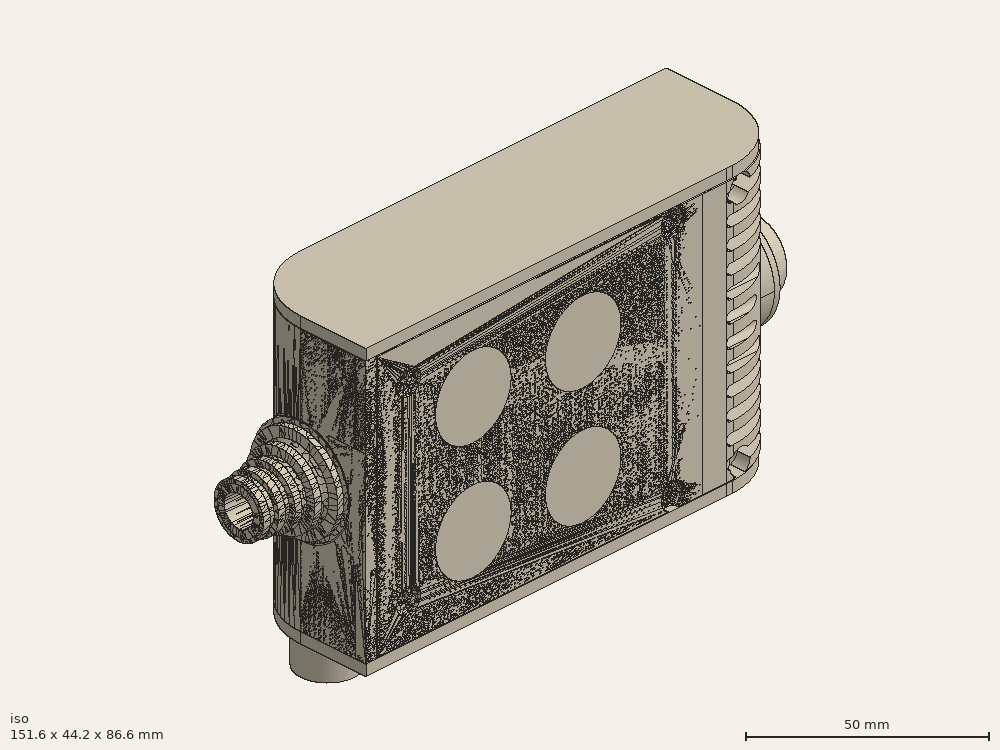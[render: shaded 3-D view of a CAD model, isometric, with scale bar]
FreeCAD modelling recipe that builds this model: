
FCSTD DOCUMENT  (FreeCAD 0.19R0.19.2)
Label: enclosure_208FCStd
License: All rights reserved
LicenseURL: http://en.wikipedia.org/wiki/All_rights_reserved
objects: Part::Revolution×152, Part::MultiFuse×146, Part::Feature×146, Sketcher::SketchObject×84, Part::Cut×71, Part::Cylinder×70, Part::Extrusion×69, Part::Fillet×58, Part::Box×36, App::MeasureDistance×4, Part::FeaturePython×2, Image::ImagePlane×1, PartDesign::Body×1, Part::Mirroring×1
note: 836 computed .brp shape members not serialized (recipe doc carries the construction recipe); baked Part::Feature solids carry a one-line shape summary decoded from their .brp

FEATURE [Sketcher::SketchObject] Sketch  label="topSketch"
  FullyConstrained = true
  sketch-geometry (20):
    g0: LineSegment StartX=5.21097e-06 StartY=3 StartZ=0 EndX=5.21097e-06 EndY=19 EndZ=0
    g1: ArcOfCircle CenterX=19 CenterY=19 CenterZ=0 NormalX=0 NormalY=0 NormalZ=1 AngleXU=0 Radius=19 StartAngle=1.5708 EndAngle=3.14159
    g2: ArcOfCircle CenterX=19 CenterY=19 CenterZ=0 NormalX=0 NormalY=0 NormalZ=1 AngleXU=0 Radius=16 StartAngle=1.5708 EndAngle=3.14159
    g3: LineSegment StartX=114 StartY=35 StartZ=0 EndX=19 EndY=35 EndZ=0
    g4: LineSegment StartX=5.21097e-06 StartY=3 StartZ=0 EndX=5.21097e-06 EndY=0 EndZ=0
    g5: LineSegment StartX=3 StartY=0 StartZ=0 EndX=5.21097e-06 EndY=0 EndZ=0
    g6: LineSegment StartX=3 StartY=19 StartZ=0 EndX=3 EndY=0 EndZ=0
    g7: LineSegment StartX=19 StartY=38 StartZ=0 EndX=124 EndY=38 EndZ=0
    g8: Circle CenterX=119 CenterY=35 CenterZ=0 NormalX=0 NormalY=0 NormalZ=1 AngleXU=0 Radius=1
    g9: Circle CenterX=121 CenterY=35 CenterZ=0 NormalX=0 NormalY=0 NormalZ=1 AngleXU=0 Radius=1
    g10: Circle CenterX=121 CenterY=33 CenterZ=0 NormalX=0 NormalY=0 NormalZ=1 AngleXU=0 Radius=1
    g11: BSplineCurve PolesCount=3 KnotsCount=2 Degree=2 IsPeriodic=0
    g12: GeomPoint X=119 Y=35 Z=0
    g13: GeomPoint X=121 Y=33 Z=0
    g14: LineSegment StartX=119 StartY=35 StartZ=0 EndX=114 EndY=35 EndZ=0
    g15: ArcOfCircle CenterX=105 CenterY=19 CenterZ=0 NormalX=0 NormalY=0 NormalZ=1 AngleXU=0 Radius=19 StartAngle=5.7297 EndAngle=6.28319
    g16: ArcOfCircle CenterX=105 CenterY=19 CenterZ=0 NormalX=0 NormalY=0 NormalZ=1 AngleXU=0 Radius=16 StartAngle=5.60905 EndAngle=6.28319
    g17: LineSegment StartX=121 StartY=33 StartZ=0 EndX=121 EndY=19 EndZ=0
    g18: LineSegment StartX=124 StartY=38 StartZ=0 EndX=124 EndY=19 EndZ=0
    g19: LineSegment StartX=117.5 StartY=9.01251 StartZ=0 EndX=121.163 EndY=9.0125 EndZ=0
  constraints (46):
    c: Vertical(g0)
    c: Block(g0)
    c: Coincident(g1,g0)
    c: Block(g1)
    c: Coincident(g2,g1)
    c: Block(g2)
    c: Coincident(g3,g2)
    c: Horizontal(g3)
    c: Tangent(g3,g2)
    c: Coincident(g4,g0)
    c: Distance(g4) = 3
    c: Vertical(g4)
    c: Coincident(g5,g4)
    c: Horizontal(g5)
    c: Coincident(g6,g2)
    c: Coincident(g6,g5)
    c: Vertical(g6)
    c: Horizontal(g7)
    c: Distance(g7) = 105
    c: Coincident(g7,g1)
    c: Block(g3)
    c: Weight(g8) = 1
    c: Equal(g8,g9)
    c: Equal(g8,g10)
    c: InternalAlignment(g8,g11)
    c: InternalAlignment(g9,g11)
    c: InternalAlignment(g10,g11)
    c: InternalAlignment(g12,g11)
    c: InternalAlignment(g13,g11)
    c: Block(g11)
    c: Coincident(g14,g11)
    c: Coincident(g14,g3)
    c: Horizontal(g14)
    c: Block(g15)
    c: Coincident(g16,g15)
    c: Block(g16)
    c: Coincident(g17,g11)
    c: Coincident(g17,g16)
    c: Vertical(g17)
    c: Distance(g17) = 14
    c: Coincident(g18,g7)
    c: Coincident(g18,g15)
    c: Vertical(g18)
    c: Distance(g18) = 19
    c: Coincident(g19,g16)
    c: Coincident(g19,g15)
FEATURE [Sketcher::SketchObject] Sketch001  label="bottomSketch"
  FullyConstrained = true
  sketch-geometry (32):
    g0: LineSegment StartX=3.3 StartY=-6.03275e-07 StartZ=0 EndX=98 EndY=-6.03275e-07 EndZ=0
    g1: ArcOfCircle CenterX=98 CenterY=19 CenterZ=0 NormalX=0 NormalY=0 NormalZ=1 AngleXU=0 Radius=19 StartAngle=4.71239 EndAngle=5.71103
    g2: LineSegment StartX=6.3 StartY=8 StartZ=0 EndX=3.3 EndY=8 EndZ=0
    g3: LineSegment StartX=3.3 StartY=8 StartZ=0 EndX=3.3 EndY=-6.03275e-07 EndZ=0
    g4: ArcOfCircle CenterX=8.3 CenterY=5 CenterZ=0 NormalX=0 NormalY=0 NormalZ=1 AngleXU=0 Radius=2 StartAngle=3.14159 EndAngle=4.71239
    g5: LineSegment StartX=6.3 StartY=8 StartZ=0 EndX=6.3 EndY=5 EndZ=0
    g6: ArcOfCircle CenterX=98 CenterY=19 CenterZ=0 NormalX=0 NormalY=0 NormalZ=1 AngleXU=0 Radius=12.7 StartAngle=4.71239 EndAngle=6.28319
    g7: LineSegment StartX=94.7 StartY=3 StartZ=0 EndX=8.3 EndY=3 EndZ=0
    g8-g12: Circle x5 (B-spline internal-alignment scaffolding for g13; pole/knot coordinates omitted)
    g13: BSplineCurve PolesCount=5 KnotsCount=3 Degree=3 IsPeriodic=0
    g14: GeomPoint X=98 Y=6.3 Z=0
    g15: GeomPoint X=96.3938 Y=4.71946 Z=0
    g16: GeomPoint X=94.7 Y=3 Z=0
    g17-g23: Circle x7 (B-spline internal-alignment scaffolding for g24; pole/knot coordinates omitted)
    g24: BSplineCurve PolesCount=7 KnotsCount=5 Degree=3 IsPeriodic=0
    g25-g29: GeomPoint x5 (B-spline internal-alignment scaffolding for g24; pole/knot coordinates omitted)
    g30: ArcOfCircle CenterX=98 CenterY=19 CenterZ=0 NormalX=0 NormalY=0 NormalZ=1 AngleXU=0 Radius=15.7 StartAngle=5.81226 EndAngle=6.28319
    g31: LineSegment StartX=110.7 StartY=19 StartZ=0 EndX=113.7 EndY=19 EndZ=0
  constraints (41):
    c: Horizontal(g0)
    c: Coincident(g1,g0)
    c: Block(g1)
    c: Horizontal(g2)
    c: Distance(g2) = 3
    c: Coincident(g3,g2)
    c: Vertical(g3)
    c: Coincident(g3,g0)
    c: Block(g4)
    c: Block(g2)
    c: Coincident(g5,g2)
    c: Coincident(g5,g4)
    c: Vertical(g5)
    c: Coincident(g6,g1)
    c: Block(g6)
    c: Coincident(g7,g4)
    c: Horizontal(g7)
    c: Block(g0)
    c: Block(g7)
    c: Block(g3)
    c: Coincident(g13,g6)
    c: Weight(g8) = 1
    c: Equal(g8, g9-g12) x4
    c: Coincident(g13,g7)
    c: InternalAlignment(g8-g12 -> g13) x5
    c: InternalAlignment(g14,g13)
    c: InternalAlignment(g15,g13)
    c: InternalAlignment(g16,g13)
    c: Block(g13)
    c: Weight(g17) = 1
    c: Equal(g17, g18-g23) x6
    c: Coincident(g24,g1)
    c: InternalAlignment(g17-g23 -> g24) x7
    c: InternalAlignment(g25-g29 -> g24) x5
    c: Block(g24)
    c: Coincident(g30,g24)
    c: Coincident(g31,g6)
    c: Coincident(g31,g30)
    c: Horizontal(g31)
    c: Block(g31)
    c: Block(g30)
FEATURE [Part::Extrusion] Extrude  label="top"
  Base = -> Sketch
  Dir = (0,0,1)
  DirMode = 2
  FaceMakerClass = Part::FaceMakerBullseye
  LengthFwd = 72
  LengthRev = 0
  Solid = true
  Symmetric = false
FEATURE [Part::Extrusion] Extrude001  label="bottom"
  Base = -> Sketch001
  Dir = (0,0,1)
  DirMode = 2
  FaceMakerClass = Part::FaceMakerBullseye
  LengthFwd = 71.4
  LengthRev = 0
  Placement = pos=(0,0,0.3) rot=(0,0,1;0rad)
  Solid = true
  Symmetric = false
FEATURE [Sketcher::SketchObject] Sketch002  label="topSketch001"
  FullyConstrained = true
  sketch-geometry (8):
    g0: ArcOfCircle CenterX=19 CenterY=19.0975 CenterZ=0 NormalX=0 NormalY=0 NormalZ=1 AngleXU=0 Radius=18.9025 StartAngle=1.5708 EndAngle=3.14674
    g1: LineSegment StartX=0.0977805 StartY=19.0003 StartZ=0 EndX=0.0977805 EndY=0.000251602 EndZ=0
    g2: LineSegment StartX=19 StartY=38 StartZ=0 EndX=124 EndY=38 EndZ=0
    g3: LineSegment StartX=0.0977805 StartY=0.000251602 StartZ=0 EndX=105.098 EndY=0.000251602 EndZ=0
    g4: LineSegment StartX=124 StartY=38 StartZ=0 EndX=125.616 EndY=38 EndZ=0
    g5: LineSegment StartX=105.098 StartY=0.000251602 StartZ=0 EndX=106.713 EndY=0.000251602 EndZ=0
    g6: ArcOfCircle CenterX=106.616 CenterY=19 CenterZ=0 NormalX=0 NormalY=0 NormalZ=1 AngleXU=0 Radius=19 StartAngle=4.71754 EndAngle=6.28319
    g7: LineSegment StartX=125.616 StartY=38 StartZ=0 EndX=125.616 EndY=19 EndZ=0
  constraints (21):
    c: Block(g0)
    c: Coincident(g1,g0)
    c: Vertical(g1)
    c: Horizontal(g2)
    c: Distance(g2) = 105
    c: Coincident(g2,g0)
    c: Distance(g1) = 19
    c: Coincident(g3,g1)
    c: Horizontal(g3)
    c: Distance(g3) = 105
    c: Coincident(g4,g2)
    c: Horizontal(g4)
    c: Distance(g4) = 1.61553
    c: Horizontal(g5)
    c: Equal(g4,g5) = 1.61553
    c: Coincident(g5,g3)
    c: Block(g6)
    c: Coincident(g6,g5)
    c: Coincident(g7,g4)
    c: Coincident(g7,g6)
    c: Vertical(g7)
FEATURE [Part::Extrusion] Extrude002  label="sideA"
  Base = -> Sketch002
  Dir = (0,0,1)
  DirMode = 2
  FaceMakerClass = Part::FaceMakerBullseye
  LengthFwd = 3
  LengthRev = 0
  Placement = pos=(0,0,-3) rot=(0,0,1;0rad)
  Solid = true
  Symmetric = false
FEATURE [Sketcher::SketchObject] Sketch003  label="topSketch002"
  FullyConstrained = true
  sketch-geometry (6):
    g0: LineSegment StartX=19 StartY=38 StartZ=0 EndX=117 EndY=38 EndZ=0
    g1: ArcOfCircle CenterX=19 CenterY=19 CenterZ=0 NormalX=0 NormalY=0 NormalZ=1 AngleXU=0 Radius=19 StartAngle=1.5708 EndAngle=3.14159
    g2: LineSegment StartX=117 StartY=38 StartZ=0 EndX=117 EndY=19 EndZ=0
    g3: LineSegment StartX=98 StartY=1.0161e-12 StartZ=0 EndX=5.22862e-06 EndY=1.0161e-12 EndZ=0
    g4: LineSegment StartX=5.22862e-06 StartY=19 StartZ=0 EndX=5.22862e-06 EndY=1.0161e-12 EndZ=0
    g5: ArcOfCircle CenterX=98 CenterY=19 CenterZ=0 NormalX=0 NormalY=0 NormalZ=1 AngleXU=0 Radius=19 StartAngle=4.71239 EndAngle=6.28319
  constraints (16):
    c: Horizontal(g0)
    c: Distance(g0) = 98
    c: Coincident(g1,g0)
    c: Block(g1)
    c: Coincident(g2,g0)
    c: Vertical(g2)
    c: Distance(g2) = 19
    c: Horizontal(g3)
    c: Coincident(g4,g1)
    c: Vertical(g4)
    c: Coincident(g3,g4)
    c: Block(g3)
    c: Coincident(g5,g2)
    c: Coincident(g5,g3)
    c: Block(g0)
    c: Block(g5)
FEATURE [Sketcher::SketchObject] Sketch004
  FullyConstrained = true
  MapMode = 3
  Placement = pos=(0,0,0) rot=(1,0,0;1.5708rad)
  Support = -> [Extrude]
  sketch-geometry (8):
    g0: Circle CenterX=80.351 CenterY=-67.6202 CenterZ=0 NormalX=0 NormalY=0 NormalZ=1 AngleXU=0 Radius=2
    g1: Circle CenterX=80.351 CenterY=-67.6202 CenterZ=0 NormalX=0 NormalY=0 NormalZ=1 AngleXU=0 Radius=3
    g2: Circle CenterX=80.351 CenterY=-4.92017 CenterZ=0 NormalX=0 NormalY=0 NormalZ=1 AngleXU=0 Radius=2
    g3: Circle CenterX=80.351 CenterY=-4.92017 CenterZ=0 NormalX=0 NormalY=0 NormalZ=1 AngleXU=0 Radius=3
    g4: Circle CenterX=23.851 CenterY=-4.92017 CenterZ=0 NormalX=0 NormalY=0 NormalZ=1 AngleXU=0 Radius=2
    g5: Circle CenterX=23.851 CenterY=-4.92017 CenterZ=0 NormalX=0 NormalY=0 NormalZ=1 AngleXU=0 Radius=3
    g6: Circle CenterX=23.851 CenterY=-67.6202 CenterZ=0 NormalX=0 NormalY=0 NormalZ=1 AngleXU=0 Radius=2
    g7: Circle CenterX=23.851 CenterY=-67.6202 CenterZ=0 NormalX=0 NormalY=0 NormalZ=1 AngleXU=0 Radius=3
  constraints (8):
    c: Block(g3)
    c: Block(g2)
    c: Block(g1)
    c: Block(g0)
    c: Block(g6)
    c: Block(g7)
    c: Block(g4)
    c: Block(g5)
FEATURE [Part::Extrusion] Extrude004
  Base = -> Sketch004
  Dir = (0,-1,2e-16)
  DirMode = 2
  FaceMakerClass = Part::FaceMakerBullseye
  LengthFwd = 6
  LengthRev = 0
  Placement = pos=(0,9,0) rot=(0,0,1;0rad)
  Solid = true
  Symmetric = false
FEATURE [Sketcher::SketchObject] Sketch005
  FullyConstrained = true
  MapMode = 3
  Placement = pos=(0,0,0) rot=(1,0,0;1.5708rad)
  Support = -> [Extrude]
  sketch-geometry (8):
    g0: Circle CenterX=80.351 CenterY=-67.6202 CenterZ=0 NormalX=0 NormalY=0 NormalZ=1 AngleXU=0 Radius=3
    g1: Circle CenterX=80.351 CenterY=-4.92017 CenterZ=0 NormalX=0 NormalY=0 NormalZ=1 AngleXU=0 Radius=3
    g2: Circle CenterX=23.851 CenterY=-4.92017 CenterZ=0 NormalX=0 NormalY=0 NormalZ=1 AngleXU=0 Radius=3
    g3: Circle CenterX=23.851 CenterY=-67.6202 CenterZ=0 NormalX=0 NormalY=0 NormalZ=1 AngleXU=0 Radius=3
    g4: Circle CenterX=23.851 CenterY=-67.6202 CenterZ=0 NormalX=0 NormalY=0 NormalZ=1 AngleXU=0 Radius=5
    g5: Circle CenterX=80.351 CenterY=-67.6202 CenterZ=0 NormalX=0 NormalY=0 NormalZ=1 AngleXU=0 Radius=5
    g6: Circle CenterX=23.851 CenterY=-4.92017 CenterZ=0 NormalX=0 NormalY=0 NormalZ=1 AngleXU=0 Radius=5
    g7: Circle CenterX=80.351 CenterY=-4.92017 CenterZ=0 NormalX=0 NormalY=0 NormalZ=1 AngleXU=0 Radius=5
  constraints (8):
    c: Block(g1)
    c: Block(g0)
    c: Block(g3)
    c: Block(g2)
    c: Block(g5)
    c: Block(g4)
    c: Block(g6)
    c: Block(g7)
FEATURE [Part::Extrusion] Extrude005
  Base = -> Sketch005
  Dir = (0,-1,2e-16)
  DirMode = 2
  FaceMakerClass = Part::FaceMakerBullseye
  LengthFwd = 2
  LengthRev = 0
  Solid = true
  Symmetric = false
FEATURE [Sketcher::SketchObject] Sketch006
  FullyConstrained = true
  MapMode = 3
  Placement = pos=(0,0,0) rot=(1,0,0;1.5708rad)
  sketch-geometry (8):
    g0: Circle CenterX=80.351 CenterY=-67.6202 CenterZ=0 NormalX=0 NormalY=0 NormalZ=1 AngleXU=0 Radius=3
    g1: Circle CenterX=80.351 CenterY=-4.92017 CenterZ=0 NormalX=0 NormalY=0 NormalZ=1 AngleXU=0 Radius=3
    g2: Circle CenterX=23.851 CenterY=-4.92017 CenterZ=0 NormalX=0 NormalY=0 NormalZ=1 AngleXU=0 Radius=3
    g3: Circle CenterX=23.851 CenterY=-67.6202 CenterZ=0 NormalX=0 NormalY=0 NormalZ=1 AngleXU=0 Radius=3
    g4: Circle CenterX=23.851 CenterY=-67.6202 CenterZ=0 NormalX=0 NormalY=0 NormalZ=1 AngleXU=0 Radius=5
    g5: Circle CenterX=80.351 CenterY=-67.6202 CenterZ=0 NormalX=0 NormalY=0 NormalZ=1 AngleXU=0 Radius=5
    g6: Circle CenterX=23.851 CenterY=-4.92017 CenterZ=0 NormalX=0 NormalY=0 NormalZ=1 AngleXU=0 Radius=5
    g7: Circle CenterX=80.351 CenterY=-4.92017 CenterZ=0 NormalX=0 NormalY=0 NormalZ=1 AngleXU=0 Radius=5
  constraints (8):
    c: Block(g1)
    c: Block(g0)
    c: Block(g3)
    c: Block(g2)
    c: Block(g5)
    c: Block(g4)
    c: Block(g6)
    c: Block(g7)
FEATURE [Part::Extrusion] Extrude007
  Base = -> Sketch006
  Dir = (0,-1,2e-16)
  DirMode = 2
  FaceMakerClass = Part::FaceMakerBullseye
  LengthFwd = 2
  LengthRev = 0
  Solid = true
  Symmetric = false
FEATURE [Part::Fillet] Fillet
  Base = -> Extrude007
  Edges = 4 edges r=1.99: [Edge6,Edge12,Edge18,Edge24]
FEATURE [Part::Cut] Cut
  Base = -> Extrude005
  Placement = pos=(0,5,0) rot=(0,0,1;0rad)
  Tool = -> Fillet
FEATURE [Part::MultiFuse] Fusion  label="pCBScrews"
  Placement = pos=(-2.5,0,72.3) rot=(0,0,1;0rad)
  Shapes = -> [Extrude004,Cut]
FEATURE [App::MeasureDistance] Distance  label="Distance: 0.69 mm"
  Distance = 0.685967
  P1 = (24.0138,2.9647,0.3)
  P2 = (23.8901,3,-0.373787)
FEATURE [App::MeasureDistance] Distance001  label="Distance: 0.53 mm"
  Distance = 0.533607
  P1 = (80.2939,3,72.2334)
  P2 = (80.281,2.99661,71.7)
FEATURE [Part::Fillet] Fillet001
  Base = -> Extrude001
  Edges = 1 edges r=2.4: [Edge17]
FEATURE [Part::Fillet] Fillet002  label="bottom001"
  Base = -> Fillet001
  Edges = 1 edges r=2.4: [Edge36]
FEATURE [Part::Fillet] Fillet003  label="top001"
  Base = -> Extrude
  Edges = 1 edges r=2: [Edge1]
FEATURE [Sketcher::SketchObject] Sketch007
  FullyConstrained = true
  sketch-geometry (16):
    g0: LineSegment StartX=4 StartY=0 StartZ=0 EndX=4 EndY=2.4 EndZ=0
    g1: LineSegment StartX=4 StartY=2.4 StartZ=0 EndX=7 EndY=2.4 EndZ=0
    g2: LineSegment StartX=4 StartY=0 StartZ=0 EndX=5.7 EndY=0 EndZ=0
    g3: LineSegment StartX=5.7 StartY=0 StartZ=0 EndX=5.7 EndY=-5.6 EndZ=0
    g4-g8: Circle x5 (B-spline internal-alignment scaffolding for g9; pole/knot coordinates omitted)
    g9: BSplineCurve PolesCount=5 KnotsCount=3 Degree=3 IsPeriodic=0
    g10: GeomPoint X=7 Y=2.4 Z=0
    g11: GeomPoint X=10.4582 Y=-1.55472 Z=0
    g12: GeomPoint X=14 Y=-5.6 Z=0
    g13: LineSegment StartX=14 StartY=-5.6 StartZ=0 EndX=14 EndY=-14.1 EndZ=0
    g14: LineSegment StartX=14 StartY=-14.1 StartZ=0 EndX=6.5 EndY=-14.1 EndZ=0
    g15: LineSegment StartX=5.7 StartY=-5.6 StartZ=0 EndX=6.5 EndY=-14.1 EndZ=0
  constraints (28):
    c: Distance(g0) = 2.4
    c: Vertical(g0)
    c: Block(g0)
    c: Coincident(g1,g0)
    c: Horizontal(g1)
    c: Distance(g1) = 3
    c: Coincident(g2,g0)
    c: Horizontal(g2)
    c: Distance(g2) = 1.7
    c: Coincident(g3,g2)
    c: Vertical(g3)
    c: Distance(g3) = 5.6
    c: Coincident(g9,g1)
    c: Weight(g4) = 1
    c: Equal(g4, g5-g8) x4
    c: InternalAlignment(g4-g8 -> g9) x5
    c: InternalAlignment(g10,g9)
    c: InternalAlignment(g11,g9)
    c: InternalAlignment(g12,g9)
    c: Block(g9)
    c: Coincident(g13,g9)
    c: Vertical(g13)
    c: Distance(g13) = 8.5
    c: Coincident(g14,g13)
    c: Horizontal(g14)
    c: Distance(g14) = 7.5
    c: Coincident(g15,g3)
    c: Coincident(g15,g14)
FEATURE [Part::Feature] Face
  shape: bbox 10 x 16.5 x 2e-07 mm, 1 faces, 0 solids (baked)
FEATURE [Part::Revolution] Revolve  label="plugHousing"
  Angle = 360
  Axis = (0,1,0)
  Base = (0,0,0)
  FaceMakerClass = Part::FaceMakerBullseye
  Placement = pos=(0,0,36.15) rot=(0,0,1;0rad)
  Solid = false
  Source = -> Face
  Symmetric = false
FEATURE [Part::Feature] Face001
  shape: bbox 10 x 16.5 x 2e-07 mm, 1 faces, 0 solids (baked)
FEATURE [Part::Revolution] Revolve001  label="plugHousing001"
  Angle = 360
  Axis = (0,1,0)
  Base = (0,0,0)
  FaceMakerClass = Part::FaceMakerBullseye
  Placement = pos=(0,0,36.15) rot=(0,0,1;0rad)
  Solid = false
  Source = -> Face001
  Symmetric = false
FEATURE [Part::MultiFuse] Fusion001  label="plugHousing002"
  Placement = pos=(0,0,0) rot=(0,0,1;1.5708rad)
  Shapes = -> [Revolve001,Revolve]
FEATURE [Part::Feature] Face002
  shape: bbox 10 x 16.5 x 2e-07 mm, 1 faces, 0 solids (baked)
FEATURE [Part::Revolution] Revolve003  label="plugHousing005"
  Angle = 360
  Axis = (0,1,0)
  Base = (0,0,0)
  FaceMakerClass = Part::FaceMakerBullseye
  Placement = pos=(0,0,36.15) rot=(0,0,1;0rad)
  Solid = false
  Source = -> Face002
  Symmetric = false
FEATURE [Part::Feature] Face003
  shape: bbox 10 x 16.5 x 2e-07 mm, 1 faces, 0 solids (baked)
FEATURE [Part::Revolution] Revolve002  label="plugHousing003"
  Angle = 360
  Axis = (0,1,0)
  Base = (0,0,0)
  FaceMakerClass = Part::FaceMakerBullseye
  Placement = pos=(0,0,36.15) rot=(0,0,1;0rad)
  Solid = false
  Source = -> Face003
  Symmetric = false
FEATURE [Part::MultiFuse] Fusion002  label="plugHousing004"
  Placement = pos=(0,0,0) rot=(0,0,1;1.5708rad)
  Shapes = -> [Revolve002,Revolve003]
FEATURE [Part::MultiFuse] Fusion003  label="plugHousing006"
  Placement = pos=(0,19,0) rot=(0,0,1;3.14159rad)
  Shapes = -> [Fusion002,Fusion001]
FEATURE [Part::Feature] Face004
  shape: bbox 10 x 16.5 x 2e-07 mm, 1 faces, 0 solids (baked)
FEATURE [Part::Revolution] Revolve006  label="plugHousing010"
  Angle = 360
  Axis = (0,1,0)
  Base = (0,0,0)
  FaceMakerClass = Part::FaceMakerBullseye
  Placement = pos=(0,0,36.15) rot=(0,0,1;0rad)
  Solid = false
  Source = -> Face004
  Symmetric = false
FEATURE [Part::Feature] Face005
  shape: bbox 10 x 16.5 x 2e-07 mm, 1 faces, 0 solids (baked)
FEATURE [Part::Revolution] Revolve007  label="plugHousing011"
  Angle = 360
  Axis = (0,1,0)
  Base = (0,0,0)
  FaceMakerClass = Part::FaceMakerBullseye
  Placement = pos=(0,0,36.15) rot=(0,0,1;0rad)
  Solid = false
  Source = -> Face005
  Symmetric = false
FEATURE [Part::Feature] Face006
  shape: bbox 10 x 16.5 x 2e-07 mm, 1 faces, 0 solids (baked)
FEATURE [Part::Revolution] Revolve004  label="plugHousing007"
  Angle = 360
  Axis = (0,1,0)
  Base = (0,0,0)
  FaceMakerClass = Part::FaceMakerBullseye
  Placement = pos=(0,0,36.15) rot=(0,0,1;0rad)
  Solid = false
  Source = -> Face006
  Symmetric = false
FEATURE [Part::MultiFuse] Fusion004  label="plugHousing009"
  Placement = pos=(0,0,0) rot=(0,0,1;1.5708rad)
  Shapes = -> [Revolve004,Revolve007]
FEATURE [Part::Feature] Face007
  shape: bbox 10 x 16.5 x 2e-07 mm, 1 faces, 0 solids (baked)
FEATURE [Part::Revolution] Revolve005  label="plugHousing008"
  Angle = 360
  Axis = (0,1,0)
  Base = (0,0,0)
  FaceMakerClass = Part::FaceMakerBullseye
  Placement = pos=(0,0,36.15) rot=(0,0,1;0rad)
  Solid = false
  Source = -> Face007
  Symmetric = false
FEATURE [Part::MultiFuse] Fusion005  label="plugHousing012"
  Placement = pos=(0,0,0) rot=(0,0,1;1.5708rad)
  Shapes = -> [Revolve006,Revolve005]
FEATURE [Part::MultiFuse] Fusion006  label="plugHousing013"
  Placement = pos=(0,19,0) rot=(0,0,1;3.14159rad)
  Shapes = -> [Fusion005,Fusion004]
FEATURE [Part::MultiFuse] Fusion007  label="plugHousing014"
  Placement = pos=(122.621,0,-0.15) rot=(0,0,1;0rad)
  Shapes = -> [Fusion003,Fusion006]
FEATURE [Part::Cylinder] Cylinder002
  Angle = 360
  AttacherType = Attacher::AttachEngine3D
  Height = 20
  Placement = pos=(0,0,36.15) rot=(0,0,1;0rad)
  Radius = 4
FEATURE [Part::Cylinder] Cylinder003
  Angle = 360
  AttacherType = Attacher::AttachEngine3D
  Height = 10
  Placement = pos=(0,0,36.15) rot=(0,0,1;0rad)
  Radius = 4
FEATURE [Part::MultiFuse] Fusion009  label="removeToCreateHoleForPlugHousing"
  Placement = pos=(70,19,36.15) rot=(0,1,0;1.5708rad)
  Shapes = -> [Cylinder002,Cylinder003]
FEATURE [Part::Cylinder] Cylinder004
  Angle = 360
  AttacherType = Attacher::AttachEngine3D
  Height = 20
  Placement = pos=(0,0,36.15) rot=(0,0,1;0rad)
  Radius = 4
FEATURE [Part::Cylinder] Cylinder005
  Angle = 360
  AttacherType = Attacher::AttachEngine3D
  Height = 10
  Placement = pos=(0,0,36.15) rot=(0,0,1;0rad)
  Radius = 4
FEATURE [Part::MultiFuse] Fusion010  label="removeToCreateHoleForPlugHousing001"
  Placement = pos=(70,19,36.15) rot=(0,1,0;1.5708rad)
  Shapes = -> [Cylinder004,Cylinder005]
FEATURE [Part::Cut] Cut001
  Base = -> Fillet003
  Tool = -> Fusion010
FEATURE [Part::Cut] Cut002  label="Bottom"
  Base = -> Fillet002
  Tool = -> Fusion009
FEATURE [Part::Feature] Face008
  shape: bbox 10 x 16.5 x 2e-07 mm, 1 faces, 0 solids (baked)
FEATURE [Part::Revolution] Revolve011  label="plugHousing021"
  Angle = 360
  Axis = (0,1,0)
  Base = (0,0,0)
  FaceMakerClass = Part::FaceMakerBullseye
  Placement = pos=(0,0,36.15) rot=(0,0,1;0rad)
  Solid = false
  Source = -> Face008
  Symmetric = false
FEATURE [Part::Feature] Face009
  shape: bbox 10 x 16.5 x 2e-07 mm, 1 faces, 0 solids (baked)
FEATURE [Part::Revolution] Revolve012  label="plugHousing022"
  Angle = 360
  Axis = (0,1,0)
  Base = (0,0,0)
  FaceMakerClass = Part::FaceMakerBullseye
  Placement = pos=(0,0,36.15) rot=(0,0,1;0rad)
  Solid = false
  Source = -> Face009
  Symmetric = false
FEATURE [Part::Feature] Face010 .. Face013  x4 (patterned run collapsed; names and placements below)
  shape: bbox 10 x 16.5 x 2e-07 mm, 1 faces, 0 solids (baked)
FEATURE [Part::Revolution] Revolve015  label="plugHousing027"
  Angle = 360
  Axis = (0,1,0)
  Base = (0,0,0)
  FaceMakerClass = Part::FaceMakerBullseye
  Placement = pos=(0,0,36.15) rot=(0,0,1;0rad)
  Solid = false
  Source = -> Face013
  Symmetric = false
FEATURE [Part::Feature] Face014
  shape: bbox 10 x 16.5 x 2e-07 mm, 1 faces, 0 solids (baked)
FEATURE [Part::Feature] Face015
  shape: bbox 10 x 16.5 x 2e-07 mm, 1 faces, 0 solids (baked)
FEATURE [Part::Feature] Face016
  shape: bbox 10 x 16.5 x 2e-07 mm, 1 faces, 0 solids (baked)
FEATURE [Part::Revolution] Revolve019  label="plugHousing033"
  Angle = 360
  Axis = (0,1,0)
  Base = (0,0,0)
  FaceMakerClass = Part::FaceMakerBullseye
  Placement = pos=(0,0,36.15) rot=(0,0,1;0rad)
  Solid = false
  Source = -> Face016
  Symmetric = false
FEATURE [Part::Feature] Face017
  shape: bbox 10 x 16.5 x 2e-07 mm, 1 faces, 0 solids (baked)
FEATURE [Part::Revolution] Revolve020  label="plugHousing034"
  Angle = 360
  Axis = (0,1,0)
  Base = (0,0,0)
  FaceMakerClass = Part::FaceMakerBullseye
  Placement = pos=(0,0,36.15) rot=(0,0,1;0rad)
  Solid = false
  Source = -> Face017
  Symmetric = false
FEATURE [Part::Feature] Face018
  shape: bbox 10 x 16.5 x 2e-07 mm, 1 faces, 0 solids (baked)
FEATURE [Part::Revolution] Revolve016  label="plugHousing030"
  Angle = 360
  Axis = (0,1,0)
  Base = (0,0,0)
  FaceMakerClass = Part::FaceMakerBullseye
  Placement = pos=(0,0,36.15) rot=(0,0,1;0rad)
  Solid = false
  Source = -> Face018
  Symmetric = false
FEATURE [Part::MultiFuse] Fusion020  label="plugHousing038"
  Placement = pos=(0,0,0) rot=(0,0,1;1.5708rad)
  Shapes = -> [Revolve016,Revolve020]
FEATURE [Part::Feature] Face019
  shape: bbox 10 x 16.5 x 2e-07 mm, 1 faces, 0 solids (baked)
FEATURE [Part::Feature] Face020
  shape: bbox 10 x 16.5 x 2e-07 mm, 1 faces, 0 solids (baked)
FEATURE [Part::Revolution] Revolve017  label="plugHousing031"
  Angle = 360
  Axis = (0,1,0)
  Base = (0,0,0)
  FaceMakerClass = Part::FaceMakerBullseye
  Placement = pos=(0,0,36.15) rot=(0,0,1;0rad)
  Solid = false
  Source = -> Face020
  Symmetric = false
FEATURE [Part::MultiFuse] Fusion021  label="plugHousing039"
  Placement = pos=(0,0,0) rot=(0,0,1;1.5708rad)
  Shapes = -> [Revolve019,Revolve017]
FEATURE [Part::MultiFuse] Fusion023  label="plugHousing041"
  Placement = pos=(0,19,0) rot=(0,0,1;3.14159rad)
  Shapes = -> [Fusion021,Fusion020]
FEATURE [Part::Revolution] Revolve022  label="plugHousing043"
  Angle = 360
  Axis = (0,1,0)
  Base = (0,0,0)
  FaceMakerClass = Part::FaceMakerBullseye
  Placement = pos=(0,0,36.15) rot=(0,0,1;0rad)
  Solid = false
  Source = -> Face019
  Symmetric = false
FEATURE [Part::Feature] Face021
  shape: bbox 10 x 16.5 x 2e-07 mm, 1 faces, 0 solids (baked)
FEATURE [Part::Revolution] Revolve023  label="plugHousing044"
  Angle = 360
  Axis = (0,1,0)
  Base = (0,0,0)
  FaceMakerClass = Part::FaceMakerBullseye
  Placement = pos=(0,0,36.15) rot=(0,0,1;0rad)
  Solid = false
  Source = -> Face021
  Symmetric = false
FEATURE [Part::Feature] Face022
  shape: bbox 10 x 16.5 x 2e-07 mm, 1 faces, 0 solids (baked)
FEATURE [Part::Revolution] Revolve018  label="plugHousing032"
  Angle = 360
  Axis = (0,1,0)
  Base = (0,0,0)
  FaceMakerClass = Part::FaceMakerBullseye
  Placement = pos=(0,0,36.15) rot=(0,0,1;0rad)
  Solid = false
  Source = -> Face022
  Symmetric = false
FEATURE [Part::MultiFuse] Fusion022  label="plugHousing040"
  Placement = pos=(0,0,0) rot=(0,0,1;1.5708rad)
  Shapes = -> [Revolve018,Revolve023]
FEATURE [Part::Feature] Face023
  shape: bbox 10 x 16.5 x 2e-07 mm, 1 faces, 0 solids (baked)
FEATURE [Part::Revolution] Revolve021  label="plugHousing035"
  Angle = 360
  Axis = (0,1,0)
  Base = (0,0,0)
  FaceMakerClass = Part::FaceMakerBullseye
  Placement = pos=(0,0,36.15) rot=(0,0,1;0rad)
  Solid = false
  Source = -> Face023
  Symmetric = false
FEATURE [Part::MultiFuse] Fusion018  label="plugHousing036"
  Placement = pos=(0,0,0) rot=(0,0,1;1.5708rad)
  Shapes = -> [Revolve022,Revolve021]
FEATURE [Part::MultiFuse] Fusion019  label="plugHousing037"
  Placement = pos=(0,19,0) rot=(0,0,1;3.14159rad)
  Shapes = -> [Fusion018,Fusion022]
FEATURE [Part::MultiFuse] Fusion024  label="plugHousing042"
  Placement = pos=(122.621,0,-0.15) rot=(0,0,1;0rad)
  Shapes = -> [Fusion023,Fusion019]
FEATURE [Part::Cylinder] Cylinder006
  Angle = 360
  AttacherType = Attacher::AttachEngine3D
  Height = 20
  Placement = pos=(0,0,36.15) rot=(0,0,1;0rad)
  Radius = 14.3
FEATURE [Part::Cylinder] Cylinder007
  Angle = 360
  AttacherType = Attacher::AttachEngine3D
  Height = 10
  Placement = pos=(0,0,36.15) rot=(0,0,1;0rad)
  Radius = 4
FEATURE [Part::MultiFuse] Fusion026  label="removeToCreteHoleForPlugHousing"
  Placement = pos=(70,19,36) rot=(0,1,0;1.5708rad)
  Shapes = -> [Cylinder006,Cylinder007]
FEATURE [Part::Box] Box001  label="Cube001"
  AttacherType = Attacher::AttachEngine3D
  Height = 28
  Length = 3
  Placement = pos=(110.7,19,22) rot=(0,0,1;0rad)
  Width = 15.7
FEATURE [Part::Cut] Cut003  label="top002"
  Base = -> Cut001
  Tool = -> Fusion007
FEATURE [Part::Revolution] Revolve008  label="plugHousing015"
  Angle = 360
  Axis = (0,1,0)
  Base = (0,0,0)
  FaceMakerClass = Part::FaceMakerBullseye
  Placement = pos=(0,0,36.15) rot=(0,0,1;0rad)
  Solid = false
  Source = -> Face010
  Symmetric = false
FEATURE [Part::MultiFuse] Fusion013  label="plugHousing020"
  Placement = pos=(0,0,0) rot=(0,0,1;1.5708rad)
  Shapes = -> [Revolve008,Revolve012]
FEATURE [Part::Cut] Cut004  label="top003"
  Base = -> Cut003
  Placement = pos=(1,0,0) rot=(0,0,1;0rad)
  Tool = -> Fusion026
FEATURE [Part::Cylinder] Cylinder008
  Angle = 360
  AttacherType = Attacher::AttachEngine3D
  Height = 20
  Placement = pos=(0,0,36.15) rot=(0,0,1;0rad)
  Radius = 10.3
FEATURE [Part::Cylinder] Cylinder009
  Angle = 360
  AttacherType = Attacher::AttachEngine3D
  Height = 10
  Placement = pos=(0,0,36.15) rot=(0,0,1;0rad)
  Radius = 4
FEATURE [Part::MultiFuse] Fusion027  label="removeToCreteHoleForPlugHousing001"
  Placement = pos=(70,19,36) rot=(0,1,0;1.5708rad)
  Shapes = -> [Cylinder008,Cylinder009]
FEATURE [Part::Cut] Cut005  label="plugHousingTab"
  Base = -> Box001
  Tool = -> Fusion027
FEATURE [Part::MultiFuse] Fusion028  label="plugHousing045"
  Shapes = -> [Fusion024,Cut005]
FEATURE [Part::Box] Box002  label="Cube002"
  AttacherType = Attacher::AttachEngine3D
  Height = 28.8
  Length = 3
  Placement = pos=(107.3,28,21.6) rot=(0,0,1;0rad)
  Width = 7
FEATURE [Part::Box] Box003  label="Cube003"
  AttacherType = Attacher::AttachEngine3D
  Height = 3
  Length = 6.4
  Placement = pos=(107.3,28,18.6) rot=(0,0,1;0rad)
  Width = 7
FEATURE [Part::Box] Box004  label="Cube004"
  AttacherType = Attacher::AttachEngine3D
  Height = 3
  Length = 6.4
  Placement = pos=(107.3,28,50.4) rot=(0,0,1;0rad)
  Width = 7
FEATURE [Part::MultiFuse] Fusion029  label="plugHousingBracketHolder"
  Shapes = -> [Box004,Box002,Box003]
FEATURE [Part::Cylinder] Cylinder010
  Angle = 360
  AttacherType = Attacher::AttachEngine3D
  Height = 20
  Placement = pos=(0,0,36.15) rot=(0,0,1;0rad)
  Radius = 14.3
FEATURE [Part::Cylinder] Cylinder011
  Angle = 360
  AttacherType = Attacher::AttachEngine3D
  Height = 10
  Placement = pos=(0,0,36.15) rot=(0,0,1;0rad)
  Radius = 4
FEATURE [Part::MultiFuse] Fusion030  label="removeToCreteHoleForPlugHousing002"
  Placement = pos=(70,19,36) rot=(0,1,0;1.5708rad)
  Shapes = -> [Cylinder010,Cylinder011]
FEATURE [Part::Cut] Cut006  label="plugHousingBracketHolder001"
  Base = -> Fusion029
  Tool = -> Fusion030
FEATURE [Part::Cylinder] Cylinder012
  Angle = 360
  AttacherType = Attacher::AttachEngine3D
  Height = 20
  Placement = pos=(0,0,36.15) rot=(0,0,1;0rad)
  Radius = 7
FEATURE [Part::Cylinder] Cylinder013
  Angle = 360
  AttacherType = Attacher::AttachEngine3D
  Height = 10
  Placement = pos=(0,0,36.15) rot=(0,0,1;0rad)
  Radius = 4
FEATURE [Part::MultiFuse] Fusion032  label="removeToCreteHoleForPlugHousing003"
  Placement = pos=(70,19,36) rot=(0,1,0;1.5708rad)
  Shapes = -> [Cylinder012,Cylinder013]
FEATURE [Part::Cut] Cut007  label="bottom002"
  Base = -> Cut002
  Tool = -> Fusion032
FEATURE [Sketcher::SketchObject] Sketch008
  FullyConstrained = true
  sketch-geometry (54):
    g0: LineSegment StartX=-4.2 StartY=0 StartZ=0 EndX=-6.2 EndY=0 EndZ=0
    g1: LineSegment StartX=-14 StartY=-18 StartZ=0 EndX=-14 EndY=-26.5 EndZ=0
    g2: LineSegment StartX=-4.2 StartY=0 StartZ=0 EndX=-4.2 EndY=-13.4877 EndZ=0
    g3: Circle CenterX=-4.2 CenterY=-13.4877 CenterZ=0 NormalX=0 NormalY=0 NormalZ=1 AngleXU=0 Radius=1
    g4: Circle CenterX=-4.2 CenterY=-26.5 CenterZ=0 NormalX=0 NormalY=0 NormalZ=1 AngleXU=0 Radius=1
    g5: Circle CenterX=-8.2 CenterY=-26.5 CenterZ=0 NormalX=0 NormalY=0 NormalZ=1 AngleXU=0 Radius=1
    g6: BSplineCurve PolesCount=3 KnotsCount=2 Degree=2 IsPeriodic=0
    g7: GeomPoint X=-4.2 Y=-13.4877 Z=0
    g8: GeomPoint X=-8.2 Y=-26.5 Z=0
    g9: LineSegment StartX=-14 StartY=-26.5 StartZ=0 EndX=-8.2 EndY=-26.5 EndZ=0
    g10: LineSegment StartX=-10.15 StartY=-12 StartZ=0 EndX=-10.15 EndY=-14 EndZ=0
    g11: LineSegment StartX=-12.8401 StartY=-16 StartZ=0 EndX=-10.1571 EndY=-16 EndZ=0
    g12: LineSegment StartX=-10.15 StartY=-14 StartZ=0 EndX=-8.70761 EndY=-14 EndZ=0
    g13: LineSegment StartX=-12.8401 StartY=-16 StartZ=0 EndX=-12.8401 EndY=-17.6958 EndZ=0
    g14: LineSegment StartX=-10.15 StartY=-12 StartZ=0 EndX=-7.79258 EndY=-12 EndZ=0
    g15: Circle CenterX=-6.2215 CenterY=-2 CenterZ=0 NormalX=0 NormalY=0 NormalZ=1 AngleXU=0 Radius=1
    g16: Circle CenterX=-6.22762 CenterY=-2.58724 CenterZ=0 NormalX=0 NormalY=0 NormalZ=1 AngleXU=0 Radius=1
    g17: Circle CenterX=-6.32538 CenterY=-4 CenterZ=0 NormalX=0 NormalY=0 NormalZ=1 AngleXU=0 Radius=1
    g18: BSplineCurve PolesCount=3 KnotsCount=2 Degree=2 IsPeriodic=0
    g19: GeomPoint X=-6.2215 Y=-2 Z=0
    g20: GeomPoint X=-6.32538 Y=-4 Z=0
    g21: Circle CenterX=-6.48644 CenterY=-5.99526 CenterZ=0 NormalX=0 NormalY=0 NormalZ=1 AngleXU=0 Radius=1
    g22: Circle CenterX=-6.58486 CenterY=-6.99526 CenterZ=0 NormalX=0 NormalY=0 NormalZ=1 AngleXU=0 Radius=1
    g23: Circle CenterX=-6.77343 CenterY=-8 CenterZ=0 NormalX=0 NormalY=0 NormalZ=1 AngleXU=0 Radius=1
    g24: BSplineCurve PolesCount=3 KnotsCount=2 Degree=2 IsPeriodic=0
    g25: GeomPoint X=-6.48644 Y=-5.99526 Z=0
    g26: GeomPoint X=-6.77343 Y=-8 Z=0
    g27: Circle CenterX=-7.19003 CenterY=-10 CenterZ=0 NormalX=0 NormalY=0 NormalZ=1 AngleXU=0 Radius=1
    g28: Circle CenterX=-7.44407 CenterY=-11.0915 CenterZ=0 NormalX=0 NormalY=0 NormalZ=1 AngleXU=0 Radius=1
    g29: Circle CenterX=-7.79258 CenterY=-12 CenterZ=0 NormalX=0 NormalY=0 NormalZ=1 AngleXU=0 Radius=1
    g30: BSplineCurve PolesCount=3 KnotsCount=2 Degree=2 IsPeriodic=0
    g31: GeomPoint X=-7.19003 Y=-10 Z=0
    g32: GeomPoint X=-7.79258 Y=-12 Z=0
    g33: Circle CenterX=-8.70761 CenterY=-14 CenterZ=0 NormalX=0 NormalY=0 NormalZ=1 AngleXU=0 Radius=1
    g34: Circle CenterX=-9.33087 CenterY=-15.1837 CenterZ=0 NormalX=0 NormalY=0 NormalZ=1 AngleXU=0 Radius=1
    g35: Circle CenterX=-10.1571 CenterY=-16 CenterZ=0 NormalX=0 NormalY=0 NormalZ=1 AngleXU=0 Radius=1
    g36: BSplineCurve PolesCount=3 KnotsCount=2 Degree=2 IsPeriodic=0
    g37: GeomPoint X=-8.70761 Y=-14 Z=0
    g38: GeomPoint X=-10.1571 Y=-16 Z=0
    g39: Circle CenterX=-12.8401 CenterY=-17.6958 CenterZ=0 NormalX=0 NormalY=0 NormalZ=1 AngleXU=0 Radius=1
    g40: Circle CenterX=-13.3521 CenterY=-17.9027 CenterZ=0 NormalX=0 NormalY=0 NormalZ=1 AngleXU=0 Radius=1
    g41: Circle CenterX=-14 CenterY=-18 CenterZ=0 NormalX=0 NormalY=0 NormalZ=1 AngleXU=0 Radius=1
    g42: BSplineCurve PolesCount=3 KnotsCount=2 Degree=2 IsPeriodic=0
    g43: GeomPoint X=-12.8401 Y=-17.6958 Z=0
    g44: GeomPoint X=-14 Y=-18 Z=0
    g45: LineSegment StartX=-6.2 StartY=0 StartZ=0 EndX=-7.2 EndY=0 EndZ=0
    g46: LineSegment StartX=-7.2 StartY=0 StartZ=0 EndX=-7.2 EndY=-2 EndZ=0
    g47: LineSegment StartX=-7.2 StartY=-2 StartZ=0 EndX=-6.2215 EndY=-2 EndZ=0
    g48: LineSegment StartX=-6.32538 StartY=-4 StartZ=0 EndX=-7.65538 EndY=-4 EndZ=0
    g49: LineSegment StartX=-7.65538 StartY=-4 StartZ=0 EndX=-7.65538 EndY=-5.99526 EndZ=0
    g50: LineSegment StartX=-7.65538 StartY=-5.99526 StartZ=0 EndX=-6.48644 EndY=-5.99526 EndZ=0
    g51: LineSegment StartX=-6.77343 StartY=-8 StartZ=0 EndX=-8.43343 EndY=-8 EndZ=0
    g52: LineSegment StartX=-8.43343 StartY=-8 StartZ=0 EndX=-8.43343 EndY=-10 EndZ=0
    g53: LineSegment StartX=-8.43343 StartY=-10 StartZ=0 EndX=-7.19003 EndY=-10 EndZ=0
  constraints (112):
    c: Horizontal(g0)
    c: Distance(g0) = 2
    c: Block(g0)
    c: Vertical(g1)
    c: Coincident(g2,g0)
    c: Vertical(g2)
    c: Block(g2)
    c: Coincident(g6,g2)
    c: Weight(g3) = 1
    c: Equal(g3,g4)
    c: Equal(g3,g5)
    c: InternalAlignment(g3,g6)
    c: InternalAlignment(g4,g6)
    c: InternalAlignment(g5,g6)
    c: InternalAlignment(g7,g6)
    c: InternalAlignment(g8,g6)
    c: Block(g6)
    c: Coincident(g9,g1)
    c: Coincident(g9,g6)
    c: Horizontal(g9)
    c: Vertical(g10)
    c: Block(g10)
    c: Horizontal(g11)
    c: Block(g11)
    c: Coincident(g12,g10)
    c: Horizontal(g12)
    c: Block(g12)
    c: Coincident(g13,g11)
    c: Vertical(g13)
    c: Block(g13)
    c: Coincident(g14,g10)
    c: Horizontal(g14)
    c: Block(g14)
    c: Block(g9)
    c: Block(g1)
    c: Weight(g15) = 1
    c: Equal(g15,g16)
    c: Equal(g15,g17)
    c: InternalAlignment(g15,g18)
    c: InternalAlignment(g16,g18)
    c: InternalAlignment(g17,g18)
    c: InternalAlignment(g19,g18)
    c: InternalAlignment(g20,g18)
    c: Weight(g21) = 1
    c: Equal(g21,g22)
    c: Equal(g21,g23)
    c: InternalAlignment(g21,g24)
    c: InternalAlignment(g22,g24)
    c: InternalAlignment(g23,g24)
    c: InternalAlignment(g25,g24)
    c: InternalAlignment(g26,g24)
    c: Weight(g27) = 1
    c: Equal(g27,g28)
    c: Equal(g27,g29)
    c: Coincident(g30,g14)
    c: InternalAlignment(g27,g30)
    c: InternalAlignment(g28,g30)
    c: InternalAlignment(g29,g30)
    c: InternalAlignment(g31,g30)
    c: InternalAlignment(g32,g30)
    c: Coincident(g36,g12)
    c: Weight(g33) = 1
    c: Equal(g33,g34)
    c: Equal(g33,g35)
    c: Coincident(g36,g11)
    c: InternalAlignment(g33,g36)
    c: InternalAlignment(g34,g36)
    c: InternalAlignment(g35,g36)
    c: InternalAlignment(g37,g36)
    c: InternalAlignment(g38,g36)
    c: Coincident(g42,g13)
    c: Weight(g39) = 1
    c: Equal(g39,g40)
    c: Equal(g39,g41)
    c: Coincident(g42,g1)
    c: InternalAlignment(g39,g42)
    c: InternalAlignment(g40,g42)
    c: InternalAlignment(g41,g42)
    c: InternalAlignment(g43,g42)
    c: InternalAlignment(g44,g42)
    c: Block(g18)
    c: Block(g24)
    c: Block(g30)
    c: Block(g36)
    c: Block(g42)
    c: Horizontal(g45)
    c: Coincident(g45,g0)
    c: Vertical(g46)
    c: Coincident(g46,g45)
    c: Coincident(g47,g46)
    c: Coincident(g47,g18)
    c: Horizontal(g47)
    c: Block(g46)
    c: Coincident(g48,g18)
    c: Horizontal(g48)
    c: Distance(g48) = 1.33
    c: Vertical(g49)
    c: Coincident(g49,g48)
    c: Coincident(g50,g49)
    c: Coincident(g50,g24)
    c: Horizontal(g50)
    c: Tangent(g50,g22)
    c: Horizontal(g51)
    c: Coincident(g51,g24)
    c: Block(g51)
    c: Vertical(g52)
    c: Block(g52)
    c: Coincident(g52,g51)
    c: Coincident(g53,g52)
    c: Coincident(g53,g30)
    c: Horizontal(g53)
    c: Distance(g1) = 8.5
FEATURE [Part::Feature] Face024
  shape: bbox 9.8 x 26.5 x 2e-07 mm, 1 faces, 0 solids (baked)
FEATURE [Part::Revolution] Revolve024
  Angle = 360
  Axis = (0,1,0)
  Base = (0,0,0)
  FaceMakerClass = Part::FaceMakerBullseye
  Placement = pos=(0,0,0) rot=(0,0,1;1.5708rad)
  Solid = false
  Source = -> Face024
  Symmetric = false
FEATURE [Part::Feature] Face025
  shape: bbox 9.8 x 26.5 x 2e-07 mm, 1 faces, 0 solids (baked)
FEATURE [Part::Revolution] Revolve025
  Angle = 360
  Axis = (0,1,0)
  Base = (0,0,0)
  FaceMakerClass = Part::FaceMakerBullseye
  Placement = pos=(0,0,0) rot=(0,0,1;1.5708rad)
  Solid = false
  Source = -> Face025
  Symmetric = false
FEATURE [Part::MultiFuse] Fusion033
  Placement = pos=(-18,19,36) rot=(0,0,1;0rad)
  Shapes = -> [Revolve025,Revolve024]
FEATURE [Part::Cylinder] Cylinder014
  Angle = 360
  AttacherType = Attacher::AttachEngine3D
  Height = 20
  Placement = pos=(0,0,36.15) rot=(0,0,1;0rad)
  Radius = 14.3
FEATURE [Part::Cylinder] Cylinder015
  Angle = 360
  AttacherType = Attacher::AttachEngine3D
  Height = 10
  Placement = pos=(0,0,36.15) rot=(0,0,1;0rad)
  Radius = 4
FEATURE [Part::MultiFuse] Fusion034  label="removeToCreteHoleForPlugHousing004"
  Placement = pos=(-42,19,36) rot=(0,1,0;1.5708rad)
  Shapes = -> [Cylinder014,Cylinder015]
FEATURE [Part::Cut] Cut008  label="top004"
  Base = -> Cut004
  Placement = pos=(-1,0,0) rot=(0,0,1;0rad)
  Tool = -> Fusion034
FEATURE [Part::Box] Box005  label="Cube005"
  AttacherType = Attacher::AttachEngine3D
  Height = 28
  Length = 3
  Placement = pos=(110.7,19,22) rot=(0,0,1;0rad)
  Width = 15.7
FEATURE [Part::Cylinder] Cylinder016
  Angle = 360
  AttacherType = Attacher::AttachEngine3D
  Height = 10
  Placement = pos=(0,0,36.15) rot=(0,0,1;0rad)
  Radius = 4
FEATURE [Part::Cylinder] Cylinder017
  Angle = 360
  AttacherType = Attacher::AttachEngine3D
  Height = 20
  Placement = pos=(0,0,36.15) rot=(0,0,1;0rad)
  Radius = 10.3
FEATURE [Part::MultiFuse] Fusion035  label="removeToCreteHoleForPlugHousing005"
  Placement = pos=(70,19,36) rot=(0,1,0;1.5708rad)
  Shapes = -> [Cylinder017,Cylinder016]
FEATURE [Part::Cut] Cut009  label="plugHousingTab001"
  Base = -> Box005
  Placement = pos=(-107.4,-14,0) rot=(0,0,1;0rad)
  Tool = -> Fusion035
FEATURE [Part::Box] Box006  label="Cube006"
  AttacherType = Attacher::AttachEngine3D
  Height = 28
  Length = 3
  Placement = pos=(110.7,19,22) rot=(0,0,1;0rad)
  Width = 15.7
FEATURE [Part::Cylinder] Cylinder018
  Angle = 360
  AttacherType = Attacher::AttachEngine3D
  Height = 10
  Placement = pos=(0,0,36.15) rot=(0,0,1;0rad)
  Radius = 4
FEATURE [Part::Cylinder] Cylinder019
  Angle = 360
  AttacherType = Attacher::AttachEngine3D
  Height = 20
  Placement = pos=(0,0,36.15) rot=(0,0,1;0rad)
  Radius = 10.3
FEATURE [Part::MultiFuse] Fusion036  label="removeToCreteHoleForPlugHousing006"
  Placement = pos=(70,19,36) rot=(0,1,0;1.5708rad)
  Shapes = -> [Cylinder019,Cylinder018]
FEATURE [Part::Cut] Cut010  label="plugHousingTab002"
  Base = -> Box006
  Placement = pos=(-107.4,-14,0) rot=(0,0,1;0rad)
  Tool = -> Fusion036
FEATURE [Part::MultiFuse] Fusion037
  Placement = pos=(9.6,23,0) rot=(0,0,1;3.14159rad)
  Shapes = -> [Cut009,Cut010]
FEATURE [Part::Box] Box  label="Cube"
  AttacherType = Attacher::AttachEngine3D
  Height = 10
  Length = 3
  Placement = pos=(3.3,4,12) rot=(0,0,1;0rad)
  Width = 10
FEATURE [Part::Fillet] Fillet004
  Base = -> Fusion028
  Edges = 1 edges r=2: [Edge25]
FEATURE [Part::Fillet] Fillet005  label="plugHousing046"
  Base = -> Fillet004
  Edges = 1 edges r=2: [Edge8]
FEATURE [Part::Fillet] Fillet006
  Base = -> Box
  Edges = 1 edges r=2: [Edge11]
FEATURE [Part::Box] Box007  label="Cube007"
  AttacherType = Attacher::AttachEngine3D
  Height = 10
  Length = 3
  Placement = pos=(3.3,4,50) rot=(0,0,1;0rad)
  Width = 10
FEATURE [Part::Fillet] Fillet007
  Base = -> Box007
  Edges = 1 edges r=2: [Edge12]
FEATURE [Part::Box] Box008  label="Cube008"
  AttacherType = Attacher::AttachEngine3D
  Height = 28
  Length = 4
  Placement = pos=(5,0,22) rot=(0,0,1;0rad)
  Width = 10
FEATURE [Part::Fillet] Fillet008
  Base = -> Box008
  Edges = 1 edges r=1: [Edge7]
FEATURE [Part::Fillet] Fillet009
  Base = -> Fillet008
  Edges = 1 edges r=2: [Edge5]
FEATURE [Part::Fillet] Fillet010
  Base = -> Fillet009
  Edges = 1 edges r=2: [Edge2]
FEATURE [Sketcher::SketchObject] Sketch009  label="topSketch003"
  FullyConstrained = true
  sketch-geometry (4):
    g0: LineSegment StartX=16.8446 StartY=31.512 StartZ=0 EndX=16.3251 EndY=34.4666 EndZ=0
    g1: ArcOfCircle CenterX=19 CenterY=19.2524 CenterZ=0 NormalX=0 NormalY=0 NormalZ=1 AngleXU=0 Radius=15.4476 StartAngle=1.74483 EndAngle=2.72717
    g2: ArcOfCircle CenterX=19 CenterY=19.2524 CenterZ=0 NormalX=0 NormalY=0 NormalZ=1 AngleXU=0 Radius=12.4476 StartAngle=1.74483 EndAngle=2.73189
    g3: LineSegment StartX=4.86004 StartY=25.4725 StartZ=0 EndX=7.58253 EndY=24.2107 EndZ=0
  constraints (7):
    c: Block(g0)
    c: Coincident(g1,g0)
    c: Coincident(g2,g0)
    c: Coincident(g3,g1)
    c: Coincident(g3,g2)
    c: Block(g1)
    c: Block(g2)
FEATURE [Part::Extrusion] Extrude008
  Base = -> Sketch009
  Dir = (0,0,1)
  DirMode = 2
  FaceMakerClass = Part::FaceMakerBullseye
  LengthFwd = 10
  LengthRev = 0
  Placement = pos=(0,0,31) rot=(0,0,1;0rad)
  Solid = true
  Symmetric = false
FEATURE [Part::Cylinder] Cylinder020
  Angle = 360
  AttacherType = Attacher::AttachEngine3D
  Height = 20
  Placement = pos=(0,0,36.15) rot=(0,0,1;0rad)
  Radius = 8.2
FEATURE [Part::Cylinder] Cylinder021
  Angle = 360
  AttacherType = Attacher::AttachEngine3D
  Height = 10
  Placement = pos=(0,0,36.15) rot=(0,0,1;0rad)
  Radius = 4
FEATURE [Part::MultiFuse] Fusion038  label="removeToCreteHoleForPlugHousing007"
  Placement = pos=(-42,19,36) rot=(0,1,0;1.5708rad)
  Shapes = -> [Cylinder020,Cylinder021]
FEATURE [Part::Cut] Cut011
  Base = -> Extrude008
  Tool = -> Fusion038
FEATURE [Part::Fillet] Fillet011
  Base = -> Cut011
  Edges = 1 edges r=2: [Edge1]
FEATURE [Part::Fillet] Fillet012
  Base = -> Fillet011
  Edges = 1 edges r=2.5: [Edge1]
FEATURE [Part::Fillet] Fillet013
  Base = -> Fillet012
  Edges = 1 edges r=2.5: [Edge2]
FEATURE [Part::Box] Box010  label="Cube010"
  AttacherType = Attacher::AttachEngine3D
  Height = 16
  Length = 8
  Placement = pos=(12.7,31.52,28) rot=(0,0,1;0rad)
  Width = 4
FEATURE [Sketcher::SketchObject] Sketch010  label="topSketch004"
  FullyConstrained = true
  sketch-geometry (4):
    g0: LineSegment StartX=16.8446 StartY=31.512 StartZ=0 EndX=16.3251 EndY=34.4666 EndZ=0
    g1: ArcOfCircle CenterX=19 CenterY=19.2524 CenterZ=0 NormalX=0 NormalY=0 NormalZ=1 AngleXU=0 Radius=15.4476 StartAngle=1.74483 EndAngle=2.72717
    g2: ArcOfCircle CenterX=19 CenterY=19.2524 CenterZ=0 NormalX=0 NormalY=0 NormalZ=1 AngleXU=0 Radius=12.4476 StartAngle=1.74483 EndAngle=2.73189
    g3: LineSegment StartX=4.86004 StartY=25.4725 StartZ=0 EndX=7.58253 EndY=24.2107 EndZ=0
  constraints (7):
    c: Block(g0)
    c: Coincident(g1,g0)
    c: Coincident(g2,g0)
    c: Coincident(g3,g1)
    c: Coincident(g3,g2)
    c: Block(g1)
    c: Block(g2)
FEATURE [Part::Cylinder] Cylinder022
  Angle = 360
  AttacherType = Attacher::AttachEngine3D
  Height = 10
  Placement = pos=(0,0,36.15) rot=(0,0,1;0rad)
  Radius = 4
FEATURE [Sketcher::SketchObject] Sketch011  label="topSketch005"
  FullyConstrained = true
  sketch-geometry (4):
    g0: LineSegment StartX=16.8446 StartY=31.512 StartZ=0 EndX=16.3251 EndY=34.4666 EndZ=0
    g1: ArcOfCircle CenterX=19 CenterY=19.2524 CenterZ=0 NormalX=0 NormalY=0 NormalZ=1 AngleXU=0 Radius=15.4476 StartAngle=1.74483 EndAngle=2.72717
    g2: ArcOfCircle CenterX=19 CenterY=19.2524 CenterZ=0 NormalX=0 NormalY=0 NormalZ=1 AngleXU=0 Radius=12.4476 StartAngle=1.74483 EndAngle=2.73189
    g3: LineSegment StartX=4.86004 StartY=25.4725 StartZ=0 EndX=7.58253 EndY=24.2107 EndZ=0
  constraints (7):
    c: Block(g0)
    c: Coincident(g1,g0)
    c: Coincident(g2,g0)
    c: Coincident(g3,g1)
    c: Coincident(g3,g2)
    c: Block(g1)
    c: Block(g2)
FEATURE [Part::Extrusion] Extrude010
  Base = -> Sketch011
  Dir = (0,0,1)
  DirMode = 2
  FaceMakerClass = Part::FaceMakerBullseye
  LengthFwd = 10.6
  LengthRev = 0
  Placement = pos=(0,0,31) rot=(0,0,1;0rad)
  Solid = true
  Symmetric = false
FEATURE [Part::Cylinder] Cylinder023
  Angle = 360
  AttacherType = Attacher::AttachEngine3D
  Height = 20
  Placement = pos=(0,0,36.15) rot=(0,0,1;0rad)
  Radius = 8.2
FEATURE [Part::MultiFuse] Fusion039  label="removeToCreteHoleForPlugHousing008"
  Placement = pos=(-42,19,36) rot=(0,1,0;1.5708rad)
  Shapes = -> [Cylinder023,Cylinder022]
FEATURE [Part::Cut] Cut012
  Base = -> Extrude010
  Placement = pos=(0,0,-0.3) rot=(0,0,1;0rad)
  Tool = -> Fusion039
FEATURE [Part::Cut] Cut013
  Base = -> Box010
  Tool = -> Cut012
FEATURE [Part::Fillet] Fillet014
  Base = -> Cut013
  Edges = 1 edges r=0.7: [Edge13]
FEATURE [Part::Fillet] Fillet015
  Base = -> Fillet014
  Edges = 1 edges r=0.7: [Edge13]
FEATURE [Part::Fillet] Fillet016
  Base = -> Fillet015
  Edges = 1 edges r=0.7: [Edge16]
FEATURE [Part::Fillet] Fillet017
  Base = -> Fillet016
  Edges = 1 edges r=0.7: [Edge11]
FEATURE [Part::Fillet] Fillet018
  Base = -> Fillet017
  Edges = 1 edges r=0.7: [Edge10]
FEATURE [Part::Fillet] Fillet019
  Base = -> Fillet018
  Edges = 1 edges r=1.2: [Edge5]
FEATURE [Part::Fillet] Fillet020
  Base = -> Fillet019
  Edges = 1 edges r=1.2: [Edge12]
FEATURE [Part::Fillet] Fillet021
  Base = -> Fillet020
  Edges = 1 edges r=2: [Edge1]
  Placement = pos=(0.3,0,0) rot=(0,0,1;0rad)
FEATURE [Part::MultiFuse] Fusion040  label="top005"
  Shapes = -> [Cut008,Fillet021]
FEATURE [Part::MultiFuse] Fusion041  label="wireHolder"
  Shapes = -> [Fusion033,Fillet013]
FEATURE [Part::MultiFuse] Fusion042
  Shapes = -> [Fillet007,Fusion041]
FEATURE [Part::MultiFuse] Fusion043  label="wireHolder001"
  Shapes = -> [Fusion042,Fillet010]
FEATURE [Part::MultiFuse] Fusion044  label="wireHolder002"
  Shapes = -> [Fillet006,Fusion037,Fusion043]
FEATURE [Part::Feature] Face026
  shape: bbox 11 x 6 x 2e-07 mm, 1 faces, 0 solids (baked)
FEATURE [Part::Revolution] Revolve026
  Angle = 360
  Axis = (0,1,0)
  Base = (0,0,0)
  FaceMakerClass = Part::FaceMakerBullseye
  Placement = pos=(30.3,-1,19.7) rot=(0,0,1;0rad)
  Solid = false
  Source = -> Face026
  Symmetric = false
FEATURE [Sketcher::SketchObject] Sketch013  label="topSketch006"
  FullyConstrained = true
  sketch-geometry (13):
    g0: LineSegment StartX=117 StartY=19 StartZ=0 EndX=117 EndY=38 EndZ=0
    g1: ArcOfCircle CenterX=98 CenterY=19 CenterZ=0 NormalX=0 NormalY=0 NormalZ=1 AngleXU=0 Radius=19 StartAngle=5.7297 EndAngle=6.28319
    g2: LineSegment StartX=0 StartY=3 StartZ=0 EndX=0 EndY=19 EndZ=0
    g3: LineSegment StartX=19 StartY=38 StartZ=0 EndX=117 EndY=38 EndZ=0
    g4: ArcOfCircle CenterX=19 CenterY=19 CenterZ=0 NormalX=0 NormalY=0 NormalZ=1 AngleXU=0 Radius=19 StartAngle=1.5708 EndAngle=3.14159
    g5: ArcOfCircle CenterX=19 CenterY=19 CenterZ=0 NormalX=0 NormalY=0 NormalZ=1 AngleXU=0 Radius=16 StartAngle=1.5708 EndAngle=3.14159
    g6: ArcOfCircle CenterX=98 CenterY=19 CenterZ=0 NormalX=0 NormalY=0 NormalZ=1 AngleXU=0 Radius=16 StartAngle=5.60905 EndAngle=6.28319
    g7: LineSegment StartX=114 StartY=19 StartZ=0 EndX=114 EndY=35 EndZ=0
    g8: LineSegment StartX=110.5 StartY=9.01251 StartZ=0 EndX=114.163 EndY=9.01251 EndZ=0
    g9: LineSegment StartX=114 StartY=35 StartZ=0 EndX=19 EndY=35 EndZ=0
    g10: LineSegment StartX=0 StartY=3 StartZ=0 EndX=0 EndY=0 EndZ=0
    g11: LineSegment StartX=3 StartY=0 StartZ=0 EndX=0 EndY=0 EndZ=0
    g12: LineSegment StartX=3 StartY=19 StartZ=0 EndX=3 EndY=0 EndZ=0
  constraints (33):
    c: Vertical(g0)
    c: Distance(g0) = 19
    c: Block(g0)
    c: Coincident(g1,g0)
    c: Block(g1)
    c: Vertical(g2)
    c: Block(g2)
    c: Coincident(g3,g0)
    c: Horizontal(g3)
    c: Distance(g3) = 98
    c: Coincident(g4,g3)
    c: Coincident(g4,g2)
    c: Block(g4)
    c: Coincident(g5,g4)
    c: Coincident(g6,g1)
    c: Block(g6)
    c: Block(g5)
    c: Coincident(g7,g6)
    c: Vertical(g7)
    c: Coincident(g8,g6)
    c: Coincident(g8,g1)
    c: Coincident(g9,g7)
    c: Coincident(g9,g5)
    c: Horizontal(g9)
    c: Tangent(g9,g5)
    c: Coincident(g10,g2)
    c: Distance(g10) = 3
    c: Vertical(g10)
    c: Coincident(g11,g10)
    c: Horizontal(g11)
    c: Coincident(g12,g5)
    c: Coincident(g12,g11)
    c: Vertical(g12)
FEATURE [Part::Extrusion] Extrude011  label="top006"
  Base = -> Sketch013
  Dir = (0,0,1)
  DirMode = 2
  FaceMakerClass = Part::FaceMakerBullseye
  LengthFwd = 72
  LengthRev = 0
  Solid = true
  Symmetric = false
FEATURE [Sketcher::SketchObject] Sketch014
  FullyConstrained = true
  MapMode = 3
  Placement = pos=(0,0,0) rot=(1,0,0;1.5708rad)
  Support = -> [Extrude011]
  sketch-geometry (8):
    g0: Circle CenterX=80.351 CenterY=-67.6202 CenterZ=0 NormalX=0 NormalY=0 NormalZ=1 AngleXU=0 Radius=2
    g1: Circle CenterX=80.351 CenterY=-67.6202 CenterZ=0 NormalX=0 NormalY=0 NormalZ=1 AngleXU=0 Radius=3
    g2: Circle CenterX=80.351 CenterY=-4.92017 CenterZ=0 NormalX=0 NormalY=0 NormalZ=1 AngleXU=0 Radius=2
    g3: Circle CenterX=80.351 CenterY=-4.92017 CenterZ=0 NormalX=0 NormalY=0 NormalZ=1 AngleXU=0 Radius=3
    g4: Circle CenterX=23.851 CenterY=-4.92017 CenterZ=0 NormalX=0 NormalY=0 NormalZ=1 AngleXU=0 Radius=2
    g5: Circle CenterX=23.851 CenterY=-4.92017 CenterZ=0 NormalX=0 NormalY=0 NormalZ=1 AngleXU=0 Radius=3
    g6: Circle CenterX=23.851 CenterY=-67.6202 CenterZ=0 NormalX=0 NormalY=0 NormalZ=1 AngleXU=0 Radius=2
    g7: Circle CenterX=23.851 CenterY=-67.6202 CenterZ=0 NormalX=0 NormalY=0 NormalZ=1 AngleXU=0 Radius=3
  constraints (8):
    c: Block(g3)
    c: Block(g2)
    c: Block(g1)
    c: Block(g0)
    c: Block(g6)
    c: Block(g7)
    c: Block(g4)
    c: Block(g5)
FEATURE [Part::Feature] Face027
  shape: bbox 11 x 6 x 2e-07 mm, 1 faces, 0 solids (baked)
FEATURE [Part::Revolution] Revolve027
  Angle = 360
  Axis = (0,1,0)
  Base = (0,0,0)
  FaceMakerClass = Part::FaceMakerBullseye
  Placement = pos=(30.3,-1,51.7) rot=(0,0,1;0rad)
  Solid = false
  Source = -> Face027
  Symmetric = false
FEATURE [Part::Feature] Face028
  shape: bbox 11 x 6 x 2e-07 mm, 1 faces, 0 solids (baked)
FEATURE [Part::Revolution] Revolve028
  Angle = 360
  Axis = (0,1,0)
  Base = (0,0,0)
  FaceMakerClass = Part::FaceMakerBullseye
  Placement = pos=(62.3,-1,19.7) rot=(0,0,1;0rad)
  Solid = false
  Source = -> Face028
  Symmetric = false
FEATURE [Part::Feature] Face029
  shape: bbox 11 x 6 x 2e-07 mm, 1 faces, 0 solids (baked)
FEATURE [Part::Revolution] Revolve029
  Angle = 360
  Axis = (0,1,0)
  Base = (0,0,0)
  FaceMakerClass = Part::FaceMakerBullseye
  Placement = pos=(62.3,-1,51.7) rot=(0,0,1;0rad)
  Solid = false
  Source = -> Face029
  Symmetric = false
FEATURE [Part::Feature] Wire
  shape: bbox 11 x 5.2 x 2e-07 mm, 0 faces, 0 solids (baked)
FEATURE [Part::Revolution] Revolve030
  Angle = 360
  Axis = (0,1,0)
  Base = (0,0,0)
  FaceMakerClass = Part::FaceMakerBullseye
  Placement = pos=(30.3,38,19.7) rot=(0,0,1;0rad)
  Solid = true
  Source = -> Wire
  Symmetric = false
FEATURE [Part::Feature] Wire001
  shape: bbox 11 x 5.2 x 2e-07 mm, 0 faces, 0 solids (baked)
FEATURE [Part::Revolution] Revolve031
  Angle = 360
  Axis = (0,1,0)
  Base = (0,0,0)
  FaceMakerClass = Part::FaceMakerBullseye
  Placement = pos=(30.3,38,51.7) rot=(0,0,1;0rad)
  Solid = true
  Source = -> Wire001
  Symmetric = false
FEATURE [Part::Feature] Wire002
  shape: bbox 11 x 5.2 x 2e-07 mm, 0 faces, 0 solids (baked)
FEATURE [Part::Revolution] Revolve032
  Angle = 360
  Axis = (0,1,0)
  Base = (0,0,0)
  FaceMakerClass = Part::FaceMakerBullseye
  Placement = pos=(62.3,38,51.7) rot=(0,0,1;0rad)
  Solid = true
  Source = -> Wire002
  Symmetric = false
FEATURE [Part::Feature] Wire003
  shape: bbox 11 x 5.2 x 2e-07 mm, 0 faces, 0 solids (baked)
FEATURE [Part::Revolution] Revolve033
  Angle = 360
  Axis = (0,1,0)
  Base = (0,0,0)
  FaceMakerClass = Part::FaceMakerBullseye
  Placement = pos=(62.3,38,19.7) rot=(0,0,1;0rad)
  Solid = true
  Source = -> Wire003
  Symmetric = false
FEATURE [Part::MultiFuse] Fusion045  label="altRandScrewHousing"
  Shapes = -> [Revolve029,Revolve027,Revolve028,Revolve026]
FEATURE [Part::MultiFuse] Fusion046  label="fanScrewHousing"
  Shapes = -> [Revolve033,Revolve032,Revolve031,Revolve030]
FEATURE [Sketcher::SketchObject] Sketch015
  FullyConstrained = true
  sketch-geometry (17):
    g0: Circle CenterX=-3.5 CenterY=23.5 CenterZ=0 NormalX=0 NormalY=0 NormalZ=1 AngleXU=0 Radius=1
    g1: Circle CenterX=-1 CenterY=15.25 CenterZ=0 NormalX=0 NormalY=0 NormalZ=1 AngleXU=0 Radius=1
    g2: Circle CenterX=-3.5 CenterY=7 CenterZ=0 NormalX=0 NormalY=0 NormalZ=1 AngleXU=0 Radius=1
    g3: BSplineCurve PolesCount=3 KnotsCount=2 Degree=2 IsPeriodic=0
    g4: GeomPoint X=-3.5 Y=23.5 Z=0
    g5: GeomPoint X=-3.5 Y=7 Z=0
    g6: Circle CenterX=-4.8 CenterY=30.5 CenterZ=0 NormalX=0 NormalY=0 NormalZ=1 AngleXU=0 Radius=1
    g7: Circle CenterX=-3.5 CenterY=30.5 CenterZ=0 NormalX=0 NormalY=0 NormalZ=1 AngleXU=0 Radius=1
    g8: Circle CenterX=-3.5 CenterY=29.2 CenterZ=0 NormalX=0 NormalY=0 NormalZ=1 AngleXU=0 Radius=1
    g9: BSplineCurve PolesCount=3 KnotsCount=2 Degree=2 IsPeriodic=0
    g10: GeomPoint X=-4.8 Y=30.5 Z=0
    g11: GeomPoint X=-3.5 Y=29.2 Z=0
    g12: LineSegment StartX=-3.5 StartY=29.2 StartZ=0 EndX=-3.5 EndY=23.5 EndZ=0
    g13: LineSegment StartX=-4.8 StartY=30.5 StartZ=0 EndX=0 EndY=30.5 EndZ=0
    g14: LineSegment StartX=-3.5 StartY=0.3 StartZ=0 EndX=0 EndY=0.3 EndZ=0
    g15: LineSegment StartX=-3.5 StartY=0.3 StartZ=0 EndX=-3.5 EndY=7 EndZ=0
    g16: LineSegment StartX=0 StartY=0.3 StartZ=0 EndX=0 EndY=30.5 EndZ=0
  constraints (33):
    c: Weight(g0) = 1
    c: Equal(g0,g1)
    c: Equal(g0,g2)
    c: InternalAlignment(g0,g3)
    c: InternalAlignment(g1,g3)
    c: InternalAlignment(g2,g3)
    c: InternalAlignment(g4,g3)
    c: InternalAlignment(g5,g3)
    c: Block(g3)
    c: Weight(g6) = 1
    c: Equal(g6,g7)
    c: Equal(g6,g8)
    c: InternalAlignment(g6,g9)
    c: InternalAlignment(g7,g9)
    c: InternalAlignment(g8,g9)
    c: InternalAlignment(g10,g9)
    c: InternalAlignment(g11,g9)
    c: Block(g9)
    c: Coincident(g12,g9)
    c: Coincident(g12,g3)
    c: Vertical(g12)
    c: Coincident(g13,g9)
    c: Horizontal(g13)
    c: Distance(g13) = 4.8
    c: Horizontal(g14)
    c: Block(g14)
    c: Coincident(g15,g14)
    c: Coincident(g15,g3)
    c: Vertical(g15)
    c: Coincident(g16,g14)
    c: Coincident(g16,g13)
    c: Vertical(g16)
    c: Tangent(g16,g1)
FEATURE [Sketcher::SketchObject] Sketch016
  FullyConstrained = true
  sketch-geometry (16):
    g0: Circle CenterX=-3.5 CenterY=23.5 CenterZ=0 NormalX=0 NormalY=0 NormalZ=1 AngleXU=0 Radius=1
    g1: Circle CenterX=-1 CenterY=15.25 CenterZ=0 NormalX=0 NormalY=0 NormalZ=1 AngleXU=0 Radius=1
    g2: Circle CenterX=-3.5 CenterY=7 CenterZ=0 NormalX=0 NormalY=0 NormalZ=1 AngleXU=0 Radius=1
    g3: BSplineCurve PolesCount=3 KnotsCount=2 Degree=2 IsPeriodic=0
    g4: GeomPoint X=-3.5 Y=23.5 Z=0
    g5: GeomPoint X=-3.5 Y=7 Z=0
    g6: LineSegment StartX=-3.5 StartY=28.2 StartZ=0 EndX=-3.5 EndY=23.5 EndZ=0
    g7: LineSegment StartX=0 StartY=29.5 StartZ=0 EndX=0 EndY=30 EndZ=0
    g8: LineSegment StartX=-3.5 StartY=28.2 StartZ=0 EndX=-3.5 EndY=30 EndZ=0
    g9: LineSegment StartX=0 StartY=30 StartZ=0 EndX=0 EndY=30.5 EndZ=0
    g10: LineSegment StartX=0 StartY=30.5 StartZ=0 EndX=-3.5 EndY=30.5 EndZ=0
    g11: LineSegment StartX=-3.5 StartY=30.5 StartZ=0 EndX=-3.5 EndY=30 EndZ=0
    g12: LineSegment StartX=0 StartY=29.5 StartZ=0 EndX=0 EndY=5 EndZ=0
    g13: LineSegment StartX=-3.5 StartY=0.3 StartZ=0 EndX=-3.5 EndY=7 EndZ=0
    g14: LineSegment StartX=-3.5 StartY=0.3 StartZ=0 EndX=0 EndY=0.3 EndZ=0
    g15: LineSegment StartX=0 StartY=5 StartZ=0 EndX=0 EndY=0.3 EndZ=0
  constraints (39):
    c: Weight(g0) = 1
    c: Equal(g0,g1)
    c: Equal(g0,g2)
    c: InternalAlignment(g0,g3)
    c: InternalAlignment(g1,g3)
    c: InternalAlignment(g2,g3)
    c: InternalAlignment(g4,g3)
    c: InternalAlignment(g5,g3)
    c: Block(g3)
    c: Coincident(g6,g3)
    c: Vertical(g6)
    c: Vertical(g7)
    c: Distance(g7) = 0.5
    c: Coincident(g8,g6)
    c: Vertical(g8)
    c: Block(g6)
    c: Block(g7)
    c: Vertical(g9)
    c: Equal(g7,g9) = 0.5
    c: Block(g9)
    c: Coincident(g9,g7)
    c: Horizontal(g10)
    c: Coincident(g10,g9)
    c: Coincident(g11,g10)
    c: Coincident(g11,g8)
    c: Vertical(g11)
    c: Block(g11)
    c: Coincident(g12,g7)
    c: Vertical(g12)
    c: Coincident(g13,g3)
    c: Vertical(g13)
    c: Distance(g13) = 6.7
    c: Coincident(g14,g13)
    c: Horizontal(g14)
    c: Block(g14)
    c: Coincident(g15,g12)
    c: Coincident(g15,g14)
    c: Vertical(g15)
    c: Block(g15)
FEATURE [Sketcher::SketchObject] Sketch017
  FullyConstrained = true
  sketch-geometry (11):
    g0: LineSegment StartX=-3.5 StartY=1e-16 StartZ=0 EndX=-1.6 EndY=1e-16 EndZ=0
    g1: LineSegment StartX=-1.6 StartY=1e-16 StartZ=0 EndX=-1.6 EndY=1.5 EndZ=0
    g2: LineSegment StartX=-3.5 StartY=1.5 StartZ=0 EndX=-1.6 EndY=1.5 EndZ=0
    g3: LineSegment StartX=-3.5 StartY=1e-16 StartZ=0 EndX=-4.8 EndY=1e-16 EndZ=0
    g4: Circle CenterX=-3.5 CenterY=1.3 CenterZ=0 NormalX=0 NormalY=0 NormalZ=1 AngleXU=0 Radius=1
    g5: Circle CenterX=-3.5 CenterY=1e-16 CenterZ=0 NormalX=0 NormalY=0 NormalZ=1 AngleXU=0 Radius=1
    g6: Circle CenterX=-4.8 CenterY=1e-16 CenterZ=0 NormalX=0 NormalY=0 NormalZ=1 AngleXU=0 Radius=1
    g7: BSplineCurve PolesCount=3 KnotsCount=2 Degree=2 IsPeriodic=0
    g8: GeomPoint X=-3.5 Y=1.3 Z=0
    g9: GeomPoint X=-4.8 Y=1e-16 Z=0
    g10: LineSegment StartX=-3.5 StartY=1.3 StartZ=0 EndX=-3.5 EndY=1.5 EndZ=0
  constraints (24):
    c: Horizontal(g0)
    c: Distance(g0) = 1.9
    c: Block(g0)
    c: Coincident(g1,g0)
    c: Vertical(g1)
    c: Coincident(g2,g1)
    c: Horizontal(g2)
    c: Coincident(g3,g0)
    c: Horizontal(g3)
    c: Distance(g3) = 1.3
    c: Weight(g4) = 1
    c: Equal(g4,g5)
    c: Coincident(g5,g0)
    c: Equal(g4,g6)
    c: Coincident(g7,g3)
    c: InternalAlignment(g4,g7)
    c: InternalAlignment(g5,g7)
    c: InternalAlignment(g6,g7)
    c: InternalAlignment(g8,g7)
    c: InternalAlignment(g9,g7)
    c: Coincident(g10,g7)
    c: Coincident(g10,g2)
    c: Vertical(g10)
    c: Block(g10)
FEATURE [Part::Feature] Face035
  shape: bbox 3.2 x 1.5 x 2e-07 mm, 1 faces, 0 solids (baked)
FEATURE [Part::Revolution] Revolve039  label="backCaseScrewRetainer"
  Angle = 360
  Axis = (0,1,0)
  Base = (0,0,0)
  FaceMakerClass = Part::FaceMakerBullseye
  Placement = pos=(12.5,3,62) rot=(0,0,1;0rad)
  Solid = false
  Source = -> Face035
  Symmetric = false
FEATURE [Part::Feature] Face036
  shape: bbox 3.2 x 1.5 x 2e-07 mm, 1 faces, 0 solids (baked)
FEATURE [Part::Feature] Face039
  shape: bbox 4.8 x 30.2 x 2e-07 mm, 1 faces, 0 solids (baked)
FEATURE [Part::Revolution] Revolve043  label="frontCaseScrewPost002"
  Angle = 360
  Axis = (0,1,0)
  Base = (0,0,0)
  FaceMakerClass = Part::FaceMakerBullseye
  Placement = pos=(89.5,4.5,3.5) rot=(0,0,1;0rad)
  Solid = false
  Source = -> Face039
  Symmetric = false
FEATURE [Part::Feature] Face042
  shape: bbox 4.8 x 30.2 x 2e-07 mm, 1 faces, 0 solids (baked)
FEATURE [Part::Revolution] Revolve046  label="frontCaseScrewPost003"
  Angle = 360
  Axis = (0,1,0)
  Base = (0,0,0)
  FaceMakerClass = Part::FaceMakerBullseye
  Placement = pos=(89.5,4.5,68.5) rot=(0,0,1;0rad)
  Solid = false
  Source = -> Face042
  Symmetric = false
FEATURE [Part::Feature] Face043
  shape: bbox 3.2 x 1.5 x 2e-07 mm, 1 faces, 0 solids (baked)
FEATURE [Part::Revolution] Revolve047  label="frontCaseScrewRetainer002"
  Angle = 360
  Axis = (0,1,0)
  Base = (0,0,0)
  FaceMakerClass = Part::FaceMakerBullseye
  Placement = pos=(89.5,3,68.5) rot=(0,0,1;0rad)
  Solid = false
  Source = -> Face043
  Symmetric = false
FEATURE [Part::Feature] Face044
  shape: bbox 3.2 x 1.5 x 2e-07 mm, 1 faces, 0 solids (baked)
FEATURE [Part::Revolution] Revolve048  label="frontCaseScrewRetainer003"
  Angle = 360
  Axis = (0,1,0)
  Base = (0,0,0)
  FaceMakerClass = Part::FaceMakerBullseye
  Placement = pos=(89.5,3,3.5) rot=(0,0,1;0rad)
  Solid = false
  Source = -> Face044
  Symmetric = false
FEATURE [App::MeasureDistance] Distance002  label="Distance: 1.67 mm"
  Distance = 1.66921
  P1 = (99.2361,4.7524,71.7)
  P2 = (99.2347,6.42161,71.7)
FEATURE [Sketcher::SketchObject] Sketch018
  FullyConstrained = true
  sketch-geometry (7):
    g0: LineSegment StartX=0 StartY=0 StartZ=0 EndX=0 EndY=6 EndZ=0
    g1: Circle CenterX=0 CenterY=0 CenterZ=0 NormalX=0 NormalY=0 NormalZ=1 AngleXU=0 Radius=1
    g2: Circle CenterX=8 CenterY=6 CenterZ=0 NormalX=0 NormalY=0 NormalZ=1 AngleXU=0 Radius=1
    g3: BSplineCurve PolesCount=3 KnotsCount=2 Degree=2 IsPeriodic=0
    g4: GeomPoint X=0 Y=0 Z=0
    g5: GeomPoint X=8 Y=6 Z=0
    g6: LineSegment StartX=0 StartY=6 StartZ=0 EndX=8 EndY=6 EndZ=0
  constraints (14):
    c: Coincident(g0,g-1)
    c: Distance(g0) = 6
    c: Vertical(g0)
    c: Coincident(g3,g0)
    c: Weight(g1) = 1
    c: Equal(g1,g2)
    c: InternalAlignment(g1,g3)
    c: InternalAlignment(g2,g3)
    c: InternalAlignment(g4,g3)
    c: InternalAlignment(g5,g3)
    c: Block(g3)
    c: Coincident(g6,g0)
    c: Coincident(g6,g3)
    c: Horizontal(g6)
FEATURE [Part::Extrusion] Extrude012  label="caseScrewPillarBracket"
  Base = -> Sketch018
  Dir = (0,0,1)
  DirMode = 2
  FaceMakerClass = Part::FaceMakerBullseye
  LengthFwd = 2.4
  LengthRev = 0
  Placement = pos=(15.76,29,8.8) rot=(0,1,0;0rad)
  Solid = true
  Symmetric = false
FEATURE [Sketcher::SketchObject] Sketch019
  FullyConstrained = true
  sketch-geometry (7):
    g0: LineSegment StartX=0 StartY=0 StartZ=0 EndX=0 EndY=6 EndZ=0
    g1: Circle CenterX=0 CenterY=0 CenterZ=0 NormalX=0 NormalY=0 NormalZ=1 AngleXU=0 Radius=1
    g2: Circle CenterX=8 CenterY=6 CenterZ=0 NormalX=0 NormalY=0 NormalZ=1 AngleXU=0 Radius=1
    g3: BSplineCurve PolesCount=3 KnotsCount=2 Degree=2 IsPeriodic=0
    g4: GeomPoint X=0 Y=0 Z=0
    g5: GeomPoint X=8 Y=6 Z=0
    g6: LineSegment StartX=0 StartY=6 StartZ=0 EndX=8 EndY=6 EndZ=0
  constraints (14):
    c: Coincident(g0,g-1)
    c: Distance(g0) = 6
    c: Vertical(g0)
    c: Coincident(g3,g0)
    c: Weight(g1) = 1
    c: Equal(g1,g2)
    c: InternalAlignment(g1,g3)
    c: InternalAlignment(g2,g3)
    c: InternalAlignment(g4,g3)
    c: InternalAlignment(g5,g3)
    c: Block(g3)
    c: Coincident(g6,g0)
    c: Coincident(g6,g3)
    c: Horizontal(g6)
FEATURE [Part::Extrusion] Extrude013  label="caseScrewPillarBracket001"
  Base = -> Sketch019
  Dir = (0,0,1)
  DirMode = 2
  FaceMakerClass = Part::FaceMakerBullseye
  LengthFwd = 2.4
  LengthRev = 0
  Placement = pos=(15.76,29,60.8) rot=(0,0,1;0rad)
  Solid = true
  Symmetric = false
FEATURE [Sketcher::SketchObject] Sketch020
  FullyConstrained = true
  sketch-geometry (7):
    g0: LineSegment StartX=0 StartY=0 StartZ=0 EndX=0 EndY=6 EndZ=0
    g1: Circle CenterX=0 CenterY=0 CenterZ=0 NormalX=0 NormalY=0 NormalZ=1 AngleXU=0 Radius=1
    g2: Circle CenterX=8 CenterY=6 CenterZ=0 NormalX=0 NormalY=0 NormalZ=1 AngleXU=0 Radius=1
    g3: BSplineCurve PolesCount=3 KnotsCount=2 Degree=2 IsPeriodic=0
    g4: GeomPoint X=0 Y=0 Z=0
    g5: GeomPoint X=8 Y=6 Z=0
    g6: LineSegment StartX=0 StartY=6 StartZ=0 EndX=8 EndY=6 EndZ=0
  constraints (14):
    c: Coincident(g0,g-1)
    c: Distance(g0) = 6
    c: Vertical(g0)
    c: Coincident(g3,g0)
    c: Weight(g1) = 1
    c: Equal(g1,g2)
    c: InternalAlignment(g1,g3)
    c: InternalAlignment(g2,g3)
    c: InternalAlignment(g4,g3)
    c: InternalAlignment(g5,g3)
    c: Block(g3)
    c: Coincident(g6,g0)
    c: Coincident(g6,g3)
    c: Horizontal(g6)
FEATURE [Part::Extrusion] Extrude014  label="caseScrewPillarBracket002"
  Base = -> Sketch020
  Dir = (0,0,1)
  DirMode = 2
  FaceMakerClass = Part::FaceMakerBullseye
  LengthFwd = 2.4
  LengthRev = 0
  Placement = pos=(13.7,29,13.26) rot=(0,-1,0;1.5708rad)
  Solid = true
  Symmetric = false
FEATURE [Sketcher::SketchObject] Sketch021
  FullyConstrained = true
  sketch-geometry (7):
    g0: LineSegment StartX=0 StartY=0 StartZ=0 EndX=0 EndY=6 EndZ=0
    g1: Circle CenterX=0 CenterY=0 CenterZ=0 NormalX=0 NormalY=0 NormalZ=1 AngleXU=0 Radius=1
    g2: Circle CenterX=8 CenterY=6 CenterZ=0 NormalX=0 NormalY=0 NormalZ=1 AngleXU=0 Radius=1
    g3: BSplineCurve PolesCount=3 KnotsCount=2 Degree=2 IsPeriodic=0
    g4: GeomPoint X=0 Y=0 Z=0
    g5: GeomPoint X=8 Y=6 Z=0
    g6: LineSegment StartX=0 StartY=6 StartZ=0 EndX=8 EndY=6 EndZ=0
  constraints (14):
    c: Coincident(g0,g-1)
    c: Distance(g0) = 6
    c: Vertical(g0)
    c: Coincident(g3,g0)
    c: Weight(g1) = 1
    c: Equal(g1,g2)
    c: InternalAlignment(g1,g3)
    c: InternalAlignment(g2,g3)
    c: InternalAlignment(g4,g3)
    c: InternalAlignment(g5,g3)
    c: Block(g3)
    c: Coincident(g6,g0)
    c: Coincident(g6,g3)
    c: Horizontal(g6)
FEATURE [Part::Extrusion] Extrude015  label="caseScrewPillarBracket003"
  Base = -> Sketch021
  Dir = (0,0,1)
  DirMode = 2
  FaceMakerClass = Part::FaceMakerBullseye
  LengthFwd = 2.4
  LengthRev = 0
  Placement = pos=(11.3,29,58.74) rot=(0,1,0;1.5708rad)
  Solid = true
  Symmetric = false
FEATURE [Sketcher::SketchObject] Sketch022
  FullyConstrained = true
  sketch-geometry (7):
    g0: LineSegment StartX=0 StartY=0 StartZ=0 EndX=0 EndY=6 EndZ=0
    g1: Circle CenterX=0 CenterY=0 CenterZ=0 NormalX=0 NormalY=0 NormalZ=1 AngleXU=0 Radius=1
    g2: Circle CenterX=8 CenterY=6 CenterZ=0 NormalX=0 NormalY=0 NormalZ=1 AngleXU=0 Radius=1
    g3: BSplineCurve PolesCount=3 KnotsCount=2 Degree=2 IsPeriodic=0
    g4: GeomPoint X=0 Y=0 Z=0
    g5: GeomPoint X=8 Y=6 Z=0
    g6: LineSegment StartX=0 StartY=6 StartZ=0 EndX=8 EndY=6 EndZ=0
  constraints (14):
    c: Coincident(g0,g-1)
    c: Distance(g0) = 6
    c: Vertical(g0)
    c: Coincident(g3,g0)
    c: Weight(g1) = 1
    c: Equal(g1,g2)
    c: InternalAlignment(g1,g3)
    c: InternalAlignment(g2,g3)
    c: InternalAlignment(g4,g3)
    c: InternalAlignment(g5,g3)
    c: Block(g3)
    c: Coincident(g6,g0)
    c: Coincident(g6,g3)
    c: Horizontal(g6)
FEATURE [Part::Extrusion] Extrude016  label="caseScrewPillarBracket004"
  Base = -> Sketch022
  Dir = (0,0,1)
  DirMode = 2
  FaceMakerClass = Part::FaceMakerBullseye
  LengthFwd = 2.4
  LengthRev = 0
  Placement = pos=(88.3,29,65.23) rot=(0,1,0;1.5708rad)
  Solid = true
  Symmetric = false
FEATURE [Sketcher::SketchObject] Sketch023
  FullyConstrained = true
  sketch-geometry (7):
    g0: LineSegment StartX=0 StartY=0 StartZ=0 EndX=0 EndY=6 EndZ=0
    g1: Circle CenterX=0 CenterY=0 CenterZ=0 NormalX=0 NormalY=0 NormalZ=1 AngleXU=0 Radius=1
    g2: Circle CenterX=8 CenterY=6 CenterZ=0 NormalX=0 NormalY=0 NormalZ=1 AngleXU=0 Radius=1
    g3: BSplineCurve PolesCount=3 KnotsCount=2 Degree=2 IsPeriodic=0
    g4: GeomPoint X=0 Y=0 Z=0
    g5: GeomPoint X=8 Y=6 Z=0
    g6: LineSegment StartX=0 StartY=6 StartZ=0 EndX=8 EndY=6 EndZ=0
  constraints (14):
    c: Coincident(g0,g-1)
    c: Distance(g0) = 6
    c: Vertical(g0)
    c: Coincident(g3,g0)
    c: Weight(g1) = 1
    c: Equal(g1,g2)
    c: InternalAlignment(g1,g3)
    c: InternalAlignment(g2,g3)
    c: InternalAlignment(g4,g3)
    c: InternalAlignment(g5,g3)
    c: Block(g3)
    c: Coincident(g6,g0)
    c: Coincident(g6,g3)
    c: Horizontal(g6)
FEATURE [Part::Extrusion] Extrude017  label="caseScrewPillarBracket005"
  Base = -> Sketch023
  Dir = (0,0,1)
  DirMode = 2
  FaceMakerClass = Part::FaceMakerBullseye
  LengthFwd = 2.4
  LengthRev = 0
  Placement = pos=(90.7,29,6.77) rot=(0,-1,0;1.5708rad)
  Solid = true
  Symmetric = false
FEATURE [Sketcher::SketchObject] Sketch024
  FullyConstrained = true
  sketch-geometry (7):
    g0: LineSegment StartX=0 StartY=0 StartZ=0 EndX=0 EndY=6 EndZ=0
    g1: Circle CenterX=0 CenterY=0 CenterZ=0 NormalX=0 NormalY=0 NormalZ=1 AngleXU=0 Radius=1
    g2: Circle CenterX=8 CenterY=6 CenterZ=0 NormalX=0 NormalY=0 NormalZ=1 AngleXU=0 Radius=1
    g3: BSplineCurve PolesCount=3 KnotsCount=2 Degree=2 IsPeriodic=0
    g4: GeomPoint X=0 Y=0 Z=0
    g5: GeomPoint X=8 Y=6 Z=0
    g6: LineSegment StartX=0 StartY=6 StartZ=0 EndX=8 EndY=6 EndZ=0
  constraints (14):
    c: Coincident(g0,g-1)
    c: Distance(g0) = 6
    c: Vertical(g0)
    c: Coincident(g3,g0)
    c: Weight(g1) = 1
    c: Equal(g1,g2)
    c: InternalAlignment(g1,g3)
    c: InternalAlignment(g2,g3)
    c: InternalAlignment(g4,g3)
    c: InternalAlignment(g5,g3)
    c: Block(g3)
    c: Coincident(g6,g0)
    c: Coincident(g6,g3)
    c: Horizontal(g6)
FEATURE [Part::Extrusion] Extrude018  label="caseScrewPillarBracket006"
  Base = -> Sketch024
  Dir = (0,0,1)
  DirMode = 2
  FaceMakerClass = Part::FaceMakerBullseye
  LengthFwd = 2.4
  LengthRev = 0
  Placement = pos=(103.7,29,6.77) rot=(0,-1,0;1.5708rad)
  Solid = true
  Symmetric = false
FEATURE [Sketcher::SketchObject] Sketch025
  FullyConstrained = true
  sketch-geometry (7):
    g0: LineSegment StartX=0 StartY=0 StartZ=0 EndX=0 EndY=6 EndZ=0
    g1: Circle CenterX=0 CenterY=0 CenterZ=0 NormalX=0 NormalY=0 NormalZ=1 AngleXU=0 Radius=1
    g2: Circle CenterX=8 CenterY=6 CenterZ=0 NormalX=0 NormalY=0 NormalZ=1 AngleXU=0 Radius=1
    g3: BSplineCurve PolesCount=3 KnotsCount=2 Degree=2 IsPeriodic=0
    g4: GeomPoint X=0 Y=0 Z=0
    g5: GeomPoint X=8 Y=6 Z=0
    g6: LineSegment StartX=0 StartY=6 StartZ=0 EndX=8 EndY=6 EndZ=0
  constraints (14):
    c: Coincident(g0,g-1)
    c: Distance(g0) = 6
    c: Vertical(g0)
    c: Coincident(g3,g0)
    c: Weight(g1) = 1
    c: Equal(g1,g2)
    c: InternalAlignment(g1,g3)
    c: InternalAlignment(g2,g3)
    c: InternalAlignment(g4,g3)
    c: InternalAlignment(g5,g3)
    c: Block(g3)
    c: Coincident(g6,g0)
    c: Coincident(g6,g3)
    c: Horizontal(g6)
FEATURE [Part::Extrusion] Extrude019  label="caseScrewPillarBracket007"
  Base = -> Sketch025
  Dir = (0,0,1)
  DirMode = 2
  FaceMakerClass = Part::FaceMakerBullseye
  LengthFwd = 2.4
  LengthRev = 0
  Placement = pos=(101.3,29,65.23) rot=(0,1,0;1.5708rad)
  Solid = true
  Symmetric = false
FEATURE [Part::Box] Box011  label="frontCaseScrewPillarBracket"
  AttacherType = Attacher::AttachEngine3D
  Height = 2.4
  Length = 16
  Placement = pos=(87,28,2.3) rot=(0,0,1;0rad)
  Width = 7
FEATURE [Part::Box] Box012  label="frontCaseScrewPillarBracket001"
  AttacherType = Attacher::AttachEngine3D
  Height = 2.4
  Length = 16
  Placement = pos=(87,28,67.3) rot=(0,0,1;0rad)
  Width = 7
FEATURE [Sketcher::SketchObject] Sketch026
  FullyConstrained = true
  sketch-geometry (17):
    g0: Circle CenterX=-3.5 CenterY=23.5 CenterZ=0 NormalX=0 NormalY=0 NormalZ=1 AngleXU=0 Radius=1
    g1: Circle CenterX=-1 CenterY=15.25 CenterZ=0 NormalX=0 NormalY=0 NormalZ=1 AngleXU=0 Radius=1
    g2: Circle CenterX=-3.5 CenterY=7 CenterZ=0 NormalX=0 NormalY=0 NormalZ=1 AngleXU=0 Radius=1
    g3: BSplineCurve PolesCount=3 KnotsCount=2 Degree=2 IsPeriodic=0
    g4: GeomPoint X=-3.5 Y=23.5 Z=0
    g5: GeomPoint X=-3.5 Y=7 Z=0
    g6: Circle CenterX=-4.8 CenterY=30.5 CenterZ=0 NormalX=0 NormalY=0 NormalZ=1 AngleXU=0 Radius=1
    g7: Circle CenterX=-3.5 CenterY=30.5 CenterZ=0 NormalX=0 NormalY=0 NormalZ=1 AngleXU=0 Radius=1
    g8: Circle CenterX=-3.5 CenterY=29.2 CenterZ=0 NormalX=0 NormalY=0 NormalZ=1 AngleXU=0 Radius=1
    g9: BSplineCurve PolesCount=3 KnotsCount=2 Degree=2 IsPeriodic=0
    g10: GeomPoint X=-4.8 Y=30.5 Z=0
    g11: GeomPoint X=-3.5 Y=29.2 Z=0
    g12: LineSegment StartX=-3.5 StartY=29.2 StartZ=0 EndX=-3.5 EndY=23.5 EndZ=0
    g13: LineSegment StartX=-4.8 StartY=30.5 StartZ=0 EndX=0 EndY=30.5 EndZ=0
    g14: LineSegment StartX=-3.5 StartY=5 StartZ=0 EndX=-3.5 EndY=7 EndZ=0
    g15: LineSegment StartX=0 StartY=5 StartZ=0 EndX=0 EndY=30.5 EndZ=0
    g16: LineSegment StartX=-3.5 StartY=5 StartZ=0 EndX=0 EndY=5 EndZ=0
  constraints (33):
    c: Weight(g0) = 1
    c: Equal(g0,g1)
    c: Equal(g0,g2)
    c: InternalAlignment(g0,g3)
    c: InternalAlignment(g1,g3)
    c: InternalAlignment(g2,g3)
    c: InternalAlignment(g4,g3)
    c: InternalAlignment(g5,g3)
    c: Block(g3)
    c: Weight(g6) = 1
    c: Equal(g6,g7)
    c: Equal(g6,g8)
    c: InternalAlignment(g6,g9)
    c: InternalAlignment(g7,g9)
    c: InternalAlignment(g8,g9)
    c: InternalAlignment(g10,g9)
    c: InternalAlignment(g11,g9)
    c: Block(g9)
    c: Coincident(g12,g9)
    c: Coincident(g12,g3)
    c: Vertical(g12)
    c: Coincident(g13,g9)
    c: Horizontal(g13)
    c: Distance(g13) = 4.8
    c: Coincident(g14,g3)
    c: Vertical(g14)
    c: Coincident(g15,g13)
    c: Vertical(g15)
    c: Tangent(g15,g1)
    c: Distance(g14) = 2
    c: Coincident(g16,g14)
    c: Horizontal(g16)
    c: Coincident(g15,g16)
FEATURE [Part::Feature] Face050
  shape: bbox 4.8 x 25.5 x 2e-07 mm, 1 faces, 0 solids (baked)
FEATURE [Part::Revolution] Revolve054  label="moreFrontCaseScrewPost001"
  Angle = 360
  Axis = (0,1,0)
  Base = (0,0,0)
  FaceMakerClass = Part::FaceMakerBullseye
  Placement = pos=(102.5,4.5,3.5) rot=(0,0,1;0rad)
  Solid = false
  Source = -> Face050
  Symmetric = false
FEATURE [Part::Feature] Face051
  shape: bbox 4.8 x 25.5 x 2e-07 mm, 1 faces, 0 solids (baked)
FEATURE [Part::Revolution] Revolve055  label="moreFrontCaseScrewPost002"
  Angle = 360
  Axis = (0,1,0)
  Base = (0,0,0)
  FaceMakerClass = Part::FaceMakerBullseye
  Placement = pos=(102.5,4.5,68.5) rot=(0,0,1;0rad)
  Solid = false
  Source = -> Face051
  Symmetric = false
FEATURE [Sketcher::SketchObject] Sketch027
  FullyConstrained = true
  sketch-geometry (10):
    g0: LineSegment StartX=-1.6 StartY=4.7 StartZ=0 EndX=-1.6 EndY=1.7 EndZ=0
    g1: LineSegment StartX=-3.5 StartY=4.7 StartZ=0 EndX=-1.6 EndY=4.7 EndZ=0
    g2: LineSegment StartX=-1.6 StartY=1.7 StartZ=0 EndX=-1.6 EndY=1.5 EndZ=0
    g3: LineSegment StartX=-1.6 StartY=1.5 StartZ=0 EndX=-5.2 EndY=1.5 EndZ=0
    g4: Circle CenterX=-3.5 CenterY=4.7 CenterZ=0 NormalX=0 NormalY=0 NormalZ=1 AngleXU=0 Radius=1
    g5: Circle CenterX=-3.59627 CenterY=2.99743 CenterZ=0 NormalX=0 NormalY=0 NormalZ=1 AngleXU=0 Radius=1
    g6: Circle CenterX=-5.2 CenterY=1.5 CenterZ=0 NormalX=0 NormalY=0 NormalZ=1 AngleXU=0 Radius=1
    g7: BSplineCurve PolesCount=3 KnotsCount=2 Degree=2 IsPeriodic=0
    g8: GeomPoint X=-3.5 Y=4.7 Z=0
    g9: GeomPoint X=-5.2 Y=1.5 Z=0
  constraints (23):
    c: Vertical(g0)
    c: Distance(g0) = 3
    c: Coincident(g1,g0)
    c: Horizontal(g1)
    c: Block(g0)
    c: Block(g1)
    c: Coincident(g2,g0)
    c: Vertical(g2)
    c: Distance(g2) = 0.2
    c: Coincident(g3,g2)
    c: Horizontal(g3)
    c: Block(g3)
    c: Coincident(g7,g1)
    c: Weight(g4) = 1
    c: Equal(g4,g5)
    c: Equal(g4,g6)
    c: Coincident(g7,g3)
    c: InternalAlignment(g4,g7)
    c: InternalAlignment(g5,g7)
    c: InternalAlignment(g6,g7)
    c: InternalAlignment(g8,g7)
    c: InternalAlignment(g9,g7)
    c: Block(g7)
FEATURE [Sketcher::SketchObject] Sketch028
  FullyConstrained = true
  sketch-geometry (18):
    g0: LineSegment StartX=0 StartY=3e-16 StartZ=0 EndX=0 EndY=1.7 EndZ=0
    g1: LineSegment StartX=-3.5 StartY=0 StartZ=0 EndX=-3.5 EndY=0.9 EndZ=0
    g2: Circle CenterX=-2.7 CenterY=1.7 CenterZ=0 NormalX=0 NormalY=0 NormalZ=1 AngleXU=0 Radius=1
    g3: Circle CenterX=-3.5 CenterY=1.7 CenterZ=0 NormalX=0 NormalY=0 NormalZ=1 AngleXU=0 Radius=1
    g4: Circle CenterX=-3.5 CenterY=0.9 CenterZ=0 NormalX=0 NormalY=0 NormalZ=1 AngleXU=0 Radius=1
    g5: BSplineCurve PolesCount=3 KnotsCount=2 Degree=2 IsPeriodic=0
    g6: GeomPoint X=-2.7 Y=1.7 Z=0
    g7: GeomPoint X=-3.5 Y=0.9 Z=0
    g8: LineSegment StartX=-3.5 StartY=0 StartZ=0 EndX=-3.5 EndY=-7 EndZ=0
    g9: LineSegment StartX=0 StartY=3e-16 StartZ=0 EndX=0 EndY=-7 EndZ=0
    g10: LineSegment StartX=-3.5 StartY=-7 StartZ=0 EndX=0 EndY=-7 EndZ=0
    g11: LineSegment StartX=-2.7 StartY=1.7 StartZ=0 EndX=-1.6 EndY=1.7 EndZ=0
    g12: LineSegment StartX=0 StartY=1.7 StartZ=0 EndX=0 EndY=4.5 EndZ=0
    g13: LineSegment StartX=0 StartY=4.5 StartZ=0 EndX=0 EndY=10.8 EndZ=0
    g14: LineSegment StartX=0 StartY=10.8 StartZ=0 EndX=-2 EndY=10.8 EndZ=0
    g15: LineSegment StartX=-1.6 StartY=4.7 StartZ=0 EndX=-1.6 EndY=1.7 EndZ=0
    g16: LineSegment StartX=-1.6 StartY=4.7 StartZ=0 EndX=-2 EndY=4.7 EndZ=0
    g17: LineSegment StartX=-2 StartY=4.7 StartZ=0 EndX=-2 EndY=10.8 EndZ=0
  constraints (44):
    c: Vertical(g0)
    c: Vertical(g1)
    c: Distance(g1) = 0.9
    c: Block(g0)
    c: Distance(g0) = 1.7
    c: Weight(g2) = 1
    c: Equal(g2,g3)
    c: Equal(g2,g4)
    c: Coincident(g5,g1)
    c: InternalAlignment(g2,g5)
    c: InternalAlignment(g3,g5)
    c: InternalAlignment(g4,g5)
    c: InternalAlignment(g6,g5)
    c: InternalAlignment(g7,g5)
    c: Block(g5)
    c: Coincident(g8,g1)
    c: Vertical(g8)
    c: Distance(g8) = 7
    c: Vertical(g9)
    c: Equal(g8,g9) = 7
    c: Coincident(g9,g0)
    c: Coincident(g10,g8)
    c: Coincident(g10,g9)
    c: Horizontal(g10)
    c: Coincident(g11,g5)
    c: Horizontal(g11)
    c: Coincident(g12,g0)
    c: Vertical(g12)
    c: Distance(g12) = 2.8
    c: Coincident(g13,g12)
    c: Vertical(g13)
    c: Distance(g13) = 6.3
    c: Coincident(g14,g13)
    c: Horizontal(g14)
    c: Distance(g14) = 2
    c: Vertical(g15)
    c: Distance(g15) = 3
    c: Block(g11)
    c: Coincident(g15,g11)
    c: Coincident(g16,g15)
    c: Horizontal(g16)
    c: Coincident(g17,g16)
    c: Coincident(g17,g14)
    c: Vertical(g17)
FEATURE [Part::Revolution] Revolve040  label="backCaseScrewRetainer001"
  Angle = 360
  Axis = (0,1,0)
  Base = (0,0,0)
  FaceMakerClass = Part::FaceMakerBullseye
  Placement = pos=(12.5,3,10) rot=(0,0,1;0rad)
  Solid = false
  Source = -> Face036
  Symmetric = false
FEATURE [Part::Feature] Face055
  shape: bbox 3.5 x 30.2 x 2e-07 mm, 1 faces, 0 solids (baked)
FEATURE [Part::Revolution] Revolve059  label="backCaseScrewPost"
  Angle = 360
  Axis = (0,1,0)
  Base = (0,0,0)
  FaceMakerClass = Part::FaceMakerBullseye
  Placement = pos=(12.5,4.5,10) rot=(0,0,1;0rad)
  Solid = false
  Source = -> Face055
  Symmetric = false
FEATURE [Part::Feature] Face056
  shape: bbox 3.5 x 30.2 x 2e-07 mm, 1 faces, 0 solids (baked)
FEATURE [Part::Revolution] Revolve060  label="backCaseScrewPost001"
  Angle = 360
  Axis = (0,1,0)
  Base = (0,0,0)
  FaceMakerClass = Part::FaceMakerBullseye
  Placement = pos=(12.5,4.5,62) rot=(0,0,1;0rad)
  Solid = false
  Source = -> Face056
  Symmetric = false
FEATURE [Part::Feature] Face057
  shape: bbox 3.5 x 17.8 x 2e-07 mm, 1 faces, 0 solids (baked)
FEATURE [Part::Revolution] Revolve061  label="removeToCreateScrewAndThreadedInsertHole"
  Angle = 360
  Axis = (0,1,0)
  Base = (0,0,0)
  FaceMakerClass = Part::FaceMakerBullseye
  Placement = pos=(12.5,0,10) rot=(0,0,1;0rad)
  Solid = false
  Source = -> Face057
  Symmetric = false
FEATURE [Part::Feature] Face058
  shape: bbox 3.5 x 17.8 x 2e-07 mm, 1 faces, 0 solids (baked)
FEATURE [Part::Revolution] Revolve062  label="removeToCreateScrewAndThreadedInsertHole001"
  Angle = 360
  Axis = (0,1,0)
  Base = (0,0,0)
  FaceMakerClass = Part::FaceMakerBullseye
  Placement = pos=(12.5,0,62) rot=(0,0,1;0rad)
  Solid = false
  Source = -> Face058
  Symmetric = false
FEATURE [Part::Feature] Face059
  shape: bbox 3.5 x 17.8 x 2e-07 mm, 1 faces, 0 solids (baked)
FEATURE [Part::Revolution] Revolve063  label="removeToCreateScrewAndThreadedInsertHole002"
  Angle = 360
  Axis = (0,1,0)
  Base = (0,0,0)
  FaceMakerClass = Part::FaceMakerBullseye
  Placement = pos=(89.5,0,68.5) rot=(0,0,1;0rad)
  Solid = false
  Source = -> Face059
  Symmetric = false
FEATURE [Part::Feature] Face060
  shape: bbox 3.5 x 17.8 x 2e-07 mm, 1 faces, 0 solids (baked)
FEATURE [Part::Revolution] Revolve064  label="removeToCreateScrewAndThreadedInsertHole003"
  Angle = 360
  Axis = (0,1,0)
  Base = (0,0,0)
  FaceMakerClass = Part::FaceMakerBullseye
  Placement = pos=(89.5,0,3.5) rot=(0,0,1;0rad)
  Solid = false
  Source = -> Face060
  Symmetric = false
FEATURE [Part::Feature] Face061
  shape: bbox 3.5 x 17.8 x 2e-07 mm, 1 faces, 0 solids (baked)
FEATURE [Part::Revolution] Revolve065  label="removeToCreateScrewAndThreadedInsertHole004"
  Angle = 360
  Axis = (0,1,0)
  Base = (0,0,0)
  FaceMakerClass = Part::FaceMakerBullseye
  Placement = pos=(102.5,4.7,3.5) rot=(0,0,1;0rad)
  Solid = false
  Source = -> Face061
  Symmetric = false
FEATURE [Part::Feature] Face062
  shape: bbox 3.5 x 17.8 x 2e-07 mm, 1 faces, 0 solids (baked)
FEATURE [Part::Revolution] Revolve066  label="removeToCreateScrewAndThreadedInsertHole005"
  Angle = 360
  Axis = (0,1,0)
  Base = (0,0,0)
  FaceMakerClass = Part::FaceMakerBullseye
  Placement = pos=(102.5,4.7,68.5) rot=(0,0,1;0rad)
  Solid = false
  Source = -> Face062
  Symmetric = false
FEATURE [Part::MultiFuse] Fusion047  label="makeHoles"
  Shapes = -> [Revolve066,Revolve065,Revolve064,Revolve063,Revolve062,Revolve061]
FEATURE [Part::Feature] Face063
  shape: bbox 3.6 x 3.2 x 2e-07 mm, 1 faces, 0 solids (baked)
FEATURE [Part::Revolution] Revolve067  label="moreFrontCaseScrewRetainer002"
  Angle = 360
  Axis = (0,1,0)
  Base = (0,0,0)
  FaceMakerClass = Part::FaceMakerBullseye
  Placement = pos=(102.5,4.5,68.5) rot=(0,0,1;0rad)
  Solid = false
  Source = -> Face063
  Symmetric = false
FEATURE [Part::Feature] Face064
  shape: bbox 3.6 x 3.2 x 2e-07 mm, 1 faces, 0 solids (baked)
FEATURE [Part::Revolution] Revolve068  label="moreFrontCaseScrewRetainer003"
  Angle = 360
  Axis = (0,1,0)
  Base = (0,0,0)
  FaceMakerClass = Part::FaceMakerBullseye
  Placement = pos=(102.5,4.5,3.5) rot=(0,0,1;0rad)
  Solid = false
  Source = -> Face064
  Symmetric = false
FEATURE [Part::Feature] Face065
  shape: bbox 3.5 x 17.8 x 2e-07 mm, 1 faces, 0 solids (baked)
FEATURE [Part::Revolution] Revolve069  label="removeToCreateScrewAndThreadedInsertHole006"
  Angle = 360
  Axis = (0,1,0)
  Base = (0,0,0)
  FaceMakerClass = Part::FaceMakerBullseye
  Placement = pos=(12.5,0,10) rot=(0,0,1;0rad)
  Solid = false
  Source = -> Face065
  Symmetric = false
FEATURE [Part::Feature] Face066
  shape: bbox 3.5 x 17.8 x 2e-07 mm, 1 faces, 0 solids (baked)
FEATURE [Part::Revolution] Revolve070  label="removeToCreateScrewAndThreadedInsertHole007"
  Angle = 360
  Axis = (0,1,0)
  Base = (0,0,0)
  FaceMakerClass = Part::FaceMakerBullseye
  Placement = pos=(12.5,0,62) rot=(0,0,1;0rad)
  Solid = false
  Source = -> Face066
  Symmetric = false
FEATURE [Part::Feature] Face067
  shape: bbox 3.5 x 17.8 x 2e-07 mm, 1 faces, 0 solids (baked)
FEATURE [Part::Revolution] Revolve071  label="removeToCreateScrewAndThreadedInsertHole008"
  Angle = 360
  Axis = (0,1,0)
  Base = (0,0,0)
  FaceMakerClass = Part::FaceMakerBullseye
  Placement = pos=(89.5,0,68.5) rot=(0,0,1;0rad)
  Solid = false
  Source = -> Face067
  Symmetric = false
FEATURE [Part::Feature] Face068
  shape: bbox 3.5 x 17.8 x 2e-07 mm, 1 faces, 0 solids (baked)
FEATURE [Part::Revolution] Revolve072  label="removeToCreateScrewAndThreadedInsertHole009"
  Angle = 360
  Axis = (0,1,0)
  Base = (0,0,0)
  FaceMakerClass = Part::FaceMakerBullseye
  Placement = pos=(89.5,0,3.5) rot=(0,0,1;0rad)
  Solid = false
  Source = -> Face068
  Symmetric = false
FEATURE [Part::Feature] Face069
  shape: bbox 3.5 x 17.8 x 2e-07 mm, 1 faces, 0 solids (baked)
FEATURE [Part::Feature] Face070
  shape: bbox 3.5 x 17.8 x 2e-07 mm, 1 faces, 0 solids (baked)
FEATURE [Part::Revolution] Revolve073  label="removeToCreateScrewAndThreadedInsertHole010"
  Angle = 360
  Axis = (0,1,0)
  Base = (0,0,0)
  FaceMakerClass = Part::FaceMakerBullseye
  Placement = pos=(102.5,4.7,3.5) rot=(0,0,1;0rad)
  Solid = false
  Source = -> Face069
  Symmetric = false
FEATURE [Part::Revolution] Revolve074  label="removeToCreateScrewAndThreadedInsertHole011"
  Angle = 360
  Axis = (0,1,0)
  Base = (0,0,0)
  FaceMakerClass = Part::FaceMakerBullseye
  Placement = pos=(102.5,4.7,68.5) rot=(0,0,1;0rad)
  Solid = false
  Source = -> Face070
  Symmetric = false
FEATURE [Part::MultiFuse] Fusion048  label="makeHoles001"
  Shapes = -> [Revolve074,Revolve073,Revolve072,Revolve071,Revolve070,Revolve069]
FEATURE [Part::MultiFuse] Fusion049  label="caseScrewRetainers"
  Shapes = -> [Revolve067,Revolve068,Revolve048,Revolve047,Revolve039,Revolve040]
FEATURE [Part::Cut] Cut015  label="caseScrewRetainers001"
  Base = -> Fusion049
  Tool = -> Fusion048
FEATURE [Part::MultiFuse] Fusion050  label="casePillars"
  Shapes = -> [Revolve055,Revolve054,Revolve043,Revolve046,Revolve059,Revolve060]
FEATURE [Part::Feature] Face071 .. Face076  x6 (patterned run collapsed; names and placements below)
  shape: bbox 3.5 x 17.8 x 2e-07 mm, 1 faces, 0 solids (baked)
FEATURE [Part::Revolution] Revolve075  label="removeToCreateScrewAndThreadedInsertHole012"
  Angle = 360
  Axis = (0,1,0)
  Base = (0,0,0)
  FaceMakerClass = Part::FaceMakerBullseye
  Placement = pos=(12.5,0,10) rot=(0,0,1;0rad)
  Solid = false
  Source = -> Face071
  Symmetric = false
FEATURE [Part::Revolution] Revolve076  label="removeToCreateScrewAndThreadedInsertHole013"
  Angle = 360
  Axis = (0,1,0)
  Base = (0,0,0)
  FaceMakerClass = Part::FaceMakerBullseye
  Placement = pos=(12.5,0,62) rot=(0,0,1;0rad)
  Solid = false
  Source = -> Face072
  Symmetric = false
FEATURE [Part::Revolution] Revolve077  label="removeToCreateScrewAndThreadedInsertHole014"
  Angle = 360
  Axis = (0,1,0)
  Base = (0,0,0)
  FaceMakerClass = Part::FaceMakerBullseye
  Placement = pos=(89.5,0,68.5) rot=(0,0,1;0rad)
  Solid = false
  Source = -> Face073
  Symmetric = false
FEATURE [Part::Revolution] Revolve078  label="removeToCreateScrewAndThreadedInsertHole015"
  Angle = 360
  Axis = (0,1,0)
  Base = (0,0,0)
  FaceMakerClass = Part::FaceMakerBullseye
  Placement = pos=(89.5,0,3.5) rot=(0,0,1;0rad)
  Solid = false
  Source = -> Face074
  Symmetric = false
FEATURE [Part::Revolution] Revolve079  label="removeToCreateScrewAndThreadedInsertHole016"
  Angle = 360
  Axis = (0,1,0)
  Base = (0,0,0)
  FaceMakerClass = Part::FaceMakerBullseye
  Placement = pos=(102.5,4.7,3.5) rot=(0,0,1;0rad)
  Solid = false
  Source = -> Face075
  Symmetric = false
FEATURE [Part::Revolution] Revolve080  label="removeToCreateScrewAndThreadedInsertHole017"
  Angle = 360
  Axis = (0,1,0)
  Base = (0,0,0)
  FaceMakerClass = Part::FaceMakerBullseye
  Placement = pos=(102.5,4.7,68.5) rot=(0,0,1;0rad)
  Solid = false
  Source = -> Face076
  Symmetric = false
FEATURE [Part::MultiFuse] Fusion051  label="makeHoles002"
  Shapes = -> [Revolve080,Revolve079,Revolve078,Revolve077,Revolve076,Revolve075]
FEATURE [Part::Cut] Cut016  label="caesPillars"
  Base = -> Fusion050
  Tool = -> Fusion051
FEATURE [Part::Revolution] Revolve009  label="plugHousing016"
  Angle = 360
  Axis = (0,1,0)
  Base = (0,0,0)
  FaceMakerClass = Part::FaceMakerBullseye
  Placement = pos=(0,0,36.15) rot=(0,0,1;0rad)
  Solid = false
  Source = -> Face012
  Symmetric = false
FEATURE [Part::MultiFuse] Fusion014  label="plugHousing023"
  Placement = pos=(0,0,0) rot=(0,0,1;1.5708rad)
  Shapes = -> [Revolve011,Revolve009]
FEATURE [Part::Revolution] Revolve010  label="plugHousing017"
  Angle = 360
  Axis = (0,1,0)
  Base = (0,0,0)
  FaceMakerClass = Part::FaceMakerBullseye
  Placement = pos=(0,0,36.15) rot=(0,0,1;0rad)
  Solid = false
  Source = -> Face014
  Symmetric = false
FEATURE [Part::MultiFuse] Fusion015  label="plugHousing024"
  Placement = pos=(0,0,0) rot=(0,0,1;1.5708rad)
  Shapes = -> [Revolve010,Revolve015]
FEATURE [Part::Revolution] Revolve014  label="plugHousing026"
  Angle = 360
  Axis = (0,1,0)
  Base = (0,0,0)
  FaceMakerClass = Part::FaceMakerBullseye
  Placement = pos=(0,0,36.15) rot=(0,0,1;0rad)
  Solid = false
  Source = -> Face011
  Symmetric = false
FEATURE [Part::Revolution] Revolve013  label="plugHousing025"
  Angle = 360
  Axis = (0,1,0)
  Base = (0,0,0)
  FaceMakerClass = Part::FaceMakerBullseye
  Placement = pos=(0,0,36.15) rot=(0,0,1;0rad)
  Solid = false
  Source = -> Face015
  Symmetric = false
FEATURE [Part::MultiFuse] Fusion016  label="plugHousing028"
  Placement = pos=(0,19,0) rot=(0,0,1;3.14159rad)
  Shapes = -> [Fusion014,Fusion013]
FEATURE [Part::MultiFuse] Fusion011  label="plugHousing018"
  Placement = pos=(0,0,0) rot=(0,0,1;1.5708rad)
  Shapes = -> [Revolve014,Revolve013]
FEATURE [Part::MultiFuse] Fusion012  label="plugHousing019"
  Placement = pos=(0,19,0) rot=(0,0,1;3.14159rad)
  Shapes = -> [Fusion011,Fusion015]
FEATURE [Part::MultiFuse] Fusion017  label="plugHousing029"
  Placement = pos=(122.621,0,-0.15) rot=(0,0,1;0rad)
  Shapes = -> [Fusion016,Fusion012]
FEATURE [Part::MultiFuse] Fusion052  label="casePillarRetainers"
  Shapes = -> [Extrude012,Extrude013,Extrude014,Extrude015,Extrude016,Extrude017,Extrude018,Extrude019,Box011,Box012]
FEATURE [Part::Feature] Face077
  shape: bbox 3.5 x 17.8 x 2e-07 mm, 1 faces, 0 solids (baked)
FEATURE [Part::Revolution] Revolve081  label="removeToCreateScrewAndThreadedInsertHole018"
  Angle = 360
  Axis = (0,1,0)
  Base = (0,0,0)
  FaceMakerClass = Part::FaceMakerBullseye
  Placement = pos=(62.3,30.3,19.7) rot=(0,0,1;0rad)
  Solid = false
  Source = -> Face077
  Symmetric = false
FEATURE [Part::Feature] Face078
  shape: bbox 3.5 x 17.8 x 2e-07 mm, 1 faces, 0 solids (baked)
FEATURE [Part::Revolution] Revolve082  label="removeToCreateScrewAndThreadedInsertHole019"
  Angle = 360
  Axis = (0,1,0)
  Base = (0,0,0)
  FaceMakerClass = Part::FaceMakerBullseye
  Placement = pos=(62.3,30.3,51.7) rot=(0,0,1;0rad)
  Solid = false
  Source = -> Face078
  Symmetric = false
FEATURE [Part::Feature] Face079
  shape: bbox 3.5 x 17.8 x 2e-07 mm, 1 faces, 0 solids (baked)
FEATURE [Part::Revolution] Revolve083  label="removeToCreateScrewAndThreadedInsertHole020"
  Angle = 360
  Axis = (0,1,0)
  Base = (0,0,0)
  FaceMakerClass = Part::FaceMakerBullseye
  Placement = pos=(30.3,30.3,19.7) rot=(0,0,1;0rad)
  Solid = false
  Source = -> Face079
  Symmetric = false
FEATURE [Part::Feature] Face080
  shape: bbox 3.5 x 17.8 x 2e-07 mm, 1 faces, 0 solids (baked)
FEATURE [Part::Revolution] Revolve084  label="removeToCreateScrewAndThreadedInsertHole021"
  Angle = 360
  Axis = (0,1,0)
  Base = (0,0,0)
  FaceMakerClass = Part::FaceMakerBullseye
  Placement = pos=(30.3,30.3,51.7) rot=(0,0,1;0rad)
  Solid = false
  Source = -> Face080
  Symmetric = false
FEATURE [Part::MultiFuse] Fusion053  label="createThreadedInsertHolesForFan"
  Shapes = -> [Revolve081,Revolve082,Revolve083,Revolve084]
FEATURE [Part::Cut] Cut017  label="fanScrewHousing001"
  Base = -> Fusion046
  Tool = -> Fusion053
FEATURE [Part::Feature] Face081
  shape: bbox 3.5 x 17.8 x 2e-07 mm, 1 faces, 0 solids (baked)
FEATURE [Part::Revolution] Revolve085  label="removeToCreateScrewAndThreadedInsertHole022"
  Angle = 360
  Axis = (0,1,0)
  Base = (0,0,0)
  FaceMakerClass = Part::FaceMakerBullseye
  Placement = pos=(62.3,30.3,19.7) rot=(0,0,1;0rad)
  Solid = false
  Source = -> Face081
  Symmetric = false
FEATURE [Part::Feature] Face082
  shape: bbox 3.5 x 17.8 x 2e-07 mm, 1 faces, 0 solids (baked)
FEATURE [Part::Revolution] Revolve086  label="removeToCreateScrewAndThreadedInsertHole023"
  Angle = 360
  Axis = (0,1,0)
  Base = (0,0,0)
  FaceMakerClass = Part::FaceMakerBullseye
  Placement = pos=(62.3,30.3,51.7) rot=(0,0,1;0rad)
  Solid = false
  Source = -> Face082
  Symmetric = false
FEATURE [Part::Feature] Face083
  shape: bbox 3.5 x 17.8 x 2e-07 mm, 1 faces, 0 solids (baked)
FEATURE [Part::Revolution] Revolve087  label="removeToCreateScrewAndThreadedInsertHole024"
  Angle = 360
  Axis = (0,1,0)
  Base = (0,0,0)
  FaceMakerClass = Part::FaceMakerBullseye
  Placement = pos=(30.3,30.3,19.7) rot=(0,0,1;0rad)
  Solid = false
  Source = -> Face083
  Symmetric = false
FEATURE [Part::Feature] Face084
  shape: bbox 3.5 x 17.8 x 2e-07 mm, 1 faces, 0 solids (baked)
FEATURE [Part::Revolution] Revolve088  label="removeToCreateScrewAndThreadedInsertHole025"
  Angle = 360
  Axis = (0,1,0)
  Base = (0,0,0)
  FaceMakerClass = Part::FaceMakerBullseye
  Placement = pos=(30.3,30.3,51.7) rot=(0,0,1;0rad)
  Solid = false
  Source = -> Face084
  Symmetric = false
FEATURE [Part::MultiFuse] Fusion054  label="createThreadedInsertHolesForFan001"
  Shapes = -> [Revolve085,Revolve086,Revolve087,Revolve088]
FEATURE [Part::Cut] Cut018  label="top007"
  Base = -> Fusion040
  Tool = -> Fusion054
FEATURE [Sketcher::SketchObject] Sketch029
  FullyConstrained = false
  Placement = pos=(0,0,0) rot=(1,0,0;1.5708rad)
  sketch-geometry (24):
    g0: ArcOfCircle CenterX=-4 CenterY=-10.5 CenterZ=0 NormalX=0 NormalY=0 NormalZ=1 AngleXU=0 Radius=1.5 StartAngle=6e-16 EndAngle=3.14159
    g1: ArcOfCircle CenterX=-34.2 CenterY=-10.5 CenterZ=0 NormalX=0 NormalY=0 NormalZ=1 AngleXU=0 Radius=1.5 StartAngle=0 EndAngle=3.14159
    g2: ArcOfCircle CenterX=-34.2 CenterY=-27.7 CenterZ=0 NormalX=0 NormalY=0 NormalZ=1 AngleXU=0 Radius=1.5 StartAngle=3.14159 EndAngle=6.28319
    g3: ArcOfCircle CenterX=-4 CenterY=-27.7 CenterZ=0 NormalX=0 NormalY=0 NormalZ=1 AngleXU=0 Radius=1.5 StartAngle=3.1416 EndAngle=6.28319
    g4: ArcOfCircle CenterX=-10 CenterY=-4.3 CenterZ=0 NormalX=0 NormalY=0 NormalZ=1 AngleXU=0 Radius=1.5 StartAngle=2e-16 EndAngle=3.14159
    g5: ArcOfCircle CenterX=-16.1 CenterY=-1.8 CenterZ=0 NormalX=0 NormalY=0 NormalZ=1 AngleXU=0 Radius=1.5 StartAngle=5e-16 EndAngle=3.14159
    g6: ArcOfCircle CenterX=-22.1 CenterY=-1.8 CenterZ=0 NormalX=0 NormalY=0 NormalZ=1 AngleXU=0 Radius=1.5 StartAngle=5e-16 EndAngle=3.14159
    g7: ArcOfCircle CenterX=-28.2 CenterY=-4.3 CenterZ=0 NormalX=0 NormalY=0 NormalZ=1 AngleXU=0 Radius=1.5 StartAngle=2e-16 EndAngle=3.14159
    g8: ArcOfCircle CenterX=-10 CenterY=-33.9 CenterZ=0 NormalX=0 NormalY=0 NormalZ=1 AngleXU=0 Radius=1.5 StartAngle=3.14159 EndAngle=6.28319
    g9: ArcOfCircle CenterX=-16.1 CenterY=-36.4 CenterZ=0 NormalX=0 NormalY=0 NormalZ=1 AngleXU=0 Radius=1.5 StartAngle=3.14159 EndAngle=6.28319
    g10: ArcOfCircle CenterX=-22.1 CenterY=-36.4 CenterZ=0 NormalX=0 NormalY=0 NormalZ=1 AngleXU=0 Radius=1.5 StartAngle=3.14159 EndAngle=6.28319
    g11: ArcOfCircle CenterX=-28.2 CenterY=-33.9 CenterZ=0 NormalX=0 NormalY=0 NormalZ=1 AngleXU=0 Radius=1.5 StartAngle=3.14159 EndAngle=6.28319
    g12: LineSegment StartX=-35.7 StartY=-10.5 StartZ=0 EndX=-35.7 EndY=-27.7 EndZ=0
    g13: LineSegment StartX=-32.7 StartY=-10.5 StartZ=0 EndX=-32.7 EndY=-27.7 EndZ=0
    g14: LineSegment StartX=-29.7 StartY=-33.9 StartZ=0 EndX=-29.7 EndY=-4.3 EndZ=0
    g15: LineSegment StartX=-26.7 StartY=-33.9 StartZ=0 EndX=-26.7 EndY=-4.3 EndZ=0
    g16: LineSegment StartX=-2.5 StartY=-10.5 StartZ=0 EndX=-2.5 EndY=-27.7 EndZ=0
    g17: LineSegment StartX=-8.5 StartY=-4.3 StartZ=0 EndX=-8.5 EndY=-33.9 EndZ=0
    g18: LineSegment StartX=-5.5 StartY=-10.5 StartZ=0 EndX=-5.5 EndY=-27.7 EndZ=0
    g19: LineSegment StartX=-11.5 StartY=-4.3 StartZ=0 EndX=-11.5 EndY=-33.9 EndZ=0
    g20: LineSegment StartX=-14.6 StartY=-1.8 StartZ=0 EndX=-14.6 EndY=-36.4 EndZ=0
    g21: LineSegment StartX=-17.6 StartY=-1.8 StartZ=0 EndX=-17.6 EndY=-36.4 EndZ=0
    g22: LineSegment StartX=-20.6 StartY=-36.4 StartZ=0 EndX=-20.6 EndY=-1.8 EndZ=0
    g23: LineSegment StartX=-23.6 StartY=-1.8 StartZ=0 EndX=-23.6 EndY=-36.4 EndZ=0
  constraints (48):
    c: Block(g0)
    c: Block(g1)
    c: Block(g2)
    c: Block(g3)
    c: Block(g4)
    c: Block(g5)
    c: Block(g6)
    c: Block(g7)
    c: Block(g8)
    c: Block(g9)
    c: Block(g10)
    c: Block(g11)
    c: Coincident(g12,g1)
    c: Coincident(g12,g2)
    c: Vertical(g12)
    c: Coincident(g13,g1)
    c: Coincident(g13,g2)
    c: Vertical(g13)
    c: Coincident(g14,g11)
    c: Coincident(g14,g7)
    c: Vertical(g14)
    c: Coincident(g15,g11)
    c: Coincident(g15,g7)
    c: Vertical(g15)
    c: Coincident(g16,g0)
    c: Coincident(g16,g3)
    c: Vertical(g16)
    c: Coincident(g17,g4)
    c: Coincident(g17,g8)
    c: Vertical(g17)
    c: Coincident(g18,g0)
    c: Coincident(g18,g3)
    c: Vertical(g18)
    c: Coincident(g19,g4)
    c: Coincident(g19,g8)
    c: Vertical(g19)
    c: Coincident(g20,g5)
    c: Coincident(g20,g9)
    c: Vertical(g20)
    c: Coincident(g21,g5)
    c: Coincident(g21,g9)
    c: Vertical(g21)
    c: Coincident(g22,g10)
    c: Coincident(g22,g6)
    c: Vertical(g22)
    c: Coincident(g23,g6)
    c: Coincident(g23,g10)
    c: Vertical(g23)
FEATURE [Part::Extrusion] Extrude020  label="removeToCreateFanGrillHoles"
  Base = -> Sketch029
  Dir = (0,-1,6e-16)
  DirMode = 2
  FaceMakerClass = Part::FaceMakerBullseye
  LengthFwd = 10
  LengthRev = 0
  Placement = pos=(65.4,44,54.82) rot=(0,0,1;0rad)
  Solid = true
  Symmetric = false
FEATURE [Part::MultiFuse] Fusion055  label="top008"
  Shapes = -> [Cut017,Cut018]
FEATURE [Part::Cut] Cut019  label="top009"
  Base = -> Fusion055
  Tool = -> Extrude020
FEATURE [App::MeasureDistance] Distance003  label="Distance: 71.95 mm"
  Distance = 71.9513
  P1 = (117,38,72)
  P2 = (117,38,0.0487319)
FEATURE [Sketcher::SketchObject] Sketch030
  FullyConstrained = true
  Placement = pos=(117,19,0) rot=(0.57735,0.57735,0.57735;2.0944rad)
  sketch-geometry (48):
    g0: LineSegment StartX=-49.19 StartY=69.25 StartZ=0 EndX=-49.19 EndY=66.25 EndZ=0
    g1: LineSegment StartX=-49.19 StartY=63.5 StartZ=0 EndX=-49.19 EndY=60.5 EndZ=0
    g2: LineSegment StartX=-49.19 StartY=57.75 StartZ=0 EndX=-49.19 EndY=54.75 EndZ=0
    g3: LineSegment StartX=-49.19 StartY=52 StartZ=0 EndX=-49.19 EndY=49 EndZ=0
    g4: LineSegment StartX=-49.19 StartY=46.25 StartZ=0 EndX=-49.19 EndY=43.25 EndZ=0
    g5: LineSegment StartX=-49.19 StartY=40.5 StartZ=0 EndX=-49.19 EndY=37.5 EndZ=0
    g6: LineSegment StartX=-49.19 StartY=34.5 StartZ=0 EndX=-49.19 EndY=31.5 EndZ=0
    g7: LineSegment StartX=-49.19 StartY=28.75 StartZ=0 EndX=-49.19 EndY=25.75 EndZ=0
    g8: LineSegment StartX=-49.19 StartY=23 StartZ=0 EndX=-49.19 EndY=20 EndZ=0
    g9: LineSegment StartX=-49.19 StartY=17.25 StartZ=0 EndX=-49.19 EndY=14.25 EndZ=0
    g10: LineSegment StartX=-49.19 StartY=11.5 StartZ=0 EndX=-49.19 EndY=8.5 EndZ=0
    g11: LineSegment StartX=-49.19 StartY=5.75 StartZ=0 EndX=-49.19 EndY=2.75 EndZ=0
    g12: ArcOfCircle CenterX=-1.5 CenterY=67.75 CenterZ=0 NormalX=0 NormalY=0 NormalZ=1 AngleXU=0 Radius=1.5 StartAngle=4.71239 EndAngle=7.85398
    g13: ArcOfCircle CenterX=-1.5 CenterY=62 CenterZ=0 NormalX=0 NormalY=0 NormalZ=1 AngleXU=0 Radius=1.5 StartAngle=4.71239 EndAngle=7.85398
    g14: ArcOfCircle CenterX=-1.5 CenterY=56.25 CenterZ=0 NormalX=0 NormalY=0 NormalZ=1 AngleXU=0 Radius=1.5 StartAngle=4.71239 EndAngle=7.85398
    g15: ArcOfCircle CenterX=-11.49 CenterY=50.5 CenterZ=0 NormalX=0 NormalY=0 NormalZ=1 AngleXU=0 Radius=1.5 StartAngle=4.71239 EndAngle=7.85398
    g16: ArcOfCircle CenterX=-16.28 CenterY=44.75 CenterZ=0 NormalX=0 NormalY=0 NormalZ=1 AngleXU=0 Radius=1.5 StartAngle=4.71239 EndAngle=7.85398
    g17: ArcOfCircle CenterX=-18.2337 CenterY=39 CenterZ=0 NormalX=0 NormalY=0 NormalZ=1 AngleXU=0 Radius=1.5 StartAngle=4.71485 EndAngle=7.85398
    g18: ArcOfCircle CenterX=-16.2837 CenterY=27.25 CenterZ=0 NormalX=0 NormalY=0 NormalZ=1 AngleXU=0 Radius=1.5 StartAngle=4.71485 EndAngle=7.85398
    g19: ArcOfCircle CenterX=-18.2337 CenterY=33 CenterZ=0 NormalX=0 NormalY=0 NormalZ=1 AngleXU=0 Radius=1.5 StartAngle=4.71485 EndAngle=7.85398
    g20: ArcOfCircle CenterX=-11.49 CenterY=21.5 CenterZ=0 NormalX=0 NormalY=0 NormalZ=1 AngleXU=0 Radius=1.5 StartAngle=4.71239 EndAngle=7.85398
    g21: ArcOfCircle CenterX=-1.5 CenterY=4.25 CenterZ=0 NormalX=0 NormalY=0 NormalZ=1 AngleXU=0 Radius=1.5 StartAngle=4.71239 EndAngle=7.85398
    g22: ArcOfCircle CenterX=-1.5 CenterY=10 CenterZ=0 NormalX=0 NormalY=0 NormalZ=1 AngleXU=0 Radius=1.5 StartAngle=4.71239 EndAngle=7.85398
    g23: ArcOfCircle CenterX=-1.5 CenterY=15.75 CenterZ=0 NormalX=0 NormalY=0 NormalZ=1 AngleXU=0 Radius=1.5 StartAngle=4.71239 EndAngle=7.85398
    g24: LineSegment StartX=-49.19 StartY=69.25 StartZ=0 EndX=-1.5 EndY=69.25 EndZ=0
    g25: LineSegment StartX=-49.19 StartY=66.25 StartZ=0 EndX=-1.5 EndY=66.25 EndZ=0
    g26: LineSegment StartX=-49.19 StartY=63.5 StartZ=0 EndX=-1.5 EndY=63.5 EndZ=0
    g27: LineSegment StartX=-49.19 StartY=60.5 StartZ=0 EndX=-1.5 EndY=60.5 EndZ=0
    g28: LineSegment StartX=-49.19 StartY=57.75 StartZ=0 EndX=-1.5 EndY=57.75 EndZ=0
    g29: LineSegment StartX=-49.19 StartY=54.75 StartZ=0 EndX=-1.5 EndY=54.75 EndZ=0
    g30: LineSegment StartX=-49.19 StartY=52 StartZ=0 EndX=-11.49 EndY=52 EndZ=0
    g31: LineSegment StartX=-49.19 StartY=49 StartZ=0 EndX=-11.49 EndY=49 EndZ=0
    g32: LineSegment StartX=-49.19 StartY=46.25 StartZ=0 EndX=-16.28 EndY=46.25 EndZ=0
    g33: LineSegment StartX=-49.19 StartY=43.25 StartZ=0 EndX=-16.28 EndY=43.25 EndZ=0
    g34: LineSegment StartX=-49.19 StartY=40.5 StartZ=0 EndX=-18.2337 EndY=40.5 EndZ=0
    g35: LineSegment StartX=-49.19 StartY=37.5 StartZ=0 EndX=-18.23 EndY=37.5 EndZ=0
    g36: LineSegment StartX=-49.19 StartY=34.5 StartZ=0 EndX=-18.2337 EndY=34.5 EndZ=0
    g37: LineSegment StartX=-49.19 StartY=31.5 StartZ=0 EndX=-18.23 EndY=31.5 EndZ=0
    g38: LineSegment StartX=-49.19 StartY=28.75 StartZ=0 EndX=-16.2837 EndY=28.75 EndZ=0
    g39: LineSegment StartX=-49.19 StartY=25.75 StartZ=0 EndX=-16.28 EndY=25.75 EndZ=0
    g40: LineSegment StartX=-49.19 StartY=23 StartZ=0 EndX=-11.49 EndY=23 EndZ=0
    g41: LineSegment StartX=-49.19 StartY=20 StartZ=0 EndX=-11.49 EndY=20 EndZ=0
    g42: LineSegment StartX=-49.19 StartY=17.25 StartZ=0 EndX=-1.5 EndY=17.25 EndZ=0
    g43: LineSegment StartX=-49.19 StartY=14.25 StartZ=0 EndX=-1.5 EndY=14.25 EndZ=0
    g44: LineSegment StartX=-49.19 StartY=11.5 StartZ=0 EndX=-1.5 EndY=11.5 EndZ=0
    g45: LineSegment StartX=-49.19 StartY=8.5 StartZ=0 EndX=-1.5 EndY=8.5 EndZ=0
    g46: LineSegment StartX=-49.19 StartY=5.75 StartZ=0 EndX=-1.5 EndY=5.75 EndZ=0
    g47: LineSegment StartX=-49.19 StartY=2.75 StartZ=0 EndX=-1.5 EndY=2.75 EndZ=0
  constraints (120):
    c: Vertical(g0)
    c: Distance(g0) = 3
    c: Block(g0)
    c: Vertical(g1)
    c: Distance(g1) = 3
    c: Vertical(g2)
    c: Equal(g0,g2) = 3
    c: Block(g2)
    c: Vertical(g3)
    c: Equal(g1,g3) = 3
    c: Vertical(g4)
    c: Equal(g0,g4) = 3
    c: Block(g4)
    c: Vertical(g5)
    c: Equal(g1,g5) = 3
    c: Vertical(g6)
    c: Equal(g0,g6) = 3
    c: Block(g6)
    c: Vertical(g7)
    c: Equal(g1,g7) = 3
    c: Vertical(g8)
    c: Equal(g0,g8) = 3
    c: Block(g8)
    c: Vertical(g9)
    c: Equal(g1,g9) = 3
    c: Vertical(g10)
    c: Equal(g0,g10) = 3
    c: Block(g10)
    c: Vertical(g11)
    c: Equal(g1,g11) = 3
    c: Block(g12)
    c: Block(g13)
    c: Block(g14)
    c: Block(g15)
    c: Block(g16)
    c: Block(g17)
    c: Block(g18)
    c: Block(g19)
    c: Block(g20)
    c: Block(g21)
    c: Block(g22)
    c: Block(g23)
    c: Block(g11)
    c: Block(g9)
    c: Block(g7)
    c: Block(g5)
    c: Block(g3)
    c: Block(g1)
    c: Coincident(g24,g0)
    c: Coincident(g24,g12)
    c: Horizontal(g24)
    c: Coincident(g25,g0)
    c: Coincident(g25,g12)
    c: Horizontal(g25)
    c: Coincident(g26,g1)
    c: Coincident(g26,g13)
    c: Horizontal(g26)
    c: Coincident(g27,g1)
    c: Coincident(g27,g13)
    c: Horizontal(g27)
    c: Coincident(g28,g2)
    c: Coincident(g28,g14)
    c: Horizontal(g28)
    c: Coincident(g29,g2)
    c: Coincident(g29,g14)
    c: Horizontal(g29)
    c: Coincident(g30,g3)
    c: Coincident(g30,g15)
    c: Horizontal(g30)
    c: Coincident(g31,g3)
    c: Coincident(g31,g15)
    c: Horizontal(g31)
    c: Coincident(g32,g4)
    c: Coincident(g32,g16)
    c: Horizontal(g32)
    c: Coincident(g33,g4)
    c: Coincident(g33,g16)
    c: Horizontal(g33)
    c: Coincident(g34,g5)
    c: Coincident(g34,g17)
    c: Horizontal(g34)
    c: Coincident(g35,g5)
    c: Coincident(g35,g17)
    c: Horizontal(g35)
    c: Coincident(g36,g6)
    c: Coincident(g36,g19)
    c: Horizontal(g36)
    c: Coincident(g37,g6)
    c: Coincident(g37,g19)
    c: Horizontal(g37)
    c: Coincident(g38,g7)
    c: Coincident(g38,g18)
    c: Horizontal(g38)
    c: Coincident(g39,g7)
    c: Coincident(g39,g18)
    c: Horizontal(g39)
    c: Coincident(g40,g8)
    c: Coincident(g40,g20)
    c: Horizontal(g40)
    c: Coincident(g41,g8)
    c: Coincident(g41,g20)
    c: Horizontal(g41)
    c: Coincident(g42,g9)
    c: Coincident(g42,g23)
    c: Horizontal(g42)
    c: Coincident(g43,g9)
    c: Coincident(g43,g23)
    c: Horizontal(g43)
    c: Coincident(g44,g10)
    c: Coincident(g44,g22)
    c: Horizontal(g44)
    c: Coincident(g45,g10)
    c: Coincident(g45,g22)
    c: Horizontal(g45)
    c: Coincident(g46,g11)
    c: Coincident(g46,g21)
    c: Horizontal(g46)
    c: Coincident(g47,g11)
    c: Coincident(g47,g21)
    c: Horizontal(g47)
FEATURE [Sketcher::SketchObject] Sketch031
  FullyConstrained = true
  Placement = pos=(117,19,0) rot=(0.57735,0.57735,0.57735;2.0944rad)
  sketch-geometry (24):
    g0: ArcOfCircle CenterX=-49.19 CenterY=67.75 CenterZ=0 NormalX=0 NormalY=0 NormalZ=1 AngleXU=0 Radius=1.5 StartAngle=1.5708 EndAngle=4.71239
    g1: ArcOfCircle CenterX=-49.19 CenterY=62 CenterZ=0 NormalX=0 NormalY=0 NormalZ=1 AngleXU=0 Radius=1.5 StartAngle=1.5708 EndAngle=4.71239
    g2: ArcOfCircle CenterX=-49.19 CenterY=56.25 CenterZ=0 NormalX=0 NormalY=0 NormalZ=1 AngleXU=0 Radius=1.5 StartAngle=1.5708 EndAngle=4.71239
    g3: ArcOfCircle CenterX=-49.19 CenterY=50.5 CenterZ=0 NormalX=0 NormalY=0 NormalZ=1 AngleXU=0 Radius=1.5 StartAngle=1.5708 EndAngle=4.71239
    g4: ArcOfCircle CenterX=-49.19 CenterY=44.75 CenterZ=0 NormalX=0 NormalY=0 NormalZ=1 AngleXU=0 Radius=1.5 StartAngle=1.5708 EndAngle=4.71239
    g5: ArcOfCircle CenterX=-49.19 CenterY=39 CenterZ=0 NormalX=0 NormalY=0 NormalZ=1 AngleXU=0 Radius=1.5 StartAngle=1.5708 EndAngle=4.71239
    g6: ArcOfCircle CenterX=-49.19 CenterY=33 CenterZ=0 NormalX=0 NormalY=0 NormalZ=1 AngleXU=0 Radius=1.5 StartAngle=1.5708 EndAngle=4.71239
    g7: ArcOfCircle CenterX=-49.19 CenterY=27.25 CenterZ=0 NormalX=0 NormalY=0 NormalZ=1 AngleXU=0 Radius=1.5 StartAngle=1.5708 EndAngle=4.71239
    g8: ArcOfCircle CenterX=-49.19 CenterY=21.5 CenterZ=0 NormalX=0 NormalY=0 NormalZ=1 AngleXU=0 Radius=1.5 StartAngle=1.5708 EndAngle=4.71239
    g9: ArcOfCircle CenterX=-49.19 CenterY=15.75 CenterZ=0 NormalX=0 NormalY=0 NormalZ=1 AngleXU=0 Radius=1.5 StartAngle=1.5708 EndAngle=4.71239
    g10: ArcOfCircle CenterX=-49.19 CenterY=10 CenterZ=0 NormalX=0 NormalY=0 NormalZ=1 AngleXU=0 Radius=1.5 StartAngle=1.5708 EndAngle=4.71239
    g11: ArcOfCircle CenterX=-49.19 CenterY=4.25 CenterZ=0 NormalX=0 NormalY=0 NormalZ=1 AngleXU=0 Radius=1.5 StartAngle=1.5708 EndAngle=4.71239
    g12: LineSegment StartX=-49.19 StartY=69.25 StartZ=0 EndX=-49.19 EndY=66.25 EndZ=0
    g13: LineSegment StartX=-49.19 StartY=63.5 StartZ=0 EndX=-49.19 EndY=60.5 EndZ=0
    g14: LineSegment StartX=-49.19 StartY=57.75 StartZ=0 EndX=-49.19 EndY=54.75 EndZ=0
    g15: LineSegment StartX=-49.19 StartY=52 StartZ=0 EndX=-49.19 EndY=49 EndZ=0
    g16: LineSegment StartX=-49.19 StartY=46.25 StartZ=0 EndX=-49.19 EndY=43.25 EndZ=0
    g17: LineSegment StartX=-49.19 StartY=40.5 StartZ=0 EndX=-49.19 EndY=37.5 EndZ=0
    g18: LineSegment StartX=-49.19 StartY=34.5 StartZ=0 EndX=-49.19 EndY=31.5 EndZ=0
    g19: LineSegment StartX=-49.19 StartY=28.75 StartZ=0 EndX=-49.19 EndY=25.75 EndZ=0
    g20: LineSegment StartX=-49.19 StartY=23 StartZ=0 EndX=-49.19 EndY=20 EndZ=0
    g21: LineSegment StartX=-49.19 StartY=17.25 StartZ=0 EndX=-49.19 EndY=14.25 EndZ=0
    g22: LineSegment StartX=-49.19 StartY=11.5 StartZ=0 EndX=-49.19 EndY=8.5 EndZ=0
    g23: LineSegment StartX=-49.19 StartY=5.75 StartZ=0 EndX=-49.19 EndY=2.75 EndZ=0
  constraints (48):
    c: Block(g0)
    c: Block(g1)
    c: Block(g2)
    c: Block(g3)
    c: Block(g4)
    c: Block(g5)
    c: Block(g6)
    c: Block(g7)
    c: Block(g8)
    c: Block(g9)
    c: Block(g10)
    c: Block(g11)
    c: Coincident(g12,g0)
    c: Coincident(g12,g0)
    c: Vertical(g12)
    c: Vertical(g13)
    c: Coincident(g13,g1)
    c: Vertical(g14)
    c: Coincident(g14,g2)
    c: Vertical(g15)
    c: Coincident(g15,g3)
    c: Vertical(g16)
    c: Coincident(g16,g4)
    c: Vertical(g17)
    c: Coincident(g17,g5)
    c: Vertical(g18)
    c: Coincident(g18,g6)
    c: Vertical(g19)
    c: Coincident(g19,g7)
    c: Vertical(g20)
    c: Coincident(g20,g8)
    c: Vertical(g21)
    c: Coincident(g21,g9)
    c: Vertical(g22)
    c: Coincident(g22,g10)
    c: Vertical(g23)
    c: Coincident(g23,g11)
    c: Block(g23)
    c: Block(g22)
    c: Block(g21)
    c: Block(g20)
    c: Block(g13)
    c: Block(g14)
    c: Block(g15)
    c: Block(g16)
    c: Block(g17)
    c: Block(g18)
    c: Block(g19)
FEATURE [Part::Extrusion] Extrude022
  Base = -> Sketch030
  Dir = (1,-2e-16,2e-16)
  DirMode = 2
  FaceMakerClass = Part::FaceMakerBullseye
  LengthFwd = 19
  LengthRev = 0
  Placement = pos=(-19,0,0) rot=(0,0,1;0rad)
  Solid = true
  Symmetric = false
FEATURE [Part::Fillet] Fillet022
  Base = -> Extrude022
  Edges = 24 edges r=1.49: [Edge6,Edge11,Edge18,Edge23,Edge30,Edge35,Edge42,Edge47,Edge54,Edge59,Edge66,Edge71,Edge78,Edge83,Edge90,Edge95,Edge102,Edge107,Edge114,Edge119,Edge126,Edge131,Edge138,Edge143]
FEATURE [Part::Cut] Cut020  label="top010"
  Base = -> Cut019
  Tool = -> Fillet022
FEATURE [Sketcher::SketchObject] Sketch032
  FullyConstrained = true
  Placement = pos=(117,19,0) rot=(0.57735,0.57735,0.57735;2.0944rad)
  sketch-geometry (48):
    g0: LineSegment StartX=-49.19 StartY=69.25 StartZ=0 EndX=-49.19 EndY=66.25 EndZ=0
    g1: LineSegment StartX=-49.19 StartY=63.5 StartZ=0 EndX=-49.19 EndY=60.5 EndZ=0
    g2: LineSegment StartX=-49.19 StartY=57.75 StartZ=0 EndX=-49.19 EndY=54.75 EndZ=0
    g3: LineSegment StartX=-49.19 StartY=52 StartZ=0 EndX=-49.19 EndY=49 EndZ=0
    g4: LineSegment StartX=-49.19 StartY=46.25 StartZ=0 EndX=-49.19 EndY=43.25 EndZ=0
    g5: LineSegment StartX=-49.19 StartY=40.5 StartZ=0 EndX=-49.19 EndY=37.5 EndZ=0
    g6: LineSegment StartX=-49.19 StartY=34.5 StartZ=0 EndX=-49.19 EndY=31.5 EndZ=0
    g7: LineSegment StartX=-49.19 StartY=28.75 StartZ=0 EndX=-49.19 EndY=25.75 EndZ=0
    g8: LineSegment StartX=-49.19 StartY=23 StartZ=0 EndX=-49.19 EndY=20 EndZ=0
    g9: LineSegment StartX=-49.19 StartY=17.25 StartZ=0 EndX=-49.19 EndY=14.25 EndZ=0
    g10: LineSegment StartX=-49.19 StartY=11.5 StartZ=0 EndX=-49.19 EndY=8.5 EndZ=0
    g11: LineSegment StartX=-49.19 StartY=5.75 StartZ=0 EndX=-49.19 EndY=2.75 EndZ=0
    g12: ArcOfCircle CenterX=-1.5 CenterY=67.75 CenterZ=0 NormalX=0 NormalY=0 NormalZ=1 AngleXU=0 Radius=1.5 StartAngle=4.71239 EndAngle=7.85398
    g13: ArcOfCircle CenterX=-1.5 CenterY=62 CenterZ=0 NormalX=0 NormalY=0 NormalZ=1 AngleXU=0 Radius=1.5 StartAngle=4.71239 EndAngle=7.85398
    g14: ArcOfCircle CenterX=-1.5 CenterY=56.25 CenterZ=0 NormalX=0 NormalY=0 NormalZ=1 AngleXU=0 Radius=1.5 StartAngle=4.71239 EndAngle=7.85398
    g15: ArcOfCircle CenterX=-11.49 CenterY=50.5 CenterZ=0 NormalX=0 NormalY=0 NormalZ=1 AngleXU=0 Radius=1.5 StartAngle=4.71239 EndAngle=7.85398
    g16: ArcOfCircle CenterX=-16.28 CenterY=44.75 CenterZ=0 NormalX=0 NormalY=0 NormalZ=1 AngleXU=0 Radius=1.5 StartAngle=4.71239 EndAngle=7.85398
    g17: ArcOfCircle CenterX=-18.2337 CenterY=39 CenterZ=0 NormalX=0 NormalY=0 NormalZ=1 AngleXU=0 Radius=1.5 StartAngle=4.71485 EndAngle=7.85398
    g18: ArcOfCircle CenterX=-16.2837 CenterY=27.25 CenterZ=0 NormalX=0 NormalY=0 NormalZ=1 AngleXU=0 Radius=1.5 StartAngle=4.71485 EndAngle=7.85398
    g19: ArcOfCircle CenterX=-18.2337 CenterY=33 CenterZ=0 NormalX=0 NormalY=0 NormalZ=1 AngleXU=0 Radius=1.5 StartAngle=4.71485 EndAngle=7.85398
    g20: ArcOfCircle CenterX=-11.49 CenterY=21.5 CenterZ=0 NormalX=0 NormalY=0 NormalZ=1 AngleXU=0 Radius=1.5 StartAngle=4.71239 EndAngle=7.85398
    g21: ArcOfCircle CenterX=-1.5 CenterY=4.25 CenterZ=0 NormalX=0 NormalY=0 NormalZ=1 AngleXU=0 Radius=1.5 StartAngle=4.71239 EndAngle=7.85398
    g22: ArcOfCircle CenterX=-1.5 CenterY=10 CenterZ=0 NormalX=0 NormalY=0 NormalZ=1 AngleXU=0 Radius=1.5 StartAngle=4.71239 EndAngle=7.85398
    g23: ArcOfCircle CenterX=-1.5 CenterY=15.75 CenterZ=0 NormalX=0 NormalY=0 NormalZ=1 AngleXU=0 Radius=1.5 StartAngle=4.71239 EndAngle=7.85398
    g24: LineSegment StartX=-49.19 StartY=69.25 StartZ=0 EndX=-1.5 EndY=69.25 EndZ=0
    g25: LineSegment StartX=-49.19 StartY=66.25 StartZ=0 EndX=-1.5 EndY=66.25 EndZ=0
    g26: LineSegment StartX=-49.19 StartY=63.5 StartZ=0 EndX=-1.5 EndY=63.5 EndZ=0
    g27: LineSegment StartX=-49.19 StartY=60.5 StartZ=0 EndX=-1.5 EndY=60.5 EndZ=0
    g28: LineSegment StartX=-49.19 StartY=57.75 StartZ=0 EndX=-1.5 EndY=57.75 EndZ=0
    g29: LineSegment StartX=-49.19 StartY=54.75 StartZ=0 EndX=-1.5 EndY=54.75 EndZ=0
    g30: LineSegment StartX=-49.19 StartY=52 StartZ=0 EndX=-11.49 EndY=52 EndZ=0
    g31: LineSegment StartX=-49.19 StartY=49 StartZ=0 EndX=-11.49 EndY=49 EndZ=0
    g32: LineSegment StartX=-49.19 StartY=46.25 StartZ=0 EndX=-16.28 EndY=46.25 EndZ=0
    g33: LineSegment StartX=-49.19 StartY=43.25 StartZ=0 EndX=-16.28 EndY=43.25 EndZ=0
    g34: LineSegment StartX=-49.19 StartY=40.5 StartZ=0 EndX=-18.2337 EndY=40.5 EndZ=0
    g35: LineSegment StartX=-49.19 StartY=37.5 StartZ=0 EndX=-18.23 EndY=37.5 EndZ=0
    g36: LineSegment StartX=-49.19 StartY=34.5 StartZ=0 EndX=-18.2337 EndY=34.5 EndZ=0
    g37: LineSegment StartX=-49.19 StartY=31.5 StartZ=0 EndX=-18.23 EndY=31.5 EndZ=0
    g38: LineSegment StartX=-49.19 StartY=28.75 StartZ=0 EndX=-16.2837 EndY=28.75 EndZ=0
    g39: LineSegment StartX=-49.19 StartY=25.75 StartZ=0 EndX=-16.28 EndY=25.75 EndZ=0
    g40: LineSegment StartX=-49.19 StartY=23 StartZ=0 EndX=-11.49 EndY=23 EndZ=0
    g41: LineSegment StartX=-49.19 StartY=20 StartZ=0 EndX=-11.49 EndY=20 EndZ=0
    g42: LineSegment StartX=-49.19 StartY=17.25 StartZ=0 EndX=-1.5 EndY=17.25 EndZ=0
    g43: LineSegment StartX=-49.19 StartY=14.25 StartZ=0 EndX=-1.5 EndY=14.25 EndZ=0
    g44: LineSegment StartX=-49.19 StartY=11.5 StartZ=0 EndX=-1.5 EndY=11.5 EndZ=0
    g45: LineSegment StartX=-49.19 StartY=8.5 StartZ=0 EndX=-1.5 EndY=8.5 EndZ=0
    g46: LineSegment StartX=-49.19 StartY=5.75 StartZ=0 EndX=-1.5 EndY=5.75 EndZ=0
    g47: LineSegment StartX=-49.19 StartY=2.75 StartZ=0 EndX=-1.5 EndY=2.75 EndZ=0
  constraints (120):
    c: Vertical(g0)
    c: Distance(g0) = 3
    c: Block(g0)
    c: Vertical(g1)
    c: Distance(g1) = 3
    c: Vertical(g2)
    c: Equal(g0,g2) = 3
    c: Block(g2)
    c: Vertical(g3)
    c: Equal(g1,g3) = 3
    c: Vertical(g4)
    c: Equal(g0,g4) = 3
    c: Block(g4)
    c: Vertical(g5)
    c: Equal(g1,g5) = 3
    c: Vertical(g6)
    c: Equal(g0,g6) = 3
    c: Block(g6)
    c: Vertical(g7)
    c: Equal(g1,g7) = 3
    c: Vertical(g8)
    c: Equal(g0,g8) = 3
    c: Block(g8)
    c: Vertical(g9)
    c: Equal(g1,g9) = 3
    c: Vertical(g10)
    c: Equal(g0,g10) = 3
    c: Block(g10)
    c: Vertical(g11)
    c: Equal(g1,g11) = 3
    c: Block(g12)
    c: Block(g13)
    c: Block(g14)
    c: Block(g15)
    c: Block(g16)
    c: Block(g17)
    c: Block(g18)
    c: Block(g19)
    c: Block(g20)
    c: Block(g21)
    c: Block(g22)
    c: Block(g23)
    c: Block(g11)
    c: Block(g9)
    c: Block(g7)
    c: Block(g5)
    c: Block(g3)
    c: Block(g1)
    c: Coincident(g24,g0)
    c: Coincident(g24,g12)
    c: Horizontal(g24)
    c: Coincident(g25,g0)
    c: Coincident(g25,g12)
    c: Horizontal(g25)
    c: Coincident(g26,g1)
    c: Coincident(g26,g13)
    c: Horizontal(g26)
    c: Coincident(g27,g1)
    c: Coincident(g27,g13)
    c: Horizontal(g27)
    c: Coincident(g28,g2)
    c: Coincident(g28,g14)
    c: Horizontal(g28)
    c: Coincident(g29,g2)
    c: Coincident(g29,g14)
    c: Horizontal(g29)
    c: Coincident(g30,g3)
    c: Coincident(g30,g15)
    c: Horizontal(g30)
    c: Coincident(g31,g3)
    c: Coincident(g31,g15)
    c: Horizontal(g31)
    c: Coincident(g32,g4)
    c: Coincident(g32,g16)
    c: Horizontal(g32)
    c: Coincident(g33,g4)
    c: Coincident(g33,g16)
    c: Horizontal(g33)
    c: Coincident(g34,g5)
    c: Coincident(g34,g17)
    c: Horizontal(g34)
    c: Coincident(g35,g5)
    c: Coincident(g35,g17)
    c: Horizontal(g35)
    c: Coincident(g36,g6)
    c: Coincident(g36,g19)
    c: Horizontal(g36)
    c: Coincident(g37,g6)
    c: Coincident(g37,g19)
    c: Horizontal(g37)
    c: Coincident(g38,g7)
    c: Coincident(g38,g18)
    c: Horizontal(g38)
    c: Coincident(g39,g7)
    c: Coincident(g39,g18)
    c: Horizontal(g39)
    c: Coincident(g40,g8)
    c: Coincident(g40,g20)
    c: Horizontal(g40)
    c: Coincident(g41,g8)
    c: Coincident(g41,g20)
    c: Horizontal(g41)
    c: Coincident(g42,g9)
    c: Coincident(g42,g23)
    c: Horizontal(g42)
    c: Coincident(g43,g9)
    c: Coincident(g43,g23)
    c: Horizontal(g43)
    c: Coincident(g44,g10)
    c: Coincident(g44,g22)
    c: Horizontal(g44)
    c: Coincident(g45,g10)
    c: Coincident(g45,g22)
    c: Horizontal(g45)
    c: Coincident(g46,g11)
    c: Coincident(g46,g21)
    c: Horizontal(g46)
    c: Coincident(g47,g11)
    c: Coincident(g47,g21)
    c: Horizontal(g47)
FEATURE [Part::Extrusion] Extrude023
  Base = -> Sketch032
  Dir = (1,-2e-16,2e-16)
  DirMode = 2
  FaceMakerClass = Part::FaceMakerBullseye
  LengthFwd = 19
  LengthRev = 0
  Placement = pos=(-19,0,0) rot=(0,0,1;0rad)
  Solid = true
  Symmetric = false
FEATURE [Part::Fillet] Fillet023
  Base = -> Extrude023
  Edges = <same value as first occurrence — deduplicated (x6 in doc)>
  Placement = pos=(0,0.05,0) rot=(0,0,1;0rad)
FEATURE [Part::Cut] Cut014  label="bottom003"
  Base = -> Cut007
  Tool = -> Fusion047
FEATURE [Part::Cut] Cut021  label="bottom004"
  Base = -> Cut014
  Tool = -> Fillet023
FEATURE [Sketcher::SketchObject] Sketch033
  FullyConstrained = true
  Placement = pos=(117,19,0) rot=(0.57735,0.57735,0.57735;2.0944rad)
  sketch-geometry (8):
    g0: LineSegment StartX=-49.19 StartY=69.25 StartZ=0 EndX=-49.19 EndY=66.25 EndZ=0
    g1: LineSegment StartX=-49.19 StartY=5.75 StartZ=0 EndX=-49.19 EndY=2.75 EndZ=0
    g2: ArcOfCircle CenterX=-1.5 CenterY=67.75 CenterZ=0 NormalX=0 NormalY=0 NormalZ=1 AngleXU=0 Radius=1.5 StartAngle=4.71239 EndAngle=7.85398
    g3: ArcOfCircle CenterX=-1.5 CenterY=4.25 CenterZ=0 NormalX=0 NormalY=0 NormalZ=1 AngleXU=0 Radius=1.5 StartAngle=4.71239 EndAngle=7.85398
    g4: LineSegment StartX=-49.19 StartY=69.25 StartZ=0 EndX=-1.5 EndY=69.25 EndZ=0
    g5: LineSegment StartX=-49.19 StartY=66.25 StartZ=0 EndX=-1.5 EndY=66.25 EndZ=0
    g6: LineSegment StartX=-49.19 StartY=5.75 StartZ=0 EndX=-1.5 EndY=5.75 EndZ=0
    g7: LineSegment StartX=-49.19 StartY=2.75 StartZ=0 EndX=-1.5 EndY=2.75 EndZ=0
  constraints (19):
    c: Vertical(g0)
    c: Distance(g0) = 3
    c: Block(g0)
    c: Vertical(g1)
    c: Block(g2)
    c: Block(g3)
    c: Block(g1)
    c: Coincident(g4,g0)
    c: Coincident(g4,g2)
    c: Horizontal(g4)
    c: Coincident(g5,g0)
    c: Coincident(g5,g2)
    c: Horizontal(g5)
    c: Coincident(g6,g1)
    c: Coincident(g6,g3)
    c: Horizontal(g6)
    c: Coincident(g7,g1)
    c: Coincident(g7,g3)
    c: Horizontal(g7)
FEATURE [Sketcher::SketchObject] Sketch034
  FullyConstrained = true
  Placement = pos=(117,19,0) rot=(0.57735,0.57735,0.57735;2.0944rad)
  sketch-geometry (8):
    g0: LineSegment StartX=-49.19 StartY=63.5 StartZ=0 EndX=-49.19 EndY=60.5 EndZ=0
    g1: LineSegment StartX=-49.19 StartY=11.5 StartZ=0 EndX=-49.19 EndY=8.5 EndZ=0
    g2: ArcOfCircle CenterX=-1.5 CenterY=62 CenterZ=0 NormalX=0 NormalY=0 NormalZ=1 AngleXU=0 Radius=1.5 StartAngle=4.71239 EndAngle=7.85398
    g3: ArcOfCircle CenterX=-1.5 CenterY=10 CenterZ=0 NormalX=0 NormalY=0 NormalZ=1 AngleXU=0 Radius=1.5 StartAngle=4.71239 EndAngle=7.85398
    g4: LineSegment StartX=-49.19 StartY=63.5 StartZ=0 EndX=-1.5 EndY=63.5 EndZ=0
    g5: LineSegment StartX=-49.19 StartY=60.5 StartZ=0 EndX=-1.5 EndY=60.5 EndZ=0
    g6: LineSegment StartX=-49.19 StartY=11.5 StartZ=0 EndX=-1.5 EndY=11.5 EndZ=0
    g7: LineSegment StartX=-49.19 StartY=8.5 StartZ=0 EndX=-1.5 EndY=8.5 EndZ=0
  constraints (19):
    c: Vertical(g0)
    c: Distance(g0) = 3
    c: Vertical(g1)
    c: Block(g1)
    c: Block(g2)
    c: Block(g3)
    c: Block(g0)
    c: Coincident(g4,g0)
    c: Coincident(g4,g2)
    c: Horizontal(g4)
    c: Coincident(g5,g0)
    c: Coincident(g5,g2)
    c: Horizontal(g5)
    c: Coincident(g6,g1)
    c: Coincident(g6,g3)
    c: Horizontal(g6)
    c: Coincident(g7,g1)
    c: Coincident(g7,g3)
    c: Horizontal(g7)
FEATURE [Part::Extrusion] Extrude024
  Base = -> Sketch033
  Dir = (1,0,0)
  DirMode = 2
  FaceMakerClass = Part::FaceMakerBullseye
  LengthFwd = 10
  LengthRev = 0
  Solid = true
  Symmetric = false
FEATURE [Part::Extrusion] Extrude025
  Base = -> Sketch034
  Dir = (1,0,0)
  DirMode = 2
  FaceMakerClass = Part::FaceMakerBullseye
  LengthFwd = 10
  LengthRev = 0
  Solid = true
  Symmetric = false
FEATURE [Part::Fillet] Fillet024  label="removeFromtMoreFrontCaseScrewRetainers"
  Base = -> Extrude024
  Edges = 4 edges r=1.49: [Edge6,Edge11,Edge18,Edge23]
  Placement = pos=(-11,0,0) rot=(0,0,1;0rad)
FEATURE [Part::Fillet] Fillet025  label="removeFromtMoreFrontCaseScrewRetainers001"
  Base = -> Extrude025
  Edges = 4 edges r=1.49: [Edge6,Edge11,Edge18,Edge23]
  Placement = pos=(-19,0,0) rot=(0,0,1;0rad)
FEATURE [Part::Cut] Cut022
  Base = -> Cut015
  Tool = -> Fillet025
FEATURE [Part::Cut] Cut023  label="screwRetainers"
  Base = -> Cut022
  Tool = -> Fillet024
FEATURE [Part::MultiFuse] Fusion056  label="bottom005"
  Shapes = -> [Fusion044,Cut021]
FEATURE [Part::MultiFuse] Fusion057  label="casePillars001"
  Shapes = -> [Cut016,Fusion052]
FEATURE [Part::MultiFuse] Fusion058  label="bottom006"
  Shapes = -> [Fusion056,Cut023]
FEATURE [Part::MultiFuse] Fusion059  label="bottom007"
  Shapes = -> [Fusion058,Fillet005]
FEATURE [Part::MultiFuse] Fusion060  label="bottom008"
  Shapes = -> [Fusion059,Fusion]
FEATURE [Part::MultiFuse] Fusion061  label="top011"
  Shapes = -> [Cut006,Cut020]
FEATURE [Part::MultiFuse] Fusion062  label="top012"
  Shapes = -> [Fusion057,Fusion061]
FEATURE [Sketcher::SketchObject] Sketch035  label="topSketch007"
  FullyConstrained = true
  sketch-geometry (6):
    g0: LineSegment StartX=19 StartY=38 StartZ=0 EndX=117 EndY=38 EndZ=0
    g1: ArcOfCircle CenterX=19 CenterY=19 CenterZ=0 NormalX=0 NormalY=0 NormalZ=1 AngleXU=0 Radius=19 StartAngle=1.5708 EndAngle=3.14159
    g2: LineSegment StartX=117 StartY=38 StartZ=0 EndX=117 EndY=19 EndZ=0
    g3: LineSegment StartX=98 StartY=1.0161e-12 StartZ=0 EndX=5.22862e-06 EndY=1.0161e-12 EndZ=0
    g4: LineSegment StartX=5.22862e-06 StartY=19 StartZ=0 EndX=5.22862e-06 EndY=1.0161e-12 EndZ=0
    g5: ArcOfCircle CenterX=98 CenterY=19 CenterZ=0 NormalX=0 NormalY=0 NormalZ=1 AngleXU=0 Radius=19 StartAngle=4.71239 EndAngle=6.28319
  constraints (16):
    c: Horizontal(g0)
    c: Distance(g0) = 98
    c: Coincident(g1,g0)
    c: Block(g1)
    c: Coincident(g2,g0)
    c: Vertical(g2)
    c: Distance(g2) = 19
    c: Horizontal(g3)
    c: Coincident(g4,g1)
    c: Vertical(g4)
    c: Coincident(g3,g4)
    c: Block(g3)
    c: Coincident(g5,g2)
    c: Coincident(g5,g3)
    c: Block(g0)
    c: Block(g5)
FEATURE [Part::Extrusion] Extrude026  label="sideA001"
  Base = -> Sketch035
  Dir = (0,0,1)
  DirMode = 2
  FaceMakerClass = Part::FaceMakerBullseye
  LengthFwd = 3
  LengthRev = 0
  Placement = pos=(0,0,-2.7) rot=(0,0,1;0rad)
  Solid = true
  Symmetric = false
FEATURE [Sketcher::SketchObject] Sketch036  label="topSketch008"
  FullyConstrained = true
  sketch-geometry (6):
    g0: LineSegment StartX=19 StartY=38 StartZ=0 EndX=117 EndY=38 EndZ=0
    g1: ArcOfCircle CenterX=19 CenterY=19 CenterZ=0 NormalX=0 NormalY=0 NormalZ=1 AngleXU=0 Radius=19 StartAngle=1.5708 EndAngle=3.14159
    g2: LineSegment StartX=117 StartY=38 StartZ=0 EndX=117 EndY=19 EndZ=0
    g3: LineSegment StartX=98 StartY=1.0161e-12 StartZ=0 EndX=5.22862e-06 EndY=1.0161e-12 EndZ=0
    g4: LineSegment StartX=5.22862e-06 StartY=19 StartZ=0 EndX=5.22862e-06 EndY=1.0161e-12 EndZ=0
    g5: ArcOfCircle CenterX=98 CenterY=19 CenterZ=0 NormalX=0 NormalY=0 NormalZ=1 AngleXU=0 Radius=19 StartAngle=4.71239 EndAngle=6.28319
  constraints (16):
    c: Horizontal(g0)
    c: Distance(g0) = 98
    c: Coincident(g1,g0)
    c: Block(g1)
    c: Coincident(g2,g0)
    c: Vertical(g2)
    c: Distance(g2) = 19
    c: Horizontal(g3)
    c: Coincident(g4,g1)
    c: Vertical(g4)
    c: Coincident(g3,g4)
    c: Block(g3)
    c: Coincident(g5,g2)
    c: Coincident(g5,g3)
    c: Block(g0)
    c: Block(g5)
FEATURE [Part::Extrusion] Extrude027  label="sideB001"
  Base = -> Sketch036
  Dir = (0,0,1)
  DirMode = 2
  FaceMakerClass = Part::FaceMakerBullseye
  LengthFwd = 3
  LengthRev = 0
  Placement = pos=(0,0,71.7) rot=(0,0,1;0rad)
  Solid = true
  Symmetric = false
FEATURE [Part::MultiFuse] Fusion064  label="removeFromBottom"
  Shapes = -> [Extrude026,Extrude027]
FEATURE [Part::Cut] Cut024  label="bottom009"
  Base = -> Fusion060
  Tool = -> Fusion064
FEATURE [Sketcher::SketchObject] Sketch037  label="topSketch009"
  FullyConstrained = true
  sketch-geometry (8):
    g0: ArcOfCircle CenterX=19 CenterY=19.1201 CenterZ=0 NormalX=0 NormalY=0 NormalZ=1 AngleXU=0 Radius=18.8799 StartAngle=1.5708 EndAngle=3.14793
    g1: LineSegment StartX=0.120501 StartY=19.0004 StartZ=0 EndX=0.120501 EndY=0.000382114 EndZ=0
    g2: LineSegment StartX=19 StartY=38 StartZ=0 EndX=124 EndY=38 EndZ=0
    g3: LineSegment StartX=0.120501 StartY=0.000382114 StartZ=0 EndX=105.121 EndY=0.000382114 EndZ=0
    g4: LineSegment StartX=124 StartY=38 StartZ=0 EndX=125.616 EndY=38 EndZ=0
    g5: LineSegment StartX=105.121 StartY=0.000382114 StartZ=0 EndX=106.736 EndY=0.000382114 EndZ=0
    g6: ArcOfCircle CenterX=106.616 CenterY=19 CenterZ=0 NormalX=0 NormalY=0 NormalZ=1 AngleXU=0 Radius=19 StartAngle=4.71873 EndAngle=6.28319
    g7: LineSegment StartX=125.616 StartY=38 StartZ=0 EndX=125.616 EndY=19 EndZ=0
  constraints (21):
    c: Block(g0)
    c: Coincident(g1,g0)
    c: Vertical(g1)
    c: Horizontal(g2)
    c: Distance(g2) = 105
    c: Coincident(g2,g0)
    c: Distance(g1) = 19
    c: Coincident(g3,g1)
    c: Horizontal(g3)
    c: Distance(g3) = 105
    c: Coincident(g4,g2)
    c: Horizontal(g4)
    c: Distance(g4) = 1.61553
    c: Horizontal(g5)
    c: Equal(g4,g5) = 1.61553
    c: Coincident(g5,g3)
    c: Block(g6)
    c: Coincident(g6,g5)
    c: Coincident(g7,g4)
    c: Coincident(g7,g6)
    c: Vertical(g7)
FEATURE [Part::Extrusion] Extrude028  label="sideB"
  Base = -> Sketch037
  Dir = (0,0,1)
  DirMode = 2
  FaceMakerClass = Part::FaceMakerBullseye
  LengthFwd = 3
  LengthRev = 0
  Placement = pos=(0,0,72) rot=(0,0,1;0rad)
  Solid = true
  Symmetric = false
FEATURE [Sketcher::SketchObject] Sketch038  label="topSketch010"
  FullyConstrained = true
  sketch-geometry (22):
    g0: LineSegment StartX=5.21097e-06 StartY=3 StartZ=0 EndX=5.21097e-06 EndY=19 EndZ=0
    g1: ArcOfCircle CenterX=19 CenterY=19 CenterZ=0 NormalX=0 NormalY=0 NormalZ=1 AngleXU=0 Radius=19 StartAngle=1.5708 EndAngle=3.14159
    g2: ArcOfCircle CenterX=19 CenterY=19 CenterZ=0 NormalX=0 NormalY=0 NormalZ=1 AngleXU=0 Radius=16 StartAngle=1.5708 EndAngle=3.14159
    g3: LineSegment StartX=114 StartY=35 StartZ=0 EndX=19 EndY=35 EndZ=0
    g4: LineSegment StartX=5.21097e-06 StartY=3 StartZ=0 EndX=5.21097e-06 EndY=0 EndZ=0
    g5: LineSegment StartX=3 StartY=0 StartZ=0 EndX=5.21097e-06 EndY=0 EndZ=0
    g6: LineSegment StartX=3 StartY=19 StartZ=0 EndX=3 EndY=0 EndZ=0
    g7: LineSegment StartX=19 StartY=38 StartZ=0 EndX=124 EndY=38 EndZ=0
    g8: Circle CenterX=119 CenterY=35 CenterZ=0 NormalX=0 NormalY=0 NormalZ=1 AngleXU=0 Radius=1
    g9: Circle CenterX=121 CenterY=35 CenterZ=0 NormalX=0 NormalY=0 NormalZ=1 AngleXU=0 Radius=1
    g10: Circle CenterX=121 CenterY=33 CenterZ=0 NormalX=0 NormalY=0 NormalZ=1 AngleXU=0 Radius=1
    g11: BSplineCurve PolesCount=3 KnotsCount=2 Degree=2 IsPeriodic=0
    g12: GeomPoint X=119 Y=35 Z=0
    g13: GeomPoint X=121 Y=33 Z=0
    g14: LineSegment StartX=119 StartY=35 StartZ=0 EndX=114 EndY=35 EndZ=0
    g15: ArcOfCircle CenterX=105 CenterY=19 CenterZ=0 NormalX=0 NormalY=0 NormalZ=1 AngleXU=0 Radius=16 StartAngle=5.60905 EndAngle=6.28319
    g16: LineSegment StartX=121 StartY=33 StartZ=0 EndX=121 EndY=19 EndZ=0
    g17: LineSegment StartX=117.5 StartY=9.01251 StartZ=0 EndX=121.163 EndY=9.0125 EndZ=0
    g18: ArcOfCircle CenterX=105 CenterY=19 CenterZ=0 NormalX=0 NormalY=0 NormalZ=1 AngleXU=0 Radius=20.6155 StartAngle=5.7297 EndAngle=6.28319
    g19: LineSegment StartX=121.163 StartY=9.0125 StartZ=0 EndX=122.538 EndY=8.16329 EndZ=0
    g20: LineSegment StartX=124 StartY=38 StartZ=0 EndX=125.616 EndY=38 EndZ=0
    g21: LineSegment StartX=125.616 StartY=19 StartZ=0 EndX=125.616 EndY=38 EndZ=0
  constraints (49):
    c: Vertical(g0)
    c: Block(g0)
    c: Coincident(g1,g0)
    c: Block(g1)
    c: Coincident(g2,g1)
    c: Block(g2)
    c: Coincident(g3,g2)
    c: Horizontal(g3)
    c: Tangent(g3,g2)
    c: Coincident(g4,g0)
    c: Distance(g4) = 3
    c: Vertical(g4)
    c: Coincident(g5,g4)
    c: Horizontal(g5)
    c: Coincident(g6,g2)
    c: Coincident(g6,g5)
    c: Vertical(g6)
    c: Horizontal(g7)
    c: Distance(g7) = 105
    c: Coincident(g7,g1)
    c: Block(g3)
    c: Weight(g8) = 1
    c: Equal(g8,g9)
    c: Equal(g8,g10)
    c: InternalAlignment(g8,g11)
    c: InternalAlignment(g9,g11)
    c: InternalAlignment(g10,g11)
    c: InternalAlignment(g12,g11)
    c: InternalAlignment(g13,g11)
    c: Block(g11)
    c: Coincident(g14,g11)
    c: Coincident(g14,g3)
    c: Horizontal(g14)
    c: Block(g15)
    c: Coincident(g16,g11)
    c: Coincident(g16,g15)
    c: Vertical(g16)
    c: Distance(g16) = 14
    c: Coincident(g17,g15)
    c: Block(g18)
    c: Coincident(g19,g18)
    c: Coincident(g20,g7)
    c: Horizontal(g20)
    c: Vertical(g21)
    c: Coincident(g20,g21)
    c: Block(g20)
    c: Block(g21)
    c: Block(g19)
    c: Block(g17)
FEATURE [Part::Extrusion] Extrude029
  Base = -> Sketch038
  Dir = (0,0,1)
  DirMode = 2
  FaceMakerClass = Part::FaceMakerBullseye
  LengthFwd = 72
  LengthRev = 0
  Solid = true
  Symmetric = false
FEATURE [Part::Feature] Face085
  shape: bbox 4.8 x 25.5 x 2e-07 mm, 1 faces, 0 solids (baked)
FEATURE [Part::Revolution] Revolve089  label="moreFrontCaseScrewPost003"
  Angle = 360
  Axis = (0,1,0)
  Base = (0,0,0)
  FaceMakerClass = Part::FaceMakerBullseye
  Placement = pos=(109.5,4.5,3.5) rot=(0,0,1;0rad)
  Solid = false
  Source = -> Face085
  Symmetric = false
FEATURE [Part::Feature] Face086
  shape: bbox 4.8 x 25.5 x 2e-07 mm, 1 faces, 0 solids (baked)
FEATURE [Part::Revolution] Revolve090  label="moreFrontCaseScrewPost004"
  Angle = 360
  Axis = (0,1,0)
  Base = (0,0,0)
  FaceMakerClass = Part::FaceMakerBullseye
  Placement = pos=(109.5,4.5,68.5) rot=(0,0,1;0rad)
  Solid = false
  Source = -> Face086
  Symmetric = false
FEATURE [Part::Fillet] Fillet026  label="top013"
  Base = -> Extrude029
  Edges = 1 edges r=2: [Edge35]
FEATURE [Sketcher::SketchObject] Sketch039
  FullyConstrained = true
  sketch-geometry (7):
    g0: LineSegment StartX=0 StartY=0 StartZ=0 EndX=0 EndY=6 EndZ=0
    g1: Circle CenterX=0 CenterY=0 CenterZ=0 NormalX=0 NormalY=0 NormalZ=1 AngleXU=0 Radius=1
    g2: Circle CenterX=8 CenterY=6 CenterZ=0 NormalX=0 NormalY=0 NormalZ=1 AngleXU=0 Radius=1
    g3: BSplineCurve PolesCount=3 KnotsCount=2 Degree=2 IsPeriodic=0
    g4: GeomPoint X=0 Y=0 Z=0
    g5: GeomPoint X=8 Y=6 Z=0
    g6: LineSegment StartX=0 StartY=6 StartZ=0 EndX=8 EndY=6 EndZ=0
  constraints (14):
    c: Coincident(g0,g-1)
    c: Distance(g0) = 6
    c: Vertical(g0)
    c: Coincident(g3,g0)
    c: Weight(g1) = 1
    c: Equal(g1,g2)
    c: InternalAlignment(g1,g3)
    c: InternalAlignment(g2,g3)
    c: InternalAlignment(g4,g3)
    c: InternalAlignment(g5,g3)
    c: Block(g3)
    c: Coincident(g6,g0)
    c: Coincident(g6,g3)
    c: Horizontal(g6)
FEATURE [Sketcher::SketchObject] Sketch040
  FullyConstrained = true
  sketch-geometry (7):
    g0: LineSegment StartX=0 StartY=0 StartZ=0 EndX=0 EndY=6 EndZ=0
    g1: Circle CenterX=0 CenterY=0 CenterZ=0 NormalX=0 NormalY=0 NormalZ=1 AngleXU=0 Radius=1
    g2: Circle CenterX=8 CenterY=6 CenterZ=0 NormalX=0 NormalY=0 NormalZ=1 AngleXU=0 Radius=1
    g3: BSplineCurve PolesCount=3 KnotsCount=2 Degree=2 IsPeriodic=0
    g4: GeomPoint X=0 Y=0 Z=0
    g5: GeomPoint X=8 Y=6 Z=0
    g6: LineSegment StartX=0 StartY=6 StartZ=0 EndX=8 EndY=6 EndZ=0
  constraints (14):
    c: Coincident(g0,g-1)
    c: Distance(g0) = 6
    c: Vertical(g0)
    c: Coincident(g3,g0)
    c: Weight(g1) = 1
    c: Equal(g1,g2)
    c: InternalAlignment(g1,g3)
    c: InternalAlignment(g2,g3)
    c: InternalAlignment(g4,g3)
    c: InternalAlignment(g5,g3)
    c: Block(g3)
    c: Coincident(g6,g0)
    c: Coincident(g6,g3)
    c: Horizontal(g6)
FEATURE [Sketcher::SketchObject] Sketch041
  FullyConstrained = true
  sketch-geometry (7):
    g0: LineSegment StartX=0 StartY=0 StartZ=0 EndX=0 EndY=6 EndZ=0
    g1: Circle CenterX=0 CenterY=0 CenterZ=0 NormalX=0 NormalY=0 NormalZ=1 AngleXU=0 Radius=1
    g2: Circle CenterX=8 CenterY=6 CenterZ=0 NormalX=0 NormalY=0 NormalZ=1 AngleXU=0 Radius=1
    g3: BSplineCurve PolesCount=3 KnotsCount=2 Degree=2 IsPeriodic=0
    g4: GeomPoint X=0 Y=0 Z=0
    g5: GeomPoint X=8 Y=6 Z=0
    g6: LineSegment StartX=0 StartY=6 StartZ=0 EndX=8 EndY=6 EndZ=0
  constraints (14):
    c: Coincident(g0,g-1)
    c: Distance(g0) = 6
    c: Vertical(g0)
    c: Coincident(g3,g0)
    c: Weight(g1) = 1
    c: Equal(g1,g2)
    c: InternalAlignment(g1,g3)
    c: InternalAlignment(g2,g3)
    c: InternalAlignment(g4,g3)
    c: InternalAlignment(g5,g3)
    c: Block(g3)
    c: Coincident(g6,g0)
    c: Coincident(g6,g3)
    c: Horizontal(g6)
FEATURE [Sketcher::SketchObject] Sketch042
  FullyConstrained = true
  sketch-geometry (7):
    g0: LineSegment StartX=0 StartY=0 StartZ=0 EndX=0 EndY=6 EndZ=0
    g1: Circle CenterX=0 CenterY=0 CenterZ=0 NormalX=0 NormalY=0 NormalZ=1 AngleXU=0 Radius=1
    g2: Circle CenterX=8 CenterY=6 CenterZ=0 NormalX=0 NormalY=0 NormalZ=1 AngleXU=0 Radius=1
    g3: BSplineCurve PolesCount=3 KnotsCount=2 Degree=2 IsPeriodic=0
    g4: GeomPoint X=0 Y=0 Z=0
    g5: GeomPoint X=8 Y=6 Z=0
    g6: LineSegment StartX=0 StartY=6 StartZ=0 EndX=8 EndY=6 EndZ=0
  constraints (14):
    c: Coincident(g0,g-1)
    c: Distance(g0) = 6
    c: Vertical(g0)
    c: Coincident(g3,g0)
    c: Weight(g1) = 1
    c: Equal(g1,g2)
    c: InternalAlignment(g1,g3)
    c: InternalAlignment(g2,g3)
    c: InternalAlignment(g4,g3)
    c: InternalAlignment(g5,g3)
    c: Block(g3)
    c: Coincident(g6,g0)
    c: Coincident(g6,g3)
    c: Horizontal(g6)
FEATURE [Part::Extrusion] Extrude030  label="caseScrewPillarBracket008"
  Base = -> Sketch039
  Dir = (0,0,1)
  DirMode = 2
  FaceMakerClass = Part::FaceMakerBullseye
  LengthFwd = 2.4
  LengthRev = 0
  Placement = pos=(15.76,29,8.8) rot=(0,1,0;0rad)
  Solid = true
  Symmetric = false
FEATURE [Part::Extrusion] Extrude031  label="caseScrewPillarBracket009"
  Base = -> Sketch040
  Dir = (0,0,1)
  DirMode = 2
  FaceMakerClass = Part::FaceMakerBullseye
  LengthFwd = 2.4
  LengthRev = 0
  Placement = pos=(15.76,29,60.8) rot=(0,0,1;0rad)
  Solid = true
  Symmetric = false
FEATURE [Part::Extrusion] Extrude032  label="caseScrewPillarBracket010"
  Base = -> Sketch041
  Dir = (0,0,1)
  DirMode = 2
  FaceMakerClass = Part::FaceMakerBullseye
  LengthFwd = 2.4
  LengthRev = 0
  Placement = pos=(13.7,29,13.26) rot=(0,-1,0;1.5708rad)
  Solid = true
  Symmetric = false
FEATURE [Part::Extrusion] Extrude033  label="caseScrewPillarBracket011"
  Base = -> Sketch042
  Dir = (0,0,1)
  DirMode = 2
  FaceMakerClass = Part::FaceMakerBullseye
  LengthFwd = 2.4
  LengthRev = 0
  Placement = pos=(11.3,29,58.74) rot=(0,1,0;1.5708rad)
  Solid = true
  Symmetric = false
FEATURE [Sketcher::SketchObject] Sketch043
  FullyConstrained = true
  sketch-geometry (7):
    g0: LineSegment StartX=0 StartY=0 StartZ=0 EndX=0 EndY=6 EndZ=0
    g1: Circle CenterX=0 CenterY=0 CenterZ=0 NormalX=0 NormalY=0 NormalZ=1 AngleXU=0 Radius=1
    g2: Circle CenterX=8 CenterY=6 CenterZ=0 NormalX=0 NormalY=0 NormalZ=1 AngleXU=0 Radius=1
    g3: BSplineCurve PolesCount=3 KnotsCount=2 Degree=2 IsPeriodic=0
    g4: GeomPoint X=0 Y=0 Z=0
    g5: GeomPoint X=8 Y=6 Z=0
    g6: LineSegment StartX=0 StartY=6 StartZ=0 EndX=8 EndY=6 EndZ=0
  constraints (14):
    c: Coincident(g0,g-1)
    c: Distance(g0) = 6
    c: Vertical(g0)
    c: Coincident(g3,g0)
    c: Weight(g1) = 1
    c: Equal(g1,g2)
    c: InternalAlignment(g1,g3)
    c: InternalAlignment(g2,g3)
    c: InternalAlignment(g4,g3)
    c: InternalAlignment(g5,g3)
    c: Block(g3)
    c: Coincident(g6,g0)
    c: Coincident(g6,g3)
    c: Horizontal(g6)
FEATURE [Part::Extrusion] Extrude034  label="caseScrewPillarBracket012"
  Base = -> Sketch043
  Dir = (0,0,1)
  DirMode = 2
  FaceMakerClass = Part::FaceMakerBullseye
  LengthFwd = 2.4
  LengthRev = 0
  Placement = pos=(88.3,29,65.23) rot=(0,1,0;1.5708rad)
  Solid = true
  Symmetric = false
FEATURE [Sketcher::SketchObject] Sketch044
  FullyConstrained = true
  sketch-geometry (7):
    g0: LineSegment StartX=0 StartY=0 StartZ=0 EndX=0 EndY=6 EndZ=0
    g1: Circle CenterX=0 CenterY=0 CenterZ=0 NormalX=0 NormalY=0 NormalZ=1 AngleXU=0 Radius=1
    g2: Circle CenterX=8 CenterY=6 CenterZ=0 NormalX=0 NormalY=0 NormalZ=1 AngleXU=0 Radius=1
    g3: BSplineCurve PolesCount=3 KnotsCount=2 Degree=2 IsPeriodic=0
    g4: GeomPoint X=0 Y=0 Z=0
    g5: GeomPoint X=8 Y=6 Z=0
    g6: LineSegment StartX=0 StartY=6 StartZ=0 EndX=8 EndY=6 EndZ=0
  constraints (14):
    c: Coincident(g0,g-1)
    c: Distance(g0) = 6
    c: Vertical(g0)
    c: Coincident(g3,g0)
    c: Weight(g1) = 1
    c: Equal(g1,g2)
    c: InternalAlignment(g1,g3)
    c: InternalAlignment(g2,g3)
    c: InternalAlignment(g4,g3)
    c: InternalAlignment(g5,g3)
    c: Block(g3)
    c: Coincident(g6,g0)
    c: Coincident(g6,g3)
    c: Horizontal(g6)
FEATURE [Part::Extrusion] Extrude035  label="caseScrewPillarBracket013"
  Base = -> Sketch044
  Dir = (0,0,1)
  DirMode = 2
  FaceMakerClass = Part::FaceMakerBullseye
  LengthFwd = 2.4
  LengthRev = 0
  Placement = pos=(90.7,29,6.77) rot=(0,-1,0;1.5708rad)
  Solid = true
  Symmetric = false
FEATURE [Sketcher::SketchObject] Sketch045
  FullyConstrained = true
  sketch-geometry (7):
    g0: LineSegment StartX=0 StartY=0 StartZ=0 EndX=0 EndY=6 EndZ=0
    g1: Circle CenterX=0 CenterY=0 CenterZ=0 NormalX=0 NormalY=0 NormalZ=1 AngleXU=0 Radius=1
    g2: Circle CenterX=8 CenterY=6 CenterZ=0 NormalX=0 NormalY=0 NormalZ=1 AngleXU=0 Radius=1
    g3: BSplineCurve PolesCount=3 KnotsCount=2 Degree=2 IsPeriodic=0
    g4: GeomPoint X=0 Y=0 Z=0
    g5: GeomPoint X=8 Y=6 Z=0
    g6: LineSegment StartX=0 StartY=6 StartZ=0 EndX=8 EndY=6 EndZ=0
  constraints (14):
    c: Coincident(g0,g-1)
    c: Distance(g0) = 6
    c: Vertical(g0)
    c: Coincident(g3,g0)
    c: Weight(g1) = 1
    c: Equal(g1,g2)
    c: InternalAlignment(g1,g3)
    c: InternalAlignment(g2,g3)
    c: InternalAlignment(g4,g3)
    c: InternalAlignment(g5,g3)
    c: Block(g3)
    c: Coincident(g6,g0)
    c: Coincident(g6,g3)
    c: Horizontal(g6)
FEATURE [Sketcher::SketchObject] Sketch046
  FullyConstrained = true
  sketch-geometry (7):
    g0: LineSegment StartX=0 StartY=0 StartZ=0 EndX=0 EndY=6 EndZ=0
    g1: Circle CenterX=0 CenterY=0 CenterZ=0 NormalX=0 NormalY=0 NormalZ=1 AngleXU=0 Radius=1
    g2: Circle CenterX=8 CenterY=6 CenterZ=0 NormalX=0 NormalY=0 NormalZ=1 AngleXU=0 Radius=1
    g3: BSplineCurve PolesCount=3 KnotsCount=2 Degree=2 IsPeriodic=0
    g4: GeomPoint X=0 Y=0 Z=0
    g5: GeomPoint X=8 Y=6 Z=0
    g6: LineSegment StartX=0 StartY=6 StartZ=0 EndX=8 EndY=6 EndZ=0
  constraints (14):
    c: Coincident(g0,g-1)
    c: Distance(g0) = 6
    c: Vertical(g0)
    c: Coincident(g3,g0)
    c: Weight(g1) = 1
    c: Equal(g1,g2)
    c: InternalAlignment(g1,g3)
    c: InternalAlignment(g2,g3)
    c: InternalAlignment(g4,g3)
    c: InternalAlignment(g5,g3)
    c: Block(g3)
    c: Coincident(g6,g0)
    c: Coincident(g6,g3)
    c: Horizontal(g6)
FEATURE [Part::Extrusion] Extrude036  label="caseScrewPillarBracket014"
  Base = -> Sketch045
  Dir = (0,0,1)
  DirMode = 2
  FaceMakerClass = Part::FaceMakerBullseye
  LengthFwd = 2.4
  LengthRev = 0
  Placement = pos=(110.7,29,6.77) rot=(0,-1,0;1.5708rad)
  Solid = true
  Symmetric = false
FEATURE [Part::Extrusion] Extrude037  label="caseScrewPillarBracket015"
  Base = -> Sketch046
  Dir = (0,0,1)
  DirMode = 2
  FaceMakerClass = Part::FaceMakerBullseye
  LengthFwd = 2.4
  LengthRev = 0
  Placement = pos=(108.3,29,65.23) rot=(0,1,0;1.5708rad)
  Solid = true
  Symmetric = false
FEATURE [Part::Box] Box013  label="frontCaseScrewPillarBracket002"
  AttacherType = Attacher::AttachEngine3D
  Height = 2.4
  Length = 22
  Placement = pos=(87,28,2.3) rot=(0,0,1;0rad)
  Width = 7
FEATURE [Part::Box] Box014  label="frontCaseScrewPillarBracket003"
  AttacherType = Attacher::AttachEngine3D
  Height = 2.4
  Length = 22
  Placement = pos=(87,28,67.3) rot=(0,0,1;0rad)
  Width = 7
FEATURE [Part::Feature] Face087
  shape: bbox 4.8 x 30.2 x 2e-07 mm, 1 faces, 0 solids (baked)
FEATURE [Part::Revolution] Revolve091  label="frontCaseScrewPost004"
  Angle = 360
  Axis = (0,1,0)
  Base = (0,0,0)
  FaceMakerClass = Part::FaceMakerBullseye
  Placement = pos=(89.5,4.5,3.5) rot=(0,0,1;0rad)
  Solid = false
  Source = -> Face087
  Symmetric = false
FEATURE [Part::Feature] Face088
  shape: bbox 4.8 x 30.2 x 2e-07 mm, 1 faces, 0 solids (baked)
FEATURE [Part::Revolution] Revolve092  label="frontCaseScrewPost005"
  Angle = 360
  Axis = (0,1,0)
  Base = (0,0,0)
  FaceMakerClass = Part::FaceMakerBullseye
  Placement = pos=(89.5,4.5,68.5) rot=(0,0,1;0rad)
  Solid = false
  Source = -> Face088
  Symmetric = false
FEATURE [Part::Feature] Face089
  shape: bbox 3.5 x 30.2 x 2e-07 mm, 1 faces, 0 solids (baked)
FEATURE [Part::Revolution] Revolve093  label="backCaseScrewPost002"
  Angle = 360
  Axis = (0,1,0)
  Base = (0,0,0)
  FaceMakerClass = Part::FaceMakerBullseye
  Placement = pos=(12.5,4.5,10) rot=(0,0,1;0rad)
  Solid = false
  Source = -> Face089
  Symmetric = false
FEATURE [Part::Feature] Face090
  shape: bbox 3.5 x 30.2 x 2e-07 mm, 1 faces, 0 solids (baked)
FEATURE [Part::Revolution] Revolve094  label="backCaseScrewPost003"
  Angle = 360
  Axis = (0,1,0)
  Base = (0,0,0)
  FaceMakerClass = Part::FaceMakerBullseye
  Placement = pos=(12.5,4.5,62) rot=(0,0,1;0rad)
  Solid = false
  Source = -> Face090
  Symmetric = false
FEATURE [Part::Box] Box015  label="Cube011"
  AttacherType = Attacher::AttachEngine3D
  Height = 28.8
  Length = 3
  Placement = pos=(107.3,28,21.6) rot=(0,0,1;0rad)
  Width = 7
FEATURE [Part::Box] Box016  label="Cube012"
  AttacherType = Attacher::AttachEngine3D
  Height = 3
  Length = 7.4
  Placement = pos=(107.3,28,18.6) rot=(0,0,1;0rad)
  Width = 7
FEATURE [Part::Box] Box017  label="Cube013"
  AttacherType = Attacher::AttachEngine3D
  Height = 3
  Length = 7.4
  Placement = pos=(107.3,28,50.4) rot=(0,0,1;0rad)
  Width = 7
FEATURE [Part::Cylinder] Cylinder024
  Angle = 360
  AttacherType = Attacher::AttachEngine3D
  Height = 20
  Placement = pos=(0,0,36.15) rot=(0,0,1;0rad)
  Radius = 14.3
FEATURE [Part::Cylinder] Cylinder025
  Angle = 360
  AttacherType = Attacher::AttachEngine3D
  Height = 10
  Placement = pos=(0,0,36.15) rot=(0,0,1;0rad)
  Radius = 4
FEATURE [Part::MultiFuse] Fusion066  label="removeToCreteHoleForPlugHousing009"
  Placement = pos=(70,19,36) rot=(0,1,0;1.5708rad)
  Shapes = -> [Cylinder024,Cylinder025]
FEATURE [Part::MultiFuse] Fusion065  label="plugHousingBracketHolder002"
  Shapes = -> [Box017,Box015,Box016]
FEATURE [Part::Cut] Cut025  label="plugHousingBracketHolder003"
  Base = -> Fusion065
  Placement = pos=(7,0,0) rot=(0,0,1;0rad)
  Tool = -> Fusion066
FEATURE [Sketcher::SketchObject] Sketch047
  FullyConstrained = false
  Placement = pos=(0,0,0) rot=(1,0,0;1.5708rad)
  sketch-geometry (24):
    g0: ArcOfCircle CenterX=-4 CenterY=-10.5 CenterZ=0 NormalX=0 NormalY=0 NormalZ=1 AngleXU=0 Radius=1.5 StartAngle=6e-16 EndAngle=3.14159
    g1: ArcOfCircle CenterX=-34.2 CenterY=-10.5 CenterZ=0 NormalX=0 NormalY=0 NormalZ=1 AngleXU=0 Radius=1.5 StartAngle=0 EndAngle=3.14159
    g2: ArcOfCircle CenterX=-34.2 CenterY=-27.7 CenterZ=0 NormalX=0 NormalY=0 NormalZ=1 AngleXU=0 Radius=1.5 StartAngle=3.14159 EndAngle=6.28319
    g3: ArcOfCircle CenterX=-4 CenterY=-27.7 CenterZ=0 NormalX=0 NormalY=0 NormalZ=1 AngleXU=0 Radius=1.5 StartAngle=3.1416 EndAngle=6.28319
    g4: ArcOfCircle CenterX=-10 CenterY=-4.3 CenterZ=0 NormalX=0 NormalY=0 NormalZ=1 AngleXU=0 Radius=1.5 StartAngle=2e-16 EndAngle=3.14159
    g5: ArcOfCircle CenterX=-16.1 CenterY=-1.8 CenterZ=0 NormalX=0 NormalY=0 NormalZ=1 AngleXU=0 Radius=1.5 StartAngle=5e-16 EndAngle=3.14159
    g6: ArcOfCircle CenterX=-22.1 CenterY=-1.8 CenterZ=0 NormalX=0 NormalY=0 NormalZ=1 AngleXU=0 Radius=1.5 StartAngle=5e-16 EndAngle=3.14159
    g7: ArcOfCircle CenterX=-28.2 CenterY=-4.3 CenterZ=0 NormalX=0 NormalY=0 NormalZ=1 AngleXU=0 Radius=1.5 StartAngle=2e-16 EndAngle=3.14159
    g8: ArcOfCircle CenterX=-10 CenterY=-33.9 CenterZ=0 NormalX=0 NormalY=0 NormalZ=1 AngleXU=0 Radius=1.5 StartAngle=3.14159 EndAngle=6.28319
    g9: ArcOfCircle CenterX=-16.1 CenterY=-36.4 CenterZ=0 NormalX=0 NormalY=0 NormalZ=1 AngleXU=0 Radius=1.5 StartAngle=3.14159 EndAngle=6.28319
    g10: ArcOfCircle CenterX=-22.1 CenterY=-36.4 CenterZ=0 NormalX=0 NormalY=0 NormalZ=1 AngleXU=0 Radius=1.5 StartAngle=3.14159 EndAngle=6.28319
    g11: ArcOfCircle CenterX=-28.2 CenterY=-33.9 CenterZ=0 NormalX=0 NormalY=0 NormalZ=1 AngleXU=0 Radius=1.5 StartAngle=3.14159 EndAngle=6.28319
    g12: LineSegment StartX=-35.7 StartY=-10.5 StartZ=0 EndX=-35.7 EndY=-27.7 EndZ=0
    g13: LineSegment StartX=-32.7 StartY=-10.5 StartZ=0 EndX=-32.7 EndY=-27.7 EndZ=0
    g14: LineSegment StartX=-29.7 StartY=-33.9 StartZ=0 EndX=-29.7 EndY=-4.3 EndZ=0
    g15: LineSegment StartX=-26.7 StartY=-33.9 StartZ=0 EndX=-26.7 EndY=-4.3 EndZ=0
    g16: LineSegment StartX=-2.5 StartY=-10.5 StartZ=0 EndX=-2.5 EndY=-27.7 EndZ=0
    g17: LineSegment StartX=-8.5 StartY=-4.3 StartZ=0 EndX=-8.5 EndY=-33.9 EndZ=0
    g18: LineSegment StartX=-5.5 StartY=-10.5 StartZ=0 EndX=-5.5 EndY=-27.7 EndZ=0
    g19: LineSegment StartX=-11.5 StartY=-4.3 StartZ=0 EndX=-11.5 EndY=-33.9 EndZ=0
    g20: LineSegment StartX=-14.6 StartY=-1.8 StartZ=0 EndX=-14.6 EndY=-36.4 EndZ=0
    g21: LineSegment StartX=-17.6 StartY=-1.8 StartZ=0 EndX=-17.6 EndY=-36.4 EndZ=0
    g22: LineSegment StartX=-20.6 StartY=-36.4 StartZ=0 EndX=-20.6 EndY=-1.8 EndZ=0
    g23: LineSegment StartX=-23.6 StartY=-1.8 StartZ=0 EndX=-23.6 EndY=-36.4 EndZ=0
  constraints (48):
    c: Block(g0)
    c: Block(g1)
    c: Block(g2)
    c: Block(g3)
    c: Block(g4)
    c: Block(g5)
    c: Block(g6)
    c: Block(g7)
    c: Block(g8)
    c: Block(g9)
    c: Block(g10)
    c: Block(g11)
    c: Coincident(g12,g1)
    c: Coincident(g12,g2)
    c: Vertical(g12)
    c: Coincident(g13,g1)
    c: Coincident(g13,g2)
    c: Vertical(g13)
    c: Coincident(g14,g11)
    c: Coincident(g14,g7)
    c: Vertical(g14)
    c: Coincident(g15,g11)
    c: Coincident(g15,g7)
    c: Vertical(g15)
    c: Coincident(g16,g0)
    c: Coincident(g16,g3)
    c: Vertical(g16)
    c: Coincident(g17,g4)
    c: Coincident(g17,g8)
    c: Vertical(g17)
    c: Coincident(g18,g0)
    c: Coincident(g18,g3)
    c: Vertical(g18)
    c: Coincident(g19,g4)
    c: Coincident(g19,g8)
    c: Vertical(g19)
    c: Coincident(g20,g5)
    c: Coincident(g20,g9)
    c: Vertical(g20)
    c: Coincident(g21,g5)
    c: Coincident(g21,g9)
    c: Vertical(g21)
    c: Coincident(g22,g10)
    c: Coincident(g22,g6)
    c: Vertical(g22)
    c: Coincident(g23,g6)
    c: Coincident(g23,g10)
    c: Vertical(g23)
FEATURE [Part::Extrusion] Extrude038  label="removeToCreateFanGrillHoles001"
  Base = -> Sketch047
  Dir = (0,-1,6e-16)
  DirMode = 2
  FaceMakerClass = Part::FaceMakerBullseye
  LengthFwd = 10
  LengthRev = 0
  Placement = pos=(65.4,44,54.82) rot=(0,0,1;0rad)
  Solid = true
  Symmetric = false
FEATURE [Part::Feature] Wire004
  shape: bbox 11 x 5.2 x 2e-07 mm, 0 faces, 0 solids (baked)
FEATURE [Part::Revolution] Revolve095
  Angle = 360
  Axis = (0,1,0)
  Base = (0,0,0)
  FaceMakerClass = Part::FaceMakerBullseye
  Placement = pos=(30.3,38,19.7) rot=(0,0,1;0rad)
  Solid = true
  Source = -> Wire004
  Symmetric = false
FEATURE [Part::Feature] Wire005
  shape: bbox 11 x 5.2 x 2e-07 mm, 0 faces, 0 solids (baked)
FEATURE [Part::Revolution] Revolve096
  Angle = 360
  Axis = (0,1,0)
  Base = (0,0,0)
  FaceMakerClass = Part::FaceMakerBullseye
  Placement = pos=(30.3,38,51.7) rot=(0,0,1;0rad)
  Solid = true
  Source = -> Wire005
  Symmetric = false
FEATURE [Part::Feature] Wire006
  shape: bbox 11 x 5.2 x 2e-07 mm, 0 faces, 0 solids (baked)
FEATURE [Part::Revolution] Revolve097
  Angle = 360
  Axis = (0,1,0)
  Base = (0,0,0)
  FaceMakerClass = Part::FaceMakerBullseye
  Placement = pos=(62.3,38,51.7) rot=(0,0,1;0rad)
  Solid = true
  Source = -> Wire006
  Symmetric = false
FEATURE [Part::Feature] Wire007
  shape: bbox 11 x 5.2 x 2e-07 mm, 0 faces, 0 solids (baked)
FEATURE [Part::Revolution] Revolve098
  Angle = 360
  Axis = (0,1,0)
  Base = (0,0,0)
  FaceMakerClass = Part::FaceMakerBullseye
  Placement = pos=(62.3,38,19.7) rot=(0,0,1;0rad)
  Solid = true
  Source = -> Wire007
  Symmetric = false
FEATURE [Part::MultiFuse] Fusion067  label="fanScrewHousing002"
  Shapes = -> [Revolve098,Revolve097,Revolve096,Revolve095]
FEATURE [Part::Feature] Face091 .. Face094  x4 (patterned run collapsed; names and placements below)
  shape: bbox 3.5 x 17.8 x 2e-07 mm, 1 faces, 0 solids (baked)
FEATURE [Part::Revolution] Revolve099  label="removeToCreateScrewAndThreadedInsertHole026"
  Angle = 360
  Axis = (0,1,0)
  Base = (0,0,0)
  FaceMakerClass = Part::FaceMakerBullseye
  Placement = pos=(62.3,30.3,19.7) rot=(0,0,1;0rad)
  Solid = false
  Source = -> Face091
  Symmetric = false
FEATURE [Part::Revolution] Revolve100  label="removeToCreateScrewAndThreadedInsertHole027"
  Angle = 360
  Axis = (0,1,0)
  Base = (0,0,0)
  FaceMakerClass = Part::FaceMakerBullseye
  Placement = pos=(62.3,30.3,51.7) rot=(0,0,1;0rad)
  Solid = false
  Source = -> Face092
  Symmetric = false
FEATURE [Part::Revolution] Revolve101  label="removeToCreateScrewAndThreadedInsertHole028"
  Angle = 360
  Axis = (0,1,0)
  Base = (0,0,0)
  FaceMakerClass = Part::FaceMakerBullseye
  Placement = pos=(30.3,30.3,19.7) rot=(0,0,1;0rad)
  Solid = false
  Source = -> Face093
  Symmetric = false
FEATURE [Part::Revolution] Revolve102  label="removeToCreateScrewAndThreadedInsertHole029"
  Angle = 360
  Axis = (0,1,0)
  Base = (0,0,0)
  FaceMakerClass = Part::FaceMakerBullseye
  Placement = pos=(30.3,30.3,51.7) rot=(0,0,1;0rad)
  Solid = false
  Source = -> Face094
  Symmetric = false
FEATURE [Part::MultiFuse] Fusion068  label="createThreadedInsertHolesForFan002"
  Shapes = -> [Revolve099,Revolve100,Revolve101,Revolve102]
FEATURE [Part::Cut] Cut026  label="fanScrewHousing003"
  Base = -> Fusion067
  Tool = -> Fusion068
FEATURE [Sketcher::SketchObject] Sketch048
  FullyConstrained = false
  Placement = pos=(0,0,0) rot=(1,0,0;1.5708rad)
  sketch-geometry (24):
    g0: ArcOfCircle CenterX=-4 CenterY=-10.5 CenterZ=0 NormalX=0 NormalY=0 NormalZ=1 AngleXU=0 Radius=1.5 StartAngle=6e-16 EndAngle=3.14159
    g1: ArcOfCircle CenterX=-34.2 CenterY=-10.5 CenterZ=0 NormalX=0 NormalY=0 NormalZ=1 AngleXU=0 Radius=1.5 StartAngle=0 EndAngle=3.14159
    g2: ArcOfCircle CenterX=-34.2 CenterY=-27.7 CenterZ=0 NormalX=0 NormalY=0 NormalZ=1 AngleXU=0 Radius=1.5 StartAngle=3.14159 EndAngle=6.28319
    g3: ArcOfCircle CenterX=-4 CenterY=-27.7 CenterZ=0 NormalX=0 NormalY=0 NormalZ=1 AngleXU=0 Radius=1.5 StartAngle=3.1416 EndAngle=6.28319
    g4: ArcOfCircle CenterX=-10 CenterY=-4.3 CenterZ=0 NormalX=0 NormalY=0 NormalZ=1 AngleXU=0 Radius=1.5 StartAngle=2e-16 EndAngle=3.14159
    g5: ArcOfCircle CenterX=-16.1 CenterY=-1.8 CenterZ=0 NormalX=0 NormalY=0 NormalZ=1 AngleXU=0 Radius=1.5 StartAngle=5e-16 EndAngle=3.14159
    g6: ArcOfCircle CenterX=-22.1 CenterY=-1.8 CenterZ=0 NormalX=0 NormalY=0 NormalZ=1 AngleXU=0 Radius=1.5 StartAngle=5e-16 EndAngle=3.14159
    g7: ArcOfCircle CenterX=-28.2 CenterY=-4.3 CenterZ=0 NormalX=0 NormalY=0 NormalZ=1 AngleXU=0 Radius=1.5 StartAngle=2e-16 EndAngle=3.14159
    g8: ArcOfCircle CenterX=-10 CenterY=-33.9 CenterZ=0 NormalX=0 NormalY=0 NormalZ=1 AngleXU=0 Radius=1.5 StartAngle=3.14159 EndAngle=6.28319
    g9: ArcOfCircle CenterX=-16.1 CenterY=-36.4 CenterZ=0 NormalX=0 NormalY=0 NormalZ=1 AngleXU=0 Radius=1.5 StartAngle=3.14159 EndAngle=6.28319
    g10: ArcOfCircle CenterX=-22.1 CenterY=-36.4 CenterZ=0 NormalX=0 NormalY=0 NormalZ=1 AngleXU=0 Radius=1.5 StartAngle=3.14159 EndAngle=6.28319
    g11: ArcOfCircle CenterX=-28.2 CenterY=-33.9 CenterZ=0 NormalX=0 NormalY=0 NormalZ=1 AngleXU=0 Radius=1.5 StartAngle=3.14159 EndAngle=6.28319
    g12: LineSegment StartX=-35.7 StartY=-10.5 StartZ=0 EndX=-35.7 EndY=-27.7 EndZ=0
    g13: LineSegment StartX=-32.7 StartY=-10.5 StartZ=0 EndX=-32.7 EndY=-27.7 EndZ=0
    g14: LineSegment StartX=-29.7 StartY=-33.9 StartZ=0 EndX=-29.7 EndY=-4.3 EndZ=0
    g15: LineSegment StartX=-26.7 StartY=-33.9 StartZ=0 EndX=-26.7 EndY=-4.3 EndZ=0
    g16: LineSegment StartX=-2.5 StartY=-10.5 StartZ=0 EndX=-2.5 EndY=-27.7 EndZ=0
    g17: LineSegment StartX=-8.5 StartY=-4.3 StartZ=0 EndX=-8.5 EndY=-33.9 EndZ=0
    g18: LineSegment StartX=-5.5 StartY=-10.5 StartZ=0 EndX=-5.5 EndY=-27.7 EndZ=0
    g19: LineSegment StartX=-11.5 StartY=-4.3 StartZ=0 EndX=-11.5 EndY=-33.9 EndZ=0
    g20: LineSegment StartX=-14.6 StartY=-1.8 StartZ=0 EndX=-14.6 EndY=-36.4 EndZ=0
    g21: LineSegment StartX=-17.6 StartY=-1.8 StartZ=0 EndX=-17.6 EndY=-36.4 EndZ=0
    g22: LineSegment StartX=-20.6 StartY=-36.4 StartZ=0 EndX=-20.6 EndY=-1.8 EndZ=0
    g23: LineSegment StartX=-23.6 StartY=-1.8 StartZ=0 EndX=-23.6 EndY=-36.4 EndZ=0
  constraints (48):
    c: Block(g0)
    c: Block(g1)
    c: Block(g2)
    c: Block(g3)
    c: Block(g4)
    c: Block(g5)
    c: Block(g6)
    c: Block(g7)
    c: Block(g8)
    c: Block(g9)
    c: Block(g10)
    c: Block(g11)
    c: Coincident(g12,g1)
    c: Coincident(g12,g2)
    c: Vertical(g12)
    c: Coincident(g13,g1)
    c: Coincident(g13,g2)
    c: Vertical(g13)
    c: Coincident(g14,g11)
    c: Coincident(g14,g7)
    c: Vertical(g14)
    c: Coincident(g15,g11)
    c: Coincident(g15,g7)
    c: Vertical(g15)
    c: Coincident(g16,g0)
    c: Coincident(g16,g3)
    c: Vertical(g16)
    c: Coincident(g17,g4)
    c: Coincident(g17,g8)
    c: Vertical(g17)
    c: Coincident(g18,g0)
    c: Coincident(g18,g3)
    c: Vertical(g18)
    c: Coincident(g19,g4)
    c: Coincident(g19,g8)
    c: Vertical(g19)
    c: Coincident(g20,g5)
    c: Coincident(g20,g9)
    c: Vertical(g20)
    c: Coincident(g21,g5)
    c: Coincident(g21,g9)
    c: Vertical(g21)
    c: Coincident(g22,g10)
    c: Coincident(g22,g6)
    c: Vertical(g22)
    c: Coincident(g23,g6)
    c: Coincident(g23,g10)
    c: Vertical(g23)
FEATURE [Part::Extrusion] Extrude039  label="removeToCreateFanGrillHoles002"
  Base = -> Sketch048
  Dir = (0,-1,6e-16)
  DirMode = 2
  FaceMakerClass = Part::FaceMakerBullseye
  LengthFwd = 10
  LengthRev = 0
  Placement = pos=(65.4,44,54.82) rot=(0,0,1;0rad)
  Solid = true
  Symmetric = false
FEATURE [Part::Cut] Cut027  label="fanScrewHousing004"
  Base = -> Cut026
  Tool = -> Extrude038
FEATURE [Part::Cut] Cut028  label="top014"
  Base = -> Fillet026
  Tool = -> Extrude039
FEATURE [Part::Feature] Face095 .. Face098  x4 (patterned run collapsed; names and placements below)
  shape: bbox 3.5 x 17.8 x 2e-07 mm, 1 faces, 0 solids (baked)
FEATURE [Part::Revolution] Revolve103  label="removeToCreateScrewAndThreadedInsertHole030"
  Angle = 360
  Axis = (0,1,0)
  Base = (0,0,0)
  FaceMakerClass = Part::FaceMakerBullseye
  Placement = pos=(62.3,30.3,19.7) rot=(0,0,1;0rad)
  Solid = false
  Source = -> Face095
  Symmetric = false
FEATURE [Part::Revolution] Revolve104  label="removeToCreateScrewAndThreadedInsertHole031"
  Angle = 360
  Axis = (0,1,0)
  Base = (0,0,0)
  FaceMakerClass = Part::FaceMakerBullseye
  Placement = pos=(62.3,30.3,51.7) rot=(0,0,1;0rad)
  Solid = false
  Source = -> Face096
  Symmetric = false
FEATURE [Part::Revolution] Revolve105  label="removeToCreateScrewAndThreadedInsertHole032"
  Angle = 360
  Axis = (0,1,0)
  Base = (0,0,0)
  FaceMakerClass = Part::FaceMakerBullseye
  Placement = pos=(30.3,30.3,19.7) rot=(0,0,1;0rad)
  Solid = false
  Source = -> Face097
  Symmetric = false
FEATURE [Part::Revolution] Revolve106  label="removeToCreateScrewAndThreadedInsertHole033"
  Angle = 360
  Axis = (0,1,0)
  Base = (0,0,0)
  FaceMakerClass = Part::FaceMakerBullseye
  Placement = pos=(30.3,30.3,51.7) rot=(0,0,1;0rad)
  Solid = false
  Source = -> Face098
  Symmetric = false
FEATURE [Part::MultiFuse] Fusion069  label="createThreadedInsertHolesForFan003"
  Shapes = -> [Revolve103,Revolve104,Revolve105,Revolve106]
FEATURE [Part::Cut] Cut029  label="top015"
  Base = -> Cut028
  Tool = -> Fusion054
FEATURE [Part::Cut] Cut030  label="fanScrewHousing005"
  Base = -> Cut027
  Tool = -> Fusion069
FEATURE [Part::Cylinder] Cylinder026  label="removeToCreteHoleForPlugHousing010"
  Angle = 360
  AttacherType = Attacher::AttachEngine3D
  Height = 20
  Placement = pos=(-2,19,36) rot=(0,1,0;1.5708rad)
  Radius = 14.3
FEATURE [Part::Box] Box018  label="removeToCreteHoleForPlugHousing011"
  AttacherType = Attacher::AttachEngine3D
  Height = 28.6
  Length = 10
  Placement = pos=(-2,0,21.7) rot=(0,0,1;0rad)
  Width = 19
FEATURE [Part::Box] Box019  label="wireHolderBottomCaseBit"
  AttacherType = Attacher::AttachEngine3D
  Height = 28
  Length = 3
  Placement = pos=(0,0,22) rot=(0,0,1;0rad)
  Width = 21
FEATURE [Part::Cylinder] Cylinder027  label="removeToCreteHoleForPlugHousing012"
  Angle = 360
  AttacherType = Attacher::AttachEngine3D
  Height = 20
  Placement = pos=(-2,19,36) rot=(0,1,0;1.5708rad)
  Radius = 14.3
FEATURE [Part::Cut] Cut031  label="wireHolderBottomCaseBit001"
  Base = -> Box019
  Tool = -> Cylinder027
FEATURE [Part::MultiFuse] Fusion070  label="removeToCreteHoleForPlugHousing013"
  Shapes = -> [Box018,Cylinder026]
FEATURE [Part::Cut] Cut032  label="top016"
  Base = -> Cut029
  Tool = -> Fusion070
FEATURE [Part::Cylinder] Cylinder028
  Angle = 360
  AttacherType = Attacher::AttachEngine3D
  Height = 20
  Placement = pos=(0,0,36.15) rot=(0,0,1;0rad)
  Radius = 14.3
FEATURE [Part::Cylinder] Cylinder029
  Angle = 360
  AttacherType = Attacher::AttachEngine3D
  Height = 10
  Placement = pos=(0,0,36.15) rot=(0,0,1;0rad)
  Radius = 4
FEATURE [Part::MultiFuse] Fusion071  label="removeToCreteHoleForPlugHousing014"
  Placement = pos=(70,19,36) rot=(0,1,0;1.5708rad)
  Shapes = -> [Cylinder028,Cylinder029]
FEATURE [Sketcher::SketchObject] Sketch049  label="topSketch011"
  FullyConstrained = true
  sketch-geometry (4):
    g0: ArcOfCircle CenterX=105 CenterY=19 CenterZ=0 NormalX=0 NormalY=0 NormalZ=1 AngleXU=0 Radius=20.6155 StartAngle=5.54125 EndAngle=6.28319
    g1: ArcOfCircle CenterX=105 CenterY=19 CenterZ=0 NormalX=0 NormalY=0 NormalZ=1 AngleXU=0 Radius=13 StartAngle=5.54125 EndAngle=6.28319
    g2: LineSegment StartX=118 StartY=19 StartZ=0 EndX=125.616 EndY=19 EndZ=0
    g3: LineSegment StartX=114.583 StartY=10.2157 StartZ=0 EndX=120.197 EndY=5.06982 EndZ=0
  constraints (7):
    c: Block(g0)
    c: Block(g1)
    c: Coincident(g2,g1)
    c: Coincident(g2,g0)
    c: Horizontal(g2)
    c: Coincident(g3,g1)
    c: Coincident(g3,g0)
FEATURE [Part::Box] Box020  label="removeToCreteHoleForPlugHousing015"
  AttacherType = Attacher::AttachEngine3D
  Height = 28.6
  Length = 20
  Placement = pos=(106.15,0,21.7) rot=(0,0,1;0rad)
  Width = 19
FEATURE [Part::MultiFuse] Fusion072  label="removeToCreteHoleForPlugHousing016"
  Shapes = -> [Box020,Fusion071]
FEATURE [Part::Cut] Cut033  label="removeToCreteHoleForPlugHousing017"
  Base = -> Cut032
  Tool = -> Fusion072
FEATURE [Part::Cylinder] Cylinder030
  Angle = 360
  AttacherType = Attacher::AttachEngine3D
  Height = 20
  Placement = pos=(0,0,36.15) rot=(0,0,1;0rad)
  Radius = 14.3
FEATURE [Part::Cylinder] Cylinder031
  Angle = 360
  AttacherType = Attacher::AttachEngine3D
  Height = 10
  Placement = pos=(0,0,36.15) rot=(0,0,1;0rad)
  Radius = 4
FEATURE [Part::Box] Box021  label="removeToCreteHoleForPlugHousing019"
  AttacherType = Attacher::AttachEngine3D
  Height = 28.6
  Length = 20
  Placement = pos=(106.15,0,21.7) rot=(0,0,1;0rad)
  Width = 19
FEATURE [Part::MultiFuse] Fusion074  label="removeToCreteHoleForPlugHousing020"
  Placement = pos=(70,19,36) rot=(0,1,0;1.5708rad)
  Shapes = -> [Cylinder030,Cylinder031]
FEATURE [Part::MultiFuse] Fusion073  label="removeToCreteHoleForPlugHousing018"
  Placement = pos=(0,0,28.3) rot=(0,0,1;0rad)
  Shapes = -> [Box021,Fusion074]
FEATURE [Part::Cylinder] Cylinder032
  Angle = 360
  AttacherType = Attacher::AttachEngine3D
  Height = 20
  Placement = pos=(0,0,36.15) rot=(0,0,1;0rad)
  Radius = 14.3
FEATURE [Part::Cylinder] Cylinder033
  Angle = 360
  AttacherType = Attacher::AttachEngine3D
  Height = 10
  Placement = pos=(0,0,36.15) rot=(0,0,1;0rad)
  Radius = 4
FEATURE [Part::Box] Box022  label="removeToCreteHoleForPlugHousing021"
  AttacherType = Attacher::AttachEngine3D
  Height = 28.6
  Length = 20
  Placement = pos=(106.15,0,21.7) rot=(0,0,1;0rad)
  Width = 19
FEATURE [Part::MultiFuse] Fusion076  label="removeToCreteHoleForPlugHousing023"
  Placement = pos=(70,19,36) rot=(0,1,0;1.5708rad)
  Shapes = -> [Cylinder032,Cylinder033]
FEATURE [Part::MultiFuse] Fusion075  label="removeToCreteHoleForPlugHousing022"
  Placement = pos=(0,0,-28.3) rot=(0,0,1;0rad)
  Shapes = -> [Box022,Fusion076]
FEATURE [Part::MultiFuse] Fusion077  label="removeToCreatePlugHousingBottomBit"
  Shapes = -> [Fusion075,Fusion073]
FEATURE [Part::Cylinder] Cylinder034
  Angle = 360
  AttacherType = Attacher::AttachEngine3D
  Height = 20
  Placement = pos=(0,0,36.15) rot=(0,0,1;0rad)
  Radius = 14
FEATURE [Part::Cylinder] Cylinder035
  Angle = 360
  AttacherType = Attacher::AttachEngine3D
  Height = 10
  Placement = pos=(0,0,36.15) rot=(0,0,1;0rad)
  Radius = 4
FEATURE [Part::MultiFuse] Fusion078  label="removeToCreteHoleForPlugHousing024"
  Placement = pos=(70,19,36) rot=(0,1,0;1.5708rad)
  Shapes = -> [Cylinder034,Cylinder035]
FEATURE [Part::MultiFuse] Fusion079  label="removeToCreatePlugHousingBottomBit001"
  Shapes = -> [Fusion078,Fusion077]
FEATURE [Part::Extrusion] Extrude040  label="bottomPlugHousingBit"
  Base = -> Sketch049
  Dir = (0,0,1)
  DirMode = 2
  FaceMakerClass = Part::FaceMakerBullseye
  LengthFwd = 72
  LengthRev = 0
  Solid = true
  Symmetric = false
FEATURE [Part::Cut] Cut034  label="bottomPlugHousingBit001"
  Base = -> Extrude040
  Placement = pos=(-0.09,0,0) rot=(0,0,1;0rad)
  Tool = -> Fusion079
FEATURE [Part::Box] Box023  label="Cube014"
  AttacherType = Attacher::AttachEngine3D
  Height = 16
  Length = 8
  Placement = pos=(12.7,31.52,28) rot=(0,0,1;0rad)
  Width = 4
FEATURE [Part::Cylinder] Cylinder036
  Angle = 360
  AttacherType = Attacher::AttachEngine3D
  Height = 10
  Placement = pos=(0,0,36.15) rot=(0,0,1;0rad)
  Radius = 4
FEATURE [Part::Cylinder] Cylinder037
  Angle = 360
  AttacherType = Attacher::AttachEngine3D
  Height = 20
  Placement = pos=(0,0,36.15) rot=(0,0,1;0rad)
  Radius = 8.2
FEATURE [Part::MultiFuse] Fusion080  label="removeToCreteHoleForPlugHousing025"
  Placement = pos=(-42,19,36) rot=(0,1,0;1.5708rad)
  Shapes = -> [Cylinder037,Cylinder036]
FEATURE [Sketcher::SketchObject] Sketch050  label="topSketch012"
  FullyConstrained = true
  sketch-geometry (4):
    g0: LineSegment StartX=16.8446 StartY=31.512 StartZ=0 EndX=16.3251 EndY=34.4666 EndZ=0
    g1: ArcOfCircle CenterX=19 CenterY=19.2524 CenterZ=0 NormalX=0 NormalY=0 NormalZ=1 AngleXU=0 Radius=15.4476 StartAngle=1.74483 EndAngle=2.72717
    g2: ArcOfCircle CenterX=19 CenterY=19.2524 CenterZ=0 NormalX=0 NormalY=0 NormalZ=1 AngleXU=0 Radius=12.4476 StartAngle=1.74483 EndAngle=2.73189
    g3: LineSegment StartX=4.86004 StartY=25.4725 StartZ=0 EndX=7.58253 EndY=24.2107 EndZ=0
  constraints (7):
    c: Block(g0)
    c: Coincident(g1,g0)
    c: Coincident(g2,g0)
    c: Coincident(g3,g1)
    c: Coincident(g3,g2)
    c: Block(g1)
    c: Block(g2)
FEATURE [Part::Extrusion] Extrude041
  Base = -> Sketch050
  Dir = (0,0,1)
  DirMode = 2
  FaceMakerClass = Part::FaceMakerBullseye
  LengthFwd = 10.6
  LengthRev = 0
  Placement = pos=(0,0,31) rot=(0,0,1;0rad)
  Solid = true
  Symmetric = false
FEATURE [Part::Cut] Cut035
  Base = -> Extrude041
  Placement = pos=(0,0,-0.3) rot=(0,0,1;0rad)
  Tool = -> Fusion080
FEATURE [Part::Cut] Cut036
  Base = -> Box023
  Tool = -> Cut035
FEATURE [Part::Fillet] Fillet027
  Base = -> Cut036
  Edges = 1 edges r=0.7: [Edge13]
FEATURE [Part::Fillet] Fillet028
  Base = -> Fillet027
  Edges = 1 edges r=0.7: [Edge13]
FEATURE [Part::Fillet] Fillet029
  Base = -> Fillet028
  Edges = 1 edges r=0.7: [Edge16]
FEATURE [Part::Fillet] Fillet030
  Base = -> Fillet029
  Edges = 1 edges r=0.7: [Edge11]
FEATURE [Part::Fillet] Fillet031
  Base = -> Fillet030
  Edges = 1 edges r=0.7: [Edge10]
FEATURE [Part::Fillet] Fillet032
  Base = -> Fillet031
  Edges = 1 edges r=1.2: [Edge5]
FEATURE [Part::Fillet] Fillet033
  Base = -> Fillet032
  Edges = 1 edges r=1.2: [Edge12]
FEATURE [Part::Fillet] Fillet034  label="wireHousingRetainer"
  Base = -> Fillet033
  Edges = 1 edges r=2: [Edge1]
  Placement = pos=(0.3,0,0) rot=(0,0,1;0rad)
FEATURE [Part::Feature] Face099
  shape: bbox 3.5 x 17.8 x 2e-07 mm, 1 faces, 0 solids (baked)
FEATURE [Part::Revolution] Revolve107  label="removeToCreateScrewAndThreadedInsertHole034"
  Angle = 360
  Axis = (0,1,0)
  Base = (0,0,0)
  FaceMakerClass = Part::FaceMakerBullseye
  Placement = pos=(12.5,0,10) rot=(0,0,1;0rad)
  Solid = false
  Source = -> Face099
  Symmetric = false
FEATURE [Part::Feature] Face100
  shape: bbox 3.5 x 17.8 x 2e-07 mm, 1 faces, 0 solids (baked)
FEATURE [Part::Revolution] Revolve108  label="removeToCreateScrewAndThreadedInsertHole035"
  Angle = 360
  Axis = (0,1,0)
  Base = (0,0,0)
  FaceMakerClass = Part::FaceMakerBullseye
  Placement = pos=(12.5,0,62) rot=(0,0,1;0rad)
  Solid = false
  Source = -> Face100
  Symmetric = false
FEATURE [Part::Feature] Face101
  shape: bbox 3.5 x 17.8 x 2e-07 mm, 1 faces, 0 solids (baked)
FEATURE [Part::Revolution] Revolve109  label="removeToCreateScrewAndThreadedInsertHole036"
  Angle = 360
  Axis = (0,1,0)
  Base = (0,0,0)
  FaceMakerClass = Part::FaceMakerBullseye
  Placement = pos=(89.5,0,68.5) rot=(0,0,1;0rad)
  Solid = false
  Source = -> Face101
  Symmetric = false
FEATURE [Part::Feature] Face102
  shape: bbox 3.5 x 17.8 x 2e-07 mm, 1 faces, 0 solids (baked)
FEATURE [Part::Revolution] Revolve110  label="removeToCreateScrewAndThreadedInsertHole037"
  Angle = 360
  Axis = (0,1,0)
  Base = (0,0,0)
  FaceMakerClass = Part::FaceMakerBullseye
  Placement = pos=(89.5,0,3.5) rot=(0,0,1;0rad)
  Solid = false
  Source = -> Face102
  Symmetric = false
FEATURE [Part::Feature] Face103
  shape: bbox 3.5 x 17.8 x 2e-07 mm, 1 faces, 0 solids (baked)
FEATURE [Part::Revolution] Revolve111  label="removeToCreateScrewAndThreadedInsertHole038"
  Angle = 360
  Axis = (0,1,0)
  Base = (0,0,0)
  FaceMakerClass = Part::FaceMakerBullseye
  Placement = pos=(109.5,4.7,3.5) rot=(0,0,1;0rad)
  Solid = false
  Source = -> Face103
  Symmetric = false
FEATURE [Part::Feature] Face104
  shape: bbox 3.5 x 17.8 x 2e-07 mm, 1 faces, 0 solids (baked)
FEATURE [Part::Revolution] Revolve112  label="removeToCreateScrewAndThreadedInsertHole039"
  Angle = 360
  Axis = (0,1,0)
  Base = (0,0,0)
  FaceMakerClass = Part::FaceMakerBullseye
  Placement = pos=(109.5,4.7,68.5) rot=(0,0,1;0rad)
  Solid = false
  Source = -> Face104
  Symmetric = false
FEATURE [Part::MultiFuse] Fusion081  label="removeToCreateScrewAndThreadedInsertHole040"
  Shapes = -> [Revolve107,Revolve108,Revolve109,Revolve110,Revolve111,Revolve112]
FEATURE [Part::MultiFuse] Fusion082  label="casePillars002"
  Shapes = -> [Revolve094,Revolve092,Revolve090,Revolve089,Revolve091,Revolve093]
FEATURE [Part::Cut] Cut037  label="casePillars003"
  Base = -> Fusion082
  Tool = -> Fusion081
FEATURE [Sketcher::SketchObject] Sketch051
  FullyConstrained = true
  Placement = pos=(117,19,0) rot=(0.57735,0.57735,0.57735;2.0944rad)
  sketch-geometry (48):
    g0: LineSegment StartX=-49.19 StartY=69.25 StartZ=0 EndX=-49.19 EndY=66.25 EndZ=0
    g1: LineSegment StartX=-49.19 StartY=63.5 StartZ=0 EndX=-49.19 EndY=60.5 EndZ=0
    g2: LineSegment StartX=-49.19 StartY=57.75 StartZ=0 EndX=-49.19 EndY=54.75 EndZ=0
    g3: LineSegment StartX=-49.19 StartY=52 StartZ=0 EndX=-49.19 EndY=49 EndZ=0
    g4: LineSegment StartX=-49.19 StartY=46.25 StartZ=0 EndX=-49.19 EndY=43.25 EndZ=0
    g5: LineSegment StartX=-49.19 StartY=40.5 StartZ=0 EndX=-49.19 EndY=37.5 EndZ=0
    g6: LineSegment StartX=-49.19 StartY=34.5 StartZ=0 EndX=-49.19 EndY=31.5 EndZ=0
    g7: LineSegment StartX=-49.19 StartY=28.75 StartZ=0 EndX=-49.19 EndY=25.75 EndZ=0
    g8: LineSegment StartX=-49.19 StartY=23 StartZ=0 EndX=-49.19 EndY=20 EndZ=0
    g9: LineSegment StartX=-49.19 StartY=17.25 StartZ=0 EndX=-49.19 EndY=14.25 EndZ=0
    g10: LineSegment StartX=-49.19 StartY=11.5 StartZ=0 EndX=-49.19 EndY=8.5 EndZ=0
    g11: LineSegment StartX=-49.19 StartY=5.75 StartZ=0 EndX=-49.19 EndY=2.75 EndZ=0
    g12: ArcOfCircle CenterX=-1.5 CenterY=67.75 CenterZ=0 NormalX=0 NormalY=0 NormalZ=1 AngleXU=0 Radius=1.5 StartAngle=4.71239 EndAngle=7.85398
    g13: ArcOfCircle CenterX=-1.5 CenterY=62 CenterZ=0 NormalX=0 NormalY=0 NormalZ=1 AngleXU=0 Radius=1.5 StartAngle=4.71239 EndAngle=7.85398
    g14: ArcOfCircle CenterX=-1.5 CenterY=56.25 CenterZ=0 NormalX=0 NormalY=0 NormalZ=1 AngleXU=0 Radius=1.5 StartAngle=4.71239 EndAngle=7.85398
    g15: ArcOfCircle CenterX=-11.49 CenterY=50.5 CenterZ=0 NormalX=0 NormalY=0 NormalZ=1 AngleXU=0 Radius=1.5 StartAngle=4.71239 EndAngle=7.85398
    g16: ArcOfCircle CenterX=-16.28 CenterY=44.75 CenterZ=0 NormalX=0 NormalY=0 NormalZ=1 AngleXU=0 Radius=1.5 StartAngle=4.71239 EndAngle=7.85398
    g17: ArcOfCircle CenterX=-18.2337 CenterY=39 CenterZ=0 NormalX=0 NormalY=0 NormalZ=1 AngleXU=0 Radius=1.5 StartAngle=4.71485 EndAngle=7.85398
    g18: ArcOfCircle CenterX=-16.2837 CenterY=27.25 CenterZ=0 NormalX=0 NormalY=0 NormalZ=1 AngleXU=0 Radius=1.5 StartAngle=4.71485 EndAngle=7.85398
    g19: ArcOfCircle CenterX=-18.2337 CenterY=33 CenterZ=0 NormalX=0 NormalY=0 NormalZ=1 AngleXU=0 Radius=1.5 StartAngle=4.71485 EndAngle=7.85398
    g20: ArcOfCircle CenterX=-11.49 CenterY=21.5 CenterZ=0 NormalX=0 NormalY=0 NormalZ=1 AngleXU=0 Radius=1.5 StartAngle=4.71239 EndAngle=7.85398
    g21: ArcOfCircle CenterX=-1.5 CenterY=4.25 CenterZ=0 NormalX=0 NormalY=0 NormalZ=1 AngleXU=0 Radius=1.5 StartAngle=4.71239 EndAngle=7.85398
    g22: ArcOfCircle CenterX=-1.5 CenterY=10 CenterZ=0 NormalX=0 NormalY=0 NormalZ=1 AngleXU=0 Radius=1.5 StartAngle=4.71239 EndAngle=7.85398
    g23: ArcOfCircle CenterX=-1.5 CenterY=15.75 CenterZ=0 NormalX=0 NormalY=0 NormalZ=1 AngleXU=0 Radius=1.5 StartAngle=4.71239 EndAngle=7.85398
    g24: LineSegment StartX=-49.19 StartY=69.25 StartZ=0 EndX=-1.5 EndY=69.25 EndZ=0
    g25: LineSegment StartX=-49.19 StartY=66.25 StartZ=0 EndX=-1.5 EndY=66.25 EndZ=0
    g26: LineSegment StartX=-49.19 StartY=63.5 StartZ=0 EndX=-1.5 EndY=63.5 EndZ=0
    g27: LineSegment StartX=-49.19 StartY=60.5 StartZ=0 EndX=-1.5 EndY=60.5 EndZ=0
    g28: LineSegment StartX=-49.19 StartY=57.75 StartZ=0 EndX=-1.5 EndY=57.75 EndZ=0
    g29: LineSegment StartX=-49.19 StartY=54.75 StartZ=0 EndX=-1.5 EndY=54.75 EndZ=0
    g30: LineSegment StartX=-49.19 StartY=52 StartZ=0 EndX=-11.49 EndY=52 EndZ=0
    g31: LineSegment StartX=-49.19 StartY=49 StartZ=0 EndX=-11.49 EndY=49 EndZ=0
    g32: LineSegment StartX=-49.19 StartY=46.25 StartZ=0 EndX=-16.28 EndY=46.25 EndZ=0
    g33: LineSegment StartX=-49.19 StartY=43.25 StartZ=0 EndX=-16.28 EndY=43.25 EndZ=0
    g34: LineSegment StartX=-49.19 StartY=40.5 StartZ=0 EndX=-18.2337 EndY=40.5 EndZ=0
    g35: LineSegment StartX=-49.19 StartY=37.5 StartZ=0 EndX=-18.23 EndY=37.5 EndZ=0
    g36: LineSegment StartX=-49.19 StartY=34.5 StartZ=0 EndX=-18.2337 EndY=34.5 EndZ=0
    g37: LineSegment StartX=-49.19 StartY=31.5 StartZ=0 EndX=-18.23 EndY=31.5 EndZ=0
    g38: LineSegment StartX=-49.19 StartY=28.75 StartZ=0 EndX=-16.2837 EndY=28.75 EndZ=0
    g39: LineSegment StartX=-49.19 StartY=25.75 StartZ=0 EndX=-16.28 EndY=25.75 EndZ=0
    g40: LineSegment StartX=-49.19 StartY=23 StartZ=0 EndX=-11.49 EndY=23 EndZ=0
    g41: LineSegment StartX=-49.19 StartY=20 StartZ=0 EndX=-11.49 EndY=20 EndZ=0
    g42: LineSegment StartX=-49.19 StartY=17.25 StartZ=0 EndX=-1.5 EndY=17.25 EndZ=0
    g43: LineSegment StartX=-49.19 StartY=14.25 StartZ=0 EndX=-1.5 EndY=14.25 EndZ=0
    g44: LineSegment StartX=-49.19 StartY=11.5 StartZ=0 EndX=-1.5 EndY=11.5 EndZ=0
    g45: LineSegment StartX=-49.19 StartY=8.5 StartZ=0 EndX=-1.5 EndY=8.5 EndZ=0
    g46: LineSegment StartX=-49.19 StartY=5.75 StartZ=0 EndX=-1.5 EndY=5.75 EndZ=0
    g47: LineSegment StartX=-49.19 StartY=2.75 StartZ=0 EndX=-1.5 EndY=2.75 EndZ=0
  constraints (120):
    c: Vertical(g0)
    c: Distance(g0) = 3
    c: Block(g0)
    c: Vertical(g1)
    c: Distance(g1) = 3
    c: Vertical(g2)
    c: Equal(g0,g2) = 3
    c: Block(g2)
    c: Vertical(g3)
    c: Equal(g1,g3) = 3
    c: Vertical(g4)
    c: Equal(g0,g4) = 3
    c: Block(g4)
    c: Vertical(g5)
    c: Equal(g1,g5) = 3
    c: Vertical(g6)
    c: Equal(g0,g6) = 3
    c: Block(g6)
    c: Vertical(g7)
    c: Equal(g1,g7) = 3
    c: Vertical(g8)
    c: Equal(g0,g8) = 3
    c: Block(g8)
    c: Vertical(g9)
    c: Equal(g1,g9) = 3
    c: Vertical(g10)
    c: Equal(g0,g10) = 3
    c: Block(g10)
    c: Vertical(g11)
    c: Equal(g1,g11) = 3
    c: Block(g12)
    c: Block(g13)
    c: Block(g14)
    c: Block(g15)
    c: Block(g16)
    c: Block(g17)
    c: Block(g18)
    c: Block(g19)
    c: Block(g20)
    c: Block(g21)
    c: Block(g22)
    c: Block(g23)
    c: Block(g11)
    c: Block(g9)
    c: Block(g7)
    c: Block(g5)
    c: Block(g3)
    c: Block(g1)
    c: Coincident(g24,g0)
    c: Coincident(g24,g12)
    c: Horizontal(g24)
    c: Coincident(g25,g0)
    c: Coincident(g25,g12)
    c: Horizontal(g25)
    c: Coincident(g26,g1)
    c: Coincident(g26,g13)
    c: Horizontal(g26)
    c: Coincident(g27,g1)
    c: Coincident(g27,g13)
    c: Horizontal(g27)
    c: Coincident(g28,g2)
    c: Coincident(g28,g14)
    c: Horizontal(g28)
    c: Coincident(g29,g2)
    c: Coincident(g29,g14)
    c: Horizontal(g29)
    c: Coincident(g30,g3)
    c: Coincident(g30,g15)
    c: Horizontal(g30)
    c: Coincident(g31,g3)
    c: Coincident(g31,g15)
    c: Horizontal(g31)
    c: Coincident(g32,g4)
    c: Coincident(g32,g16)
    c: Horizontal(g32)
    c: Coincident(g33,g4)
    c: Coincident(g33,g16)
    c: Horizontal(g33)
    c: Coincident(g34,g5)
    c: Coincident(g34,g17)
    c: Horizontal(g34)
    c: Coincident(g35,g5)
    c: Coincident(g35,g17)
    c: Horizontal(g35)
    c: Coincident(g36,g6)
    c: Coincident(g36,g19)
    c: Horizontal(g36)
    c: Coincident(g37,g6)
    c: Coincident(g37,g19)
    c: Horizontal(g37)
    c: Coincident(g38,g7)
    c: Coincident(g38,g18)
    c: Horizontal(g38)
    c: Coincident(g39,g7)
    c: Coincident(g39,g18)
    c: Horizontal(g39)
    c: Coincident(g40,g8)
    c: Coincident(g40,g20)
    c: Horizontal(g40)
    c: Coincident(g41,g8)
    c: Coincident(g41,g20)
    c: Horizontal(g41)
    c: Coincident(g42,g9)
    c: Coincident(g42,g23)
    c: Horizontal(g42)
    c: Coincident(g43,g9)
    c: Coincident(g43,g23)
    c: Horizontal(g43)
    c: Coincident(g44,g10)
    c: Coincident(g44,g22)
    c: Horizontal(g44)
    c: Coincident(g45,g10)
    c: Coincident(g45,g22)
    c: Horizontal(g45)
    c: Coincident(g46,g11)
    c: Coincident(g46,g21)
    c: Horizontal(g46)
    c: Coincident(g47,g11)
    c: Coincident(g47,g21)
    c: Horizontal(g47)
FEATURE [Part::Extrusion] Extrude042
  Base = -> Sketch051
  Dir = (1,-2e-16,2e-16)
  DirMode = 2
  FaceMakerClass = Part::FaceMakerBullseye
  LengthFwd = 19
  LengthRev = 0
  Placement = pos=(-19,0,0) rot=(0,0,1;0rad)
  Solid = true
  Symmetric = false
FEATURE [Part::Fillet] Fillet035  label="removeToCreateVentalationHoles"
  Base = -> Extrude042
  Edges = <same value as first occurrence — deduplicated (x6 in doc)>
  Placement = pos=(7,0,0) rot=(0,0,1;0rad)
FEATURE [Part::Cut] Cut038  label="top017"
  Base = -> Cut033
  Tool = -> Fillet035
FEATURE [Sketcher::SketchObject] Sketch052  label="bottomSketch001"
  FullyConstrained = true
  sketch-geometry (45):
    g0: LineSegment StartX=6.29999 StartY=8 StartZ=0 EndX=3.29999 EndY=8 EndZ=0
    g1: LineSegment StartX=3.29999 StartY=8 StartZ=0 EndX=3.29999 EndY=-6.03275e-07 EndZ=0
    g2: ArcOfCircle CenterX=8.29999 CenterY=5 CenterZ=0 NormalX=0 NormalY=0 NormalZ=1 AngleXU=0 Radius=2 StartAngle=3.14159 EndAngle=4.71239
    g3: LineSegment StartX=6.29999 StartY=8 StartZ=0 EndX=6.29999 EndY=5 EndZ=0
    g4: ArcOfCircle CenterX=105 CenterY=19 CenterZ=0 NormalX=0 NormalY=0 NormalZ=1 AngleXU=0 Radius=12.7 StartAngle=4.71239 EndAngle=5.94289
    g5-g11: Circle x7 (B-spline internal-alignment scaffolding for g12; pole/knot coordinates omitted)
    g12: BSplineCurve PolesCount=7 KnotsCount=5 Degree=3 IsPeriodic=0
    g13-g17: GeomPoint x5 (B-spline internal-alignment scaffolding for g12; pole/knot coordinates omitted)
    g18: ArcOfCircle CenterX=105 CenterY=19 CenterZ=0 NormalX=0 NormalY=0 NormalZ=1 AngleXU=0 Radius=15.7 StartAngle=5.81226 EndAngle=6.28319
    g19: BSplineCurve PolesCount=5 KnotsCount=3 Degree=3 IsPeriodic=0
    g20: LineSegment StartX=8.29999 StartY=3 StartZ=0 EndX=101.7 EndY=3 EndZ=0
    g21: LineSegment StartX=3.29999 StartY=-6.03275e-07 StartZ=0 EndX=105 EndY=-6.03275e-07 EndZ=0
    g22: LineSegment StartX=120.974 StartY=8.71251 StartZ=0 EndX=122.332 EndY=7.83778 EndZ=0
    g23: LineSegment StartX=105 StartY=-6.03274e-07 StartZ=0 EndX=113 EndY=-6.03274e-07 EndZ=0
    g24: ArcOfCircle CenterX=105 CenterY=19 CenterZ=0 NormalX=0 NormalY=0 NormalZ=1 AngleXU=0 Radius=20.6155 StartAngle=5.11091 EndAngle=5.71103
    g25: ArcOfCircle CenterX=117.7 CenterY=19 CenterZ=0 NormalX=0 NormalY=0 NormalZ=1 AngleXU=0 Radius=3 StartAngle=1.2e-15 EndAngle=2.10468
    g26: Circle CenterX=116.345 CenterY=16.3232 CenterZ=0 NormalX=0 NormalY=0 NormalZ=1 AngleXU=0 Radius=1
    g27: Circle CenterX=117.24 CenterY=15.7584 CenterZ=0 NormalX=0 NormalY=0 NormalZ=1 AngleXU=0 Radius=1
    g28: Circle CenterX=116.972 CenterY=14.7612 CenterZ=0 NormalX=0 NormalY=0 NormalZ=1 AngleXU=0 Radius=1
    g29: BSplineCurve PolesCount=3 KnotsCount=2 Degree=2 IsPeriodic=0
    g30: GeomPoint X=116.345 Y=16.3232 Z=0
    g31: GeomPoint X=116.972 Y=14.7612 Z=0
    g32: Circle CenterX=115.828 CenterY=17.157 CenterZ=0 NormalX=0 NormalY=0 NormalZ=1 AngleXU=0 Radius=1
    g33: Circle CenterX=115.841 CenterY=16.639 CenterZ=0 NormalX=0 NormalY=0 NormalZ=1 AngleXU=0 Radius=1
    g34: Circle CenterX=116.345 CenterY=16.3232 CenterZ=0 NormalX=0 NormalY=0 NormalZ=1 AngleXU=0 Radius=1
    g35: BSplineCurve PolesCount=3 KnotsCount=2 Degree=2 IsPeriodic=0
    g36: GeomPoint X=115.828 Y=17.157 Z=0
    g37: GeomPoint X=116.345 Y=16.3232 Z=0
    g38: LineSegment StartX=115.828 StartY=17.157 StartZ=0 EndX=115.828 EndY=20.8307 EndZ=0
    g39: Circle CenterX=115.828 CenterY=20.8307 CenterZ=0 NormalX=0 NormalY=0 NormalZ=1 AngleXU=0 Radius=1
    g40: Circle CenterX=115.831 CenterY=21.3396 CenterZ=0 NormalX=0 NormalY=0 NormalZ=1 AngleXU=0 Radius=1
    g41: Circle CenterX=116.173 CenterY=21.5825 CenterZ=0 NormalX=0 NormalY=0 NormalZ=1 AngleXU=0 Radius=1
    g42: BSplineCurve PolesCount=3 KnotsCount=2 Degree=2 IsPeriodic=0
    g43: GeomPoint X=115.828 Y=20.8307 Z=0
    g44: GeomPoint X=116.173 Y=21.5825 Z=0
  constraints (70):
    c: Horizontal(g0)
    c: Distance(g0) = 3
    c: Coincident(g1,g0)
    c: Vertical(g1)
    c: Block(g2)
    c: Block(g0)
    c: Coincident(g3,g0)
    c: Coincident(g3,g2)
    c: Vertical(g3)
    c: Block(g1)
    c: Block(g4)
    c: Coincident(g19,g4)
    c: Block(g19)
    c: Equal(g5, g6-g11) x6
    c: InternalAlignment(g5-g11 -> g12) x7
    c: InternalAlignment(g13-g17 -> g12) x5
    c: Block(g12)
    c: Coincident(g18,g12)
    c: Block(g18)
    c: Coincident(g20,g2)
    c: Coincident(g20,g19)
    c: Horizontal(g20)
    c: Distance(g20) = 93.4
    c: Coincident(g21,g1)
    c: Horizontal(g21)
    c: Distance(g21) = 101.7
    c: Horizontal(g23)
    c: Distance(g23) = 8
    c: Coincident(g24,g23)
    c: Block(g23)
    c: Coincident(g22,g24)
    c: Block(g24)
    c: Block(g22)
    c: Distance(g22) = 1.61553
    c: Coincident(g25,g18)
    c: Block(g25)
    c: Weight(g26) = 1
    c: Equal(g26,g27)
    c: Equal(g26,g28)
    c: Coincident(g29,g4)
    c: InternalAlignment(g26,g29)
    c: InternalAlignment(g27,g29)
    c: InternalAlignment(g28,g29)
    c: InternalAlignment(g30,g29)
    c: InternalAlignment(g31,g29)
    c: Block(g29)
    c: Weight(g32) = 1
    c: Equal(g32,g33)
    c: Equal(g32,g34)
    c: Coincident(g35,g29)
    c: InternalAlignment(g32,g35)
    c: InternalAlignment(g33,g35)
    c: InternalAlignment(g34,g35)
    c: InternalAlignment(g36,g35)
    c: InternalAlignment(g37,g35)
    c: Block(g35)
    c: Coincident(g38,g35)
    c: Vertical(g38)
    c: Block(g38)
    c: Coincident(g42,g38)
    c: Weight(g39) = 1
    c: Equal(g39,g40)
    c: Equal(g39,g41)
    c: Coincident(g42,g25)
    c: InternalAlignment(g39,g42)
    c: InternalAlignment(g40,g42)
    c: InternalAlignment(g41,g42)
    c: InternalAlignment(g43,g42)
    c: InternalAlignment(g44,g42)
    c: Block(g42)
FEATURE [Part::Extrusion] Extrude043  label="bottom010"
  Base = -> Sketch052
  Dir = (0,0,1)
  DirMode = 2
  FaceMakerClass = Part::FaceMakerBullseye
  LengthFwd = 71.4
  LengthRev = 0
  Placement = pos=(0,0,0.3) rot=(0,0,1;0rad)
  Solid = true
  Symmetric = false
FEATURE [Sketcher::SketchObject] Sketch053  label="topSketch013"
  FullyConstrained = true
  sketch-geometry (22):
    g0: LineSegment StartX=5.21097e-06 StartY=3 StartZ=0 EndX=5.21097e-06 EndY=19 EndZ=0
    g1: ArcOfCircle CenterX=19 CenterY=19 CenterZ=0 NormalX=0 NormalY=0 NormalZ=1 AngleXU=0 Radius=19 StartAngle=1.5708 EndAngle=3.14159
    g2: ArcOfCircle CenterX=19 CenterY=19 CenterZ=0 NormalX=0 NormalY=0 NormalZ=1 AngleXU=0 Radius=16 StartAngle=1.5708 EndAngle=3.14159
    g3: LineSegment StartX=114 StartY=35 StartZ=0 EndX=19 EndY=35 EndZ=0
    g4: LineSegment StartX=5.21097e-06 StartY=3 StartZ=0 EndX=5.21097e-06 EndY=0 EndZ=0
    g5: LineSegment StartX=3 StartY=0 StartZ=0 EndX=5.21097e-06 EndY=0 EndZ=0
    g6: LineSegment StartX=3 StartY=19 StartZ=0 EndX=3 EndY=0 EndZ=0
    g7: LineSegment StartX=19 StartY=38 StartZ=0 EndX=124 EndY=38 EndZ=0
    g8: Circle CenterX=119 CenterY=35 CenterZ=0 NormalX=0 NormalY=0 NormalZ=1 AngleXU=0 Radius=1
    g9: Circle CenterX=121 CenterY=35 CenterZ=0 NormalX=0 NormalY=0 NormalZ=1 AngleXU=0 Radius=1
    g10: Circle CenterX=121 CenterY=33 CenterZ=0 NormalX=0 NormalY=0 NormalZ=1 AngleXU=0 Radius=1
    g11: BSplineCurve PolesCount=3 KnotsCount=2 Degree=2 IsPeriodic=0
    g12: GeomPoint X=119 Y=35 Z=0
    g13: GeomPoint X=121 Y=33 Z=0
    g14: LineSegment StartX=119 StartY=35 StartZ=0 EndX=114 EndY=35 EndZ=0
    g15: ArcOfCircle CenterX=105 CenterY=19 CenterZ=0 NormalX=0 NormalY=0 NormalZ=1 AngleXU=0 Radius=16 StartAngle=5.60905 EndAngle=6.28319
    g16: LineSegment StartX=121 StartY=33 StartZ=0 EndX=121 EndY=19 EndZ=0
    g17: LineSegment StartX=117.5 StartY=9.01251 StartZ=0 EndX=121.163 EndY=9.0125 EndZ=0
    g18: ArcOfCircle CenterX=105 CenterY=19 CenterZ=0 NormalX=0 NormalY=0 NormalZ=1 AngleXU=0 Radius=20.6155 StartAngle=5.7297 EndAngle=6.28319
    g19: LineSegment StartX=121.163 StartY=9.0125 StartZ=0 EndX=122.538 EndY=8.16329 EndZ=0
    g20: LineSegment StartX=124 StartY=38 StartZ=0 EndX=125.616 EndY=38 EndZ=0
    g21: LineSegment StartX=125.616 StartY=19 StartZ=0 EndX=125.616 EndY=38 EndZ=0
  constraints (50):
    c: Vertical(g0)
    c: Block(g0)
    c: Coincident(g1,g0)
    c: Block(g1)
    c: Coincident(g2,g1)
    c: Block(g2)
    c: Coincident(g3,g2)
    c: Horizontal(g3)
    c: Tangent(g3,g2)
    c: Coincident(g4,g0)
    c: Distance(g4) = 3
    c: Vertical(g4)
    c: Coincident(g5,g4)
    c: Horizontal(g5)
    c: Coincident(g6,g2)
    c: Coincident(g6,g5)
    c: Vertical(g6)
    c: Horizontal(g7)
    c: Distance(g7) = 105
    c: Coincident(g7,g1)
    c: Block(g3)
    c: Weight(g8) = 1
    c: Equal(g8,g9)
    c: Equal(g8,g10)
    c: InternalAlignment(g8,g11)
    c: InternalAlignment(g9,g11)
    c: InternalAlignment(g10,g11)
    c: InternalAlignment(g12,g11)
    c: InternalAlignment(g13,g11)
    c: Block(g11)
    c: Coincident(g14,g11)
    c: Coincident(g14,g3)
    c: Horizontal(g14)
    c: Block(g15)
    c: Coincident(g16,g11)
    c: Coincident(g16,g15)
    c: Vertical(g16)
    c: Distance(g16) = 14
    c: Coincident(g17,g15)
    c: Block(g18)
    c: Coincident(g19,g18)
    c: Coincident(g20,g7)
    c: Horizontal(g20)
    c: Vertical(g21)
    c: Coincident(g20,g21)
    c: Block(g20)
    c: Block(g21)
    c: Block(g19)
    c: Block(g17)
    c: Distance(g20) = 1.61553
FEATURE [Part::Extrusion] Extrude044
  Base = -> Sketch053
  Dir = (0,0,1)
  DirMode = 2
  FaceMakerClass = Part::FaceMakerBullseye
  LengthFwd = 72
  LengthRev = 0
  Solid = true
  Symmetric = false
FEATURE [Part::Fillet] Fillet036  label="top018"
  Base = -> Extrude044
  Edges = 1 edges r=2: [Edge41]
FEATURE [Sketcher::SketchObject] Sketch054
  FullyConstrained = false
  Placement = pos=(0,0,0) rot=(1,0,0;1.5708rad)
  sketch-geometry (24):
    g0: ArcOfCircle CenterX=-4 CenterY=-10.5 CenterZ=0 NormalX=0 NormalY=0 NormalZ=1 AngleXU=0 Radius=1.5 StartAngle=6e-16 EndAngle=3.14159
    g1: ArcOfCircle CenterX=-34.2 CenterY=-10.5 CenterZ=0 NormalX=0 NormalY=0 NormalZ=1 AngleXU=0 Radius=1.5 StartAngle=0 EndAngle=3.14159
    g2: ArcOfCircle CenterX=-34.2 CenterY=-27.7 CenterZ=0 NormalX=0 NormalY=0 NormalZ=1 AngleXU=0 Radius=1.5 StartAngle=3.14159 EndAngle=6.28319
    g3: ArcOfCircle CenterX=-4 CenterY=-27.7 CenterZ=0 NormalX=0 NormalY=0 NormalZ=1 AngleXU=0 Radius=1.5 StartAngle=3.1416 EndAngle=6.28319
    g4: ArcOfCircle CenterX=-10 CenterY=-4.3 CenterZ=0 NormalX=0 NormalY=0 NormalZ=1 AngleXU=0 Radius=1.5 StartAngle=2e-16 EndAngle=3.14159
    g5: ArcOfCircle CenterX=-16.1 CenterY=-1.8 CenterZ=0 NormalX=0 NormalY=0 NormalZ=1 AngleXU=0 Radius=1.5 StartAngle=5e-16 EndAngle=3.14159
    g6: ArcOfCircle CenterX=-22.1 CenterY=-1.8 CenterZ=0 NormalX=0 NormalY=0 NormalZ=1 AngleXU=0 Radius=1.5 StartAngle=5e-16 EndAngle=3.14159
    g7: ArcOfCircle CenterX=-28.2 CenterY=-4.3 CenterZ=0 NormalX=0 NormalY=0 NormalZ=1 AngleXU=0 Radius=1.5 StartAngle=2e-16 EndAngle=3.14159
    g8: ArcOfCircle CenterX=-10 CenterY=-33.9 CenterZ=0 NormalX=0 NormalY=0 NormalZ=1 AngleXU=0 Radius=1.5 StartAngle=3.14159 EndAngle=6.28319
    g9: ArcOfCircle CenterX=-16.1 CenterY=-36.4 CenterZ=0 NormalX=0 NormalY=0 NormalZ=1 AngleXU=0 Radius=1.5 StartAngle=3.14159 EndAngle=6.28319
    g10: ArcOfCircle CenterX=-22.1 CenterY=-36.4 CenterZ=0 NormalX=0 NormalY=0 NormalZ=1 AngleXU=0 Radius=1.5 StartAngle=3.14159 EndAngle=6.28319
    g11: ArcOfCircle CenterX=-28.2 CenterY=-33.9 CenterZ=0 NormalX=0 NormalY=0 NormalZ=1 AngleXU=0 Radius=1.5 StartAngle=3.14159 EndAngle=6.28319
    g12: LineSegment StartX=-35.7 StartY=-10.5 StartZ=0 EndX=-35.7 EndY=-27.7 EndZ=0
    g13: LineSegment StartX=-32.7 StartY=-10.5 StartZ=0 EndX=-32.7 EndY=-27.7 EndZ=0
    g14: LineSegment StartX=-29.7 StartY=-33.9 StartZ=0 EndX=-29.7 EndY=-4.3 EndZ=0
    g15: LineSegment StartX=-26.7 StartY=-33.9 StartZ=0 EndX=-26.7 EndY=-4.3 EndZ=0
    g16: LineSegment StartX=-2.5 StartY=-10.5 StartZ=0 EndX=-2.5 EndY=-27.7 EndZ=0
    g17: LineSegment StartX=-8.5 StartY=-4.3 StartZ=0 EndX=-8.5 EndY=-33.9 EndZ=0
    g18: LineSegment StartX=-5.5 StartY=-10.5 StartZ=0 EndX=-5.5 EndY=-27.7 EndZ=0
    g19: LineSegment StartX=-11.5 StartY=-4.3 StartZ=0 EndX=-11.5 EndY=-33.9 EndZ=0
    g20: LineSegment StartX=-14.6 StartY=-1.8 StartZ=0 EndX=-14.6 EndY=-36.4 EndZ=0
    g21: LineSegment StartX=-17.6 StartY=-1.8 StartZ=0 EndX=-17.6 EndY=-36.4 EndZ=0
    g22: LineSegment StartX=-20.6 StartY=-36.4 StartZ=0 EndX=-20.6 EndY=-1.8 EndZ=0
    g23: LineSegment StartX=-23.6 StartY=-1.8 StartZ=0 EndX=-23.6 EndY=-36.4 EndZ=0
  constraints (48):
    c: Block(g0)
    c: Block(g1)
    c: Block(g2)
    c: Block(g3)
    c: Block(g4)
    c: Block(g5)
    c: Block(g6)
    c: Block(g7)
    c: Block(g8)
    c: Block(g9)
    c: Block(g10)
    c: Block(g11)
    c: Coincident(g12,g1)
    c: Coincident(g12,g2)
    c: Vertical(g12)
    c: Coincident(g13,g1)
    c: Coincident(g13,g2)
    c: Vertical(g13)
    c: Coincident(g14,g11)
    c: Coincident(g14,g7)
    c: Vertical(g14)
    c: Coincident(g15,g11)
    c: Coincident(g15,g7)
    c: Vertical(g15)
    c: Coincident(g16,g0)
    c: Coincident(g16,g3)
    c: Vertical(g16)
    c: Coincident(g17,g4)
    c: Coincident(g17,g8)
    c: Vertical(g17)
    c: Coincident(g18,g0)
    c: Coincident(g18,g3)
    c: Vertical(g18)
    c: Coincident(g19,g4)
    c: Coincident(g19,g8)
    c: Vertical(g19)
    c: Coincident(g20,g5)
    c: Coincident(g20,g9)
    c: Vertical(g20)
    c: Coincident(g21,g5)
    c: Coincident(g21,g9)
    c: Vertical(g21)
    c: Coincident(g22,g10)
    c: Coincident(g22,g6)
    c: Vertical(g22)
    c: Coincident(g23,g6)
    c: Coincident(g23,g10)
    c: Vertical(g23)
FEATURE [Part::Extrusion] Extrude045  label="removeToCreateFanGrillHoles003"
  Base = -> Sketch054
  Dir = (0,-1,6e-16)
  DirMode = 2
  FaceMakerClass = Part::FaceMakerBullseye
  LengthFwd = 10
  LengthRev = 0
  Placement = pos=(65.4,44,54.82) rot=(0,0,1;0rad)
  Solid = true
  Symmetric = false
FEATURE [Part::Feature] Face105 .. Face108  x4 (patterned run collapsed; names and placements below)
  shape: bbox 3.5 x 17.8 x 2e-07 mm, 1 faces, 0 solids (baked)
FEATURE [Part::Revolution] Revolve113  label="removeToCreateScrewAndThreadedInsertHole041"
  Angle = 360
  Axis = (0,1,0)
  Base = (0,0,0)
  FaceMakerClass = Part::FaceMakerBullseye
  Placement = pos=(62.3,30.3,19.7) rot=(0,0,1;0rad)
  Solid = false
  Source = -> Face105
  Symmetric = false
FEATURE [Part::Revolution] Revolve114  label="removeToCreateScrewAndThreadedInsertHole042"
  Angle = 360
  Axis = (0,1,0)
  Base = (0,0,0)
  FaceMakerClass = Part::FaceMakerBullseye
  Placement = pos=(62.3,30.3,51.7) rot=(0,0,1;0rad)
  Solid = false
  Source = -> Face106
  Symmetric = false
FEATURE [Part::Revolution] Revolve115  label="removeToCreateScrewAndThreadedInsertHole043"
  Angle = 360
  Axis = (0,1,0)
  Base = (0,0,0)
  FaceMakerClass = Part::FaceMakerBullseye
  Placement = pos=(30.3,30.3,19.7) rot=(0,0,1;0rad)
  Solid = false
  Source = -> Face107
  Symmetric = false
FEATURE [Part::Revolution] Revolve116  label="removeToCreateScrewAndThreadedInsertHole044"
  Angle = 360
  Axis = (0,1,0)
  Base = (0,0,0)
  FaceMakerClass = Part::FaceMakerBullseye
  Placement = pos=(30.3,30.3,51.7) rot=(0,0,1;0rad)
  Solid = false
  Source = -> Face108
  Symmetric = false
FEATURE [Part::MultiFuse] Fusion083  label="createThreadedInsertHolesForFan004"
  Shapes = -> [Revolve113,Revolve114,Revolve115,Revolve116]
FEATURE [Part::Box] Box024  label="removeToCreteHoleForPlugHousing026"
  AttacherType = Attacher::AttachEngine3D
  Height = 28.6
  Length = 10
  Placement = pos=(-2,0,21.7) rot=(0,0,1;0rad)
  Width = 19
FEATURE [Part::Cylinder] Cylinder038  label="removeToCreteHoleForPlugHousing027"
  Angle = 360
  AttacherType = Attacher::AttachEngine3D
  Height = 20
  Placement = pos=(-2,19,36) rot=(0,1,0;1.5708rad)
  Radius = 14.3
FEATURE [Part::MultiFuse] Fusion084  label="removeToCreteHoleForPlugHousing028"
  Shapes = -> [Box024,Cylinder038]
FEATURE [Part::Cylinder] Cylinder039
  Angle = 360
  AttacherType = Attacher::AttachEngine3D
  Height = 20
  Placement = pos=(0,0,36.15) rot=(0,0,1;0rad)
  Radius = 14.3
FEATURE [Part::Cylinder] Cylinder040
  Angle = 360
  AttacherType = Attacher::AttachEngine3D
  Height = 10
  Placement = pos=(0,0,36.15) rot=(0,0,1;0rad)
  Radius = 4
FEATURE [Part::Box] Box025  label="removeToCreteHoleForPlugHousing030"
  AttacherType = Attacher::AttachEngine3D
  Height = 28.6
  Length = 20
  Placement = pos=(106.15,0,21.7) rot=(0,0,1;0rad)
  Width = 19
FEATURE [Part::MultiFuse] Fusion086  label="removeToCreteHoleForPlugHousing031"
  Placement = pos=(70,19,36) rot=(0,1,0;1.5708rad)
  Shapes = -> [Cylinder039,Cylinder040]
FEATURE [Part::MultiFuse] Fusion085  label="removeToCreteHoleForPlugHousing029"
  Shapes = -> [Box025,Fusion086]
FEATURE [Sketcher::SketchObject] Sketch055
  FullyConstrained = true
  Placement = pos=(117,19,0) rot=(0.57735,0.57735,0.57735;2.0944rad)
  sketch-geometry (48):
    g0: LineSegment StartX=-49.19 StartY=69.25 StartZ=0 EndX=-49.19 EndY=66.25 EndZ=0
    g1: LineSegment StartX=-49.19 StartY=63.5 StartZ=0 EndX=-49.19 EndY=60.5 EndZ=0
    g2: LineSegment StartX=-49.19 StartY=57.75 StartZ=0 EndX=-49.19 EndY=54.75 EndZ=0
    g3: LineSegment StartX=-49.19 StartY=52 StartZ=0 EndX=-49.19 EndY=49 EndZ=0
    g4: LineSegment StartX=-49.19 StartY=46.25 StartZ=0 EndX=-49.19 EndY=43.25 EndZ=0
    g5: LineSegment StartX=-49.19 StartY=40.5 StartZ=0 EndX=-49.19 EndY=37.5 EndZ=0
    g6: LineSegment StartX=-49.19 StartY=34.5 StartZ=0 EndX=-49.19 EndY=31.5 EndZ=0
    g7: LineSegment StartX=-49.19 StartY=28.75 StartZ=0 EndX=-49.19 EndY=25.75 EndZ=0
    g8: LineSegment StartX=-49.19 StartY=23 StartZ=0 EndX=-49.19 EndY=20 EndZ=0
    g9: LineSegment StartX=-49.19 StartY=17.25 StartZ=0 EndX=-49.19 EndY=14.25 EndZ=0
    g10: LineSegment StartX=-49.19 StartY=11.5 StartZ=0 EndX=-49.19 EndY=8.5 EndZ=0
    g11: LineSegment StartX=-49.19 StartY=5.75 StartZ=0 EndX=-49.19 EndY=2.75 EndZ=0
    g12: ArcOfCircle CenterX=-1.5 CenterY=67.75 CenterZ=0 NormalX=0 NormalY=0 NormalZ=1 AngleXU=0 Radius=1.5 StartAngle=4.71239 EndAngle=7.85398
    g13: ArcOfCircle CenterX=-1.5 CenterY=62 CenterZ=0 NormalX=0 NormalY=0 NormalZ=1 AngleXU=0 Radius=1.5 StartAngle=4.71239 EndAngle=7.85398
    g14: ArcOfCircle CenterX=-1.5 CenterY=56.25 CenterZ=0 NormalX=0 NormalY=0 NormalZ=1 AngleXU=0 Radius=1.5 StartAngle=4.71239 EndAngle=7.85398
    g15: ArcOfCircle CenterX=-11.49 CenterY=50.5 CenterZ=0 NormalX=0 NormalY=0 NormalZ=1 AngleXU=0 Radius=1.5 StartAngle=4.71239 EndAngle=7.85398
    g16: ArcOfCircle CenterX=-16.28 CenterY=44.75 CenterZ=0 NormalX=0 NormalY=0 NormalZ=1 AngleXU=0 Radius=1.5 StartAngle=4.71239 EndAngle=7.85398
    g17: ArcOfCircle CenterX=-18.2337 CenterY=39 CenterZ=0 NormalX=0 NormalY=0 NormalZ=1 AngleXU=0 Radius=1.5 StartAngle=4.71485 EndAngle=7.85398
    g18: ArcOfCircle CenterX=-16.2837 CenterY=27.25 CenterZ=0 NormalX=0 NormalY=0 NormalZ=1 AngleXU=0 Radius=1.5 StartAngle=4.71485 EndAngle=7.85398
    g19: ArcOfCircle CenterX=-18.2337 CenterY=33 CenterZ=0 NormalX=0 NormalY=0 NormalZ=1 AngleXU=0 Radius=1.5 StartAngle=4.71485 EndAngle=7.85398
    g20: ArcOfCircle CenterX=-11.49 CenterY=21.5 CenterZ=0 NormalX=0 NormalY=0 NormalZ=1 AngleXU=0 Radius=1.5 StartAngle=4.71239 EndAngle=7.85398
    g21: ArcOfCircle CenterX=-1.5 CenterY=4.25 CenterZ=0 NormalX=0 NormalY=0 NormalZ=1 AngleXU=0 Radius=1.5 StartAngle=4.71239 EndAngle=7.85398
    g22: ArcOfCircle CenterX=-1.5 CenterY=10 CenterZ=0 NormalX=0 NormalY=0 NormalZ=1 AngleXU=0 Radius=1.5 StartAngle=4.71239 EndAngle=7.85398
    g23: ArcOfCircle CenterX=-1.5 CenterY=15.75 CenterZ=0 NormalX=0 NormalY=0 NormalZ=1 AngleXU=0 Radius=1.5 StartAngle=4.71239 EndAngle=7.85398
    g24: LineSegment StartX=-49.19 StartY=69.25 StartZ=0 EndX=-1.5 EndY=69.25 EndZ=0
    g25: LineSegment StartX=-49.19 StartY=66.25 StartZ=0 EndX=-1.5 EndY=66.25 EndZ=0
    g26: LineSegment StartX=-49.19 StartY=63.5 StartZ=0 EndX=-1.5 EndY=63.5 EndZ=0
    g27: LineSegment StartX=-49.19 StartY=60.5 StartZ=0 EndX=-1.5 EndY=60.5 EndZ=0
    g28: LineSegment StartX=-49.19 StartY=57.75 StartZ=0 EndX=-1.5 EndY=57.75 EndZ=0
    g29: LineSegment StartX=-49.19 StartY=54.75 StartZ=0 EndX=-1.5 EndY=54.75 EndZ=0
    g30: LineSegment StartX=-49.19 StartY=52 StartZ=0 EndX=-11.49 EndY=52 EndZ=0
    g31: LineSegment StartX=-49.19 StartY=49 StartZ=0 EndX=-11.49 EndY=49 EndZ=0
    g32: LineSegment StartX=-49.19 StartY=46.25 StartZ=0 EndX=-16.28 EndY=46.25 EndZ=0
    g33: LineSegment StartX=-49.19 StartY=43.25 StartZ=0 EndX=-16.28 EndY=43.25 EndZ=0
    g34: LineSegment StartX=-49.19 StartY=40.5 StartZ=0 EndX=-18.2337 EndY=40.5 EndZ=0
    g35: LineSegment StartX=-49.19 StartY=37.5 StartZ=0 EndX=-18.23 EndY=37.5 EndZ=0
    g36: LineSegment StartX=-49.19 StartY=34.5 StartZ=0 EndX=-18.2337 EndY=34.5 EndZ=0
    g37: LineSegment StartX=-49.19 StartY=31.5 StartZ=0 EndX=-18.23 EndY=31.5 EndZ=0
    g38: LineSegment StartX=-49.19 StartY=28.75 StartZ=0 EndX=-16.2837 EndY=28.75 EndZ=0
    g39: LineSegment StartX=-49.19 StartY=25.75 StartZ=0 EndX=-16.28 EndY=25.75 EndZ=0
    g40: LineSegment StartX=-49.19 StartY=23 StartZ=0 EndX=-11.49 EndY=23 EndZ=0
    g41: LineSegment StartX=-49.19 StartY=20 StartZ=0 EndX=-11.49 EndY=20 EndZ=0
    g42: LineSegment StartX=-49.19 StartY=17.25 StartZ=0 EndX=-1.5 EndY=17.25 EndZ=0
    g43: LineSegment StartX=-49.19 StartY=14.25 StartZ=0 EndX=-1.5 EndY=14.25 EndZ=0
    g44: LineSegment StartX=-49.19 StartY=11.5 StartZ=0 EndX=-1.5 EndY=11.5 EndZ=0
    g45: LineSegment StartX=-49.19 StartY=8.5 StartZ=0 EndX=-1.5 EndY=8.5 EndZ=0
    g46: LineSegment StartX=-49.19 StartY=5.75 StartZ=0 EndX=-1.5 EndY=5.75 EndZ=0
    g47: LineSegment StartX=-49.19 StartY=2.75 StartZ=0 EndX=-1.5 EndY=2.75 EndZ=0
  constraints (120):
    c: Vertical(g0)
    c: Distance(g0) = 3
    c: Block(g0)
    c: Vertical(g1)
    c: Distance(g1) = 3
    c: Vertical(g2)
    c: Equal(g0,g2) = 3
    c: Block(g2)
    c: Vertical(g3)
    c: Equal(g1,g3) = 3
    c: Vertical(g4)
    c: Equal(g0,g4) = 3
    c: Block(g4)
    c: Vertical(g5)
    c: Equal(g1,g5) = 3
    c: Vertical(g6)
    c: Equal(g0,g6) = 3
    c: Block(g6)
    c: Vertical(g7)
    c: Equal(g1,g7) = 3
    c: Vertical(g8)
    c: Equal(g0,g8) = 3
    c: Block(g8)
    c: Vertical(g9)
    c: Equal(g1,g9) = 3
    c: Vertical(g10)
    c: Equal(g0,g10) = 3
    c: Block(g10)
    c: Vertical(g11)
    c: Equal(g1,g11) = 3
    c: Block(g12)
    c: Block(g13)
    c: Block(g14)
    c: Block(g15)
    c: Block(g16)
    c: Block(g17)
    c: Block(g18)
    c: Block(g19)
    c: Block(g20)
    c: Block(g21)
    c: Block(g22)
    c: Block(g23)
    c: Block(g11)
    c: Block(g9)
    c: Block(g7)
    c: Block(g5)
    c: Block(g3)
    c: Block(g1)
    c: Coincident(g24,g0)
    c: Coincident(g24,g12)
    c: Horizontal(g24)
    c: Coincident(g25,g0)
    c: Coincident(g25,g12)
    c: Horizontal(g25)
    c: Coincident(g26,g1)
    c: Coincident(g26,g13)
    c: Horizontal(g26)
    c: Coincident(g27,g1)
    c: Coincident(g27,g13)
    c: Horizontal(g27)
    c: Coincident(g28,g2)
    c: Coincident(g28,g14)
    c: Horizontal(g28)
    c: Coincident(g29,g2)
    c: Coincident(g29,g14)
    c: Horizontal(g29)
    c: Coincident(g30,g3)
    c: Coincident(g30,g15)
    c: Horizontal(g30)
    c: Coincident(g31,g3)
    c: Coincident(g31,g15)
    c: Horizontal(g31)
    c: Coincident(g32,g4)
    c: Coincident(g32,g16)
    c: Horizontal(g32)
    c: Coincident(g33,g4)
    c: Coincident(g33,g16)
    c: Horizontal(g33)
    c: Coincident(g34,g5)
    c: Coincident(g34,g17)
    c: Horizontal(g34)
    c: Coincident(g35,g5)
    c: Coincident(g35,g17)
    c: Horizontal(g35)
    c: Coincident(g36,g6)
    c: Coincident(g36,g19)
    c: Horizontal(g36)
    c: Coincident(g37,g6)
    c: Coincident(g37,g19)
    c: Horizontal(g37)
    c: Coincident(g38,g7)
    c: Coincident(g38,g18)
    c: Horizontal(g38)
    c: Coincident(g39,g7)
    c: Coincident(g39,g18)
    c: Horizontal(g39)
    c: Coincident(g40,g8)
    c: Coincident(g40,g20)
    c: Horizontal(g40)
    c: Coincident(g41,g8)
    c: Coincident(g41,g20)
    c: Horizontal(g41)
    c: Coincident(g42,g9)
    c: Coincident(g42,g23)
    c: Horizontal(g42)
    c: Coincident(g43,g9)
    c: Coincident(g43,g23)
    c: Horizontal(g43)
    c: Coincident(g44,g10)
    c: Coincident(g44,g22)
    c: Horizontal(g44)
    c: Coincident(g45,g10)
    c: Coincident(g45,g22)
    c: Horizontal(g45)
    c: Coincident(g46,g11)
    c: Coincident(g46,g21)
    c: Horizontal(g46)
    c: Coincident(g47,g11)
    c: Coincident(g47,g21)
    c: Horizontal(g47)
FEATURE [Part::Extrusion] Extrude046
  Base = -> Sketch055
  Dir = (1,0,0)
  DirMode = 2
  FaceMakerClass = Part::FaceMakerBullseye
  LengthFwd = 23
  LengthRev = 0
  Placement = pos=(-19,0,0) rot=(0,0,1;0rad)
  Solid = true
  Symmetric = false
FEATURE [Part::Fillet] Fillet038  label="removeToCreateVentalationHoles001"
  Base = -> Extrude046
  Edges = <same value as first occurrence — deduplicated (x6 in doc)>
  Placement = pos=(7,0,0) rot=(0,0,1;0rad)
FEATURE [Sketcher::SketchObject] Sketch056  label="topSketch014"
  FullyConstrained = true
  sketch-geometry (22):
    g0: LineSegment StartX=5.21097e-06 StartY=3 StartZ=0 EndX=5.21097e-06 EndY=19 EndZ=0
    g1: ArcOfCircle CenterX=19 CenterY=19 CenterZ=0 NormalX=0 NormalY=0 NormalZ=1 AngleXU=0 Radius=19 StartAngle=1.5708 EndAngle=3.14159
    g2: ArcOfCircle CenterX=19 CenterY=19 CenterZ=0 NormalX=0 NormalY=0 NormalZ=1 AngleXU=0 Radius=16 StartAngle=1.5708 EndAngle=3.14159
    g3: LineSegment StartX=114 StartY=35 StartZ=0 EndX=19 EndY=35 EndZ=0
    g4: LineSegment StartX=5.21097e-06 StartY=3 StartZ=0 EndX=5.21097e-06 EndY=0 EndZ=0
    g5: LineSegment StartX=3 StartY=0 StartZ=0 EndX=5.21097e-06 EndY=0 EndZ=0
    g6: LineSegment StartX=3 StartY=19 StartZ=0 EndX=3 EndY=0 EndZ=0
    g7: LineSegment StartX=19 StartY=38 StartZ=0 EndX=124 EndY=38 EndZ=0
    g8: Circle CenterX=119 CenterY=35 CenterZ=0 NormalX=0 NormalY=0 NormalZ=1 AngleXU=0 Radius=1
    g9: Circle CenterX=121 CenterY=35 CenterZ=0 NormalX=0 NormalY=0 NormalZ=1 AngleXU=0 Radius=1
    g10: Circle CenterX=121 CenterY=33 CenterZ=0 NormalX=0 NormalY=0 NormalZ=1 AngleXU=0 Radius=1
    g11: BSplineCurve PolesCount=3 KnotsCount=2 Degree=2 IsPeriodic=0
    g12: GeomPoint X=119 Y=35 Z=0
    g13: GeomPoint X=121 Y=33 Z=0
    g14: LineSegment StartX=119 StartY=35 StartZ=0 EndX=114 EndY=35 EndZ=0
    g15: ArcOfCircle CenterX=105 CenterY=19 CenterZ=0 NormalX=0 NormalY=0 NormalZ=1 AngleXU=0 Radius=16 StartAngle=5.60905 EndAngle=6.28319
    g16: LineSegment StartX=121 StartY=33 StartZ=0 EndX=121 EndY=19 EndZ=0
    g17: LineSegment StartX=117.5 StartY=9.01251 StartZ=0 EndX=121.163 EndY=9.0125 EndZ=0
    g18: ArcOfCircle CenterX=105 CenterY=19 CenterZ=0 NormalX=0 NormalY=0 NormalZ=1 AngleXU=0 Radius=20.6155 StartAngle=5.7297 EndAngle=6.28319
    g19: LineSegment StartX=121.163 StartY=9.0125 StartZ=0 EndX=122.538 EndY=8.16329 EndZ=0
    g20: LineSegment StartX=124 StartY=38 StartZ=0 EndX=125.616 EndY=38 EndZ=0
    g21: LineSegment StartX=125.616 StartY=19 StartZ=0 EndX=125.616 EndY=38 EndZ=0
  constraints (49):
    c: Vertical(g0)
    c: Block(g0)
    c: Coincident(g1,g0)
    c: Block(g1)
    c: Coincident(g2,g1)
    c: Block(g2)
    c: Coincident(g3,g2)
    c: Horizontal(g3)
    c: Tangent(g3,g2)
    c: Coincident(g4,g0)
    c: Distance(g4) = 3
    c: Vertical(g4)
    c: Coincident(g5,g4)
    c: Horizontal(g5)
    c: Coincident(g6,g2)
    c: Coincident(g6,g5)
    c: Vertical(g6)
    c: Horizontal(g7)
    c: Distance(g7) = 105
    c: Coincident(g7,g1)
    c: Block(g3)
    c: Weight(g8) = 1
    c: Equal(g8,g9)
    c: Equal(g8,g10)
    c: InternalAlignment(g8,g11)
    c: InternalAlignment(g9,g11)
    c: InternalAlignment(g10,g11)
    c: InternalAlignment(g12,g11)
    c: InternalAlignment(g13,g11)
    c: Block(g11)
    c: Coincident(g14,g11)
    c: Coincident(g14,g3)
    c: Horizontal(g14)
    c: Block(g15)
    c: Coincident(g16,g11)
    c: Coincident(g16,g15)
    c: Vertical(g16)
    c: Distance(g16) = 14
    c: Coincident(g17,g15)
    c: Block(g18)
    c: Coincident(g19,g18)
    c: Coincident(g20,g7)
    c: Horizontal(g20)
    c: Vertical(g21)
    c: Coincident(g20,g21)
    c: Block(g20)
    c: Block(g21)
    c: Block(g19)
    c: Block(g17)
FEATURE [Part::Box] Box026  label="removeToCreteHoleForPlugHousing032"
  AttacherType = Attacher::AttachEngine3D
  Height = 28.6
  Length = 10
  Placement = pos=(-2,0,21.7) rot=(0,0,1;0rad)
  Width = 19
FEATURE [Part::Feature] Face109 .. Face112  x4 (patterned run collapsed; names and placements below)
  shape: bbox 3.5 x 17.8 x 2e-07 mm, 1 faces, 0 solids (baked)
FEATURE [Part::Revolution] Revolve117  label="removeToCreateScrewAndThreadedInsertHole045"
  Angle = 360
  Axis = (0,1,0)
  Base = (0,0,0)
  FaceMakerClass = Part::FaceMakerBullseye
  Placement = pos=(62.3,30.3,19.7) rot=(0,0,1;0rad)
  Solid = false
  Source = -> Face109
  Symmetric = false
FEATURE [Part::Revolution] Revolve118  label="removeToCreateScrewAndThreadedInsertHole046"
  Angle = 360
  Axis = (0,1,0)
  Base = (0,0,0)
  FaceMakerClass = Part::FaceMakerBullseye
  Placement = pos=(62.3,30.3,51.7) rot=(0,0,1;0rad)
  Solid = false
  Source = -> Face110
  Symmetric = false
FEATURE [Part::Revolution] Revolve119  label="removeToCreateScrewAndThreadedInsertHole047"
  Angle = 360
  Axis = (0,1,0)
  Base = (0,0,0)
  FaceMakerClass = Part::FaceMakerBullseye
  Placement = pos=(30.3,30.3,19.7) rot=(0,0,1;0rad)
  Solid = false
  Source = -> Face111
  Symmetric = false
FEATURE [Part::Revolution] Revolve120  label="removeToCreateScrewAndThreadedInsertHole048"
  Angle = 360
  Axis = (0,1,0)
  Base = (0,0,0)
  FaceMakerClass = Part::FaceMakerBullseye
  Placement = pos=(30.3,30.3,51.7) rot=(0,0,1;0rad)
  Solid = false
  Source = -> Face112
  Symmetric = false
FEATURE [Part::MultiFuse] Fusion087  label="createThreadedInsertHolesForFan005"
  Shapes = -> [Revolve117,Revolve118,Revolve119,Revolve120]
FEATURE [Part::Extrusion] Extrude047
  Base = -> Sketch056
  Dir = (0,0,1)
  DirMode = 2
  FaceMakerClass = Part::FaceMakerBullseye
  LengthFwd = 72
  LengthRev = 0
  Solid = true
  Symmetric = false
FEATURE [Part::Fillet] Fillet039  label="top019"
  Base = -> Extrude047
  Edges = 1 edges r=2: [Edge35]
FEATURE [Sketcher::SketchObject] Sketch057
  FullyConstrained = false
  Placement = pos=(0,0,0) rot=(1,0,0;1.5708rad)
  sketch-geometry (24):
    g0: ArcOfCircle CenterX=-4 CenterY=-10.5 CenterZ=0 NormalX=0 NormalY=0 NormalZ=1 AngleXU=0 Radius=1.5 StartAngle=6e-16 EndAngle=3.14159
    g1: ArcOfCircle CenterX=-34.2 CenterY=-10.5 CenterZ=0 NormalX=0 NormalY=0 NormalZ=1 AngleXU=0 Radius=1.5 StartAngle=0 EndAngle=3.14159
    g2: ArcOfCircle CenterX=-34.2 CenterY=-27.7 CenterZ=0 NormalX=0 NormalY=0 NormalZ=1 AngleXU=0 Radius=1.5 StartAngle=3.14159 EndAngle=6.28319
    g3: ArcOfCircle CenterX=-4 CenterY=-27.7 CenterZ=0 NormalX=0 NormalY=0 NormalZ=1 AngleXU=0 Radius=1.5 StartAngle=3.1416 EndAngle=6.28319
    g4: ArcOfCircle CenterX=-10 CenterY=-4.3 CenterZ=0 NormalX=0 NormalY=0 NormalZ=1 AngleXU=0 Radius=1.5 StartAngle=2e-16 EndAngle=3.14159
    g5: ArcOfCircle CenterX=-16.1 CenterY=-1.8 CenterZ=0 NormalX=0 NormalY=0 NormalZ=1 AngleXU=0 Radius=1.5 StartAngle=5e-16 EndAngle=3.14159
    g6: ArcOfCircle CenterX=-22.1 CenterY=-1.8 CenterZ=0 NormalX=0 NormalY=0 NormalZ=1 AngleXU=0 Radius=1.5 StartAngle=5e-16 EndAngle=3.14159
    g7: ArcOfCircle CenterX=-28.2 CenterY=-4.3 CenterZ=0 NormalX=0 NormalY=0 NormalZ=1 AngleXU=0 Radius=1.5 StartAngle=2e-16 EndAngle=3.14159
    g8: ArcOfCircle CenterX=-10 CenterY=-33.9 CenterZ=0 NormalX=0 NormalY=0 NormalZ=1 AngleXU=0 Radius=1.5 StartAngle=3.14159 EndAngle=6.28319
    g9: ArcOfCircle CenterX=-16.1 CenterY=-36.4 CenterZ=0 NormalX=0 NormalY=0 NormalZ=1 AngleXU=0 Radius=1.5 StartAngle=3.14159 EndAngle=6.28319
    g10: ArcOfCircle CenterX=-22.1 CenterY=-36.4 CenterZ=0 NormalX=0 NormalY=0 NormalZ=1 AngleXU=0 Radius=1.5 StartAngle=3.14159 EndAngle=6.28319
    g11: ArcOfCircle CenterX=-28.2 CenterY=-33.9 CenterZ=0 NormalX=0 NormalY=0 NormalZ=1 AngleXU=0 Radius=1.5 StartAngle=3.14159 EndAngle=6.28319
    g12: LineSegment StartX=-35.7 StartY=-10.5 StartZ=0 EndX=-35.7 EndY=-27.7 EndZ=0
    g13: LineSegment StartX=-32.7 StartY=-10.5 StartZ=0 EndX=-32.7 EndY=-27.7 EndZ=0
    g14: LineSegment StartX=-29.7 StartY=-33.9 StartZ=0 EndX=-29.7 EndY=-4.3 EndZ=0
    g15: LineSegment StartX=-26.7 StartY=-33.9 StartZ=0 EndX=-26.7 EndY=-4.3 EndZ=0
    g16: LineSegment StartX=-2.5 StartY=-10.5 StartZ=0 EndX=-2.5 EndY=-27.7 EndZ=0
    g17: LineSegment StartX=-8.5 StartY=-4.3 StartZ=0 EndX=-8.5 EndY=-33.9 EndZ=0
    g18: LineSegment StartX=-5.5 StartY=-10.5 StartZ=0 EndX=-5.5 EndY=-27.7 EndZ=0
    g19: LineSegment StartX=-11.5 StartY=-4.3 StartZ=0 EndX=-11.5 EndY=-33.9 EndZ=0
    g20: LineSegment StartX=-14.6 StartY=-1.8 StartZ=0 EndX=-14.6 EndY=-36.4 EndZ=0
    g21: LineSegment StartX=-17.6 StartY=-1.8 StartZ=0 EndX=-17.6 EndY=-36.4 EndZ=0
    g22: LineSegment StartX=-20.6 StartY=-36.4 StartZ=0 EndX=-20.6 EndY=-1.8 EndZ=0
    g23: LineSegment StartX=-23.6 StartY=-1.8 StartZ=0 EndX=-23.6 EndY=-36.4 EndZ=0
  constraints (48):
    c: Block(g0)
    c: Block(g1)
    c: Block(g2)
    c: Block(g3)
    c: Block(g4)
    c: Block(g5)
    c: Block(g6)
    c: Block(g7)
    c: Block(g8)
    c: Block(g9)
    c: Block(g10)
    c: Block(g11)
    c: Coincident(g12,g1)
    c: Coincident(g12,g2)
    c: Vertical(g12)
    c: Coincident(g13,g1)
    c: Coincident(g13,g2)
    c: Vertical(g13)
    c: Coincident(g14,g11)
    c: Coincident(g14,g7)
    c: Vertical(g14)
    c: Coincident(g15,g11)
    c: Coincident(g15,g7)
    c: Vertical(g15)
    c: Coincident(g16,g0)
    c: Coincident(g16,g3)
    c: Vertical(g16)
    c: Coincident(g17,g4)
    c: Coincident(g17,g8)
    c: Vertical(g17)
    c: Coincident(g18,g0)
    c: Coincident(g18,g3)
    c: Vertical(g18)
    c: Coincident(g19,g4)
    c: Coincident(g19,g8)
    c: Vertical(g19)
    c: Coincident(g20,g5)
    c: Coincident(g20,g9)
    c: Vertical(g20)
    c: Coincident(g21,g5)
    c: Coincident(g21,g9)
    c: Vertical(g21)
    c: Coincident(g22,g10)
    c: Coincident(g22,g6)
    c: Vertical(g22)
    c: Coincident(g23,g6)
    c: Coincident(g23,g10)
    c: Vertical(g23)
FEATURE [Part::Extrusion] Extrude048  label="removeToCreateFanGrillHoles004"
  Base = -> Sketch057
  Dir = (0,-1,6e-16)
  DirMode = 2
  FaceMakerClass = Part::FaceMakerBullseye
  LengthFwd = 10
  LengthRev = 0
  Placement = pos=(65.4,44,54.82) rot=(0,0,1;0rad)
  Solid = true
  Symmetric = false
FEATURE [Part::Cut] Cut040  label="top021"
  Base = -> Fillet039
  Tool = -> Extrude048
FEATURE [Part::Cylinder] Cylinder041  label="removeToCreteHoleForPlugHousing034"
  Angle = 360
  AttacherType = Attacher::AttachEngine3D
  Height = 20
  Placement = pos=(-2,19,36) rot=(0,1,0;1.5708rad)
  Radius = 14.3
FEATURE [Part::MultiFuse] Fusion089  label="removeToCreteHoleForPlugHousing035"
  Shapes = -> [Box026,Cylinder041]
FEATURE [Part::Cylinder] Cylinder042
  Angle = 360
  AttacherType = Attacher::AttachEngine3D
  Height = 20
  Placement = pos=(0,0,36.15) rot=(0,0,1;0rad)
  Radius = 14.3
FEATURE [Part::Cylinder] Cylinder043
  Angle = 360
  AttacherType = Attacher::AttachEngine3D
  Height = 10
  Placement = pos=(0,0,36.15) rot=(0,0,1;0rad)
  Radius = 4
FEATURE [Part::Box] Box027  label="removeToCreteHoleForPlugHousing036"
  AttacherType = Attacher::AttachEngine3D
  Height = 28.6
  Length = 20
  Placement = pos=(106.15,0,21.7) rot=(0,0,1;0rad)
  Width = 19
FEATURE [Part::Cut] Cut041  label="top022"
  Base = -> Cut040
  Tool = -> Fusion087
FEATURE [Part::Cut] Cut039  label="top020"
  Base = -> Cut041
  Tool = -> Fusion089
FEATURE [Part::MultiFuse] Fusion090  label="removeToCreteHoleForPlugHousing037"
  Placement = pos=(70,19,36) rot=(0,1,0;1.5708rad)
  Shapes = -> [Cylinder042,Cylinder043]
FEATURE [Part::MultiFuse] Fusion088  label="removeToCreteHoleForPlugHousing033"
  Shapes = -> [Box027,Fusion090]
FEATURE [Part::Cut] Cut042  label="removeToCreteHoleForPlugHousing038"
  Base = -> Cut039
  Tool = -> Fusion088
FEATURE [Part::MultiFuse] Fusion091  label="removeFromTop"
  Shapes = -> [Fillet038,Fusion085,Fusion084,Fusion083,Extrude045]
FEATURE [Part::Cut] Cut043  label="REAL TOP ====="
  Base = -> Fillet036
  Tool = -> Fusion091
FEATURE [Part::MultiFuse] Fusion092  label="caseScrewPillarBracket016"
  Shapes = -> [Extrude030,Extrude031,Extrude032,Extrude033,Extrude034,Extrude035,Extrude036,Extrude037,Box013,Box014]
FEATURE [Sketcher::SketchObject] Sketch058  label="topSketch015"
  FullyConstrained = true
  sketch-geometry (20):
    g0: LineSegment StartX=5.21097e-06 StartY=3 StartZ=0 EndX=5.21097e-06 EndY=19 EndZ=0
    g1: ArcOfCircle CenterX=19 CenterY=19 CenterZ=0 NormalX=0 NormalY=0 NormalZ=1 AngleXU=0 Radius=19 StartAngle=1.5708 EndAngle=3.14159
    g2: ArcOfCircle CenterX=19 CenterY=19 CenterZ=0 NormalX=0 NormalY=0 NormalZ=1 AngleXU=0 Radius=16 StartAngle=1.5708 EndAngle=3.14159
    g3: LineSegment StartX=114 StartY=35 StartZ=0 EndX=19 EndY=35 EndZ=0
    g4: LineSegment StartX=5.21097e-06 StartY=3 StartZ=0 EndX=5.21097e-06 EndY=0 EndZ=0
    g5: LineSegment StartX=3 StartY=0 StartZ=0 EndX=5.21097e-06 EndY=0 EndZ=0
    g6: LineSegment StartX=3 StartY=19 StartZ=0 EndX=3 EndY=0 EndZ=0
    g7: LineSegment StartX=19 StartY=38 StartZ=0 EndX=124 EndY=38 EndZ=0
    g8: Circle CenterX=119 CenterY=35 CenterZ=0 NormalX=0 NormalY=0 NormalZ=1 AngleXU=0 Radius=1
    g9: Circle CenterX=121 CenterY=35 CenterZ=0 NormalX=0 NormalY=0 NormalZ=1 AngleXU=0 Radius=1
    g10: Circle CenterX=121 CenterY=33 CenterZ=0 NormalX=0 NormalY=0 NormalZ=1 AngleXU=0 Radius=1
    g11: BSplineCurve PolesCount=3 KnotsCount=2 Degree=2 IsPeriodic=0
    g12: GeomPoint X=119 Y=35 Z=0
    g13: GeomPoint X=121 Y=33 Z=0
    g14: LineSegment StartX=119 StartY=35 StartZ=0 EndX=114 EndY=35 EndZ=0
    g15: ArcOfCircle CenterX=105 CenterY=19 CenterZ=0 NormalX=0 NormalY=0 NormalZ=1 AngleXU=0 Radius=19 StartAngle=5.7297 EndAngle=6.28319
    g16: ArcOfCircle CenterX=105 CenterY=19 CenterZ=0 NormalX=0 NormalY=0 NormalZ=1 AngleXU=0 Radius=16 StartAngle=5.60905 EndAngle=6.28319
    g17: LineSegment StartX=121 StartY=33 StartZ=0 EndX=121 EndY=19 EndZ=0
    g18: LineSegment StartX=124 StartY=38 StartZ=0 EndX=124 EndY=19 EndZ=0
    g19: LineSegment StartX=117.5 StartY=9.01251 StartZ=0 EndX=121.163 EndY=9.0125 EndZ=0
  constraints (46):
    c: Vertical(g0)
    c: Block(g0)
    c: Coincident(g1,g0)
    c: Block(g1)
    c: Coincident(g2,g1)
    c: Block(g2)
    c: Coincident(g3,g2)
    c: Horizontal(g3)
    c: Tangent(g3,g2)
    c: Coincident(g4,g0)
    c: Distance(g4) = 3
    c: Vertical(g4)
    c: Coincident(g5,g4)
    c: Horizontal(g5)
    c: Coincident(g6,g2)
    c: Coincident(g6,g5)
    c: Vertical(g6)
    c: Horizontal(g7)
    c: Distance(g7) = 105
    c: Coincident(g7,g1)
    c: Block(g3)
    c: Weight(g8) = 1
    c: Equal(g8,g9)
    c: Equal(g8,g10)
    c: InternalAlignment(g8,g11)
    c: InternalAlignment(g9,g11)
    c: InternalAlignment(g10,g11)
    c: InternalAlignment(g12,g11)
    c: InternalAlignment(g13,g11)
    c: Block(g11)
    c: Coincident(g14,g11)
    c: Coincident(g14,g3)
    c: Horizontal(g14)
    c: Block(g15)
    c: Coincident(g16,g15)
    c: Block(g16)
    c: Coincident(g17,g11)
    c: Coincident(g17,g16)
    c: Vertical(g17)
    c: Distance(g17) = 14
    c: Coincident(g18,g7)
    c: Coincident(g18,g15)
    c: Vertical(g18)
    c: Distance(g18) = 19
    c: Coincident(g19,g16)
    c: Coincident(g19,g15)
FEATURE [Part::Extrusion] Extrude049  label="top023"
  Base = -> Sketch058
  Dir = (0,0,1)
  DirMode = 2
  FaceMakerClass = Part::FaceMakerBullseye
  LengthFwd = 72
  LengthRev = 0
  Solid = true
  Symmetric = false
FEATURE [Sketcher::SketchObject] Sketch059
  FullyConstrained = true
  MapMode = 3
  Placement = pos=(0,0,0) rot=(1,0,0;1.5708rad)
  Support = -> [Extrude049]
  sketch-geometry (8):
    g0: Circle CenterX=80.351 CenterY=-67.6202 CenterZ=0 NormalX=0 NormalY=0 NormalZ=1 AngleXU=0 Radius=2
    g1: Circle CenterX=80.351 CenterY=-67.6202 CenterZ=0 NormalX=0 NormalY=0 NormalZ=1 AngleXU=0 Radius=3
    g2: Circle CenterX=80.351 CenterY=-4.92017 CenterZ=0 NormalX=0 NormalY=0 NormalZ=1 AngleXU=0 Radius=2
    g3: Circle CenterX=80.351 CenterY=-4.92017 CenterZ=0 NormalX=0 NormalY=0 NormalZ=1 AngleXU=0 Radius=3
    g4: Circle CenterX=23.851 CenterY=-4.92017 CenterZ=0 NormalX=0 NormalY=0 NormalZ=1 AngleXU=0 Radius=2
    g5: Circle CenterX=23.851 CenterY=-4.92017 CenterZ=0 NormalX=0 NormalY=0 NormalZ=1 AngleXU=0 Radius=3
    g6: Circle CenterX=23.851 CenterY=-67.6202 CenterZ=0 NormalX=0 NormalY=0 NormalZ=1 AngleXU=0 Radius=2
    g7: Circle CenterX=23.851 CenterY=-67.6202 CenterZ=0 NormalX=0 NormalY=0 NormalZ=1 AngleXU=0 Radius=3
  constraints (8):
    c: Block(g3)
    c: Block(g2)
    c: Block(g1)
    c: Block(g0)
    c: Block(g6)
    c: Block(g7)
    c: Block(g4)
    c: Block(g5)
FEATURE [Sketcher::SketchObject] Sketch060
  FullyConstrained = true
  MapMode = 3
  Placement = pos=(0,0,0) rot=(1,0,0;1.5708rad)
  Support = -> [Extrude049]
  sketch-geometry (8):
    g0: Circle CenterX=80.351 CenterY=-67.6202 CenterZ=0 NormalX=0 NormalY=0 NormalZ=1 AngleXU=0 Radius=3
    g1: Circle CenterX=80.351 CenterY=-4.92017 CenterZ=0 NormalX=0 NormalY=0 NormalZ=1 AngleXU=0 Radius=3
    g2: Circle CenterX=23.851 CenterY=-4.92017 CenterZ=0 NormalX=0 NormalY=0 NormalZ=1 AngleXU=0 Radius=3
    g3: Circle CenterX=23.851 CenterY=-67.6202 CenterZ=0 NormalX=0 NormalY=0 NormalZ=1 AngleXU=0 Radius=3
    g4: Circle CenterX=23.851 CenterY=-67.6202 CenterZ=0 NormalX=0 NormalY=0 NormalZ=1 AngleXU=0 Radius=5
    g5: Circle CenterX=80.351 CenterY=-67.6202 CenterZ=0 NormalX=0 NormalY=0 NormalZ=1 AngleXU=0 Radius=5
    g6: Circle CenterX=23.851 CenterY=-4.92017 CenterZ=0 NormalX=0 NormalY=0 NormalZ=1 AngleXU=0 Radius=5
    g7: Circle CenterX=80.351 CenterY=-4.92017 CenterZ=0 NormalX=0 NormalY=0 NormalZ=1 AngleXU=0 Radius=5
  constraints (8):
    c: Block(g1)
    c: Block(g0)
    c: Block(g3)
    c: Block(g2)
    c: Block(g5)
    c: Block(g4)
    c: Block(g6)
    c: Block(g7)
FEATURE [Sketcher::SketchObject] Sketch061
  FullyConstrained = true
  MapMode = 3
  Placement = pos=(0,0,0) rot=(1,0,0;1.5708rad)
  sketch-geometry (8):
    g0: Circle CenterX=80.351 CenterY=-67.6202 CenterZ=0 NormalX=0 NormalY=0 NormalZ=1 AngleXU=0 Radius=3
    g1: Circle CenterX=80.351 CenterY=-4.92017 CenterZ=0 NormalX=0 NormalY=0 NormalZ=1 AngleXU=0 Radius=3
    g2: Circle CenterX=23.851 CenterY=-4.92017 CenterZ=0 NormalX=0 NormalY=0 NormalZ=1 AngleXU=0 Radius=3
    g3: Circle CenterX=23.851 CenterY=-67.6202 CenterZ=0 NormalX=0 NormalY=0 NormalZ=1 AngleXU=0 Radius=3
    g4: Circle CenterX=23.851 CenterY=-67.6202 CenterZ=0 NormalX=0 NormalY=0 NormalZ=1 AngleXU=0 Radius=5
    g5: Circle CenterX=80.351 CenterY=-67.6202 CenterZ=0 NormalX=0 NormalY=0 NormalZ=1 AngleXU=0 Radius=5
    g6: Circle CenterX=23.851 CenterY=-4.92017 CenterZ=0 NormalX=0 NormalY=0 NormalZ=1 AngleXU=0 Radius=5
    g7: Circle CenterX=80.351 CenterY=-4.92017 CenterZ=0 NormalX=0 NormalY=0 NormalZ=1 AngleXU=0 Radius=5
  constraints (8):
    c: Block(g1)
    c: Block(g0)
    c: Block(g3)
    c: Block(g2)
    c: Block(g5)
    c: Block(g4)
    c: Block(g6)
    c: Block(g7)
FEATURE [Sketcher::SketchObject] Sketch062  label="topSketch016"
  FullyConstrained = true
  sketch-geometry (20):
    g0: LineSegment StartX=5.21097e-06 StartY=3 StartZ=0 EndX=5.21097e-06 EndY=19 EndZ=0
    g1: ArcOfCircle CenterX=19 CenterY=19 CenterZ=0 NormalX=0 NormalY=0 NormalZ=1 AngleXU=0 Radius=19 StartAngle=1.5708 EndAngle=3.14159
    g2: ArcOfCircle CenterX=19 CenterY=19 CenterZ=0 NormalX=0 NormalY=0 NormalZ=1 AngleXU=0 Radius=16 StartAngle=1.5708 EndAngle=3.14159
    g3: LineSegment StartX=114 StartY=35 StartZ=0 EndX=19 EndY=35 EndZ=0
    g4: LineSegment StartX=5.21097e-06 StartY=3 StartZ=0 EndX=5.21097e-06 EndY=0 EndZ=0
    g5: LineSegment StartX=3 StartY=0 StartZ=0 EndX=5.21097e-06 EndY=0 EndZ=0
    g6: LineSegment StartX=3 StartY=19 StartZ=0 EndX=3 EndY=0 EndZ=0
    g7: LineSegment StartX=19 StartY=38 StartZ=0 EndX=124 EndY=38 EndZ=0
    g8: Circle CenterX=119 CenterY=35 CenterZ=0 NormalX=0 NormalY=0 NormalZ=1 AngleXU=0 Radius=1
    g9: Circle CenterX=121 CenterY=35 CenterZ=0 NormalX=0 NormalY=0 NormalZ=1 AngleXU=0 Radius=1
    g10: Circle CenterX=121 CenterY=33 CenterZ=0 NormalX=0 NormalY=0 NormalZ=1 AngleXU=0 Radius=1
    g11: BSplineCurve PolesCount=3 KnotsCount=2 Degree=2 IsPeriodic=0
    g12: GeomPoint X=119 Y=35 Z=0
    g13: GeomPoint X=121 Y=33 Z=0
    g14: LineSegment StartX=119 StartY=35 StartZ=0 EndX=114 EndY=35 EndZ=0
    g15: ArcOfCircle CenterX=105 CenterY=19 CenterZ=0 NormalX=0 NormalY=0 NormalZ=1 AngleXU=0 Radius=19 StartAngle=5.7297 EndAngle=6.28319
    g16: ArcOfCircle CenterX=105 CenterY=19 CenterZ=0 NormalX=0 NormalY=0 NormalZ=1 AngleXU=0 Radius=16 StartAngle=5.60905 EndAngle=6.28319
    g17: LineSegment StartX=121 StartY=33 StartZ=0 EndX=121 EndY=19 EndZ=0
    g18: LineSegment StartX=124 StartY=38 StartZ=0 EndX=124 EndY=19 EndZ=0
    g19: LineSegment StartX=117.5 StartY=9.01251 StartZ=0 EndX=121.163 EndY=9.0125 EndZ=0
  constraints (46):
    c: Vertical(g0)
    c: Block(g0)
    c: Coincident(g1,g0)
    c: Block(g1)
    c: Coincident(g2,g1)
    c: Block(g2)
    c: Coincident(g3,g2)
    c: Horizontal(g3)
    c: Tangent(g3,g2)
    c: Coincident(g4,g0)
    c: Distance(g4) = 3
    c: Vertical(g4)
    c: Coincident(g5,g4)
    c: Horizontal(g5)
    c: Coincident(g6,g2)
    c: Coincident(g6,g5)
    c: Vertical(g6)
    c: Horizontal(g7)
    c: Distance(g7) = 105
    c: Coincident(g7,g1)
    c: Block(g3)
    c: Weight(g8) = 1
    c: Equal(g8,g9)
    c: Equal(g8,g10)
    c: InternalAlignment(g8,g11)
    c: InternalAlignment(g9,g11)
    c: InternalAlignment(g10,g11)
    c: InternalAlignment(g12,g11)
    c: InternalAlignment(g13,g11)
    c: Block(g11)
    c: Coincident(g14,g11)
    c: Coincident(g14,g3)
    c: Horizontal(g14)
    c: Block(g15)
    c: Coincident(g16,g15)
    c: Block(g16)
    c: Coincident(g17,g11)
    c: Coincident(g17,g16)
    c: Vertical(g17)
    c: Distance(g17) = 14
    c: Coincident(g18,g7)
    c: Coincident(g18,g15)
    c: Vertical(g18)
    c: Distance(g18) = 19
    c: Coincident(g19,g16)
    c: Coincident(g19,g15)
FEATURE [Part::Extrusion] Extrude053  label="top024"
  Base = -> Sketch062
  Dir = (0,0,1)
  DirMode = 2
  FaceMakerClass = Part::FaceMakerBullseye
  LengthFwd = 72
  LengthRev = 0
  Solid = true
  Symmetric = false
FEATURE [Sketcher::SketchObject] Sketch063
  FullyConstrained = true
  MapMode = 3
  Placement = pos=(0,0,0) rot=(1,0,0;1.5708rad)
  Support = -> [Extrude053]
  sketch-geometry (8):
    g0: Circle CenterX=80.351 CenterY=-67.6202 CenterZ=0 NormalX=0 NormalY=0 NormalZ=1 AngleXU=0 Radius=2
    g1: Circle CenterX=80.351 CenterY=-67.6202 CenterZ=0 NormalX=0 NormalY=0 NormalZ=1 AngleXU=0 Radius=3
    g2: Circle CenterX=80.351 CenterY=-4.92017 CenterZ=0 NormalX=0 NormalY=0 NormalZ=1 AngleXU=0 Radius=2
    g3: Circle CenterX=80.351 CenterY=-4.92017 CenterZ=0 NormalX=0 NormalY=0 NormalZ=1 AngleXU=0 Radius=3
    g4: Circle CenterX=23.851 CenterY=-4.92017 CenterZ=0 NormalX=0 NormalY=0 NormalZ=1 AngleXU=0 Radius=2
    g5: Circle CenterX=23.851 CenterY=-4.92017 CenterZ=0 NormalX=0 NormalY=0 NormalZ=1 AngleXU=0 Radius=3
    g6: Circle CenterX=23.851 CenterY=-67.6202 CenterZ=0 NormalX=0 NormalY=0 NormalZ=1 AngleXU=0 Radius=2
    g7: Circle CenterX=23.851 CenterY=-67.6202 CenterZ=0 NormalX=0 NormalY=0 NormalZ=1 AngleXU=0 Radius=3
  constraints (8):
    c: Block(g3)
    c: Block(g2)
    c: Block(g1)
    c: Block(g0)
    c: Block(g6)
    c: Block(g7)
    c: Block(g4)
    c: Block(g5)
FEATURE [Part::Extrusion] Extrude054
  Base = -> Sketch063
  Dir = (0,-1,2e-16)
  DirMode = 2
  FaceMakerClass = Part::FaceMakerBullseye
  LengthFwd = 6
  LengthRev = 0
  Placement = pos=(0,9,0) rot=(0,0,1;0rad)
  Solid = true
  Symmetric = false
FEATURE [Sketcher::SketchObject] Sketch064  label="topSketch017"
  FullyConstrained = true
  sketch-geometry (20):
    g0: LineSegment StartX=5.21097e-06 StartY=3 StartZ=0 EndX=5.21097e-06 EndY=19 EndZ=0
    g1: ArcOfCircle CenterX=19 CenterY=19 CenterZ=0 NormalX=0 NormalY=0 NormalZ=1 AngleXU=0 Radius=19 StartAngle=1.5708 EndAngle=3.14159
    g2: ArcOfCircle CenterX=19 CenterY=19 CenterZ=0 NormalX=0 NormalY=0 NormalZ=1 AngleXU=0 Radius=16 StartAngle=1.5708 EndAngle=3.14159
    g3: LineSegment StartX=114 StartY=35 StartZ=0 EndX=19 EndY=35 EndZ=0
    g4: LineSegment StartX=5.21097e-06 StartY=3 StartZ=0 EndX=5.21097e-06 EndY=0 EndZ=0
    g5: LineSegment StartX=3 StartY=0 StartZ=0 EndX=5.21097e-06 EndY=0 EndZ=0
    g6: LineSegment StartX=3 StartY=19 StartZ=0 EndX=3 EndY=0 EndZ=0
    g7: LineSegment StartX=19 StartY=38 StartZ=0 EndX=124 EndY=38 EndZ=0
    g8: Circle CenterX=119 CenterY=35 CenterZ=0 NormalX=0 NormalY=0 NormalZ=1 AngleXU=0 Radius=1
    g9: Circle CenterX=121 CenterY=35 CenterZ=0 NormalX=0 NormalY=0 NormalZ=1 AngleXU=0 Radius=1
    g10: Circle CenterX=121 CenterY=33 CenterZ=0 NormalX=0 NormalY=0 NormalZ=1 AngleXU=0 Radius=1
    g11: BSplineCurve PolesCount=3 KnotsCount=2 Degree=2 IsPeriodic=0
    g12: GeomPoint X=119 Y=35 Z=0
    g13: GeomPoint X=121 Y=33 Z=0
    g14: LineSegment StartX=119 StartY=35 StartZ=0 EndX=114 EndY=35 EndZ=0
    g15: ArcOfCircle CenterX=105 CenterY=19 CenterZ=0 NormalX=0 NormalY=0 NormalZ=1 AngleXU=0 Radius=19 StartAngle=5.7297 EndAngle=6.28319
    g16: ArcOfCircle CenterX=105 CenterY=19 CenterZ=0 NormalX=0 NormalY=0 NormalZ=1 AngleXU=0 Radius=16 StartAngle=5.60905 EndAngle=6.28319
    g17: LineSegment StartX=121 StartY=33 StartZ=0 EndX=121 EndY=19 EndZ=0
    g18: LineSegment StartX=124 StartY=38 StartZ=0 EndX=124 EndY=19 EndZ=0
    g19: LineSegment StartX=117.5 StartY=9.01251 StartZ=0 EndX=121.163 EndY=9.0125 EndZ=0
  constraints (46):
    c: Vertical(g0)
    c: Block(g0)
    c: Coincident(g1,g0)
    c: Block(g1)
    c: Coincident(g2,g1)
    c: Block(g2)
    c: Coincident(g3,g2)
    c: Horizontal(g3)
    c: Tangent(g3,g2)
    c: Coincident(g4,g0)
    c: Distance(g4) = 3
    c: Vertical(g4)
    c: Coincident(g5,g4)
    c: Horizontal(g5)
    c: Coincident(g6,g2)
    c: Coincident(g6,g5)
    c: Vertical(g6)
    c: Horizontal(g7)
    c: Distance(g7) = 105
    c: Coincident(g7,g1)
    c: Block(g3)
    c: Weight(g8) = 1
    c: Equal(g8,g9)
    c: Equal(g8,g10)
    c: InternalAlignment(g8,g11)
    c: InternalAlignment(g9,g11)
    c: InternalAlignment(g10,g11)
    c: InternalAlignment(g12,g11)
    c: InternalAlignment(g13,g11)
    c: Block(g11)
    c: Coincident(g14,g11)
    c: Coincident(g14,g3)
    c: Horizontal(g14)
    c: Block(g15)
    c: Coincident(g16,g15)
    c: Block(g16)
    c: Coincident(g17,g11)
    c: Coincident(g17,g16)
    c: Vertical(g17)
    c: Distance(g17) = 14
    c: Coincident(g18,g7)
    c: Coincident(g18,g15)
    c: Vertical(g18)
    c: Distance(g18) = 19
    c: Coincident(g19,g16)
    c: Coincident(g19,g15)
FEATURE [Sketcher::SketchObject] Sketch065
  FullyConstrained = true
  MapMode = 3
  Placement = pos=(0,0,0) rot=(1,0,0;1.5708rad)
  sketch-geometry (8):
    g0: Circle CenterX=80.351 CenterY=-67.6202 CenterZ=0 NormalX=0 NormalY=0 NormalZ=1 AngleXU=0 Radius=3
    g1: Circle CenterX=80.351 CenterY=-4.92017 CenterZ=0 NormalX=0 NormalY=0 NormalZ=1 AngleXU=0 Radius=3
    g2: Circle CenterX=23.851 CenterY=-4.92017 CenterZ=0 NormalX=0 NormalY=0 NormalZ=1 AngleXU=0 Radius=3
    g3: Circle CenterX=23.851 CenterY=-67.6202 CenterZ=0 NormalX=0 NormalY=0 NormalZ=1 AngleXU=0 Radius=3
    g4: Circle CenterX=23.851 CenterY=-67.6202 CenterZ=0 NormalX=0 NormalY=0 NormalZ=1 AngleXU=0 Radius=5
    g5: Circle CenterX=80.351 CenterY=-67.6202 CenterZ=0 NormalX=0 NormalY=0 NormalZ=1 AngleXU=0 Radius=5
    g6: Circle CenterX=23.851 CenterY=-4.92017 CenterZ=0 NormalX=0 NormalY=0 NormalZ=1 AngleXU=0 Radius=5
    g7: Circle CenterX=80.351 CenterY=-4.92017 CenterZ=0 NormalX=0 NormalY=0 NormalZ=1 AngleXU=0 Radius=5
  constraints (8):
    c: Block(g1)
    c: Block(g0)
    c: Block(g3)
    c: Block(g2)
    c: Block(g5)
    c: Block(g4)
    c: Block(g6)
    c: Block(g7)
FEATURE [Part::Extrusion] Extrude056
  Base = -> Sketch065
  Dir = (0,-1,2e-16)
  DirMode = 2
  FaceMakerClass = Part::FaceMakerBullseye
  LengthFwd = 2
  LengthRev = 0
  Solid = true
  Symmetric = false
FEATURE [Part::Extrusion] Extrude057  label="top025"
  Base = -> Sketch064
  Dir = (0,0,1)
  DirMode = 2
  FaceMakerClass = Part::FaceMakerBullseye
  LengthFwd = 72
  LengthRev = 0
  Solid = true
  Symmetric = false
FEATURE [Sketcher::SketchObject] Sketch066
  FullyConstrained = true
  MapMode = 3
  Placement = pos=(0,0,0) rot=(1,0,0;1.5708rad)
  Support = -> [Extrude057]
  sketch-geometry (8):
    g0: Circle CenterX=80.351 CenterY=-67.6202 CenterZ=0 NormalX=0 NormalY=0 NormalZ=1 AngleXU=0 Radius=3
    g1: Circle CenterX=80.351 CenterY=-4.92017 CenterZ=0 NormalX=0 NormalY=0 NormalZ=1 AngleXU=0 Radius=3
    g2: Circle CenterX=23.851 CenterY=-4.92017 CenterZ=0 NormalX=0 NormalY=0 NormalZ=1 AngleXU=0 Radius=3
    g3: Circle CenterX=23.851 CenterY=-67.6202 CenterZ=0 NormalX=0 NormalY=0 NormalZ=1 AngleXU=0 Radius=3
    g4: Circle CenterX=23.851 CenterY=-67.6202 CenterZ=0 NormalX=0 NormalY=0 NormalZ=1 AngleXU=0 Radius=5
    g5: Circle CenterX=80.351 CenterY=-67.6202 CenterZ=0 NormalX=0 NormalY=0 NormalZ=1 AngleXU=0 Radius=5
    g6: Circle CenterX=23.851 CenterY=-4.92017 CenterZ=0 NormalX=0 NormalY=0 NormalZ=1 AngleXU=0 Radius=5
    g7: Circle CenterX=80.351 CenterY=-4.92017 CenterZ=0 NormalX=0 NormalY=0 NormalZ=1 AngleXU=0 Radius=5
  constraints (8):
    c: Block(g1)
    c: Block(g0)
    c: Block(g3)
    c: Block(g2)
    c: Block(g5)
    c: Block(g4)
    c: Block(g6)
    c: Block(g7)
FEATURE [Part::Extrusion] Extrude055
  Base = -> Sketch066
  Dir = (0,-1,2e-16)
  DirMode = 2
  FaceMakerClass = Part::FaceMakerBullseye
  LengthFwd = 2
  LengthRev = 0
  Solid = true
  Symmetric = false
FEATURE [Part::Fillet] Fillet041
  Base = -> Extrude056
  Edges = 4 edges r=1.99: [Edge6,Edge12,Edge18,Edge24]
FEATURE [Part::Cut] Cut045
  Base = -> Extrude055
  Placement = pos=(0,6,0) rot=(0,0,1;0rad)
  Tool = -> Fillet041
FEATURE [Part::MultiFuse] Fusion095  label="pcbScrewPillars"
  Placement = pos=(-3.2,-1,72.3) rot=(0,0,1;0rad)
  Shapes = -> [Cut045,Extrude054]
FEATURE [Part::Feature] Face113
  shape: bbox 3.2 x 1.5 x 2e-07 mm, 1 faces, 0 solids (baked)
FEATURE [Part::Revolution] Revolve121  label="backCaseScrewRetainer002"
  Angle = 360
  Axis = (0,1,0)
  Base = (0,0,0)
  FaceMakerClass = Part::FaceMakerBullseye
  Placement = pos=(12.5,3,62) rot=(0,0,1;0rad)
  Solid = false
  Source = -> Face113
  Symmetric = false
FEATURE [Part::Feature] Face114
  shape: bbox 3.2 x 1.5 x 2e-07 mm, 1 faces, 0 solids (baked)
FEATURE [Part::Feature] Face115
  shape: bbox 3.2 x 1.5 x 2e-07 mm, 1 faces, 0 solids (baked)
FEATURE [Part::Feature] Face116
  shape: bbox 3.2 x 1.5 x 2e-07 mm, 1 faces, 0 solids (baked)
FEATURE [Part::Revolution] Revolve122  label="frontCaseScrewRetainer004"
  Angle = 360
  Axis = (0,1,0)
  Base = (0,0,0)
  FaceMakerClass = Part::FaceMakerBullseye
  Placement = pos=(89.5,3,68.5) rot=(0,0,1;0rad)
  Solid = false
  Source = -> Face115
  Symmetric = false
FEATURE [Part::Revolution] Revolve123  label="frontCaseScrewRetainer005"
  Angle = 360
  Axis = (0,1,0)
  Base = (0,0,0)
  FaceMakerClass = Part::FaceMakerBullseye
  Placement = pos=(89.5,3,3.5) rot=(0,0,1;0rad)
  Solid = false
  Source = -> Face116
  Symmetric = false
FEATURE [Part::Revolution] Revolve124  label="backCaseScrewRetainer003"
  Angle = 360
  Axis = (0,1,0)
  Base = (0,0,0)
  FaceMakerClass = Part::FaceMakerBullseye
  Placement = pos=(12.5,3,10) rot=(0,0,1;0rad)
  Solid = false
  Source = -> Face114
  Symmetric = false
FEATURE [Part::Feature] Face117
  shape: bbox 3.6 x 3.2 x 2e-07 mm, 1 faces, 0 solids (baked)
FEATURE [Part::Revolution] Revolve125  label="moreFrontCaseScrewRetainer004"
  Angle = 360
  Axis = (0,1,0)
  Base = (0,0,0)
  FaceMakerClass = Part::FaceMakerBullseye
  Placement = pos=(109.5,4.5,68.5) rot=(0,0,1;0rad)
  Solid = false
  Source = -> Face117
  Symmetric = false
FEATURE [Part::Feature] Face118
  shape: bbox 3.6 x 3.2 x 2e-07 mm, 1 faces, 0 solids (baked)
FEATURE [Part::Revolution] Revolve126  label="moreFrontCaseScrewRetainer005"
  Angle = 360
  Axis = (0,1,0)
  Base = (0,0,0)
  FaceMakerClass = Part::FaceMakerBullseye
  Placement = pos=(109.5,4.5,3.5) rot=(0,0,1;0rad)
  Solid = false
  Source = -> Face118
  Symmetric = false
FEATURE [Part::MultiFuse] Fusion096  label="screwRetainers001"
  Shapes = -> [Revolve126,Revolve125,Revolve124,Revolve123,Revolve122,Revolve121]
FEATURE [Part::Feature] Face119
  shape: bbox 10 x 16.5 x 2e-07 mm, 1 faces, 0 solids (baked)
FEATURE [Part::Revolution] Revolve130  label="plugHousing050"
  Angle = 360
  Axis = (0,1,0)
  Base = (0,0,0)
  FaceMakerClass = Part::FaceMakerBullseye
  Placement = pos=(0,0,36.15) rot=(0,0,1;0rad)
  Solid = false
  Source = -> Face119
  Symmetric = false
FEATURE [Part::Feature] Face120
  shape: bbox 10 x 16.5 x 2e-07 mm, 1 faces, 0 solids (baked)
FEATURE [Part::Feature] Face121
  shape: bbox 10 x 16.5 x 2e-07 mm, 1 faces, 0 solids (baked)
FEATURE [Part::Revolution] Revolve127  label="plugHousing047"
  Angle = 360
  Axis = (0,1,0)
  Base = (0,0,0)
  FaceMakerClass = Part::FaceMakerBullseye
  Placement = pos=(0,0,36.15) rot=(0,0,1;0rad)
  Solid = false
  Source = -> Face121
  Symmetric = false
FEATURE [Part::Feature] Face122
  shape: bbox 10 x 16.5 x 2e-07 mm, 1 faces, 0 solids (baked)
FEATURE [Part::Feature] Face123
  shape: bbox 10 x 16.5 x 2e-07 mm, 1 faces, 0 solids (baked)
FEATURE [Part::Revolution] Revolve128  label="plugHousing048"
  Angle = 360
  Axis = (0,1,0)
  Base = (0,0,0)
  FaceMakerClass = Part::FaceMakerBullseye
  Placement = pos=(0,0,36.15) rot=(0,0,1;0rad)
  Solid = false
  Source = -> Face123
  Symmetric = false
FEATURE [Part::MultiFuse] Fusion100  label="plugHousing054"
  Placement = pos=(0,0,0) rot=(0,0,1;1.5708rad)
  Shapes = -> [Revolve130,Revolve128]
FEATURE [Part::Feature] Face124
  shape: bbox 10 x 16.5 x 2e-07 mm, 1 faces, 0 solids (baked)
FEATURE [Part::Feature] Face125
  shape: bbox 10 x 16.5 x 2e-07 mm, 1 faces, 0 solids (baked)
FEATURE [Part::Revolution] Revolve129  label="plugHousing049"
  Angle = 360
  Axis = (0,1,0)
  Base = (0,0,0)
  FaceMakerClass = Part::FaceMakerBullseye
  Placement = pos=(0,0,36.15) rot=(0,0,1;0rad)
  Solid = false
  Source = -> Face125
  Symmetric = false
FEATURE [Part::Feature] Face126
  shape: bbox 10 x 16.5 x 2e-07 mm, 1 faces, 0 solids (baked)
FEATURE [Part::Revolution] Revolve131  label="plugHousing058"
  Angle = 360
  Axis = (0,1,0)
  Base = (0,0,0)
  FaceMakerClass = Part::FaceMakerBullseye
  Placement = pos=(0,0,36.15) rot=(0,0,1;0rad)
  Solid = false
  Source = -> Face120
  Symmetric = false
FEATURE [Part::MultiFuse] Fusion099  label="plugHousing053"
  Placement = pos=(0,0,0) rot=(0,0,1;1.5708rad)
  Shapes = -> [Revolve127,Revolve131]
FEATURE [Part::MultiFuse] Fusion102  label="plugHousing056"
  Placement = pos=(0,19,0) rot=(0,0,1;3.14159rad)
  Shapes = -> [Fusion100,Fusion099]
FEATURE [Part::Revolution] Revolve132  label="plugHousing059"
  Angle = 360
  Axis = (0,1,0)
  Base = (0,0,0)
  FaceMakerClass = Part::FaceMakerBullseye
  Placement = pos=(0,0,36.15) rot=(0,0,1;0rad)
  Solid = false
  Source = -> Face126
  Symmetric = false
FEATURE [Part::Revolution] Revolve133  label="plugHousing060"
  Angle = 360
  Axis = (0,1,0)
  Base = (0,0,0)
  FaceMakerClass = Part::FaceMakerBullseye
  Placement = pos=(0,0,36.15) rot=(0,0,1;0rad)
  Solid = false
  Source = -> Face122
  Symmetric = false
FEATURE [Part::MultiFuse] Fusion097  label="plugHousing051"
  Placement = pos=(0,0,0) rot=(0,0,1;1.5708rad)
  Shapes = -> [Revolve133,Revolve132]
FEATURE [Part::Revolution] Revolve134  label="plugHousing061"
  Angle = 360
  Axis = (0,1,0)
  Base = (0,0,0)
  FaceMakerClass = Part::FaceMakerBullseye
  Placement = pos=(0,0,36.15) rot=(0,0,1;0rad)
  Solid = false
  Source = -> Face124
  Symmetric = false
FEATURE [Part::MultiFuse] Fusion101  label="plugHousing055"
  Placement = pos=(0,0,0) rot=(0,0,1;1.5708rad)
  Shapes = -> [Revolve129,Revolve134]
FEATURE [Part::MultiFuse] Fusion098  label="plugHousing052"
  Placement = pos=(0,19,0) rot=(0,0,1;3.14159rad)
  Shapes = -> [Fusion097,Fusion101]
FEATURE [Part::MultiFuse] Fusion103  label="plugHousing057"
  Placement = pos=(122.621,0,-0.15) rot=(0,0,1;0rad)
  Shapes = -> [Fusion102,Fusion098]
FEATURE [Part::Box] Box028  label="Cube015"
  AttacherType = Attacher::AttachEngine3D
  Height = 28
  Length = 3
  Placement = pos=(110.7,19,22) rot=(0,0,1;0rad)
  Width = 15.7
FEATURE [Part::Cylinder] Cylinder044
  Angle = 360
  AttacherType = Attacher::AttachEngine3D
  Height = 20
  Placement = pos=(0,0,36.15) rot=(0,0,1;0rad)
  Radius = 10.3
FEATURE [Part::Cylinder] Cylinder045
  Angle = 360
  AttacherType = Attacher::AttachEngine3D
  Height = 10
  Placement = pos=(0,0,36.15) rot=(0,0,1;0rad)
  Radius = 4
FEATURE [Part::MultiFuse] Fusion104  label="removeToCreteHoleForPlugHousing040"
  Placement = pos=(70,19,36) rot=(0,1,0;1.5708rad)
  Shapes = -> [Cylinder044,Cylinder045]
FEATURE [Part::Cut] Cut046  label="plugHousingTab003"
  Base = -> Box028
  Tool = -> Fusion104
FEATURE [Part::MultiFuse] Fusion105  label="plugHousing062"
  Shapes = -> [Fusion103,Cut046]
FEATURE [Part::Fillet] Fillet042
  Base = -> Fusion105
  Edges = 1 edges r=2: [Edge25]
FEATURE [Part::Fillet] Fillet043  label="plugHousing063"
  Base = -> Fillet042
  Edges = 1 edges r=2: [Edge8]
  Placement = pos=(7,0,0) rot=(0,0,1;0rad)
FEATURE [Part::Feature] Face127
  shape: bbox 10 x 16.5 x 2e-07 mm, 1 faces, 0 solids (baked)
FEATURE [Part::Feature] Face128
  shape: bbox 10 x 16.5 x 2e-07 mm, 1 faces, 0 solids (baked)
FEATURE [Part::Revolution] Revolve137  label="plugHousing070"
  Angle = 360
  Axis = (0,1,0)
  Base = (0,0,0)
  FaceMakerClass = Part::FaceMakerBullseye
  Placement = pos=(0,0,36.15) rot=(0,0,1;0rad)
  Solid = false
  Source = -> Face127
  Symmetric = false
FEATURE [Part::Revolution] Revolve140  label="plugHousing073"
  Angle = 360
  Axis = (0,1,0)
  Base = (0,0,0)
  FaceMakerClass = Part::FaceMakerBullseye
  Placement = pos=(0,0,36.15) rot=(0,0,1;0rad)
  Solid = false
  Source = -> Face128
  Symmetric = false
FEATURE [Part::Feature] Face129
  shape: bbox 10 x 16.5 x 2e-07 mm, 1 faces, 0 solids (baked)
FEATURE [Part::Revolution] Revolve138  label="plugHousing071"
  Angle = 360
  Axis = (0,1,0)
  Base = (0,0,0)
  FaceMakerClass = Part::FaceMakerBullseye
  Placement = pos=(0,0,36.15) rot=(0,0,1;0rad)
  Solid = false
  Source = -> Face129
  Symmetric = false
FEATURE [Part::Feature] Face130
  shape: bbox 10 x 16.5 x 2e-07 mm, 1 faces, 0 solids (baked)
FEATURE [Part::Revolution] Revolve139  label="plugHousing072"
  Angle = 360
  Axis = (0,1,0)
  Base = (0,0,0)
  FaceMakerClass = Part::FaceMakerBullseye
  Placement = pos=(0,0,36.15) rot=(0,0,1;0rad)
  Solid = false
  Source = -> Face130
  Symmetric = false
FEATURE [Part::Feature] Face131
  shape: bbox 10 x 16.5 x 2e-07 mm, 1 faces, 0 solids (baked)
FEATURE [Part::Revolution] Revolve135  label="plugHousing068"
  Angle = 360
  Axis = (0,1,0)
  Base = (0,0,0)
  FaceMakerClass = Part::FaceMakerBullseye
  Placement = pos=(0,0,36.15) rot=(0,0,1;0rad)
  Solid = false
  Source = -> Face131
  Symmetric = false
FEATURE [Part::MultiFuse] Fusion112  label="plugHousing078"
  Placement = pos=(0,0,0) rot=(0,0,1;1.5708rad)
  Shapes = -> [Revolve135,Revolve139]
FEATURE [Part::Feature] Face132
  shape: bbox 10 x 16.5 x 2e-07 mm, 1 faces, 0 solids (baked)
FEATURE [Part::Revolution] Revolve141  label="plugHousing074"
  Angle = 360
  Axis = (0,1,0)
  Base = (0,0,0)
  FaceMakerClass = Part::FaceMakerBullseye
  Placement = pos=(0,0,36.15) rot=(0,0,1;0rad)
  Solid = false
  Source = -> Face132
  Symmetric = false
FEATURE [Part::MultiFuse] Fusion110  label="plugHousing076"
  Placement = pos=(0,0,0) rot=(0,0,1;1.5708rad)
  Shapes = -> [Revolve141,Revolve140]
FEATURE [Part::Feature] Face133
  shape: bbox 10 x 16.5 x 2e-07 mm, 1 faces, 0 solids (baked)
FEATURE [Part::Revolution] Revolve136  label="plugHousing069"
  Angle = 360
  Axis = (0,1,0)
  Base = (0,0,0)
  FaceMakerClass = Part::FaceMakerBullseye
  Placement = pos=(0,0,36.15) rot=(0,0,1;0rad)
  Solid = false
  Source = -> Face133
  Symmetric = false
FEATURE [Part::MultiFuse] Fusion106  label="plugHousing064"
  Placement = pos=(0,0,0) rot=(0,0,1;1.5708rad)
  Shapes = -> [Revolve138,Revolve136]
FEATURE [Part::MultiFuse] Fusion108  label="plugHousing066"
  Placement = pos=(0,19,0) rot=(0,0,1;3.14159rad)
  Shapes = -> [Fusion106,Fusion112]
FEATURE [Part::Feature] Face134
  shape: bbox 10 x 16.5 x 2e-07 mm, 1 faces, 0 solids (baked)
FEATURE [Part::Revolution] Revolve142  label="plugHousing075"
  Angle = 360
  Axis = (0,1,0)
  Base = (0,0,0)
  FaceMakerClass = Part::FaceMakerBullseye
  Placement = pos=(0,0,36.15) rot=(0,0,1;0rad)
  Solid = false
  Source = -> Face134
  Symmetric = false
FEATURE [Part::MultiFuse] Fusion107  label="plugHousing065"
  Placement = pos=(0,0,0) rot=(0,0,1;1.5708rad)
  Shapes = -> [Revolve137,Revolve142]
FEATURE [Part::MultiFuse] Fusion111  label="plugHousing077"
  Placement = pos=(0,19,0) rot=(0,0,1;3.14159rad)
  Shapes = -> [Fusion110,Fusion107]
FEATURE [Part::MultiFuse] Fusion109  label="plugHousing067"
  Placement = pos=(131.236,0,-0.15) rot=(0,0,1;0rad)
  Shapes = -> [Fusion108,Fusion111]
FEATURE [Part::MultiFuse] Fusion113  label="plugHousing079"
  Shapes = -> [Fillet043,Fusion109]
FEATURE [Part::Feature] Face135
  shape: bbox 3.5 x 17.8 x 2e-07 mm, 1 faces, 0 solids (baked)
FEATURE [Part::Revolution] Revolve143  label="removeToCreateScrewAndThreadedInsertHole049"
  Angle = 360
  Axis = (0,1,0)
  Base = (0,0,0)
  FaceMakerClass = Part::FaceMakerBullseye
  Placement = pos=(12.5,0,10) rot=(0,0,1;0rad)
  Solid = false
  Source = -> Face135
  Symmetric = false
FEATURE [Part::Feature] Face136
  shape: bbox 3.5 x 17.8 x 2e-07 mm, 1 faces, 0 solids (baked)
FEATURE [Part::Revolution] Revolve144  label="removeToCreateScrewAndThreadedInsertHole050"
  Angle = 360
  Axis = (0,1,0)
  Base = (0,0,0)
  FaceMakerClass = Part::FaceMakerBullseye
  Placement = pos=(12.5,0,62) rot=(0,0,1;0rad)
  Solid = false
  Source = -> Face136
  Symmetric = false
FEATURE [Part::Feature] Face137
  shape: bbox 3.5 x 17.8 x 2e-07 mm, 1 faces, 0 solids (baked)
FEATURE [Part::Revolution] Revolve145  label="removeToCreateScrewAndThreadedInsertHole051"
  Angle = 360
  Axis = (0,1,0)
  Base = (0,0,0)
  FaceMakerClass = Part::FaceMakerBullseye
  Placement = pos=(89.5,0,68.5) rot=(0,0,1;0rad)
  Solid = false
  Source = -> Face137
  Symmetric = false
FEATURE [Part::Feature] Face138
  shape: bbox 3.5 x 17.8 x 2e-07 mm, 1 faces, 0 solids (baked)
FEATURE [Part::Revolution] Revolve146  label="removeToCreateScrewAndThreadedInsertHole052"
  Angle = 360
  Axis = (0,1,0)
  Base = (0,0,0)
  FaceMakerClass = Part::FaceMakerBullseye
  Placement = pos=(89.5,0,3.5) rot=(0,0,1;0rad)
  Solid = false
  Source = -> Face138
  Symmetric = false
FEATURE [Part::Feature] Face139
  shape: bbox 3.5 x 17.8 x 2e-07 mm, 1 faces, 0 solids (baked)
FEATURE [Part::Revolution] Revolve147  label="removeToCreateScrewAndThreadedInsertHole053"
  Angle = 360
  Axis = (0,1,0)
  Base = (0,0,0)
  FaceMakerClass = Part::FaceMakerBullseye
  Placement = pos=(109.5,4.7,3.5) rot=(0,0,1;0rad)
  Solid = false
  Source = -> Face139
  Symmetric = false
FEATURE [Part::Feature] Face140
  shape: bbox 3.5 x 17.8 x 2e-07 mm, 1 faces, 0 solids (baked)
FEATURE [Part::Revolution] Revolve148  label="removeToCreateScrewAndThreadedInsertHole054"
  Angle = 360
  Axis = (0,1,0)
  Base = (0,0,0)
  FaceMakerClass = Part::FaceMakerBullseye
  Placement = pos=(109.5,4.7,68.5) rot=(0,0,1;0rad)
  Solid = false
  Source = -> Face140
  Symmetric = false
FEATURE [Part::MultiFuse] Fusion114  label="removeToCreateScrewAndThreadedInsertHole055"
  Shapes = -> [Revolve148,Revolve147,Revolve146,Revolve145,Revolve144,Revolve143]
FEATURE [Part::Cut] Cut047  label="casePillars004"
  Base = -> Cut037
  Tool = -> Fusion114
FEATURE [Part::Feature] Face141
  shape: bbox 3.5 x 17.8 x 2e-07 mm, 1 faces, 0 solids (baked)
FEATURE [Part::Feature] Face142
  shape: bbox 3.5 x 17.8 x 2e-07 mm, 1 faces, 0 solids (baked)
FEATURE [Part::Feature] Face143
  shape: bbox 3.5 x 17.8 x 2e-07 mm, 1 faces, 0 solids (baked)
FEATURE [Part::Revolution] Revolve149  label="removeToCreateScrewAndThreadedInsertHole057"
  Angle = 360
  Axis = (0,1,0)
  Base = (0,0,0)
  FaceMakerClass = Part::FaceMakerBullseye
  Placement = pos=(12.5,0,10) rot=(0,0,1;0rad)
  Solid = false
  Source = -> Face141
  Symmetric = false
FEATURE [Part::Feature] Face144
  shape: bbox 3.5 x 17.8 x 2e-07 mm, 1 faces, 0 solids (baked)
FEATURE [Part::Feature] Face145
  shape: bbox 3.5 x 17.8 x 2e-07 mm, 1 faces, 0 solids (baked)
FEATURE [Part::Feature] Face146
  shape: bbox 3.5 x 17.8 x 2e-07 mm, 1 faces, 0 solids (baked)
FEATURE [Part::Revolution] Revolve150  label="removeToCreateScrewAndThreadedInsertHole058"
  Angle = 360
  Axis = (0,1,0)
  Base = (0,0,0)
  FaceMakerClass = Part::FaceMakerBullseye
  Placement = pos=(12.5,0,62) rot=(0,0,1;0rad)
  Solid = false
  Source = -> Face146
  Symmetric = false
FEATURE [Part::Revolution] Revolve151  label="removeToCreateScrewAndThreadedInsertHole059"
  Angle = 360
  Axis = (0,1,0)
  Base = (0,0,0)
  FaceMakerClass = Part::FaceMakerBullseye
  Placement = pos=(89.5,0,68.5) rot=(0,0,1;0rad)
  Solid = false
  Source = -> Face143
  Symmetric = false
FEATURE [Part::Revolution] Revolve152  label="removeToCreateScrewAndThreadedInsertHole060"
  Angle = 360
  Axis = (0,1,0)
  Base = (0,0,0)
  FaceMakerClass = Part::FaceMakerBullseye
  Placement = pos=(89.5,0,3.5) rot=(0,0,1;0rad)
  Solid = false
  Source = -> Face142
  Symmetric = false
FEATURE [Part::Revolution] Revolve153  label="removeToCreateScrewAndThreadedInsertHole061"
  Angle = 360
  Axis = (0,1,0)
  Base = (0,0,0)
  FaceMakerClass = Part::FaceMakerBullseye
  Placement = pos=(109.5,4.7,3.5) rot=(0,0,1;0rad)
  Solid = false
  Source = -> Face145
  Symmetric = false
FEATURE [Part::Revolution] Revolve154  label="removeToCreateScrewAndThreadedInsertHole062"
  Angle = 360
  Axis = (0,1,0)
  Base = (0,0,0)
  FaceMakerClass = Part::FaceMakerBullseye
  Placement = pos=(109.5,4.7,68.5) rot=(0,0,1;0rad)
  Solid = false
  Source = -> Face144
  Symmetric = false
FEATURE [Part::MultiFuse] Fusion115  label="removeToCreateScrewAndThreadedInsertHole056"
  Shapes = -> [Revolve154,Revolve153,Revolve152,Revolve151,Revolve150,Revolve149]
FEATURE [Part::Feature] Face147
  shape: bbox 9.8 x 26.5 x 2e-07 mm, 1 faces, 0 solids (baked)
FEATURE [Part::Revolution] Revolve155
  Angle = 360
  Axis = (0,1,0)
  Base = (0,0,0)
  FaceMakerClass = Part::FaceMakerBullseye
  Placement = pos=(0,0,0) rot=(0,0,1;1.5708rad)
  Solid = false
  Source = -> Face147
  Symmetric = false
FEATURE [Part::Feature] Face148
  shape: bbox 9.8 x 26.5 x 2e-07 mm, 1 faces, 0 solids (baked)
FEATURE [Part::Revolution] Revolve156
  Angle = 360
  Axis = (0,1,0)
  Base = (0,0,0)
  FaceMakerClass = Part::FaceMakerBullseye
  Placement = pos=(0,0,0) rot=(0,0,1;1.5708rad)
  Solid = false
  Source = -> Face148
  Symmetric = false
FEATURE [Part::MultiFuse] Fusion116
  Placement = pos=(-18,19,36) rot=(0,0,1;0rad)
  Shapes = -> [Revolve156,Revolve155]
FEATURE [Part::Box] Box029  label="Cube016"
  AttacherType = Attacher::AttachEngine3D
  Height = 28
  Length = 3
  Placement = pos=(110.7,19,22) rot=(0,0,1;0rad)
  Width = 15.7
FEATURE [Part::Cylinder] Cylinder046
  Angle = 360
  AttacherType = Attacher::AttachEngine3D
  Height = 10
  Placement = pos=(0,0,36.15) rot=(0,0,1;0rad)
  Radius = 4
FEATURE [Part::Cylinder] Cylinder047
  Angle = 360
  AttacherType = Attacher::AttachEngine3D
  Height = 20
  Placement = pos=(0,0,36.15) rot=(0,0,1;0rad)
  Radius = 10.3
FEATURE [Part::MultiFuse] Fusion117  label="removeToCreteHoleForPlugHousing041"
  Placement = pos=(70,19,36) rot=(0,1,0;1.5708rad)
  Shapes = -> [Cylinder047,Cylinder046]
FEATURE [Part::Cut] Cut049  label="plugHousingTab004"
  Base = -> Box029
  Placement = pos=(-107.4,-14,0) rot=(0,0,1;0rad)
  Tool = -> Fusion117
FEATURE [Part::Box] Box030  label="Cube017"
  AttacherType = Attacher::AttachEngine3D
  Height = 28
  Length = 3
  Placement = pos=(110.7,19,22) rot=(0,0,1;0rad)
  Width = 15.7
FEATURE [Part::Cylinder] Cylinder048
  Angle = 360
  AttacherType = Attacher::AttachEngine3D
  Height = 10
  Placement = pos=(0,0,36.15) rot=(0,0,1;0rad)
  Radius = 4
FEATURE [Part::Cylinder] Cylinder049
  Angle = 360
  AttacherType = Attacher::AttachEngine3D
  Height = 20
  Placement = pos=(0,0,36.15) rot=(0,0,1;0rad)
  Radius = 10.3
FEATURE [Part::MultiFuse] Fusion118  label="removeToCreteHoleForPlugHousing042"
  Placement = pos=(70,19,36) rot=(0,1,0;1.5708rad)
  Shapes = -> [Cylinder049,Cylinder048]
FEATURE [Part::Cut] Cut050  label="plugHousingTab005"
  Base = -> Box030
  Placement = pos=(-107.4,-14,0) rot=(0,0,1;0rad)
  Tool = -> Fusion118
FEATURE [Part::MultiFuse] Fusion119
  Placement = pos=(9.6,23,0) rot=(0,0,1;3.14159rad)
  Shapes = -> [Cut049,Cut050]
FEATURE [Part::Box] Box031  label="Cube018"
  AttacherType = Attacher::AttachEngine3D
  Height = 10
  Length = 3
  Placement = pos=(3.3,4,12) rot=(0,0,1;0rad)
  Width = 10
FEATURE [Part::Fillet] Fillet044
  Base = -> Box031
  Edges = 1 edges r=2: [Edge11]
FEATURE [Part::Box] Box032  label="Cube019"
  AttacherType = Attacher::AttachEngine3D
  Height = 10
  Length = 3
  Placement = pos=(3.3,4,50) rot=(0,0,1;0rad)
  Width = 10
FEATURE [Part::Fillet] Fillet045
  Base = -> Box032
  Edges = 1 edges r=2: [Edge12]
FEATURE [Part::Box] Box033  label="Cube020"
  AttacherType = Attacher::AttachEngine3D
  Height = 28
  Length = 4
  Placement = pos=(5,0,22) rot=(0,0,1;0rad)
  Width = 10
FEATURE [Part::Fillet] Fillet046
  Base = -> Box033
  Edges = 1 edges r=1: [Edge7]
FEATURE [Part::Fillet] Fillet047
  Base = -> Fillet046
  Edges = 1 edges r=2: [Edge5]
FEATURE [Part::Fillet] Fillet048
  Base = -> Fillet047
  Edges = 1 edges r=2: [Edge2]
FEATURE [Part::Cylinder] Cylinder050
  Angle = 360
  AttacherType = Attacher::AttachEngine3D
  Height = 20
  Placement = pos=(0,0,36.15) rot=(0,0,1;0rad)
  Radius = 8.2
FEATURE [Part::Cylinder] Cylinder051
  Angle = 360
  AttacherType = Attacher::AttachEngine3D
  Height = 10
  Placement = pos=(0,0,36.15) rot=(0,0,1;0rad)
  Radius = 4
FEATURE [Part::MultiFuse] Fusion120  label="removeToCreteHoleForPlugHousing043"
  Placement = pos=(-42,19,36) rot=(0,1,0;1.5708rad)
  Shapes = -> [Cylinder050,Cylinder051]
FEATURE [Sketcher::SketchObject] Sketch067  label="topSketch018"
  FullyConstrained = true
  sketch-geometry (4):
    g0: LineSegment StartX=16.8446 StartY=31.512 StartZ=0 EndX=16.3251 EndY=34.4666 EndZ=0
    g1: ArcOfCircle CenterX=19 CenterY=19.2524 CenterZ=0 NormalX=0 NormalY=0 NormalZ=1 AngleXU=0 Radius=15.4476 StartAngle=1.74483 EndAngle=2.72717
    g2: ArcOfCircle CenterX=19 CenterY=19.2524 CenterZ=0 NormalX=0 NormalY=0 NormalZ=1 AngleXU=0 Radius=12.4476 StartAngle=1.74483 EndAngle=2.73189
    g3: LineSegment StartX=4.86004 StartY=25.4725 StartZ=0 EndX=7.58253 EndY=24.2107 EndZ=0
  constraints (7):
    c: Block(g0)
    c: Coincident(g1,g0)
    c: Coincident(g2,g0)
    c: Coincident(g3,g1)
    c: Coincident(g3,g2)
    c: Block(g1)
    c: Block(g2)
FEATURE [Part::Extrusion] Extrude058
  Base = -> Sketch067
  Dir = (0,0,1)
  DirMode = 2
  FaceMakerClass = Part::FaceMakerBullseye
  LengthFwd = 10
  LengthRev = 0
  Placement = pos=(0,0,31) rot=(0,0,1;0rad)
  Solid = true
  Symmetric = false
FEATURE [Part::Cut] Cut051
  Base = -> Extrude058
  Tool = -> Fusion120
FEATURE [Part::Fillet] Fillet049
  Base = -> Cut051
  Edges = 1 edges r=2: [Edge1]
FEATURE [Part::Fillet] Fillet050
  Base = -> Fillet049
  Edges = 1 edges r=2.5: [Edge1]
FEATURE [Part::Fillet] Fillet051
  Base = -> Fillet050
  Edges = 1 edges r=2.5: [Edge2]
FEATURE [Part::MultiFuse] Fusion121  label="wireHolder003"
  Shapes = -> [Fusion116,Fillet051]
FEATURE [Part::MultiFuse] Fusion122
  Shapes = -> [Fillet045,Fusion121]
FEATURE [Part::MultiFuse] Fusion123  label="wireHolder004"
  Shapes = -> [Fusion122,Fillet048]
FEATURE [Part::MultiFuse] Fusion124  label="wireHolder005"
  Shapes = -> [Fillet044,Fusion119,Fusion123]
FEATURE [Sketcher::SketchObject] Sketch068  label="topSketch019"
  FullyConstrained = true
  sketch-geometry (6):
    g0: LineSegment StartX=19 StartY=38 StartZ=0 EndX=117 EndY=38 EndZ=0
    g1: ArcOfCircle CenterX=19 CenterY=19 CenterZ=0 NormalX=0 NormalY=0 NormalZ=1 AngleXU=0 Radius=19 StartAngle=1.5708 EndAngle=3.14159
    g2: LineSegment StartX=117 StartY=38 StartZ=0 EndX=117 EndY=19 EndZ=0
    g3: LineSegment StartX=98 StartY=1.0161e-12 StartZ=0 EndX=5.22862e-06 EndY=1.0161e-12 EndZ=0
    g4: LineSegment StartX=5.22862e-06 StartY=19 StartZ=0 EndX=5.22862e-06 EndY=1.0161e-12 EndZ=0
    g5: ArcOfCircle CenterX=98 CenterY=19 CenterZ=0 NormalX=0 NormalY=0 NormalZ=1 AngleXU=0 Radius=19 StartAngle=4.71239 EndAngle=6.28319
  constraints (16):
    c: Horizontal(g0)
    c: Distance(g0) = 98
    c: Coincident(g1,g0)
    c: Block(g1)
    c: Coincident(g2,g0)
    c: Vertical(g2)
    c: Distance(g2) = 19
    c: Horizontal(g3)
    c: Coincident(g4,g1)
    c: Vertical(g4)
    c: Coincident(g3,g4)
    c: Block(g3)
    c: Coincident(g5,g2)
    c: Coincident(g5,g3)
    c: Block(g0)
    c: Block(g5)
FEATURE [Part::Extrusion] Extrude059  label="sideA002"
  Base = -> Sketch068
  Dir = (0,0,1)
  DirMode = 2
  FaceMakerClass = Part::FaceMakerBullseye
  LengthFwd = 3
  LengthRev = 0
  Placement = pos=(0,0,-2.7) rot=(0,0,1;0rad)
  Solid = true
  Symmetric = false
FEATURE [Sketcher::SketchObject] Sketch069  label="topSketch020"
  FullyConstrained = true
  sketch-geometry (6):
    g0: LineSegment StartX=19 StartY=38 StartZ=0 EndX=117 EndY=38 EndZ=0
    g1: ArcOfCircle CenterX=19 CenterY=19 CenterZ=0 NormalX=0 NormalY=0 NormalZ=1 AngleXU=0 Radius=19 StartAngle=1.5708 EndAngle=3.14159
    g2: LineSegment StartX=117 StartY=38 StartZ=0 EndX=117 EndY=19 EndZ=0
    g3: LineSegment StartX=98 StartY=1.0161e-12 StartZ=0 EndX=5.22862e-06 EndY=1.0161e-12 EndZ=0
    g4: LineSegment StartX=5.22862e-06 StartY=19 StartZ=0 EndX=5.22862e-06 EndY=1.0161e-12 EndZ=0
    g5: ArcOfCircle CenterX=98 CenterY=19 CenterZ=0 NormalX=0 NormalY=0 NormalZ=1 AngleXU=0 Radius=19 StartAngle=4.71239 EndAngle=6.28319
  constraints (16):
    c: Horizontal(g0)
    c: Distance(g0) = 98
    c: Coincident(g1,g0)
    c: Block(g1)
    c: Coincident(g2,g0)
    c: Vertical(g2)
    c: Distance(g2) = 19
    c: Horizontal(g3)
    c: Coincident(g4,g1)
    c: Vertical(g4)
    c: Coincident(g3,g4)
    c: Block(g3)
    c: Coincident(g5,g2)
    c: Coincident(g5,g3)
    c: Block(g0)
    c: Block(g5)
FEATURE [Part::Extrusion] Extrude060  label="sideB002"
  Base = -> Sketch069
  Dir = (0,0,1)
  DirMode = 2
  FaceMakerClass = Part::FaceMakerBullseye
  LengthFwd = 3
  LengthRev = 0
  Placement = pos=(0,0,71.7) rot=(0,0,1;0rad)
  Solid = true
  Symmetric = false
FEATURE [Part::MultiFuse] Fusion127  label="removeFromBottom001"
  Placement = pos=(2,0,0) rot=(0,0,1;0rad)
  Shapes = -> [Extrude059,Extrude060]
FEATURE [Part::Cylinder] Cylinder052
  Angle = 360
  AttacherType = Attacher::AttachEngine3D
  Height = 20
  Placement = pos=(0,0,36.15) rot=(0,0,1;0rad)
  Radius = 14
FEATURE [Part::Cylinder] Cylinder053
  Angle = 360
  AttacherType = Attacher::AttachEngine3D
  Height = 10
  Placement = pos=(0,0,36.15) rot=(0,0,1;0rad)
  Radius = 4
FEATURE [Part::MultiFuse] Fusion128  label="removeToCreteHoleForPlugHousing044"
  Placement = pos=(70,19,36) rot=(0,1,0;1.5708rad)
  Shapes = -> [Cylinder052,Cylinder053]
FEATURE [Part::Cut] Cut052  label="bottom011"
  Base = -> Extrude043
  Tool = -> Fusion128
FEATURE [Part::Cut] Cut054  label="bottom012"
  Base = -> Cut052
  Tool = -> Fusion115
FEATURE [Sketcher::SketchObject] Sketch070
  FullyConstrained = true
  Placement = pos=(117,19,0) rot=(0.57735,0.57735,0.57735;2.0944rad)
  sketch-geometry (48):
    g0: LineSegment StartX=-49.19 StartY=69.25 StartZ=0 EndX=-49.19 EndY=66.25 EndZ=0
    g1: LineSegment StartX=-49.19 StartY=63.5 StartZ=0 EndX=-49.19 EndY=60.5 EndZ=0
    g2: LineSegment StartX=-49.19 StartY=57.75 StartZ=0 EndX=-49.19 EndY=54.75 EndZ=0
    g3: LineSegment StartX=-49.19 StartY=52 StartZ=0 EndX=-49.19 EndY=49 EndZ=0
    g4: LineSegment StartX=-49.19 StartY=46.25 StartZ=0 EndX=-49.19 EndY=43.25 EndZ=0
    g5: LineSegment StartX=-49.19 StartY=40.5 StartZ=0 EndX=-49.19 EndY=37.5 EndZ=0
    g6: LineSegment StartX=-49.19 StartY=34.5 StartZ=0 EndX=-49.19 EndY=31.5 EndZ=0
    g7: LineSegment StartX=-49.19 StartY=28.75 StartZ=0 EndX=-49.19 EndY=25.75 EndZ=0
    g8: LineSegment StartX=-49.19 StartY=23 StartZ=0 EndX=-49.19 EndY=20 EndZ=0
    g9: LineSegment StartX=-49.19 StartY=17.25 StartZ=0 EndX=-49.19 EndY=14.25 EndZ=0
    g10: LineSegment StartX=-49.19 StartY=11.5 StartZ=0 EndX=-49.19 EndY=8.5 EndZ=0
    g11: LineSegment StartX=-49.19 StartY=5.75 StartZ=0 EndX=-49.19 EndY=2.75 EndZ=0
    g12: ArcOfCircle CenterX=-1.5 CenterY=67.75 CenterZ=0 NormalX=0 NormalY=0 NormalZ=1 AngleXU=0 Radius=1.5 StartAngle=4.71239 EndAngle=7.85398
    g13: ArcOfCircle CenterX=-1.5 CenterY=62 CenterZ=0 NormalX=0 NormalY=0 NormalZ=1 AngleXU=0 Radius=1.5 StartAngle=4.71239 EndAngle=7.85398
    g14: ArcOfCircle CenterX=-1.5 CenterY=56.25 CenterZ=0 NormalX=0 NormalY=0 NormalZ=1 AngleXU=0 Radius=1.5 StartAngle=4.71239 EndAngle=7.85398
    g15: ArcOfCircle CenterX=-11.49 CenterY=50.5 CenterZ=0 NormalX=0 NormalY=0 NormalZ=1 AngleXU=0 Radius=1.5 StartAngle=4.71239 EndAngle=7.85398
    g16: ArcOfCircle CenterX=-16.28 CenterY=44.75 CenterZ=0 NormalX=0 NormalY=0 NormalZ=1 AngleXU=0 Radius=1.5 StartAngle=4.71239 EndAngle=7.85398
    g17: ArcOfCircle CenterX=-18.2337 CenterY=39 CenterZ=0 NormalX=0 NormalY=0 NormalZ=1 AngleXU=0 Radius=1.5 StartAngle=4.71485 EndAngle=7.85398
    g18: ArcOfCircle CenterX=-16.2837 CenterY=27.25 CenterZ=0 NormalX=0 NormalY=0 NormalZ=1 AngleXU=0 Radius=1.5 StartAngle=4.71485 EndAngle=7.85398
    g19: ArcOfCircle CenterX=-18.2337 CenterY=33 CenterZ=0 NormalX=0 NormalY=0 NormalZ=1 AngleXU=0 Radius=1.5 StartAngle=4.71485 EndAngle=7.85398
    g20: ArcOfCircle CenterX=-11.49 CenterY=21.5 CenterZ=0 NormalX=0 NormalY=0 NormalZ=1 AngleXU=0 Radius=1.5 StartAngle=4.71239 EndAngle=7.85398
    g21: ArcOfCircle CenterX=-1.5 CenterY=4.25 CenterZ=0 NormalX=0 NormalY=0 NormalZ=1 AngleXU=0 Radius=1.5 StartAngle=4.71239 EndAngle=7.85398
    g22: ArcOfCircle CenterX=-1.5 CenterY=10 CenterZ=0 NormalX=0 NormalY=0 NormalZ=1 AngleXU=0 Radius=1.5 StartAngle=4.71239 EndAngle=7.85398
    g23: ArcOfCircle CenterX=-1.5 CenterY=15.75 CenterZ=0 NormalX=0 NormalY=0 NormalZ=1 AngleXU=0 Radius=1.5 StartAngle=4.71239 EndAngle=7.85398
    g24: LineSegment StartX=-49.19 StartY=69.25 StartZ=0 EndX=-1.5 EndY=69.25 EndZ=0
    g25: LineSegment StartX=-49.19 StartY=66.25 StartZ=0 EndX=-1.5 EndY=66.25 EndZ=0
    g26: LineSegment StartX=-49.19 StartY=63.5 StartZ=0 EndX=-1.5 EndY=63.5 EndZ=0
    g27: LineSegment StartX=-49.19 StartY=60.5 StartZ=0 EndX=-1.5 EndY=60.5 EndZ=0
    g28: LineSegment StartX=-49.19 StartY=57.75 StartZ=0 EndX=-1.5 EndY=57.75 EndZ=0
    g29: LineSegment StartX=-49.19 StartY=54.75 StartZ=0 EndX=-1.5 EndY=54.75 EndZ=0
    g30: LineSegment StartX=-49.19 StartY=52 StartZ=0 EndX=-11.49 EndY=52 EndZ=0
    g31: LineSegment StartX=-49.19 StartY=49 StartZ=0 EndX=-11.49 EndY=49 EndZ=0
    g32: LineSegment StartX=-49.19 StartY=46.25 StartZ=0 EndX=-16.28 EndY=46.25 EndZ=0
    g33: LineSegment StartX=-49.19 StartY=43.25 StartZ=0 EndX=-16.28 EndY=43.25 EndZ=0
    g34: LineSegment StartX=-49.19 StartY=40.5 StartZ=0 EndX=-18.2337 EndY=40.5 EndZ=0
    g35: LineSegment StartX=-49.19 StartY=37.5 StartZ=0 EndX=-18.23 EndY=37.5 EndZ=0
    g36: LineSegment StartX=-49.19 StartY=34.5 StartZ=0 EndX=-18.2337 EndY=34.5 EndZ=0
    g37: LineSegment StartX=-49.19 StartY=31.5 StartZ=0 EndX=-18.23 EndY=31.5 EndZ=0
    g38: LineSegment StartX=-49.19 StartY=28.75 StartZ=0 EndX=-16.2837 EndY=28.75 EndZ=0
    g39: LineSegment StartX=-49.19 StartY=25.75 StartZ=0 EndX=-16.28 EndY=25.75 EndZ=0
    g40: LineSegment StartX=-49.19 StartY=23 StartZ=0 EndX=-11.49 EndY=23 EndZ=0
    g41: LineSegment StartX=-49.19 StartY=20 StartZ=0 EndX=-11.49 EndY=20 EndZ=0
    g42: LineSegment StartX=-49.19 StartY=17.25 StartZ=0 EndX=-1.5 EndY=17.25 EndZ=0
    g43: LineSegment StartX=-49.19 StartY=14.25 StartZ=0 EndX=-1.5 EndY=14.25 EndZ=0
    g44: LineSegment StartX=-49.19 StartY=11.5 StartZ=0 EndX=-1.5 EndY=11.5 EndZ=0
    g45: LineSegment StartX=-49.19 StartY=8.5 StartZ=0 EndX=-1.5 EndY=8.5 EndZ=0
    g46: LineSegment StartX=-49.19 StartY=5.75 StartZ=0 EndX=-1.5 EndY=5.75 EndZ=0
    g47: LineSegment StartX=-49.19 StartY=2.75 StartZ=0 EndX=-1.5 EndY=2.75 EndZ=0
  constraints (120):
    c: Vertical(g0)
    c: Distance(g0) = 3
    c: Block(g0)
    c: Vertical(g1)
    c: Distance(g1) = 3
    c: Vertical(g2)
    c: Equal(g0,g2) = 3
    c: Block(g2)
    c: Vertical(g3)
    c: Equal(g1,g3) = 3
    c: Vertical(g4)
    c: Equal(g0,g4) = 3
    c: Block(g4)
    c: Vertical(g5)
    c: Equal(g1,g5) = 3
    c: Vertical(g6)
    c: Equal(g0,g6) = 3
    c: Block(g6)
    c: Vertical(g7)
    c: Equal(g1,g7) = 3
    c: Vertical(g8)
    c: Equal(g0,g8) = 3
    c: Block(g8)
    c: Vertical(g9)
    c: Equal(g1,g9) = 3
    c: Vertical(g10)
    c: Equal(g0,g10) = 3
    c: Block(g10)
    c: Vertical(g11)
    c: Equal(g1,g11) = 3
    c: Block(g12)
    c: Block(g13)
    c: Block(g14)
    c: Block(g15)
    c: Block(g16)
    c: Block(g17)
    c: Block(g18)
    c: Block(g19)
    c: Block(g20)
    c: Block(g21)
    c: Block(g22)
    c: Block(g23)
    c: Block(g11)
    c: Block(g9)
    c: Block(g7)
    c: Block(g5)
    c: Block(g3)
    c: Block(g1)
    c: Coincident(g24,g0)
    c: Coincident(g24,g12)
    c: Horizontal(g24)
    c: Coincident(g25,g0)
    c: Coincident(g25,g12)
    c: Horizontal(g25)
    c: Coincident(g26,g1)
    c: Coincident(g26,g13)
    c: Horizontal(g26)
    c: Coincident(g27,g1)
    c: Coincident(g27,g13)
    c: Horizontal(g27)
    c: Coincident(g28,g2)
    c: Coincident(g28,g14)
    c: Horizontal(g28)
    c: Coincident(g29,g2)
    c: Coincident(g29,g14)
    c: Horizontal(g29)
    c: Coincident(g30,g3)
    c: Coincident(g30,g15)
    c: Horizontal(g30)
    c: Coincident(g31,g3)
    c: Coincident(g31,g15)
    c: Horizontal(g31)
    c: Coincident(g32,g4)
    c: Coincident(g32,g16)
    c: Horizontal(g32)
    c: Coincident(g33,g4)
    c: Coincident(g33,g16)
    c: Horizontal(g33)
    c: Coincident(g34,g5)
    c: Coincident(g34,g17)
    c: Horizontal(g34)
    c: Coincident(g35,g5)
    c: Coincident(g35,g17)
    c: Horizontal(g35)
    c: Coincident(g36,g6)
    c: Coincident(g36,g19)
    c: Horizontal(g36)
    c: Coincident(g37,g6)
    c: Coincident(g37,g19)
    c: Horizontal(g37)
    c: Coincident(g38,g7)
    c: Coincident(g38,g18)
    c: Horizontal(g38)
    c: Coincident(g39,g7)
    c: Coincident(g39,g18)
    c: Horizontal(g39)
    c: Coincident(g40,g8)
    c: Coincident(g40,g20)
    c: Horizontal(g40)
    c: Coincident(g41,g8)
    c: Coincident(g41,g20)
    c: Horizontal(g41)
    c: Coincident(g42,g9)
    c: Coincident(g42,g23)
    c: Horizontal(g42)
    c: Coincident(g43,g9)
    c: Coincident(g43,g23)
    c: Horizontal(g43)
    c: Coincident(g44,g10)
    c: Coincident(g44,g22)
    c: Horizontal(g44)
    c: Coincident(g45,g10)
    c: Coincident(g45,g22)
    c: Horizontal(g45)
    c: Coincident(g46,g11)
    c: Coincident(g46,g21)
    c: Horizontal(g46)
    c: Coincident(g47,g11)
    c: Coincident(g47,g21)
    c: Horizontal(g47)
FEATURE [Part::Extrusion] Extrude061
  Base = -> Sketch070
  Dir = (1,0,0)
  DirMode = 2
  FaceMakerClass = Part::FaceMakerBullseye
  LengthFwd = 23
  LengthRev = 0
  Placement = pos=(-19,0,0) rot=(0,0,1;0rad)
  Solid = true
  Symmetric = false
FEATURE [Part::Fillet] Fillet052  label="removeToCreateVentalationHoles002"
  Base = -> Extrude061
  Edges = <same value as first occurrence — deduplicated (x6 in doc)>
  Placement = pos=(7,0.02,0) rot=(0,0,1;0rad)
FEATURE [Part::MultiFuse] Fusion130  label="bottom013"
  Shapes = -> [Cut054,Cut034]
FEATURE [Part::Cut] Cut055
  Base = -> Fusion130
  Tool = -> Fillet052
FEATURE [Part::Cylinder] Cylinder054
  Angle = 360
  AttacherType = Attacher::AttachEngine3D
  Height = 20
  Placement = pos=(0,0,36.15) rot=(0,0,1;0rad)
  Radius = 4
FEATURE [Sketcher::SketchObject] Sketch071  label="bottomSketch002"
  FullyConstrained = true
  sketch-geometry (32):
    g0: LineSegment StartX=3.3 StartY=-6.03275e-07 StartZ=0 EndX=98 EndY=-6.03275e-07 EndZ=0
    g1: ArcOfCircle CenterX=98 CenterY=19 CenterZ=0 NormalX=0 NormalY=0 NormalZ=1 AngleXU=0 Radius=19 StartAngle=4.71239 EndAngle=5.71103
    g2: LineSegment StartX=6.3 StartY=8 StartZ=0 EndX=3.3 EndY=8 EndZ=0
    g3: LineSegment StartX=3.3 StartY=8 StartZ=0 EndX=3.3 EndY=-6.03275e-07 EndZ=0
    g4: ArcOfCircle CenterX=8.3 CenterY=5 CenterZ=0 NormalX=0 NormalY=0 NormalZ=1 AngleXU=0 Radius=2 StartAngle=3.14159 EndAngle=4.71239
    g5: LineSegment StartX=6.3 StartY=8 StartZ=0 EndX=6.3 EndY=5 EndZ=0
    g6: ArcOfCircle CenterX=98 CenterY=19 CenterZ=0 NormalX=0 NormalY=0 NormalZ=1 AngleXU=0 Radius=12.7 StartAngle=4.71239 EndAngle=6.28319
    g7: LineSegment StartX=94.7 StartY=3 StartZ=0 EndX=8.3 EndY=3 EndZ=0
    g8-g12: Circle x5 (B-spline internal-alignment scaffolding for g13; pole/knot coordinates omitted)
    g13: BSplineCurve PolesCount=5 KnotsCount=3 Degree=3 IsPeriodic=0
    g14: GeomPoint X=98 Y=6.3 Z=0
    g15: GeomPoint X=96.3938 Y=4.71946 Z=0
    g16: GeomPoint X=94.7 Y=3 Z=0
    g17-g23: Circle x7 (B-spline internal-alignment scaffolding for g24; pole/knot coordinates omitted)
    g24: BSplineCurve PolesCount=7 KnotsCount=5 Degree=3 IsPeriodic=0
    g25-g29: GeomPoint x5 (B-spline internal-alignment scaffolding for g24; pole/knot coordinates omitted)
    g30: ArcOfCircle CenterX=98 CenterY=19 CenterZ=0 NormalX=0 NormalY=0 NormalZ=1 AngleXU=0 Radius=15.7 StartAngle=5.81226 EndAngle=6.28319
    g31: LineSegment StartX=110.7 StartY=19 StartZ=0 EndX=113.7 EndY=19 EndZ=0
  constraints (41):
    c: Horizontal(g0)
    c: Coincident(g1,g0)
    c: Block(g1)
    c: Horizontal(g2)
    c: Distance(g2) = 3
    c: Coincident(g3,g2)
    c: Vertical(g3)
    c: Coincident(g3,g0)
    c: Block(g4)
    c: Block(g2)
    c: Coincident(g5,g2)
    c: Coincident(g5,g4)
    c: Vertical(g5)
    c: Coincident(g6,g1)
    c: Block(g6)
    c: Coincident(g7,g4)
    c: Horizontal(g7)
    c: Block(g0)
    c: Block(g7)
    c: Block(g3)
    c: Coincident(g13,g6)
    c: Weight(g8) = 1
    c: Equal(g8, g9-g12) x4
    c: Coincident(g13,g7)
    c: InternalAlignment(g8-g12 -> g13) x5
    c: InternalAlignment(g14,g13)
    c: InternalAlignment(g15,g13)
    c: InternalAlignment(g16,g13)
    c: Block(g13)
    c: Weight(g17) = 1
    c: Equal(g17, g18-g23) x6
    c: Coincident(g24,g1)
    c: InternalAlignment(g17-g23 -> g24) x7
    c: InternalAlignment(g25-g29 -> g24) x5
    c: Block(g24)
    c: Coincident(g30,g24)
    c: Coincident(g31,g6)
    c: Coincident(g31,g30)
    c: Horizontal(g31)
    c: Block(g31)
    c: Block(g30)
FEATURE [Part::Extrusion] Extrude062  label="bottom014"
  Base = -> Sketch071
  Dir = (0,0,1)
  DirMode = 2
  FaceMakerClass = Part::FaceMakerBullseye
  LengthFwd = 71.4
  LengthRev = 0
  Placement = pos=(0,0,0.3) rot=(0,0,1;0rad)
  Solid = true
  Symmetric = false
FEATURE [Part::Fillet] Fillet054
  Base = -> Extrude062
  Edges = 1 edges r=2.4: [Edge17]
FEATURE [Part::Fillet] Fillet055  label="bottom015"
  Base = -> Fillet054
  Edges = 1 edges r=2.4: [Edge36]
FEATURE [Part::Cylinder] Cylinder055
  Angle = 360
  AttacherType = Attacher::AttachEngine3D
  Height = 10
  Placement = pos=(0,0,36.15) rot=(0,0,1;0rad)
  Radius = 4
FEATURE [Part::MultiFuse] Fusion131  label="removeToCreateHoleForPlugHousing002"
  Placement = pos=(70,19,36.15) rot=(0,1,0;1.5708rad)
  Shapes = -> [Cylinder054,Cylinder055]
FEATURE [Part::Cut] Cut056  label="Bottom001"
  Base = -> Fillet055
  Placement = pos=(9,0,0) rot=(0,0,1;0rad)
  Tool = -> Fusion131
FEATURE [Part::Cut] Cut057
  Base = -> Cut055
  Tool = -> Cut056
FEATURE [Sketcher::SketchObject] Sketch072  label="topSketch021"
  FullyConstrained = true
  sketch-geometry (4):
    g0: ArcOfCircle CenterX=105 CenterY=19 CenterZ=0 NormalX=0 NormalY=0 NormalZ=1 AngleXU=0 Radius=20.6155 StartAngle=5.54125 EndAngle=6.28319
    g1: ArcOfCircle CenterX=105 CenterY=19 CenterZ=0 NormalX=0 NormalY=0 NormalZ=1 AngleXU=0 Radius=13 StartAngle=5.54125 EndAngle=6.28319
    g2: LineSegment StartX=118 StartY=19 StartZ=0 EndX=125.616 EndY=19 EndZ=0
    g3: LineSegment StartX=114.583 StartY=10.2157 StartZ=0 EndX=120.197 EndY=5.06982 EndZ=0
  constraints (7):
    c: Block(g0)
    c: Block(g1)
    c: Coincident(g2,g1)
    c: Coincident(g2,g0)
    c: Horizontal(g2)
    c: Coincident(g3,g1)
    c: Coincident(g3,g0)
FEATURE [Part::Extrusion] Extrude063  label="bottomPlugHousingBit003"
  Base = -> Sketch072
  Dir = (0,0,1)
  DirMode = 2
  FaceMakerClass = Part::FaceMakerBullseye
  LengthFwd = 72
  LengthRev = 0
  Solid = true
  Symmetric = false
FEATURE [Part::Cylinder] Cylinder056
  Angle = 360
  AttacherType = Attacher::AttachEngine3D
  Height = 20
  Placement = pos=(0,0,36.15) rot=(0,0,1;0rad)
  Radius = 14.3
FEATURE [Part::Cylinder] Cylinder057
  Angle = 360
  AttacherType = Attacher::AttachEngine3D
  Height = 10
  Placement = pos=(0,0,36.15) rot=(0,0,1;0rad)
  Radius = 4
FEATURE [Part::Box] Box034  label="removeToCreteHoleForPlugHousing047"
  AttacherType = Attacher::AttachEngine3D
  Height = 28.6
  Length = 20
  Placement = pos=(106.15,0,21.7) rot=(0,0,1;0rad)
  Width = 19
FEATURE [Part::Cylinder] Cylinder058
  Angle = 360
  AttacherType = Attacher::AttachEngine3D
  Height = 20
  Placement = pos=(0,0,36.15) rot=(0,0,1;0rad)
  Radius = 14.3
FEATURE [Part::Cylinder] Cylinder059
  Angle = 360
  AttacherType = Attacher::AttachEngine3D
  Height = 10
  Placement = pos=(0,0,36.15) rot=(0,0,1;0rad)
  Radius = 4
FEATURE [Part::MultiFuse] Fusion134  label="removeToCreteHoleForPlugHousing046"
  Placement = pos=(70,19,36) rot=(0,1,0;1.5708rad)
  Shapes = -> [Cylinder058,Cylinder059]
FEATURE [Part::Cylinder] Cylinder060
  Angle = 360
  AttacherType = Attacher::AttachEngine3D
  Height = 20
  Placement = pos=(0,0,36.15) rot=(0,0,1;0rad)
  Radius = 14
FEATURE [Part::Cylinder] Cylinder061
  Angle = 360
  AttacherType = Attacher::AttachEngine3D
  Height = 10
  Placement = pos=(0,0,36.15) rot=(0,0,1;0rad)
  Radius = 4
FEATURE [Part::MultiFuse] Fusion135  label="removeToCreteHoleForPlugHousing048"
  Placement = pos=(70,19,36) rot=(0,1,0;1.5708rad)
  Shapes = -> [Cylinder060,Cylinder061]
FEATURE [Part::Box] Box035  label="removeToCreteHoleForPlugHousing049"
  AttacherType = Attacher::AttachEngine3D
  Height = 28.6
  Length = 20
  Placement = pos=(106.15,0,21.7) rot=(0,0,1;0rad)
  Width = 19
FEATURE [Part::MultiFuse] Fusion133  label="removeToCreteHoleForPlugHousing045"
  Placement = pos=(0,0,-28.3) rot=(0,0,1;0rad)
  Shapes = -> [Box035,Fusion134]
FEATURE [Part::MultiFuse] Fusion138  label="removeToCreteHoleForPlugHousing051"
  Placement = pos=(70,19,36) rot=(0,1,0;1.5708rad)
  Shapes = -> [Cylinder056,Cylinder057]
FEATURE [Part::MultiFuse] Fusion137  label="removeToCreteHoleForPlugHousing050"
  Placement = pos=(0,0,28.3) rot=(0,0,1;0rad)
  Shapes = -> [Box034,Fusion138]
FEATURE [Part::MultiFuse] Fusion132  label="removeToCreatePlugHousingBottomBit002"
  Shapes = -> [Fusion133,Fusion137]
FEATURE [Part::MultiFuse] Fusion136  label="removeToCreatePlugHousingBottomBit003"
  Shapes = -> [Fusion135,Fusion132]
FEATURE [Part::Cut] Cut058  label="bottomPlugHousingBit002"
  Base = -> Extrude063
  Placement = pos=(-0.09,0,0) rot=(0,0,1;0rad)
  Tool = -> Fusion136
FEATURE [Sketcher::SketchObject] Sketch073  label="bottomSketch003"
  FullyConstrained = true
  sketch-geometry (45):
    g0: LineSegment StartX=6.29999 StartY=8 StartZ=0 EndX=3.29999 EndY=8 EndZ=0
    g1: LineSegment StartX=3.29999 StartY=8 StartZ=0 EndX=3.29999 EndY=-6.03275e-07 EndZ=0
    g2: ArcOfCircle CenterX=8.29999 CenterY=5 CenterZ=0 NormalX=0 NormalY=0 NormalZ=1 AngleXU=0 Radius=2 StartAngle=3.14159 EndAngle=4.71239
    g3: LineSegment StartX=6.29999 StartY=8 StartZ=0 EndX=6.29999 EndY=5 EndZ=0
    g4: ArcOfCircle CenterX=105 CenterY=19 CenterZ=0 NormalX=0 NormalY=0 NormalZ=1 AngleXU=0 Radius=12.7 StartAngle=4.71239 EndAngle=5.94289
    g5-g11: Circle x7 (B-spline internal-alignment scaffolding for g12; pole/knot coordinates omitted)
    g12: BSplineCurve PolesCount=7 KnotsCount=5 Degree=3 IsPeriodic=0
    g13-g17: GeomPoint x5 (B-spline internal-alignment scaffolding for g12; pole/knot coordinates omitted)
    g18: ArcOfCircle CenterX=105 CenterY=19 CenterZ=0 NormalX=0 NormalY=0 NormalZ=1 AngleXU=0 Radius=15.7 StartAngle=5.81226 EndAngle=6.28319
    g19: BSplineCurve PolesCount=5 KnotsCount=3 Degree=3 IsPeriodic=0
    g20: LineSegment StartX=8.29999 StartY=3 StartZ=0 EndX=101.7 EndY=3 EndZ=0
    g21: LineSegment StartX=3.29999 StartY=-6.03275e-07 StartZ=0 EndX=105 EndY=-6.03275e-07 EndZ=0
    g22: LineSegment StartX=120.974 StartY=8.71251 StartZ=0 EndX=122.332 EndY=7.83778 EndZ=0
    g23: LineSegment StartX=105 StartY=-6.03274e-07 StartZ=0 EndX=113 EndY=-6.03274e-07 EndZ=0
    g24: ArcOfCircle CenterX=105 CenterY=19 CenterZ=0 NormalX=0 NormalY=0 NormalZ=1 AngleXU=0 Radius=20.6155 StartAngle=5.11091 EndAngle=5.71103
    g25: ArcOfCircle CenterX=117.7 CenterY=19 CenterZ=0 NormalX=0 NormalY=0 NormalZ=1 AngleXU=0 Radius=3 StartAngle=1.2e-15 EndAngle=2.10468
    g26: Circle CenterX=116.345 CenterY=16.3232 CenterZ=0 NormalX=0 NormalY=0 NormalZ=1 AngleXU=0 Radius=1
    g27: Circle CenterX=117.24 CenterY=15.7584 CenterZ=0 NormalX=0 NormalY=0 NormalZ=1 AngleXU=0 Radius=1
    g28: Circle CenterX=116.972 CenterY=14.7612 CenterZ=0 NormalX=0 NormalY=0 NormalZ=1 AngleXU=0 Radius=1
    g29: BSplineCurve PolesCount=3 KnotsCount=2 Degree=2 IsPeriodic=0
    g30: GeomPoint X=116.345 Y=16.3232 Z=0
    g31: GeomPoint X=116.972 Y=14.7612 Z=0
    g32: Circle CenterX=115.828 CenterY=17.157 CenterZ=0 NormalX=0 NormalY=0 NormalZ=1 AngleXU=0 Radius=1
    g33: Circle CenterX=115.841 CenterY=16.639 CenterZ=0 NormalX=0 NormalY=0 NormalZ=1 AngleXU=0 Radius=1
    g34: Circle CenterX=116.345 CenterY=16.3232 CenterZ=0 NormalX=0 NormalY=0 NormalZ=1 AngleXU=0 Radius=1
    g35: BSplineCurve PolesCount=3 KnotsCount=2 Degree=2 IsPeriodic=0
    g36: GeomPoint X=115.828 Y=17.157 Z=0
    g37: GeomPoint X=116.345 Y=16.3232 Z=0
    g38: LineSegment StartX=115.828 StartY=17.157 StartZ=0 EndX=115.828 EndY=20.8307 EndZ=0
    g39: Circle CenterX=115.828 CenterY=20.8307 CenterZ=0 NormalX=0 NormalY=0 NormalZ=1 AngleXU=0 Radius=1
    g40: Circle CenterX=115.831 CenterY=21.3396 CenterZ=0 NormalX=0 NormalY=0 NormalZ=1 AngleXU=0 Radius=1
    g41: Circle CenterX=116.173 CenterY=21.5825 CenterZ=0 NormalX=0 NormalY=0 NormalZ=1 AngleXU=0 Radius=1
    g42: BSplineCurve PolesCount=3 KnotsCount=2 Degree=2 IsPeriodic=0
    g43: GeomPoint X=115.828 Y=20.8307 Z=0
    g44: GeomPoint X=116.173 Y=21.5825 Z=0
  constraints (70):
    c: Horizontal(g0)
    c: Distance(g0) = 3
    c: Coincident(g1,g0)
    c: Vertical(g1)
    c: Block(g2)
    c: Block(g0)
    c: Coincident(g3,g0)
    c: Coincident(g3,g2)
    c: Vertical(g3)
    c: Block(g1)
    c: Block(g4)
    c: Coincident(g19,g4)
    c: Block(g19)
    c: Equal(g5, g6-g11) x6
    c: InternalAlignment(g5-g11 -> g12) x7
    c: InternalAlignment(g13-g17 -> g12) x5
    c: Block(g12)
    c: Coincident(g18,g12)
    c: Block(g18)
    c: Coincident(g20,g2)
    c: Coincident(g20,g19)
    c: Horizontal(g20)
    c: Distance(g20) = 93.4
    c: Coincident(g21,g1)
    c: Horizontal(g21)
    c: Distance(g21) = 101.7
    c: Horizontal(g23)
    c: Distance(g23) = 8
    c: Coincident(g24,g23)
    c: Block(g23)
    c: Coincident(g22,g24)
    c: Block(g24)
    c: Block(g22)
    c: Distance(g22) = 1.61553
    c: Coincident(g25,g18)
    c: Block(g25)
    c: Weight(g26) = 1
    c: Equal(g26,g27)
    c: Equal(g26,g28)
    c: Coincident(g29,g4)
    c: InternalAlignment(g26,g29)
    c: InternalAlignment(g27,g29)
    c: InternalAlignment(g28,g29)
    c: InternalAlignment(g30,g29)
    c: InternalAlignment(g31,g29)
    c: Block(g29)
    c: Weight(g32) = 1
    c: Equal(g32,g33)
    c: Equal(g32,g34)
    c: Coincident(g35,g29)
    c: InternalAlignment(g32,g35)
    c: InternalAlignment(g33,g35)
    c: InternalAlignment(g34,g35)
    c: InternalAlignment(g36,g35)
    c: InternalAlignment(g37,g35)
    c: Block(g35)
    c: Coincident(g38,g35)
    c: Vertical(g38)
    c: Block(g38)
    c: Coincident(g42,g38)
    c: Weight(g39) = 1
    c: Equal(g39,g40)
    c: Equal(g39,g41)
    c: Coincident(g42,g25)
    c: InternalAlignment(g39,g42)
    c: InternalAlignment(g40,g42)
    c: InternalAlignment(g41,g42)
    c: InternalAlignment(g43,g42)
    c: InternalAlignment(g44,g42)
    c: Block(g42)
FEATURE [Part::Extrusion] Extrude064  label="bottom016"
  Base = -> Sketch073
  Dir = (0,0,1)
  DirMode = 2
  FaceMakerClass = Part::FaceMakerBullseye
  LengthFwd = 71.4
  LengthRev = 0
  Placement = pos=(0,0,0.3) rot=(0,0,1;0rad)
  Solid = true
  Symmetric = false
FEATURE [Part::Revolution] Revolve157  label="removeToCreateScrewAndThreadedInsertHole063"
  Angle = 360
  Axis = (0,1,0)
  Base = (0,0,0)
  FaceMakerClass = Part::FaceMakerBullseye
  Placement = pos=(12.5,0,10) rot=(0,0,1;0rad)
  Solid = false
  Source = -> Face141
  Symmetric = false
FEATURE [Sketcher::SketchObject] Sketch074
  FullyConstrained = true
  Placement = pos=(117,19,0) rot=(0.57735,0.57735,0.57735;2.0944rad)
  sketch-geometry (48):
    g0: LineSegment StartX=-49.19 StartY=69.25 StartZ=0 EndX=-49.19 EndY=66.25 EndZ=0
    g1: LineSegment StartX=-49.19 StartY=63.5 StartZ=0 EndX=-49.19 EndY=60.5 EndZ=0
    g2: LineSegment StartX=-49.19 StartY=57.75 StartZ=0 EndX=-49.19 EndY=54.75 EndZ=0
    g3: LineSegment StartX=-49.19 StartY=52 StartZ=0 EndX=-49.19 EndY=49 EndZ=0
    g4: LineSegment StartX=-49.19 StartY=46.25 StartZ=0 EndX=-49.19 EndY=43.25 EndZ=0
    g5: LineSegment StartX=-49.19 StartY=40.5 StartZ=0 EndX=-49.19 EndY=37.5 EndZ=0
    g6: LineSegment StartX=-49.19 StartY=34.5 StartZ=0 EndX=-49.19 EndY=31.5 EndZ=0
    g7: LineSegment StartX=-49.19 StartY=28.75 StartZ=0 EndX=-49.19 EndY=25.75 EndZ=0
    g8: LineSegment StartX=-49.19 StartY=23 StartZ=0 EndX=-49.19 EndY=20 EndZ=0
    g9: LineSegment StartX=-49.19 StartY=17.25 StartZ=0 EndX=-49.19 EndY=14.25 EndZ=0
    g10: LineSegment StartX=-49.19 StartY=11.5 StartZ=0 EndX=-49.19 EndY=8.5 EndZ=0
    g11: LineSegment StartX=-49.19 StartY=5.75 StartZ=0 EndX=-49.19 EndY=2.75 EndZ=0
    g12: ArcOfCircle CenterX=-1.5 CenterY=67.75 CenterZ=0 NormalX=0 NormalY=0 NormalZ=1 AngleXU=0 Radius=1.5 StartAngle=4.71239 EndAngle=7.85398
    g13: ArcOfCircle CenterX=-1.5 CenterY=62 CenterZ=0 NormalX=0 NormalY=0 NormalZ=1 AngleXU=0 Radius=1.5 StartAngle=4.71239 EndAngle=7.85398
    g14: ArcOfCircle CenterX=-1.5 CenterY=56.25 CenterZ=0 NormalX=0 NormalY=0 NormalZ=1 AngleXU=0 Radius=1.5 StartAngle=4.71239 EndAngle=7.85398
    g15: ArcOfCircle CenterX=-11.49 CenterY=50.5 CenterZ=0 NormalX=0 NormalY=0 NormalZ=1 AngleXU=0 Radius=1.5 StartAngle=4.71239 EndAngle=7.85398
    g16: ArcOfCircle CenterX=-16.28 CenterY=44.75 CenterZ=0 NormalX=0 NormalY=0 NormalZ=1 AngleXU=0 Radius=1.5 StartAngle=4.71239 EndAngle=7.85398
    g17: ArcOfCircle CenterX=-18.2337 CenterY=39 CenterZ=0 NormalX=0 NormalY=0 NormalZ=1 AngleXU=0 Radius=1.5 StartAngle=4.71485 EndAngle=7.85398
    g18: ArcOfCircle CenterX=-16.2837 CenterY=27.25 CenterZ=0 NormalX=0 NormalY=0 NormalZ=1 AngleXU=0 Radius=1.5 StartAngle=4.71485 EndAngle=7.85398
    g19: ArcOfCircle CenterX=-18.2337 CenterY=33 CenterZ=0 NormalX=0 NormalY=0 NormalZ=1 AngleXU=0 Radius=1.5 StartAngle=4.71485 EndAngle=7.85398
    g20: ArcOfCircle CenterX=-11.49 CenterY=21.5 CenterZ=0 NormalX=0 NormalY=0 NormalZ=1 AngleXU=0 Radius=1.5 StartAngle=4.71239 EndAngle=7.85398
    g21: ArcOfCircle CenterX=-1.5 CenterY=4.25 CenterZ=0 NormalX=0 NormalY=0 NormalZ=1 AngleXU=0 Radius=1.5 StartAngle=4.71239 EndAngle=7.85398
    g22: ArcOfCircle CenterX=-1.5 CenterY=10 CenterZ=0 NormalX=0 NormalY=0 NormalZ=1 AngleXU=0 Radius=1.5 StartAngle=4.71239 EndAngle=7.85398
    g23: ArcOfCircle CenterX=-1.5 CenterY=15.75 CenterZ=0 NormalX=0 NormalY=0 NormalZ=1 AngleXU=0 Radius=1.5 StartAngle=4.71239 EndAngle=7.85398
    g24: LineSegment StartX=-49.19 StartY=69.25 StartZ=0 EndX=-1.5 EndY=69.25 EndZ=0
    g25: LineSegment StartX=-49.19 StartY=66.25 StartZ=0 EndX=-1.5 EndY=66.25 EndZ=0
    g26: LineSegment StartX=-49.19 StartY=63.5 StartZ=0 EndX=-1.5 EndY=63.5 EndZ=0
    g27: LineSegment StartX=-49.19 StartY=60.5 StartZ=0 EndX=-1.5 EndY=60.5 EndZ=0
    g28: LineSegment StartX=-49.19 StartY=57.75 StartZ=0 EndX=-1.5 EndY=57.75 EndZ=0
    g29: LineSegment StartX=-49.19 StartY=54.75 StartZ=0 EndX=-1.5 EndY=54.75 EndZ=0
    g30: LineSegment StartX=-49.19 StartY=52 StartZ=0 EndX=-11.49 EndY=52 EndZ=0
    g31: LineSegment StartX=-49.19 StartY=49 StartZ=0 EndX=-11.49 EndY=49 EndZ=0
    g32: LineSegment StartX=-49.19 StartY=46.25 StartZ=0 EndX=-16.28 EndY=46.25 EndZ=0
    g33: LineSegment StartX=-49.19 StartY=43.25 StartZ=0 EndX=-16.28 EndY=43.25 EndZ=0
    g34: LineSegment StartX=-49.19 StartY=40.5 StartZ=0 EndX=-18.2337 EndY=40.5 EndZ=0
    g35: LineSegment StartX=-49.19 StartY=37.5 StartZ=0 EndX=-18.23 EndY=37.5 EndZ=0
    g36: LineSegment StartX=-49.19 StartY=34.5 StartZ=0 EndX=-18.2337 EndY=34.5 EndZ=0
    g37: LineSegment StartX=-49.19 StartY=31.5 StartZ=0 EndX=-18.23 EndY=31.5 EndZ=0
    g38: LineSegment StartX=-49.19 StartY=28.75 StartZ=0 EndX=-16.2837 EndY=28.75 EndZ=0
    g39: LineSegment StartX=-49.19 StartY=25.75 StartZ=0 EndX=-16.28 EndY=25.75 EndZ=0
    g40: LineSegment StartX=-49.19 StartY=23 StartZ=0 EndX=-11.49 EndY=23 EndZ=0
    g41: LineSegment StartX=-49.19 StartY=20 StartZ=0 EndX=-11.49 EndY=20 EndZ=0
    g42: LineSegment StartX=-49.19 StartY=17.25 StartZ=0 EndX=-1.5 EndY=17.25 EndZ=0
    g43: LineSegment StartX=-49.19 StartY=14.25 StartZ=0 EndX=-1.5 EndY=14.25 EndZ=0
    g44: LineSegment StartX=-49.19 StartY=11.5 StartZ=0 EndX=-1.5 EndY=11.5 EndZ=0
    g45: LineSegment StartX=-49.19 StartY=8.5 StartZ=0 EndX=-1.5 EndY=8.5 EndZ=0
    g46: LineSegment StartX=-49.19 StartY=5.75 StartZ=0 EndX=-1.5 EndY=5.75 EndZ=0
    g47: LineSegment StartX=-49.19 StartY=2.75 StartZ=0 EndX=-1.5 EndY=2.75 EndZ=0
  constraints (120):
    c: Vertical(g0)
    c: Distance(g0) = 3
    c: Block(g0)
    c: Vertical(g1)
    c: Distance(g1) = 3
    c: Vertical(g2)
    c: Equal(g0,g2) = 3
    c: Block(g2)
    c: Vertical(g3)
    c: Equal(g1,g3) = 3
    c: Vertical(g4)
    c: Equal(g0,g4) = 3
    c: Block(g4)
    c: Vertical(g5)
    c: Equal(g1,g5) = 3
    c: Vertical(g6)
    c: Equal(g0,g6) = 3
    c: Block(g6)
    c: Vertical(g7)
    c: Equal(g1,g7) = 3
    c: Vertical(g8)
    c: Equal(g0,g8) = 3
    c: Block(g8)
    c: Vertical(g9)
    c: Equal(g1,g9) = 3
    c: Vertical(g10)
    c: Equal(g0,g10) = 3
    c: Block(g10)
    c: Vertical(g11)
    c: Equal(g1,g11) = 3
    c: Block(g12)
    c: Block(g13)
    c: Block(g14)
    c: Block(g15)
    c: Block(g16)
    c: Block(g17)
    c: Block(g18)
    c: Block(g19)
    c: Block(g20)
    c: Block(g21)
    c: Block(g22)
    c: Block(g23)
    c: Block(g11)
    c: Block(g9)
    c: Block(g7)
    c: Block(g5)
    c: Block(g3)
    c: Block(g1)
    c: Coincident(g24,g0)
    c: Coincident(g24,g12)
    c: Horizontal(g24)
    c: Coincident(g25,g0)
    c: Coincident(g25,g12)
    c: Horizontal(g25)
    c: Coincident(g26,g1)
    c: Coincident(g26,g13)
    c: Horizontal(g26)
    c: Coincident(g27,g1)
    c: Coincident(g27,g13)
    c: Horizontal(g27)
    c: Coincident(g28,g2)
    c: Coincident(g28,g14)
    c: Horizontal(g28)
    c: Coincident(g29,g2)
    c: Coincident(g29,g14)
    c: Horizontal(g29)
    c: Coincident(g30,g3)
    c: Coincident(g30,g15)
    c: Horizontal(g30)
    c: Coincident(g31,g3)
    c: Coincident(g31,g15)
    c: Horizontal(g31)
    c: Coincident(g32,g4)
    c: Coincident(g32,g16)
    c: Horizontal(g32)
    c: Coincident(g33,g4)
    c: Coincident(g33,g16)
    c: Horizontal(g33)
    c: Coincident(g34,g5)
    c: Coincident(g34,g17)
    c: Horizontal(g34)
    c: Coincident(g35,g5)
    c: Coincident(g35,g17)
    c: Horizontal(g35)
    c: Coincident(g36,g6)
    c: Coincident(g36,g19)
    c: Horizontal(g36)
    c: Coincident(g37,g6)
    c: Coincident(g37,g19)
    c: Horizontal(g37)
    c: Coincident(g38,g7)
    c: Coincident(g38,g18)
    c: Horizontal(g38)
    c: Coincident(g39,g7)
    c: Coincident(g39,g18)
    c: Horizontal(g39)
    c: Coincident(g40,g8)
    c: Coincident(g40,g20)
    c: Horizontal(g40)
    c: Coincident(g41,g8)
    c: Coincident(g41,g20)
    c: Horizontal(g41)
    c: Coincident(g42,g9)
    c: Coincident(g42,g23)
    c: Horizontal(g42)
    c: Coincident(g43,g9)
    c: Coincident(g43,g23)
    c: Horizontal(g43)
    c: Coincident(g44,g10)
    c: Coincident(g44,g22)
    c: Horizontal(g44)
    c: Coincident(g45,g10)
    c: Coincident(g45,g22)
    c: Horizontal(g45)
    c: Coincident(g46,g11)
    c: Coincident(g46,g21)
    c: Horizontal(g46)
    c: Coincident(g47,g11)
    c: Coincident(g47,g21)
    c: Horizontal(g47)
FEATURE [Part::Extrusion] Extrude065
  Base = -> Sketch074
  Dir = (1,0,0)
  DirMode = 2
  FaceMakerClass = Part::FaceMakerBullseye
  LengthFwd = 23
  LengthRev = 0
  Placement = pos=(-19,0,0) rot=(0,0,1;0rad)
  Solid = true
  Symmetric = false
FEATURE [Part::Fillet] Fillet056  label="removeToCreateVentalationHoles003"
  Base = -> Extrude065
  Edges = <same value as first occurrence — deduplicated (x6 in doc)>
  Placement = pos=(7,0.02,0) rot=(0,0,1;0rad)
FEATURE [Part::Revolution] Revolve158  label="removeToCreateScrewAndThreadedInsertHole065"
  Angle = 360
  Axis = (0,1,0)
  Base = (0,0,0)
  FaceMakerClass = Part::FaceMakerBullseye
  Placement = pos=(12.5,0,62) rot=(0,0,1;0rad)
  Solid = false
  Source = -> Face146
  Symmetric = false
FEATURE [Part::Revolution] Revolve159  label="removeToCreateScrewAndThreadedInsertHole066"
  Angle = 360
  Axis = (0,1,0)
  Base = (0,0,0)
  FaceMakerClass = Part::FaceMakerBullseye
  Placement = pos=(89.5,0,68.5) rot=(0,0,1;0rad)
  Solid = false
  Source = -> Face143
  Symmetric = false
FEATURE [Part::Revolution] Revolve160  label="removeToCreateScrewAndThreadedInsertHole067"
  Angle = 360
  Axis = (0,1,0)
  Base = (0,0,0)
  FaceMakerClass = Part::FaceMakerBullseye
  Placement = pos=(89.5,0,3.5) rot=(0,0,1;0rad)
  Solid = false
  Source = -> Face142
  Symmetric = false
FEATURE [Part::Revolution] Revolve161  label="removeToCreateScrewAndThreadedInsertHole068"
  Angle = 360
  Axis = (0,1,0)
  Base = (0,0,0)
  FaceMakerClass = Part::FaceMakerBullseye
  Placement = pos=(109.5,4.7,3.5) rot=(0,0,1;0rad)
  Solid = false
  Source = -> Face145
  Symmetric = false
FEATURE [Part::Revolution] Revolve162  label="removeToCreateScrewAndThreadedInsertHole069"
  Angle = 360
  Axis = (0,1,0)
  Base = (0,0,0)
  FaceMakerClass = Part::FaceMakerBullseye
  Placement = pos=(109.5,4.7,68.5) rot=(0,0,1;0rad)
  Solid = false
  Source = -> Face144
  Symmetric = false
FEATURE [Part::MultiFuse] Fusion141  label="removeToCreateScrewAndThreadedInsertHole064"
  Shapes = -> [Revolve162,Revolve161,Revolve160,Revolve159,Revolve158,Revolve157]
FEATURE [Part::Cylinder] Cylinder062
  Angle = 360
  AttacherType = Attacher::AttachEngine3D
  Height = 20
  Placement = pos=(0,0,36.15) rot=(0,0,1;0rad)
  Radius = 14
FEATURE [Part::Cylinder] Cylinder063
  Angle = 360
  AttacherType = Attacher::AttachEngine3D
  Height = 10
  Placement = pos=(0,0,36.15) rot=(0,0,1;0rad)
  Radius = 4
FEATURE [Part::MultiFuse] Fusion139  label="removeToCreteHoleForPlugHousing052"
  Placement = pos=(70,19,36) rot=(0,1,0;1.5708rad)
  Shapes = -> [Cylinder062,Cylinder063]
FEATURE [Part::Cut] Cut060  label="bottom017"
  Base = -> Extrude064
  Tool = -> Fusion139
FEATURE [Part::Cut] Cut061  label="bottom019"
  Base = -> Cut060
  Tool = -> Fusion141
FEATURE [Part::MultiFuse] Fusion140  label="bottom018"
  Shapes = -> [Cut061,Cut058]
FEATURE [Part::Cut] Cut059  label="bottom020"
  Base = -> Fusion140
  Tool = -> Fillet056
FEATURE [Part::Box] Box036  label="Cube021"
  AttacherType = Attacher::AttachEngine3D
  Height = 80
  Length = 26
  Placement = pos=(0,-1,-5) rot=(0,0,1;0rad)
  Width = 11
FEATURE [Part::Cut] Cut062  label="removeFromBottom002"
  Base = -> Cut057
  Tool = -> Box036
FEATURE [Part::Cut] Cut063
  Base = -> Cut059
  Tool = -> Cut062
FEATURE [Part::Cut] Cut064  label="pcbStands"
  Base = -> Fusion095
  Tool = -> Fusion127
FEATURE [Sketcher::SketchObject] Sketch075  label="topSketch022"
  FullyConstrained = true
  sketch-geometry (6):
    g0: LineSegment StartX=19 StartY=38 StartZ=0 EndX=117 EndY=38 EndZ=0
    g1: ArcOfCircle CenterX=19 CenterY=19 CenterZ=0 NormalX=0 NormalY=0 NormalZ=1 AngleXU=0 Radius=19 StartAngle=1.5708 EndAngle=3.14159
    g2: LineSegment StartX=117 StartY=38 StartZ=0 EndX=117 EndY=19 EndZ=0
    g3: LineSegment StartX=98 StartY=1.0161e-12 StartZ=0 EndX=5.22862e-06 EndY=1.0161e-12 EndZ=0
    g4: LineSegment StartX=5.22862e-06 StartY=19 StartZ=0 EndX=5.22862e-06 EndY=1.0161e-12 EndZ=0
    g5: ArcOfCircle CenterX=98 CenterY=19 CenterZ=0 NormalX=0 NormalY=0 NormalZ=1 AngleXU=0 Radius=19 StartAngle=4.71239 EndAngle=6.28319
  constraints (16):
    c: Horizontal(g0)
    c: Distance(g0) = 98
    c: Coincident(g1,g0)
    c: Block(g1)
    c: Coincident(g2,g0)
    c: Vertical(g2)
    c: Distance(g2) = 19
    c: Horizontal(g3)
    c: Coincident(g4,g1)
    c: Vertical(g4)
    c: Coincident(g3,g4)
    c: Block(g3)
    c: Coincident(g5,g2)
    c: Coincident(g5,g3)
    c: Block(g0)
    c: Block(g5)
FEATURE [Part::Extrusion] Extrude067  label="sideB003"
  Base = -> Sketch075
  Dir = (0,0,1)
  DirMode = 2
  FaceMakerClass = Part::FaceMakerBullseye
  LengthFwd = 3
  LengthRev = 0
  Placement = pos=(0,0,71.7) rot=(0,0,1;0rad)
  Solid = true
  Symmetric = false
FEATURE [Sketcher::SketchObject] Sketch076  label="topSketch023"
  FullyConstrained = true
  sketch-geometry (6):
    g0: LineSegment StartX=19 StartY=38 StartZ=0 EndX=117 EndY=38 EndZ=0
    g1: ArcOfCircle CenterX=19 CenterY=19 CenterZ=0 NormalX=0 NormalY=0 NormalZ=1 AngleXU=0 Radius=19 StartAngle=1.5708 EndAngle=3.14159
    g2: LineSegment StartX=117 StartY=38 StartZ=0 EndX=117 EndY=19 EndZ=0
    g3: LineSegment StartX=98 StartY=1.0161e-12 StartZ=0 EndX=5.22862e-06 EndY=1.0161e-12 EndZ=0
    g4: LineSegment StartX=5.22862e-06 StartY=19 StartZ=0 EndX=5.22862e-06 EndY=1.0161e-12 EndZ=0
    g5: ArcOfCircle CenterX=98 CenterY=19 CenterZ=0 NormalX=0 NormalY=0 NormalZ=1 AngleXU=0 Radius=19 StartAngle=4.71239 EndAngle=6.28319
  constraints (16):
    c: Horizontal(g0)
    c: Distance(g0) = 98
    c: Coincident(g1,g0)
    c: Block(g1)
    c: Coincident(g2,g0)
    c: Vertical(g2)
    c: Distance(g2) = 19
    c: Horizontal(g3)
    c: Coincident(g4,g1)
    c: Vertical(g4)
    c: Coincident(g3,g4)
    c: Block(g3)
    c: Coincident(g5,g2)
    c: Coincident(g5,g3)
    c: Block(g0)
    c: Block(g5)
FEATURE [Part::Extrusion] Extrude066  label="sideA003"
  Base = -> Sketch076
  Dir = (0,0,1)
  DirMode = 2
  FaceMakerClass = Part::FaceMakerBullseye
  LengthFwd = 3
  LengthRev = 0
  Placement = pos=(0,0,-2.7) rot=(0,0,1;0rad)
  Solid = true
  Symmetric = false
FEATURE [Part::MultiFuse] Fusion142  label="removeFromBottom003"
  Placement = pos=(2,0,0) rot=(0,0,1;0rad)
  Shapes = -> [Extrude066,Extrude067]
FEATURE [Part::Cut] Cut065  label="screwRetainers002"
  Base = -> Fusion096
  Tool = -> Fusion142
FEATURE [Sketcher::SketchObject] Sketch077
  FullyConstrained = true
  Placement = pos=(117,19,0) rot=(0.57735,0.57735,0.57735;2.0944rad)
  sketch-geometry (8):
    g0: LineSegment StartX=-49.19 StartY=63.5 StartZ=0 EndX=-49.19 EndY=60.5 EndZ=0
    g1: LineSegment StartX=-49.19 StartY=11.5 StartZ=0 EndX=-49.19 EndY=8.5 EndZ=0
    g2: ArcOfCircle CenterX=-1.5 CenterY=62 CenterZ=0 NormalX=0 NormalY=0 NormalZ=1 AngleXU=0 Radius=1.5 StartAngle=4.71239 EndAngle=7.85398
    g3: ArcOfCircle CenterX=-1.5 CenterY=10 CenterZ=0 NormalX=0 NormalY=0 NormalZ=1 AngleXU=0 Radius=1.5 StartAngle=4.71239 EndAngle=7.85398
    g4: LineSegment StartX=-49.19 StartY=63.5 StartZ=0 EndX=-1.5 EndY=63.5 EndZ=0
    g5: LineSegment StartX=-49.19 StartY=60.5 StartZ=0 EndX=-1.5 EndY=60.5 EndZ=0
    g6: LineSegment StartX=-49.19 StartY=11.5 StartZ=0 EndX=-1.5 EndY=11.5 EndZ=0
    g7: LineSegment StartX=-49.19 StartY=8.5 StartZ=0 EndX=-1.5 EndY=8.5 EndZ=0
  constraints (19):
    c: Vertical(g0)
    c: Distance(g0) = 3
    c: Vertical(g1)
    c: Block(g1)
    c: Block(g2)
    c: Block(g3)
    c: Block(g0)
    c: Coincident(g4,g0)
    c: Coincident(g4,g2)
    c: Horizontal(g4)
    c: Coincident(g5,g0)
    c: Coincident(g5,g2)
    c: Horizontal(g5)
    c: Coincident(g6,g1)
    c: Coincident(g6,g3)
    c: Horizontal(g6)
    c: Coincident(g7,g1)
    c: Coincident(g7,g3)
    c: Horizontal(g7)
FEATURE [Part::Extrusion] Extrude068
  Base = -> Sketch077
  Dir = (1,0,0)
  DirMode = 2
  FaceMakerClass = Part::FaceMakerBullseye
  LengthFwd = 10
  LengthRev = 0
  Solid = true
  Symmetric = false
FEATURE [Part::Fillet] Fillet057  label="removeFromtMoreFrontCaseScrewRetainers002"
  Base = -> Extrude068
  Edges = 4 edges r=1.49: [Edge6,Edge11,Edge18,Edge23]
  Placement = pos=(-12,0,0) rot=(0,0,1;0rad)
FEATURE [Sketcher::SketchObject] Sketch078
  FullyConstrained = true
  Placement = pos=(117,19,0) rot=(0.57735,0.57735,0.57735;2.0944rad)
  sketch-geometry (8):
    g0: LineSegment StartX=-49.19 StartY=69.25 StartZ=0 EndX=-49.19 EndY=66.25 EndZ=0
    g1: LineSegment StartX=-49.19 StartY=5.75 StartZ=0 EndX=-49.19 EndY=2.75 EndZ=0
    g2: ArcOfCircle CenterX=-1.5 CenterY=67.75 CenterZ=0 NormalX=0 NormalY=0 NormalZ=1 AngleXU=0 Radius=1.5 StartAngle=4.71239 EndAngle=7.85398
    g3: ArcOfCircle CenterX=-1.5 CenterY=4.25 CenterZ=0 NormalX=0 NormalY=0 NormalZ=1 AngleXU=0 Radius=1.5 StartAngle=4.71239 EndAngle=7.85398
    g4: LineSegment StartX=-49.19 StartY=69.25 StartZ=0 EndX=-1.5 EndY=69.25 EndZ=0
    g5: LineSegment StartX=-49.19 StartY=66.25 StartZ=0 EndX=-1.5 EndY=66.25 EndZ=0
    g6: LineSegment StartX=-49.19 StartY=5.75 StartZ=0 EndX=-1.5 EndY=5.75 EndZ=0
    g7: LineSegment StartX=-49.19 StartY=2.75 StartZ=0 EndX=-1.5 EndY=2.75 EndZ=0
  constraints (19):
    c: Vertical(g0)
    c: Distance(g0) = 3
    c: Block(g0)
    c: Vertical(g1)
    c: Block(g2)
    c: Block(g3)
    c: Block(g1)
    c: Coincident(g4,g0)
    c: Coincident(g4,g2)
    c: Horizontal(g4)
    c: Coincident(g5,g0)
    c: Coincident(g5,g2)
    c: Horizontal(g5)
    c: Coincident(g6,g1)
    c: Coincident(g6,g3)
    c: Horizontal(g6)
    c: Coincident(g7,g1)
    c: Coincident(g7,g3)
    c: Horizontal(g7)
FEATURE [Part::Extrusion] Extrude069
  Base = -> Sketch078
  Dir = (1,0,0)
  DirMode = 2
  FaceMakerClass = Part::FaceMakerBullseye
  LengthFwd = 10
  LengthRev = 0
  Solid = true
  Symmetric = false
FEATURE [Part::Fillet] Fillet058  label="removeFromtMoreFrontCaseScrewRetainers003"
  Base = -> Extrude069
  Edges = 4 edges r=1.49: [Edge6,Edge11,Edge18,Edge23]
  Placement = pos=(-4,0,0) rot=(0,0,1;0rad)
FEATURE [Part::Cut] Cut066
  Base = -> Cut065
  Tool = -> Fillet058
FEATURE [Part::Cut] Cut067  label="screwPillars"
  Base = -> Cut066
  Tool = -> Fillet057
FEATURE [Part::MultiFuse] Fusion143  label="bottom021"
  Shapes = -> [Cut031,Cut063]
FEATURE [Part::Cylinder] Cylinder
  Angle = 360
  AttacherType = Attacher::AttachEngine3D
  Height = 10
  Placement = pos=(20.65,12,4.68) rot=(1,0,0;1.5708rad)
  Radius = 2
FEATURE [Part::Cylinder] Cylinder064
  Angle = 360
  AttacherType = Attacher::AttachEngine3D
  Height = 10
  Placement = pos=(20.65,12,67.38) rot=(1,0,0;1.5708rad)
  Radius = 2
FEATURE [Part::Cylinder] Cylinder065
  Angle = 360
  AttacherType = Attacher::AttachEngine3D
  Height = 10
  Placement = pos=(77.15,12,67.38) rot=(1,0,0;1.5708rad)
  Radius = 2
FEATURE [Part::Cylinder] Cylinder066
  Angle = 360
  AttacherType = Attacher::AttachEngine3D
  Height = 10
  Placement = pos=(77.15,12,4.68) rot=(1,0,0;1.5708rad)
  Radius = 2
FEATURE [Part::MultiFuse] Fusion144  label="removeFromThreadedInsertHousing"
  Shapes = -> [Cylinder065,Cylinder064,Cylinder,Cylinder066]
FEATURE [Part::Cut] Cut068  label="pcbStands001"
  Base = -> Cut064
  Tool = -> Fusion144
FEATURE [Part::MultiFuse] Fusion145
  Shapes = -> [Cut068,Fusion143]
FEATURE [Part::MultiFuse] Fusion146
  Shapes = -> [Fusion145]
FEATURE [Part::MultiFuse] Fusion147  label="bottom022"
  Shapes = -> [Cut067,Fusion146]
FEATURE [Part::MultiFuse] Fusion148  label="casePillars005"
  Shapes = -> [Cut047,Fusion092]
FEATURE [Part::MultiFuse] Fusion149  label="bottom023"
  Shapes = -> [Fusion124,Fusion113,Fusion147]
FEATURE [Part::MultiFuse] Fusion150  label="topBits"
  Shapes = -> [Cut025,Fusion148,Cut030,Fillet034]
FEATURE [Part::Feature] Face149 .. Face152  x4 (patterned run collapsed; names and placements below)
  shape: bbox 3.2 x 1.5 x 2e-07 mm, 1 faces, 0 solids (baked)
FEATURE [Part::Feature] Face153
  shape: bbox 3.6 x 3.2 x 2e-07 mm, 1 faces, 0 solids (baked)
FEATURE [Part::Feature] Face154
  shape: bbox 3.6 x 3.2 x 2e-07 mm, 1 faces, 0 solids (baked)
FEATURE [Sketcher::SketchObject] Sketch079  label="topSketch024"
  FullyConstrained = true
  sketch-geometry (6):
    g0: LineSegment StartX=19 StartY=38 StartZ=0 EndX=117 EndY=38 EndZ=0
    g1: ArcOfCircle CenterX=19 CenterY=19 CenterZ=0 NormalX=0 NormalY=0 NormalZ=1 AngleXU=0 Radius=19 StartAngle=1.5708 EndAngle=3.14159
    g2: LineSegment StartX=117 StartY=38 StartZ=0 EndX=117 EndY=19 EndZ=0
    g3: LineSegment StartX=98 StartY=1.0161e-12 StartZ=0 EndX=5.22862e-06 EndY=1.0161e-12 EndZ=0
    g4: LineSegment StartX=5.22862e-06 StartY=19 StartZ=0 EndX=5.22862e-06 EndY=1.0161e-12 EndZ=0
    g5: ArcOfCircle CenterX=98 CenterY=19 CenterZ=0 NormalX=0 NormalY=0 NormalZ=1 AngleXU=0 Radius=19 StartAngle=4.71239 EndAngle=6.28319
  constraints (16):
    c: Horizontal(g0)
    c: Distance(g0) = 98
    c: Coincident(g1,g0)
    c: Block(g1)
    c: Coincident(g2,g0)
    c: Vertical(g2)
    c: Distance(g2) = 19
    c: Horizontal(g3)
    c: Coincident(g4,g1)
    c: Vertical(g4)
    c: Coincident(g3,g4)
    c: Block(g3)
    c: Coincident(g5,g2)
    c: Coincident(g5,g3)
    c: Block(g0)
    c: Block(g5)
FEATURE [Sketcher::SketchObject] Sketch080  label="topSketch025"
  FullyConstrained = true
  sketch-geometry (6):
    g0: LineSegment StartX=19 StartY=38 StartZ=0 EndX=117 EndY=38 EndZ=0
    g1: ArcOfCircle CenterX=19 CenterY=19 CenterZ=0 NormalX=0 NormalY=0 NormalZ=1 AngleXU=0 Radius=19 StartAngle=1.5708 EndAngle=3.14159
    g2: LineSegment StartX=117 StartY=38 StartZ=0 EndX=117 EndY=19 EndZ=0
    g3: LineSegment StartX=98 StartY=1.0161e-12 StartZ=0 EndX=5.22862e-06 EndY=1.0161e-12 EndZ=0
    g4: LineSegment StartX=5.22862e-06 StartY=19 StartZ=0 EndX=5.22862e-06 EndY=1.0161e-12 EndZ=0
    g5: ArcOfCircle CenterX=98 CenterY=19 CenterZ=0 NormalX=0 NormalY=0 NormalZ=1 AngleXU=0 Radius=19 StartAngle=4.71239 EndAngle=6.28319
  constraints (16):
    c: Horizontal(g0)
    c: Distance(g0) = 98
    c: Coincident(g1,g0)
    c: Block(g1)
    c: Coincident(g2,g0)
    c: Vertical(g2)
    c: Distance(g2) = 19
    c: Horizontal(g3)
    c: Coincident(g4,g1)
    c: Vertical(g4)
    c: Coincident(g3,g4)
    c: Block(g3)
    c: Coincident(g5,g2)
    c: Coincident(g5,g3)
    c: Block(g0)
    c: Block(g5)
FEATURE [Part::Extrusion] Extrude070  label="sideA004"
  Base = -> Sketch080
  Dir = (0,0,1)
  DirMode = 2
  FaceMakerClass = Part::FaceMakerBullseye
  LengthFwd = 3
  LengthRev = 0
  Placement = pos=(0,0,-2.7) rot=(0,0,1;0rad)
  Solid = true
  Symmetric = false
FEATURE [Sketcher::SketchObject] Sketch081
  FullyConstrained = true
  Placement = pos=(117,19,0) rot=(0.57735,0.57735,0.57735;2.0944rad)
  sketch-geometry (8):
    g0: LineSegment StartX=-49.19 StartY=63.5 StartZ=0 EndX=-49.19 EndY=60.5 EndZ=0
    g1: LineSegment StartX=-49.19 StartY=11.5 StartZ=0 EndX=-49.19 EndY=8.5 EndZ=0
    g2: ArcOfCircle CenterX=-1.5 CenterY=62 CenterZ=0 NormalX=0 NormalY=0 NormalZ=1 AngleXU=0 Radius=1.5 StartAngle=4.71239 EndAngle=7.85398
    g3: ArcOfCircle CenterX=-1.5 CenterY=10 CenterZ=0 NormalX=0 NormalY=0 NormalZ=1 AngleXU=0 Radius=1.5 StartAngle=4.71239 EndAngle=7.85398
    g4: LineSegment StartX=-49.19 StartY=63.5 StartZ=0 EndX=-1.5 EndY=63.5 EndZ=0
    g5: LineSegment StartX=-49.19 StartY=60.5 StartZ=0 EndX=-1.5 EndY=60.5 EndZ=0
    g6: LineSegment StartX=-49.19 StartY=11.5 StartZ=0 EndX=-1.5 EndY=11.5 EndZ=0
    g7: LineSegment StartX=-49.19 StartY=8.5 StartZ=0 EndX=-1.5 EndY=8.5 EndZ=0
  constraints (19):
    c: Vertical(g0)
    c: Distance(g0) = 3
    c: Vertical(g1)
    c: Block(g1)
    c: Block(g2)
    c: Block(g3)
    c: Block(g0)
    c: Coincident(g4,g0)
    c: Coincident(g4,g2)
    c: Horizontal(g4)
    c: Coincident(g5,g0)
    c: Coincident(g5,g2)
    c: Horizontal(g5)
    c: Coincident(g6,g1)
    c: Coincident(g6,g3)
    c: Horizontal(g6)
    c: Coincident(g7,g1)
    c: Coincident(g7,g3)
    c: Horizontal(g7)
FEATURE [Part::Extrusion] Extrude071  label="sideB004"
  Base = -> Sketch079
  Dir = (0,0,1)
  DirMode = 2
  FaceMakerClass = Part::FaceMakerBullseye
  LengthFwd = 3
  LengthRev = 0
  Placement = pos=(0,0,71.7) rot=(0,0,1;0rad)
  Solid = true
  Symmetric = false
FEATURE [Part::MultiFuse] Fusion152  label="removeFromBottom004"
  Placement = pos=(2,0,0) rot=(0,0,1;0rad)
  Shapes = -> [Extrude070,Extrude071]
FEATURE [Part::Extrusion] Extrude072
  Base = -> Sketch081
  Dir = (1,0,0)
  DirMode = 2
  FaceMakerClass = Part::FaceMakerBullseye
  LengthFwd = 10
  LengthRev = 0
  Solid = true
  Symmetric = false
FEATURE [Part::Fillet] Fillet059  label="removeFromtMoreFrontCaseScrewRetainers004"
  Base = -> Extrude072
  Edges = 4 edges r=1.49: [Edge6,Edge11,Edge18,Edge23]
  Placement = pos=(-12,0,0) rot=(0,0,1;0rad)
FEATURE [Sketcher::SketchObject] Sketch082
  FullyConstrained = true
  Placement = pos=(117,19,0) rot=(0.57735,0.57735,0.57735;2.0944rad)
  sketch-geometry (8):
    g0: LineSegment StartX=-49.19 StartY=69.25 StartZ=0 EndX=-49.19 EndY=66.25 EndZ=0
    g1: LineSegment StartX=-49.19 StartY=5.75 StartZ=0 EndX=-49.19 EndY=2.75 EndZ=0
    g2: ArcOfCircle CenterX=-1.5 CenterY=67.75 CenterZ=0 NormalX=0 NormalY=0 NormalZ=1 AngleXU=0 Radius=1.5 StartAngle=4.71239 EndAngle=7.85398
    g3: ArcOfCircle CenterX=-1.5 CenterY=4.25 CenterZ=0 NormalX=0 NormalY=0 NormalZ=1 AngleXU=0 Radius=1.5 StartAngle=4.71239 EndAngle=7.85398
    g4: LineSegment StartX=-49.19 StartY=69.25 StartZ=0 EndX=-1.5 EndY=69.25 EndZ=0
    g5: LineSegment StartX=-49.19 StartY=66.25 StartZ=0 EndX=-1.5 EndY=66.25 EndZ=0
    g6: LineSegment StartX=-49.19 StartY=5.75 StartZ=0 EndX=-1.5 EndY=5.75 EndZ=0
    g7: LineSegment StartX=-49.19 StartY=2.75 StartZ=0 EndX=-1.5 EndY=2.75 EndZ=0
  constraints (19):
    c: Vertical(g0)
    c: Distance(g0) = 3
    c: Block(g0)
    c: Vertical(g1)
    c: Block(g2)
    c: Block(g3)
    c: Block(g1)
    c: Coincident(g4,g0)
    c: Coincident(g4,g2)
    c: Horizontal(g4)
    c: Coincident(g5,g0)
    c: Coincident(g5,g2)
    c: Horizontal(g5)
    c: Coincident(g6,g1)
    c: Coincident(g6,g3)
    c: Horizontal(g6)
    c: Coincident(g7,g1)
    c: Coincident(g7,g3)
    c: Horizontal(g7)
FEATURE [Part::Extrusion] Extrude073
  Base = -> Sketch082
  Dir = (1,0,0)
  DirMode = 2
  FaceMakerClass = Part::FaceMakerBullseye
  LengthFwd = 10
  LengthRev = 0
  Solid = true
  Symmetric = false
FEATURE [Part::Fillet] Fillet060  label="removeFromtMoreFrontCaseScrewRetainers005"
  Base = -> Extrude073
  Edges = 4 edges r=1.49: [Edge6,Edge11,Edge18,Edge23]
  Placement = pos=(-4,0,0) rot=(0,0,1;0rad)
FEATURE [Part::Revolution] Revolve163  label="backCaseScrewRetainer004"
  Angle = 360
  Axis = (0,1,0)
  Base = (0,0,0)
  FaceMakerClass = Part::FaceMakerBullseye
  Placement = pos=(12.5,3,62) rot=(0,0,1;0rad)
  Solid = false
  Source = -> Face149
  Symmetric = false
FEATURE [Part::Revolution] Revolve164  label="frontCaseScrewRetainer006"
  Angle = 360
  Axis = (0,1,0)
  Base = (0,0,0)
  FaceMakerClass = Part::FaceMakerBullseye
  Placement = pos=(89.5,3,68.5) rot=(0,0,1;0rad)
  Solid = false
  Source = -> Face151
  Symmetric = false
FEATURE [Part::Revolution] Revolve165  label="frontCaseScrewRetainer007"
  Angle = 360
  Axis = (0,1,0)
  Base = (0,0,0)
  FaceMakerClass = Part::FaceMakerBullseye
  Placement = pos=(89.5,3,3.5) rot=(0,0,1;0rad)
  Solid = false
  Source = -> Face152
  Symmetric = false
FEATURE [Part::Revolution] Revolve166  label="backCaseScrewRetainer005"
  Angle = 360
  Axis = (0,1,0)
  Base = (0,0,0)
  FaceMakerClass = Part::FaceMakerBullseye
  Placement = pos=(12.5,3,10) rot=(0,0,1;0rad)
  Solid = false
  Source = -> Face150
  Symmetric = false
FEATURE [Part::Revolution] Revolve167  label="moreFrontCaseScrewRetainer006"
  Angle = 360
  Axis = (0,1,0)
  Base = (0,0,0)
  FaceMakerClass = Part::FaceMakerBullseye
  Placement = pos=(109.5,4.5,68.5) rot=(0,0,1;0rad)
  Solid = false
  Source = -> Face153
  Symmetric = false
FEATURE [Part::Revolution] Revolve168  label="moreFrontCaseScrewRetainer007"
  Angle = 360
  Axis = (0,1,0)
  Base = (0,0,0)
  FaceMakerClass = Part::FaceMakerBullseye
  Placement = pos=(109.5,4.5,3.5) rot=(0,0,1;0rad)
  Solid = false
  Source = -> Face154
  Symmetric = false
FEATURE [Part::MultiFuse] Fusion151  label="screwRetainers003"
  Shapes = -> [Revolve168,Revolve167,Revolve166,Revolve165,Revolve164,Revolve163]
FEATURE [Part::Cut] Cut069  label="screwRetainers004"
  Base = -> Fusion151
  Tool = -> Fusion152
FEATURE [Part::Cut] Cut070
  Base = -> Cut069
  Tool = -> Fillet060
FEATURE [Part::Cut] Cut071  label="screwPillars001"
  Base = -> Cut070
  Tool = -> Fillet059
FEATURE [Part::MultiFuse] Fusion153  label="bottom024"
  Shapes = -> [Fusion149,Cut071]
FEATURE [Part::Cylinder] Cylinder067
  Angle = 360
  AttacherType = Attacher::AttachEngine3D
  Height = 10
  Placement = pos=(20.65,12,4.68) rot=(1,0,0;1.5708rad)
  Radius = 2
FEATURE [Part::Cylinder] Cylinder068
  Angle = 360
  AttacherType = Attacher::AttachEngine3D
  Height = 10
  Placement = pos=(20.65,12,67.38) rot=(1,0,0;1.5708rad)
  Radius = 2
FEATURE [Part::Cylinder] Cylinder069
  Angle = 360
  AttacherType = Attacher::AttachEngine3D
  Height = 10
  Placement = pos=(77.15,12,67.38) rot=(1,0,0;1.5708rad)
  Radius = 2
FEATURE [Part::Cylinder] Cylinder070
  Angle = 360
  AttacherType = Attacher::AttachEngine3D
  Height = 10
  Placement = pos=(77.15,12,4.68) rot=(1,0,0;1.5708rad)
  Radius = 2
FEATURE [Part::MultiFuse] Fusion154  label="removeFromThreadedInsertHousing001"
  Shapes = -> [Cylinder069,Cylinder068,Cylinder067,Cylinder070]
FEATURE [Part::Cut] Cut072  label="bottom025"
  Base = -> Fusion153
  Tool = -> Fusion154
FEATURE [Image::ImagePlane] ImagePlane
  XSize = 339
  YSize = 72
FEATURE [Sketcher::SketchObject] Sketch083
  FullyConstrained = true
  MapMode = 5
  Support = -> [XY_Plane]
  sketch-geometry (338):
    g0: LineSegment StartX=-151.619 StartY=28.8932 StartZ=0 EndX=-140.819 EndY=28.8932 EndZ=0
    g1: LineSegment StartX=-151.619 StartY=24.0313 StartZ=0 EndX=-151.619 EndY=28.8932 EndZ=0
    g2: LineSegment StartX=-140.819 StartY=17.7713 StartZ=0 EndX=-151.619 EndY=17.7713 EndZ=0
    g3: LineSegment StartX=-151.619 StartY=17.7713 StartZ=0 EndX=-151.619 EndY=22.6313 EndZ=0
    g4: LineSegment StartX=-151.619 StartY=22.6313 StartZ=0 EndX=-145.128 EndY=22.6313 EndZ=0
    g5: LineSegment StartX=-145.128 StartY=24.0313 StartZ=0 EndX=-140.819 EndY=28.8932 EndZ=0
    g6: LineSegment StartX=-145.128 StartY=22.6313 StartZ=0 EndX=-140.819 EndY=17.7713 EndZ=0
    g7: ArcOfCircle CenterX=-155.157 CenterY=23.3323 CenterZ=0 NormalX=0 NormalY=0 NormalZ=1 AngleXU=0 Radius=6.92354 StartAngle=1.03434 EndAngle=5.24885
    g8: ArcOfCircle CenterX=-155.157 CenterY=23.3323 CenterZ=0 NormalX=0 NormalY=0 NormalZ=1 AngleXU=0 Radius=12.6269 StartAngle=1.28675 EndAngle=4.99643
    g9: LineSegment StartX=-151.619 StartY=35.4532 StartZ=0 EndX=-151.619 EndY=29.2832 EndZ=0
    g10: LineSegment StartX=-151.619 StartY=17.3813 StartZ=0 EndX=-151.619 EndY=11.2113 EndZ=0
    g11-g21: Circle x11 (B-spline internal-alignment scaffolding for g22; pole/knot coordinates omitted)
    g22: BSplineCurve PolesCount=11 KnotsCount=9 Degree=3 IsPeriodic=0
    g23-g31: GeomPoint x9 (B-spline internal-alignment scaffolding for g22; pole/knot coordinates omitted)
    g32-g49: Circle x18 (B-spline internal-alignment scaffolding for g50; pole/knot coordinates omitted)
    g50: BSplineCurve PolesCount=18 KnotsCount=16 Degree=3 IsPeriodic=0
    g51-g66: GeomPoint x16 (B-spline internal-alignment scaffolding for g50; pole/knot coordinates omitted)
    g67: LineSegment StartX=-117.124 StartY=30.093 StartZ=0 EndX=-117.603 EndY=26.5272 EndZ=0
    g68: LineSegment StartX=-117.603 StartY=17.8472 StartZ=0 EndX=-117.124 EndY=14.2659 EndZ=0
    g69: Ellipse CenterX=-109.671 CenterY=20.025 CenterZ=0 NormalX=0 NormalY=0 NormalZ=1 MajorRadius=3.34798 MinorRadius=2.71052 AngleXU=-1.56793
    g70: GeomPoint X=-109.666 Y=18.0598 Z=0
    g71: GeomPoint X=-109.677 Y=21.9902 Z=0
    g72: Ellipse CenterX=-109.671 CenterY=20.0123 CenterZ=0 NormalX=0 NormalY=0 NormalZ=1 MajorRadius=6.93002 MinorRadius=6.36273 AngleXU=-3.13976
    g73: GeomPoint X=-112.417 Y=20.0073 Z=0
    g74: GeomPoint X=-106.925 Y=20.0173 Z=0
    g75: Ellipse CenterX=-51.7682 CenterY=20.1463 CenterZ=0 NormalX=0 NormalY=0 NormalZ=1 MajorRadius=3.19279 MinorRadius=2.71052 AngleXU=-1.52774
    g76: GeomPoint X=-51.6955 Y=18.4606 Z=0
    g77: GeomPoint X=-51.8408 Y=21.832 Z=0
    g78: GeomPoint X=-54.5142 Y=20.1413 Z=0
    g79: GeomPoint X=-49.0221 Y=20.1513 Z=0
    g80: Ellipse CenterX=-51.7682 CenterY=20.1463 CenterZ=0 NormalX=0 NormalY=0 NormalZ=1 MajorRadius=6.93002 MinorRadius=6.36273 AngleXU=-3.13976
    g81: Ellipse CenterX=-22.8436 CenterY=20.1783 CenterZ=0 NormalX=0 NormalY=0 NormalZ=1 MajorRadius=3.31512 MinorRadius=2.71052 AngleXU=-1.60214
    g82: GeomPoint X=-22.9034 Y=18.2706 Z=0
    g83: GeomPoint X=-22.7838 Y=22.0861 Z=0
    g84: GeomPoint X=-25.5897 Y=20.1733 Z=0
    g85: GeomPoint X=-20.0976 Y=20.1833 Z=0
    g86: Ellipse CenterX=-22.8436 CenterY=20.1783 CenterZ=0 NormalX=0 NormalY=0 NormalZ=1 MajorRadius=6.93002 MinorRadius=6.36273 AngleXU=-3.13976
    g87: LineSegment StartX=-101.889 StartY=14.1107 StartZ=0 EndX=-97.7455 EndY=14.1107 EndZ=0
    g88: LineSegment StartX=-93.8155 StartY=14.1107 StartZ=0 EndX=-89.6755 EndY=14.1107 EndZ=0
    g89: LineSegment StartX=-85.7455 StartY=14.1107 StartZ=0 EndX=-81.6055 EndY=14.1107 EndZ=0
    g90: LineSegment StartX=-101.889 StartY=14.1107 StartZ=0 EndX=-101.889 EndY=25.9907 EndZ=0
    g91: LineSegment StartX=-101.889 StartY=25.9907 StartZ=0 EndX=-97.8594 EndY=25.9907 EndZ=0
    g92: LineSegment StartX=-97.8594 StartY=25.9907 StartZ=0 EndX=-97.8594 EndY=24.0907 EndZ=0
    g93: LineSegment StartX=-97.7455 StartY=14.1107 StartZ=0 EndX=-97.7455 EndY=19.9107 EndZ=0
    g94: LineSegment StartX=-89.6755 StartY=14.1107 StartZ=0 EndX=-89.6755 EndY=19.9107 EndZ=0
    g95: LineSegment StartX=-93.8155 StartY=14.1107 StartZ=0 EndX=-93.8155 EndY=21.0107 EndZ=0
    g96-g106: Circle x11 (B-spline internal-alignment scaffolding for g107; pole/knot coordinates omitted)
    g107: BSplineCurve PolesCount=11 KnotsCount=9 Degree=3 IsPeriodic=0
    g108-g116: GeomPoint x9 (B-spline internal-alignment scaffolding for g107; pole/knot coordinates omitted)
    g117: BSplineCurve PolesCount=11 KnotsCount=9 Degree=3 IsPeriodic=0
    g118-g125: Circle x8 (B-spline internal-alignment scaffolding for g126; pole/knot coordinates omitted)
    g126: BSplineCurve PolesCount=8 KnotsCount=6 Degree=3 IsPeriodic=0
    g127-g132: GeomPoint x6 (B-spline internal-alignment scaffolding for g126; pole/knot coordinates omitted)
    g133: BSplineCurve PolesCount=8 KnotsCount=6 Degree=3 IsPeriodic=0
    g134: LineSegment StartX=-85.7455 StartY=21.0107 StartZ=0 EndX=-85.7455 EndY=14.1107 EndZ=0
    g135: LineSegment StartX=-80.0879 StartY=14.1107 StartZ=0 EndX=-75.944 EndY=14.1107 EndZ=0
    g136: LineSegment StartX=-72.014 StartY=14.1107 StartZ=0 EndX=-67.874 EndY=14.1107 EndZ=0
    g137: LineSegment StartX=-63.944 StartY=14.1107 StartZ=0 EndX=-59.804 EndY=14.1107 EndZ=0
    g138: LineSegment StartX=-80.0879 StartY=14.1107 StartZ=0 EndX=-80.0879 EndY=25.9907 EndZ=0
    g139: LineSegment StartX=-80.0879 StartY=25.9907 StartZ=0 EndX=-76.0579 EndY=25.9907 EndZ=0
    g140: LineSegment StartX=-76.0579 StartY=25.9907 StartZ=0 EndX=-76.0579 EndY=24.0907 EndZ=0
    g141: LineSegment StartX=-75.944 StartY=14.1107 StartZ=0 EndX=-75.944 EndY=19.9107 EndZ=0
    g142: LineSegment StartX=-67.874 StartY=14.1107 StartZ=0 EndX=-67.874 EndY=19.9107 EndZ=0
    g143: LineSegment StartX=-72.014 StartY=14.1107 StartZ=0 EndX=-72.014 EndY=21.0107 EndZ=0
    g144-g148: Circle x5 (B-spline internal-alignment scaffolding for g149; pole/knot coordinates omitted)
    g149: BSplineCurve PolesCount=11 KnotsCount=9 Degree=3 IsPeriodic=0
    g150-g158: GeomPoint x9 (B-spline internal-alignment scaffolding for g149; pole/knot coordinates omitted)
    g159: BSplineCurve PolesCount=11 KnotsCount=9 Degree=3 IsPeriodic=0
    g160-g167: Circle x8 (B-spline internal-alignment scaffolding for g168; pole/knot coordinates omitted)
    g168: BSplineCurve PolesCount=8 KnotsCount=6 Degree=3 IsPeriodic=0
    g169-g174: GeomPoint x6 (B-spline internal-alignment scaffolding for g168; pole/knot coordinates omitted)
    g175: BSplineCurve PolesCount=8 KnotsCount=6 Degree=3 IsPeriodic=0
    g176: LineSegment StartX=-63.944 StartY=21.0107 StartZ=0 EndX=-63.944 EndY=14.1107 EndZ=0
    g177: LineSegment StartX=-59.804 StartY=14.1107 StartZ=0 EndX=-59.804 EndY=21.5868 EndZ=0
    g178: BSplineCurve PolesCount=4 KnotsCount=2 Degree=3 IsPeriodic=0
    g179: GeomPoint X=-59.804 Y=21.5868 Z=0
    g180: GeomPoint X=-60.2379 Y=24.0907 Z=0
    g181: LineSegment StartX=-81.6055 StartY=14.1107 StartZ=0 EndX=-81.6055 EndY=21.5868 EndZ=0
    g182: LineSegment StartX=-151.619 StartY=24.0313 StartZ=0 EndX=-145.128 EndY=24.0313 EndZ=0
    g183: Circle CenterX=-82.0394 CenterY=24.0907 CenterZ=0 NormalX=0 NormalY=0 NormalZ=1 AngleXU=0 Radius=1
    g184: Circle CenterX=-81.7131 CenterY=23.2736 CenterZ=0 NormalX=0 NormalY=0 NormalZ=1 AngleXU=0 Radius=1
    g185: Circle CenterX=-81.6055 CenterY=21.5868 CenterZ=0 NormalX=0 NormalY=0 NormalZ=1 AngleXU=0 Radius=1
    g186: BSplineCurve PolesCount=3 KnotsCount=2 Degree=2 IsPeriodic=0
    g187: GeomPoint X=-82.0394 Y=24.0907 Z=0
    g188: GeomPoint X=-81.6055 Y=21.5868 Z=0
    g189: Ellipse CenterX=-37.3522 CenterY=19.9515 CenterZ=0 NormalX=0 NormalY=0 NormalZ=1 MajorRadius=2.99755 MinorRadius=2.49 AngleXU=1.5708
    g190: GeomPoint X=-37.3522 Y=21.6203 Z=0
    g191: GeomPoint X=-37.3522 Y=18.2826 Z=0
    g192: ArcOfEllipse CenterX=-38.7647 CenterY=20.06 CenterZ=0 NormalX=0 NormalY=0 NormalZ=1 MajorRadius=6.30025 MinorRadius=5.3849 AngleXU=1.57276 StartAngle=5.50632 EndAngle=10.3035
    g193: GeomPoint X=-38.7711 Y=23.3304 Z=0
    g194: GeomPoint X=-38.7583 Y=16.7895 Z=0
    g195: LineSegment StartX=-34.6109 StartY=14.1107 StartZ=0 EndX=-30.8984 EndY=14.1107 EndZ=0
    g196: LineSegment StartX=-30.8984 StartY=14.1107 StartZ=0 EndX=-30.8984 EndY=31.1784 EndZ=0
    g197: LineSegment StartX=-30.8984 StartY=31.1784 StartZ=0 EndX=-34.9984 EndY=31.1784 EndZ=0
    g198: LineSegment StartX=-34.9984 StartY=24.5602 StartZ=0 EndX=-34.9984 EndY=31.1784 EndZ=0
    g199: LineSegment StartX=-34.6109 StartY=16.0476 StartZ=0 EndX=-34.6109 EndY=14.1107 EndZ=0
    g200: LineSegment StartX=-14.8781 StartY=14.1107 StartZ=0 EndX=-10.5106 EndY=14.1107 EndZ=0
    g201: LineSegment StartX=-14.8781 StartY=14.1107 StartZ=0 EndX=-14.8781 EndY=25.8504 EndZ=0
    g202: LineSegment StartX=-14.8781 StartY=25.8504 StartZ=0 EndX=-10.8534 EndY=25.8504 EndZ=0
    g203: LineSegment StartX=-10.8534 StartY=25.8504 StartZ=0 EndX=-10.8534 EndY=24.0923 EndZ=0
    g204: LineSegment StartX=-10.5106 StartY=14.1107 StartZ=0 EndX=-10.5106 EndY=19.7752 EndZ=0
    g205: LineSegment StartX=-5.96397 StartY=25.9304 StartZ=0 EndX=-5.96397 EndY=22.574 EndZ=0
    g206-g214: Circle x9 (B-spline internal-alignment scaffolding for g215; pole/knot coordinates omitted)
    g215: BSplineCurve PolesCount=9 KnotsCount=7 Degree=3 IsPeriodic=0
    g216-g222: GeomPoint x7 (B-spline internal-alignment scaffolding for g215; pole/knot coordinates omitted)
    g223-g232: Circle x10 (B-spline internal-alignment scaffolding for g233; pole/knot coordinates omitted)
    g233: BSplineCurve PolesCount=10 KnotsCount=8 Degree=3 IsPeriodic=0
    g234-g241: GeomPoint x8 (B-spline internal-alignment scaffolding for g233; pole/knot coordinates omitted)
    g242: LineSegment StartX=-1.58923 StartY=21.0696 StartZ=0 EndX=2.62034 EndY=21.0696 EndZ=0
    g243: LineSegment StartX=-1.55856 StartY=18.7342 StartZ=0 EndX=6.45946 EndY=18.7342 EndZ=0
    g244: LineSegment StartX=5.29231 StartY=17.386 StartZ=0 EndX=5.29231 EndY=14.3674 EndZ=0
    g245-g269: Circle x25 (B-spline internal-alignment scaffolding for g270; pole/knot coordinates omitted)
    g270: BSplineCurve PolesCount=25 KnotsCount=23 Degree=3 IsPeriodic=0
    g271-g293: GeomPoint x23 (B-spline internal-alignment scaffolding for g270; pole/knot coordinates omitted)
    g294-g304: Circle x11 (B-spline internal-alignment scaffolding for g305; pole/knot coordinates omitted)
    g305: BSplineCurve PolesCount=11 KnotsCount=9 Degree=3 IsPeriodic=0
    g306-g314: GeomPoint x9 (B-spline internal-alignment scaffolding for g305; pole/knot coordinates omitted)
    g315-g326: Circle x12 (B-spline internal-alignment scaffolding for g327; pole/knot coordinates omitted)
    g327: BSplineCurve PolesCount=12 KnotsCount=10 Degree=3 IsPeriodic=0
    g328-g337: GeomPoint x10 (B-spline internal-alignment scaffolding for g327; pole/knot coordinates omitted)
  constraints (252):
    c: Coincident(g1,g0)
    c: Horizontal(g0)
    c: Vertical(g1)
    c: Coincident(g2,g3)
    c: Coincident(g3,g4)
    c: Horizontal(g4)
    c: Horizontal(g2)
    c: Vertical(g3)
    c: Block(g1)
    c: Distance(g3) = 4.86
    c: Block(g4)
    c: Distance(g0) = 10.8
    c: Distance(g2) = 10.8
    c: Coincident(g5,g0)
    c: Coincident(g6,g4)
    c: Coincident(g6,g2)
    c: Block(g8)
    c: Block(g7)
    c: Coincident(g9,g8)
    c: Coincident(g9,g7)
    c: Vertical(g9)
    c: Coincident(g10,g7)
    c: Coincident(g10,g8)
    c: Vertical(g10)
    c: Weight(g11) = 1
    c: Equal(g11, g12-g21) x10
    c: InternalAlignment(g11-g21 -> g22) x11
    c: InternalAlignment(g23-g31 -> g22) x9
    c: Block(g22)
    c: Weight(g32) = 1
    c: Equal(g32, g33-g49) x17
    c: InternalAlignment(g32-g49 -> g50) x18
    c: InternalAlignment(g51-g66 -> g50) x16
    c: Block(g50)
    c: Coincident(g67,g50)
    c: Coincident(g67,g22)
    c: Coincident(g68,g22)
    c: Coincident(g68,g50)
    c: InternalAlignment(g70,g69)
    c: InternalAlignment(g71,g69)
    c: Block(g69)
    c: InternalAlignment(g73,g72)
    c: InternalAlignment(g74,g72)
    c: Block(g72)
    c: InternalAlignment(g76,g75)
    c: InternalAlignment(g77,g75)
    c: InternalAlignment(g78,g80)
    c: InternalAlignment(g79,g80)
    c: Block(g80)
    c: Coincident(g75,g80)
    c: Block(g75)
    c: InternalAlignment(g82,g81)
    c: InternalAlignment(g83,g81)
    c: InternalAlignment(g84,g86)
    c: InternalAlignment(g85,g86)
    c: Block(g86)
    c: Coincident(g81,g86)
    c: Block(g81)
    c: Horizontal(g87)
    c: Block(g87)
    c: Horizontal(g88)
    c: Distance(g88) = 4.14
    c: Horizontal(g89)
    c: Equal(g88,g89) = 4.14
    c: Block(g89)
    c: Block(g88)
    c: Coincident(g90,g87)
    c: Vertical(g90)
    c: Distance(g90) = 11.88
    c: Coincident(g91,g90)
    c: Horizontal(g91)
    c: Coincident(g92,g91)
    c: Vertical(g92)
    c: Distance(g91) = 4.03
    c: Distance(g92) = 1.9
    c: Coincident(g93,g87)
    c: Vertical(g93)
    c: Vertical(g94)
    c: Coincident(g94,g88)
    c: Distance(g93) = 5.8
    c: Distance(g94) = 5.8
    c: Vertical(g95)
    c: Coincident(g95,g88)
    c: Distance(g95) = 6.9
    c: Coincident(g107,g92)
    c: Weight(g96) = 1
    c: Equal(g96, g97-g106) x10
    c: InternalAlignment(g96-g106 -> g107) x11
    c: InternalAlignment(g108-g116 -> g107) x9
    c: Block(g107)
    c: Block(g117)
    c: Coincident(g126,g93)
    c: Weight(g118) = 1
    c: Equal(g118, g119-g125) x7
    c: Coincident(g126,g95)
    c: InternalAlignment(g118-g125 -> g126) x8
    c: InternalAlignment(g127-g132 -> g126) x6
    c: Coincident(g133,g94)
    c: Block(g126)
    c: Block(g133)
    c: Coincident(g134,g133)
    c: Coincident(g134,g89)
    c: Vertical(g134)
    c: Horizontal(g135)
    c: Block(g135)
    c: Horizontal(g136)
    c: Equal(g88,g136) = 4.14
    c: Horizontal(g137)
    c: Equal(g136,g137) = 4.14
    c: Block(g137)
    c: Block(g136)
    c: Coincident(g138,g135)
    c: Vertical(g138)
    c: Equal(g90,g138) = 11.88
    c: Coincident(g139,g138)
    c: Horizontal(g139)
    c: Coincident(g140,g139)
    c: Vertical(g140)
    c: Equal(g91,g139) = 4.03
    c: Equal(g92,g140) = 1.9
    c: Coincident(g141,g135)
    c: Vertical(g141)
    c: Vertical(g142)
    c: Coincident(g142,g136)
    c: Equal(g93,g141) = 5.8
    c: Equal(g94,g142) = 5.8
    c: Vertical(g143)
    c: Coincident(g143,g136)
    c: Equal(g95,g143) = 6.9
    c: Coincident(g149,g140)
    c: Equal(g96,g144) = 1
    c: Equal(g144, g145-g148) x4
    c: InternalAlignment(g144-g148 -> g149) x5
    c: InternalAlignment(g150-g158 -> g149) x9
    c: Block(g149)
    c: Block(g159)
    c: Coincident(g168,g141)
    c: Equal(g118,g160) = 1
    c: Equal(g160, g161-g167) x7
    c: Coincident(g168,g143)
    c: InternalAlignment(g160-g167 -> g168) x8
    c: InternalAlignment(g169-g174 -> g168) x6
    c: Coincident(g175,g142)
    c: Block(g168)
    c: Block(g175)
    c: Coincident(g176,g175)
    c: Coincident(g176,g137)
    c: Vertical(g176)
    c: Coincident(g177,g137)
    c: Vertical(g177)
    c: Coincident(g178,g177)
    c: Coincident(g178,g159)
    c: InternalAlignment(g179,g178)
    c: InternalAlignment(g180,g178)
    c: Block(g178)
    c: Vertical(g181)
    c: Coincident(g181,g89)
    c: Block(g5)
    c: Coincident(g182,g1)
    c: Coincident(g182,g5)
    c: Horizontal(g182)
    c: Coincident(g186,g117)
    c: Weight(g183) = 1
    c: Equal(g183,g184)
    c: Equal(g183,g185)
    c: Coincident(g186,g181)
    c: InternalAlignment(g183,g186)
    c: InternalAlignment(g184,g186)
    c: InternalAlignment(g185,g186)
    c: InternalAlignment(g187,g186)
    c: InternalAlignment(g188,g186)
    c: Block(g186)
    c: InternalAlignment(g190,g189)
    c: InternalAlignment(g191,g189)
    c: Block(g189)
    c: InternalAlignment(g193,g192)
    c: InternalAlignment(g194,g192)
    c: Block(g192)
    c: Horizontal(g195)
    c: Block(g195)
    c: Coincident(g196,g195)
    c: Vertical(g196)
    c: Block(g196)
    c: Distance(g195) = 3.71244
    c: Coincident(g197,g196)
    c: Horizontal(g197)
    c: Distance(g197) = 4.1
    c: Coincident(g198,g192)
    c: Coincident(g198,g197)
    c: Vertical(g198)
    c: Block(g198)
    c: Coincident(g199,g192)
    c: Coincident(g199,g195)
    c: Vertical(g199)
    c: Block(g199)
    c: Horizontal(g200)
    c: Block(g200)
    c: Coincident(g201,g200)
    c: Vertical(g201)
    c: Block(g201)
    c: Coincident(g202,g201)
    c: Horizontal(g202)
    c: Block(g202)
    c: Coincident(g203,g202)
    c: Vertical(g203)
    c: Block(g203)
    c: Coincident(g204,g200)
    c: Vertical(g204)
    c: Block(g204)
    c: Coincident(g215,g203)
    c: Weight(g206) = 1
    c: Equal(g206, g207-g214) x8
    c: Coincident(g215,g205)
    c: InternalAlignment(g206-g214 -> g215) x9
    c: InternalAlignment(g216-g222 -> g215) x7
    c: Coincident(g233,g204)
    c: Weight(g223) = 1
    c: Equal(g223, g224-g232) x9
    c: Coincident(g233,g205)
    c: InternalAlignment(g223-g232 -> g233) x10
    c: InternalAlignment(g234-g241 -> g233) x8
    c: Vertical(g205)
    c: Block(g205)
    c: Block(g215)
    c: Block(g233)
    c: Horizontal(g242)
    c: Horizontal(g243)
    c: Block(g242)
    c: Block(g243)
    c: Vertical(g244)
    c: Block(g244)
    c: Coincident(g270,g243)
    c: Weight(g245) = 1
    c: Equal(g245, g246-g269) x24
    c: Coincident(g270,g244)
    c: InternalAlignment(g245-g269 -> g270) x25
    c: InternalAlignment(g271-g293 -> g270) x23
    c: Coincident(g305,g242)
    c: Weight(g294) = 1
    c: Equal(g294, g295-g304) x10
    c: Coincident(g305,g242)
    c: InternalAlignment(g294-g304 -> g305) x11
    c: InternalAlignment(g306-g314 -> g305) x9
    c: Block(g305)
    c: Coincident(g327,g243)
    c: Weight(g315) = 1
    c: Equal(g315, g316-g326) x11
    c: Coincident(g327,g244)
    c: InternalAlignment(g315-g326 -> g327) x12
    c: InternalAlignment(g328-g337 -> g327) x10
    c: Block(g327)
    c: Block(g270)
FEATURE [PartDesign::Body] Body  label="CommodoreLogoAndText"
  Group = -> [Sketch083]
  Origin = -> Origin
FEATURE [Part::Extrusion] Extrude074  label="CommodoreLogoAndText001"
  Base = -> Sketch083
  Dir = (0,0,1)
  DirMode = 2
  FaceMakerClass = Part::FaceMakerBullseye
  LengthFwd = 10
  LengthRev = 0
  Solid = true
  Symmetric = false
FEATURE [Part::FeaturePython] Clone  label="CommodoreLogoAndTextScale"  # Draft clone (typed FeaturePython)
  AttacherType = Attacher::AttachEngine3D
  Fuse = false
  Objects = -> [Extrude074]
  Placement = pos=(111,5.37,-11.6) rot=(0,0,1;0rad)
  Scale = (0.62,0.62,1)
FEATURE [Part::Mirroring] Part__Mirroring  label="CommodoreLogoAndTextScale (Mirror #1)"
  Base = (0,0,0)
  Normal = (1,0,0)
  Placement = pos=(123.576,0,0) rot=(0,0,1;0rad)
  Source = -> Clone
FEATURE [Sketcher::SketchObject] Sketch084
  FullyConstrained = true
  MapMode = 5
  Support = -> [XY_Plane001]
  sketch-geometry (338):
    g0: LineSegment StartX=-151.619 StartY=28.8932 StartZ=0 EndX=-140.819 EndY=28.8932 EndZ=0
    g1: LineSegment StartX=-151.619 StartY=24.0313 StartZ=0 EndX=-151.619 EndY=28.8932 EndZ=0
    g2: LineSegment StartX=-140.819 StartY=17.7713 StartZ=0 EndX=-151.619 EndY=17.7713 EndZ=0
    g3: LineSegment StartX=-151.619 StartY=17.7713 StartZ=0 EndX=-151.619 EndY=22.6313 EndZ=0
    g4: LineSegment StartX=-151.619 StartY=22.6313 StartZ=0 EndX=-145.128 EndY=22.6313 EndZ=0
    g5: LineSegment StartX=-145.128 StartY=24.0313 StartZ=0 EndX=-140.819 EndY=28.8932 EndZ=0
    g6: LineSegment StartX=-145.128 StartY=22.6313 StartZ=0 EndX=-140.819 EndY=17.7713 EndZ=0
    g7: ArcOfCircle CenterX=-155.157 CenterY=23.3323 CenterZ=0 NormalX=0 NormalY=0 NormalZ=1 AngleXU=0 Radius=6.92354 StartAngle=1.03434 EndAngle=5.24885
    g8: ArcOfCircle CenterX=-155.157 CenterY=23.3323 CenterZ=0 NormalX=0 NormalY=0 NormalZ=1 AngleXU=0 Radius=12.6269 StartAngle=1.28675 EndAngle=4.99643
    g9: LineSegment StartX=-151.619 StartY=35.4532 StartZ=0 EndX=-151.619 EndY=29.2832 EndZ=0
    g10: LineSegment StartX=-151.619 StartY=17.3813 StartZ=0 EndX=-151.619 EndY=11.2113 EndZ=0
    g11-g21: Circle x11 (B-spline internal-alignment scaffolding for g22; pole/knot coordinates omitted)
    g22: BSplineCurve PolesCount=11 KnotsCount=9 Degree=3 IsPeriodic=0
    g23-g31: GeomPoint x9 (B-spline internal-alignment scaffolding for g22; pole/knot coordinates omitted)
    g32-g49: Circle x18 (B-spline internal-alignment scaffolding for g50; pole/knot coordinates omitted)
    g50: BSplineCurve PolesCount=18 KnotsCount=16 Degree=3 IsPeriodic=0
    g51-g66: GeomPoint x16 (B-spline internal-alignment scaffolding for g50; pole/knot coordinates omitted)
    g67: LineSegment StartX=-117.124 StartY=30.093 StartZ=0 EndX=-117.603 EndY=26.5272 EndZ=0
    g68: LineSegment StartX=-117.603 StartY=17.8472 StartZ=0 EndX=-117.124 EndY=14.2659 EndZ=0
    g69: Ellipse CenterX=-109.671 CenterY=20.025 CenterZ=0 NormalX=0 NormalY=0 NormalZ=1 MajorRadius=3.34798 MinorRadius=2.71052 AngleXU=-1.56793
    g70: GeomPoint X=-109.666 Y=18.0598 Z=0
    g71: GeomPoint X=-109.677 Y=21.9902 Z=0
    g72: Ellipse CenterX=-109.671 CenterY=20.0123 CenterZ=0 NormalX=0 NormalY=0 NormalZ=1 MajorRadius=6.93002 MinorRadius=6.36273 AngleXU=-3.13976
    g73: GeomPoint X=-112.417 Y=20.0073 Z=0
    g74: GeomPoint X=-106.925 Y=20.0173 Z=0
    g75: Ellipse CenterX=-51.7682 CenterY=20.1463 CenterZ=0 NormalX=0 NormalY=0 NormalZ=1 MajorRadius=3.19279 MinorRadius=2.71052 AngleXU=-1.52774
    g76: GeomPoint X=-51.6955 Y=18.4606 Z=0
    g77: GeomPoint X=-51.8408 Y=21.832 Z=0
    g78: GeomPoint X=-54.5142 Y=20.1413 Z=0
    g79: GeomPoint X=-49.0221 Y=20.1513 Z=0
    g80: Ellipse CenterX=-51.7682 CenterY=20.1463 CenterZ=0 NormalX=0 NormalY=0 NormalZ=1 MajorRadius=6.93002 MinorRadius=6.36273 AngleXU=-3.13976
    g81: Ellipse CenterX=-22.8436 CenterY=20.1783 CenterZ=0 NormalX=0 NormalY=0 NormalZ=1 MajorRadius=3.31512 MinorRadius=2.71052 AngleXU=-1.60214
    g82: GeomPoint X=-22.9034 Y=18.2706 Z=0
    g83: GeomPoint X=-22.7838 Y=22.0861 Z=0
    g84: GeomPoint X=-25.5897 Y=20.1733 Z=0
    g85: GeomPoint X=-20.0976 Y=20.1833 Z=0
    g86: Ellipse CenterX=-22.8436 CenterY=20.1783 CenterZ=0 NormalX=0 NormalY=0 NormalZ=1 MajorRadius=6.93002 MinorRadius=6.36273 AngleXU=-3.13976
    g87: LineSegment StartX=-101.889 StartY=14.1107 StartZ=0 EndX=-97.7455 EndY=14.1107 EndZ=0
    g88: LineSegment StartX=-93.8155 StartY=14.1107 StartZ=0 EndX=-89.6755 EndY=14.1107 EndZ=0
    g89: LineSegment StartX=-85.7455 StartY=14.1107 StartZ=0 EndX=-81.6055 EndY=14.1107 EndZ=0
    g90: LineSegment StartX=-101.889 StartY=14.1107 StartZ=0 EndX=-101.889 EndY=25.9907 EndZ=0
    g91: LineSegment StartX=-101.889 StartY=25.9907 StartZ=0 EndX=-97.8594 EndY=25.9907 EndZ=0
    g92: LineSegment StartX=-97.8594 StartY=25.9907 StartZ=0 EndX=-97.8594 EndY=24.0907 EndZ=0
    g93: LineSegment StartX=-97.7455 StartY=14.1107 StartZ=0 EndX=-97.7455 EndY=19.9107 EndZ=0
    g94: LineSegment StartX=-89.6755 StartY=14.1107 StartZ=0 EndX=-89.6755 EndY=19.9107 EndZ=0
    g95: LineSegment StartX=-93.8155 StartY=14.1107 StartZ=0 EndX=-93.8155 EndY=21.0107 EndZ=0
    g96-g106: Circle x11 (B-spline internal-alignment scaffolding for g107; pole/knot coordinates omitted)
    g107: BSplineCurve PolesCount=11 KnotsCount=9 Degree=3 IsPeriodic=0
    g108-g116: GeomPoint x9 (B-spline internal-alignment scaffolding for g107; pole/knot coordinates omitted)
    g117: BSplineCurve PolesCount=11 KnotsCount=9 Degree=3 IsPeriodic=0
    g118-g125: Circle x8 (B-spline internal-alignment scaffolding for g126; pole/knot coordinates omitted)
    g126: BSplineCurve PolesCount=8 KnotsCount=6 Degree=3 IsPeriodic=0
    g127-g132: GeomPoint x6 (B-spline internal-alignment scaffolding for g126; pole/knot coordinates omitted)
    g133: BSplineCurve PolesCount=8 KnotsCount=6 Degree=3 IsPeriodic=0
    g134: LineSegment StartX=-85.7455 StartY=21.0107 StartZ=0 EndX=-85.7455 EndY=14.1107 EndZ=0
    g135: LineSegment StartX=-80.0879 StartY=14.1107 StartZ=0 EndX=-75.944 EndY=14.1107 EndZ=0
    g136: LineSegment StartX=-72.014 StartY=14.1107 StartZ=0 EndX=-67.874 EndY=14.1107 EndZ=0
    g137: LineSegment StartX=-63.944 StartY=14.1107 StartZ=0 EndX=-59.804 EndY=14.1107 EndZ=0
    g138: LineSegment StartX=-80.0879 StartY=14.1107 StartZ=0 EndX=-80.0879 EndY=25.9907 EndZ=0
    g139: LineSegment StartX=-80.0879 StartY=25.9907 StartZ=0 EndX=-76.0579 EndY=25.9907 EndZ=0
    g140: LineSegment StartX=-76.0579 StartY=25.9907 StartZ=0 EndX=-76.0579 EndY=24.0907 EndZ=0
    g141: LineSegment StartX=-75.944 StartY=14.1107 StartZ=0 EndX=-75.944 EndY=19.9107 EndZ=0
    g142: LineSegment StartX=-67.874 StartY=14.1107 StartZ=0 EndX=-67.874 EndY=19.9107 EndZ=0
    g143: LineSegment StartX=-72.014 StartY=14.1107 StartZ=0 EndX=-72.014 EndY=21.0107 EndZ=0
    g144-g148: Circle x5 (B-spline internal-alignment scaffolding for g149; pole/knot coordinates omitted)
    g149: BSplineCurve PolesCount=11 KnotsCount=9 Degree=3 IsPeriodic=0
    g150-g158: GeomPoint x9 (B-spline internal-alignment scaffolding for g149; pole/knot coordinates omitted)
    g159: BSplineCurve PolesCount=11 KnotsCount=9 Degree=3 IsPeriodic=0
    g160-g167: Circle x8 (B-spline internal-alignment scaffolding for g168; pole/knot coordinates omitted)
    g168: BSplineCurve PolesCount=8 KnotsCount=6 Degree=3 IsPeriodic=0
    g169-g174: GeomPoint x6 (B-spline internal-alignment scaffolding for g168; pole/knot coordinates omitted)
    g175: BSplineCurve PolesCount=8 KnotsCount=6 Degree=3 IsPeriodic=0
    g176: LineSegment StartX=-63.944 StartY=21.0107 StartZ=0 EndX=-63.944 EndY=14.1107 EndZ=0
    g177: LineSegment StartX=-59.804 StartY=14.1107 StartZ=0 EndX=-59.804 EndY=21.5868 EndZ=0
    g178: BSplineCurve PolesCount=4 KnotsCount=2 Degree=3 IsPeriodic=0
    g179: GeomPoint X=-59.804 Y=21.5868 Z=0
    g180: GeomPoint X=-60.2379 Y=24.0907 Z=0
    g181: LineSegment StartX=-81.6055 StartY=14.1107 StartZ=0 EndX=-81.6055 EndY=21.5868 EndZ=0
    g182: LineSegment StartX=-151.619 StartY=24.0313 StartZ=0 EndX=-145.128 EndY=24.0313 EndZ=0
    g183: Circle CenterX=-82.0394 CenterY=24.0907 CenterZ=0 NormalX=0 NormalY=0 NormalZ=1 AngleXU=0 Radius=1
    g184: Circle CenterX=-81.7131 CenterY=23.2736 CenterZ=0 NormalX=0 NormalY=0 NormalZ=1 AngleXU=0 Radius=1
    g185: Circle CenterX=-81.6055 CenterY=21.5868 CenterZ=0 NormalX=0 NormalY=0 NormalZ=1 AngleXU=0 Radius=1
    g186: BSplineCurve PolesCount=3 KnotsCount=2 Degree=2 IsPeriodic=0
    g187: GeomPoint X=-82.0394 Y=24.0907 Z=0
    g188: GeomPoint X=-81.6055 Y=21.5868 Z=0
    g189: Ellipse CenterX=-37.3522 CenterY=19.9515 CenterZ=0 NormalX=0 NormalY=0 NormalZ=1 MajorRadius=2.99755 MinorRadius=2.49 AngleXU=1.5708
    g190: GeomPoint X=-37.3522 Y=21.6203 Z=0
    g191: GeomPoint X=-37.3522 Y=18.2826 Z=0
    g192: ArcOfEllipse CenterX=-38.7647 CenterY=20.06 CenterZ=0 NormalX=0 NormalY=0 NormalZ=1 MajorRadius=6.30025 MinorRadius=5.3849 AngleXU=1.57276 StartAngle=5.50632 EndAngle=10.3035
    g193: GeomPoint X=-38.7711 Y=23.3304 Z=0
    g194: GeomPoint X=-38.7583 Y=16.7895 Z=0
    g195: LineSegment StartX=-34.6109 StartY=14.1107 StartZ=0 EndX=-30.8984 EndY=14.1107 EndZ=0
    g196: LineSegment StartX=-30.8984 StartY=14.1107 StartZ=0 EndX=-30.8984 EndY=31.1784 EndZ=0
    g197: LineSegment StartX=-30.8984 StartY=31.1784 StartZ=0 EndX=-34.9984 EndY=31.1784 EndZ=0
    g198: LineSegment StartX=-34.9984 StartY=24.5602 StartZ=0 EndX=-34.9984 EndY=31.1784 EndZ=0
    g199: LineSegment StartX=-34.6109 StartY=16.0476 StartZ=0 EndX=-34.6109 EndY=14.1107 EndZ=0
    g200: LineSegment StartX=-14.8781 StartY=14.1107 StartZ=0 EndX=-10.5106 EndY=14.1107 EndZ=0
    g201: LineSegment StartX=-14.8781 StartY=14.1107 StartZ=0 EndX=-14.8781 EndY=25.8504 EndZ=0
    g202: LineSegment StartX=-14.8781 StartY=25.8504 StartZ=0 EndX=-10.8534 EndY=25.8504 EndZ=0
    g203: LineSegment StartX=-10.8534 StartY=25.8504 StartZ=0 EndX=-10.8534 EndY=24.0923 EndZ=0
    g204: LineSegment StartX=-10.5106 StartY=14.1107 StartZ=0 EndX=-10.5106 EndY=19.7752 EndZ=0
    g205: LineSegment StartX=-5.96397 StartY=25.9304 StartZ=0 EndX=-5.96397 EndY=22.574 EndZ=0
    g206-g214: Circle x9 (B-spline internal-alignment scaffolding for g215; pole/knot coordinates omitted)
    g215: BSplineCurve PolesCount=9 KnotsCount=7 Degree=3 IsPeriodic=0
    g216-g222: GeomPoint x7 (B-spline internal-alignment scaffolding for g215; pole/knot coordinates omitted)
    g223-g232: Circle x10 (B-spline internal-alignment scaffolding for g233; pole/knot coordinates omitted)
    g233: BSplineCurve PolesCount=10 KnotsCount=8 Degree=3 IsPeriodic=0
    g234-g241: GeomPoint x8 (B-spline internal-alignment scaffolding for g233; pole/knot coordinates omitted)
    g242: LineSegment StartX=-1.58923 StartY=21.0696 StartZ=0 EndX=2.62034 EndY=21.0696 EndZ=0
    g243: LineSegment StartX=-1.55856 StartY=18.7342 StartZ=0 EndX=6.45946 EndY=18.7342 EndZ=0
    g244: LineSegment StartX=5.29231 StartY=17.386 StartZ=0 EndX=5.29231 EndY=14.3674 EndZ=0
    g245-g269: Circle x25 (B-spline internal-alignment scaffolding for g270; pole/knot coordinates omitted)
    g270: BSplineCurve PolesCount=25 KnotsCount=23 Degree=3 IsPeriodic=0
    g271-g293: GeomPoint x23 (B-spline internal-alignment scaffolding for g270; pole/knot coordinates omitted)
    g294-g304: Circle x11 (B-spline internal-alignment scaffolding for g305; pole/knot coordinates omitted)
    g305: BSplineCurve PolesCount=11 KnotsCount=9 Degree=3 IsPeriodic=0
    g306-g314: GeomPoint x9 (B-spline internal-alignment scaffolding for g305; pole/knot coordinates omitted)
    g315-g326: Circle x12 (B-spline internal-alignment scaffolding for g327; pole/knot coordinates omitted)
    g327: BSplineCurve PolesCount=12 KnotsCount=10 Degree=3 IsPeriodic=0
    g328-g337: GeomPoint x10 (B-spline internal-alignment scaffolding for g327; pole/knot coordinates omitted)
  constraints (252):
    c: Coincident(g1,g0)
    c: Horizontal(g0)
    c: Vertical(g1)
    c: Coincident(g2,g3)
    c: Coincident(g3,g4)
    c: Horizontal(g4)
    c: Horizontal(g2)
    c: Vertical(g3)
    c: Block(g1)
    c: Distance(g3) = 4.86
    c: Block(g4)
    c: Distance(g0) = 10.8
    c: Distance(g2) = 10.8
    c: Coincident(g5,g0)
    c: Coincident(g6,g4)
    c: Coincident(g6,g2)
    c: Block(g8)
    c: Block(g7)
    c: Coincident(g9,g8)
    c: Coincident(g9,g7)
    c: Vertical(g9)
    c: Coincident(g10,g7)
    c: Coincident(g10,g8)
    c: Vertical(g10)
    c: Weight(g11) = 1
    c: Equal(g11, g12-g21) x10
    c: InternalAlignment(g11-g21 -> g22) x11
    c: InternalAlignment(g23-g31 -> g22) x9
    c: Block(g22)
    c: Weight(g32) = 1
    c: Equal(g32, g33-g49) x17
    c: InternalAlignment(g32-g49 -> g50) x18
    c: InternalAlignment(g51-g66 -> g50) x16
    c: Block(g50)
    c: Coincident(g67,g50)
    c: Coincident(g67,g22)
    c: Coincident(g68,g22)
    c: Coincident(g68,g50)
    c: InternalAlignment(g70,g69)
    c: InternalAlignment(g71,g69)
    c: Block(g69)
    c: InternalAlignment(g73,g72)
    c: InternalAlignment(g74,g72)
    c: Block(g72)
    c: InternalAlignment(g76,g75)
    c: InternalAlignment(g77,g75)
    c: InternalAlignment(g78,g80)
    c: InternalAlignment(g79,g80)
    c: Block(g80)
    c: Coincident(g75,g80)
    c: Block(g75)
    c: InternalAlignment(g82,g81)
    c: InternalAlignment(g83,g81)
    c: InternalAlignment(g84,g86)
    c: InternalAlignment(g85,g86)
    c: Block(g86)
    c: Coincident(g81,g86)
    c: Block(g81)
    c: Horizontal(g87)
    c: Block(g87)
    c: Horizontal(g88)
    c: Distance(g88) = 4.14
    c: Horizontal(g89)
    c: Equal(g88,g89) = 4.14
    c: Block(g89)
    c: Block(g88)
    c: Coincident(g90,g87)
    c: Vertical(g90)
    c: Distance(g90) = 11.88
    c: Coincident(g91,g90)
    c: Horizontal(g91)
    c: Coincident(g92,g91)
    c: Vertical(g92)
    c: Distance(g91) = 4.03
    c: Distance(g92) = 1.9
    c: Coincident(g93,g87)
    c: Vertical(g93)
    c: Vertical(g94)
    c: Coincident(g94,g88)
    c: Distance(g93) = 5.8
    c: Distance(g94) = 5.8
    c: Vertical(g95)
    c: Coincident(g95,g88)
    c: Distance(g95) = 6.9
    c: Coincident(g107,g92)
    c: Weight(g96) = 1
    c: Equal(g96, g97-g106) x10
    c: InternalAlignment(g96-g106 -> g107) x11
    c: InternalAlignment(g108-g116 -> g107) x9
    c: Block(g107)
    c: Block(g117)
    c: Coincident(g126,g93)
    c: Weight(g118) = 1
    c: Equal(g118, g119-g125) x7
    c: Coincident(g126,g95)
    c: InternalAlignment(g118-g125 -> g126) x8
    c: InternalAlignment(g127-g132 -> g126) x6
    c: Coincident(g133,g94)
    c: Block(g126)
    c: Block(g133)
    c: Coincident(g134,g133)
    c: Coincident(g134,g89)
    c: Vertical(g134)
    c: Horizontal(g135)
    c: Block(g135)
    c: Horizontal(g136)
    c: Equal(g88,g136) = 4.14
    c: Horizontal(g137)
    c: Equal(g136,g137) = 4.14
    c: Block(g137)
    c: Block(g136)
    c: Coincident(g138,g135)
    c: Vertical(g138)
    c: Equal(g90,g138) = 11.88
    c: Coincident(g139,g138)
    c: Horizontal(g139)
    c: Coincident(g140,g139)
    c: Vertical(g140)
    c: Equal(g91,g139) = 4.03
    c: Equal(g92,g140) = 1.9
    c: Coincident(g141,g135)
    c: Vertical(g141)
    c: Vertical(g142)
    c: Coincident(g142,g136)
    c: Equal(g93,g141) = 5.8
    c: Equal(g94,g142) = 5.8
    c: Vertical(g143)
    c: Coincident(g143,g136)
    c: Equal(g95,g143) = 6.9
    c: Coincident(g149,g140)
    c: Equal(g96,g144) = 1
    c: Equal(g144, g145-g148) x4
    c: InternalAlignment(g144-g148 -> g149) x5
    c: InternalAlignment(g150-g158 -> g149) x9
    c: Block(g149)
    c: Block(g159)
    c: Coincident(g168,g141)
    c: Equal(g118,g160) = 1
    c: Equal(g160, g161-g167) x7
    c: Coincident(g168,g143)
    c: InternalAlignment(g160-g167 -> g168) x8
    c: InternalAlignment(g169-g174 -> g168) x6
    c: Coincident(g175,g142)
    c: Block(g168)
    c: Block(g175)
    c: Coincident(g176,g175)
    c: Coincident(g176,g137)
    c: Vertical(g176)
    c: Coincident(g177,g137)
    c: Vertical(g177)
    c: Coincident(g178,g177)
    c: Coincident(g178,g159)
    c: InternalAlignment(g179,g178)
    c: InternalAlignment(g180,g178)
    c: Block(g178)
    c: Vertical(g181)
    c: Coincident(g181,g89)
    c: Block(g5)
    c: Coincident(g182,g1)
    c: Coincident(g182,g5)
    c: Horizontal(g182)
    c: Coincident(g186,g117)
    c: Weight(g183) = 1
    c: Equal(g183,g184)
    c: Equal(g183,g185)
    c: Coincident(g186,g181)
    c: InternalAlignment(g183,g186)
    c: InternalAlignment(g184,g186)
    c: InternalAlignment(g185,g186)
    c: InternalAlignment(g187,g186)
    c: InternalAlignment(g188,g186)
    c: Block(g186)
    c: InternalAlignment(g190,g189)
    c: InternalAlignment(g191,g189)
    c: Block(g189)
    c: InternalAlignment(g193,g192)
    c: InternalAlignment(g194,g192)
    c: Block(g192)
    c: Horizontal(g195)
    c: Block(g195)
    c: Coincident(g196,g195)
    c: Vertical(g196)
    c: Block(g196)
    c: Distance(g195) = 3.71244
    c: Coincident(g197,g196)
    c: Horizontal(g197)
    c: Distance(g197) = 4.1
    c: Coincident(g198,g192)
    c: Coincident(g198,g197)
    c: Vertical(g198)
    c: Block(g198)
    c: Coincident(g199,g192)
    c: Coincident(g199,g195)
    c: Vertical(g199)
    c: Block(g199)
    c: Horizontal(g200)
    c: Block(g200)
    c: Coincident(g201,g200)
    c: Vertical(g201)
    c: Block(g201)
    c: Coincident(g202,g201)
    c: Horizontal(g202)
    c: Block(g202)
    c: Coincident(g203,g202)
    c: Vertical(g203)
    c: Block(g203)
    c: Coincident(g204,g200)
    c: Vertical(g204)
    c: Block(g204)
    c: Coincident(g215,g203)
    c: Weight(g206) = 1
    c: Equal(g206, g207-g214) x8
    c: Coincident(g215,g205)
    c: InternalAlignment(g206-g214 -> g215) x9
    c: InternalAlignment(g216-g222 -> g215) x7
    c: Coincident(g233,g204)
    c: Weight(g223) = 1
    c: Equal(g223, g224-g232) x9
    c: Coincident(g233,g205)
    c: InternalAlignment(g223-g232 -> g233) x10
    c: InternalAlignment(g234-g241 -> g233) x8
    c: Vertical(g205)
    c: Block(g205)
    c: Block(g215)
    c: Block(g233)
    c: Horizontal(g242)
    c: Horizontal(g243)
    c: Block(g242)
    c: Block(g243)
    c: Vertical(g244)
    c: Block(g244)
    c: Coincident(g270,g243)
    c: Weight(g245) = 1
    c: Equal(g245, g246-g269) x24
    c: Coincident(g270,g244)
    c: InternalAlignment(g245-g269 -> g270) x25
    c: InternalAlignment(g271-g293 -> g270) x23
    c: Coincident(g305,g242)
    c: Weight(g294) = 1
    c: Equal(g294, g295-g304) x10
    c: Coincident(g305,g242)
    c: InternalAlignment(g294-g304 -> g305) x11
    c: InternalAlignment(g306-g314 -> g305) x9
    c: Block(g305)
    c: Coincident(g327,g243)
    c: Weight(g315) = 1
    c: Equal(g315, g316-g326) x11
    c: Coincident(g327,g244)
    c: InternalAlignment(g315-g326 -> g327) x12
    c: InternalAlignment(g328-g337 -> g327) x10
    c: Block(g327)
    c: Block(g270)
FEATURE [Part::Extrusion] Extrude075  label="CommodoreLogoAndText002"
  Base = -> Sketch084
  Dir = (0,0,1)
  DirMode = 2
  FaceMakerClass = Part::FaceMakerBullseye
  LengthFwd = 10
  LengthRev = 0
  Solid = true
  Symmetric = false
FEATURE [Part::FeaturePython] Clone001  label="CommodoreLogoAndTextScale001"  # Draft clone (typed FeaturePython)
  AttacherType = Attacher::AttachEngine3D
  Fuse = false
  Objects = -> [Extrude075]
  Placement = pos=(105,5.37,-11.6) rot=(0,0,1;0rad)
  Scale = (0.62,0.62,1)
FEATURE [Part::Cut] Cut073  label="sideA005"
  Base = -> Extrude002
  Tool = -> Part__Mirroring
